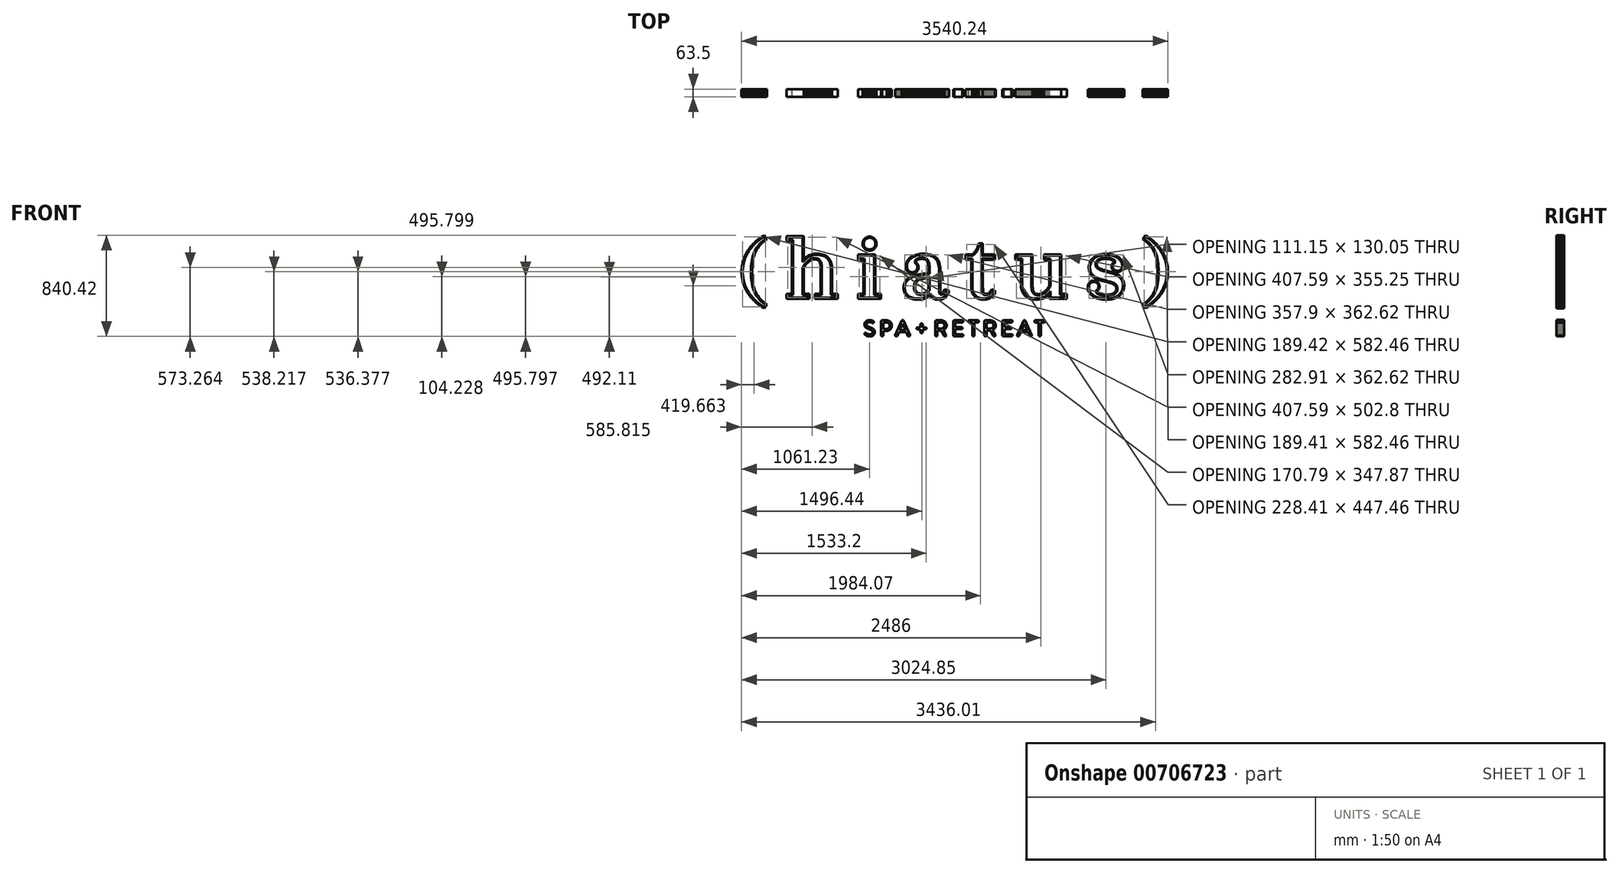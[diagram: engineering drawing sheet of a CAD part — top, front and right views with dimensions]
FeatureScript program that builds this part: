
annotation { "Feature Type Name" : "Feature", "Feature Type Description" : "" }
export const myFeature = defineFeature(function(context is Context, id is Id, definition is map)
    precondition{}
    {
        {
            var Q0;
            Q0=qCreatedBy(makeId("Front.planeOp"),FACE);
            var sketch = newSketch(context, id + "F0", { "sketchPlane" : qUnion([Q0])});
            skLineSegment(sketch, "E0", {"start": v(-2285.99, 533.4) * mm, "end": v(2285.99, 533.4) * mm});
            skLineSegment(sketch, "E1", {"start": v(2285.99, 533.4) * mm, "end": v(2285.99, -533.4) * mm});
            skLineSegment(sketch, "E2", {"start": v(2285.99, -533.4) * mm, "end": v(-2285.99, -533.4) * mm});
            skLineSegment(sketch, "E3", {"start": v(-2285.99, -533.4) * mm, "end": v(-2285.99, 533.4) * mm});
            skLineSegment(sketch, "E4", {"start": v(-1654.97, -36.78) * mm, "end": v(-1656.5, -33) * mm});
            skLineSegment(sketch, "E5", {"start": v(-1656.5, -33) * mm, "end": v(-1660.62, -21.42) * mm});
            skLineSegment(sketch, "E6", {"start": v(-1660.62, -21.42) * mm, "end": v(-1665.46, -5.14) * mm});
            skLineSegment(sketch, "E7", {"start": v(-1665.46, -5.14) * mm, "end": v(-1669.53, 12.14) * mm});
            skLineSegment(sketch, "E8", {"start": v(-1669.53, 12.14) * mm, "end": v(-1672.82, 30.5) * mm});
            skLineSegment(sketch, "E9", {"start": v(-1672.82, 30.5) * mm, "end": v(-1675.37, 50.01) * mm});
            skLineSegment(sketch, "E10", {"start": v(-1675.37, 50.01) * mm, "end": v(-1677.16, 70.78) * mm});
            skLineSegment(sketch, "E11", {"start": v(-1677.16, 70.78) * mm, "end": v(-1678.24, 92.88) * mm});
            skLineSegment(sketch, "E12", {"start": v(-1678.24, 92.88) * mm, "end": v(-1678.59, 110.52) * mm});
            skLineSegment(sketch, "E13", {"start": v(-1678.59, 110.52) * mm, "end": v(-1678.59, 116.4) * mm});
            skLineSegment(sketch, "E14", {"start": v(-1678.59, 116.4) * mm, "end": v(-1678.59, 122.28) * mm});
            skLineSegment(sketch, "E15", {"start": v(-1678.59, 122.28) * mm, "end": v(-1678.24, 139.92) * mm});
            skLineSegment(sketch, "E16", {"start": v(-1678.24, 139.92) * mm, "end": v(-1677.16, 162.02) * mm});
            skLineSegment(sketch, "E17", {"start": v(-1677.16, 162.02) * mm, "end": v(-1675.37, 182.79) * mm});
            skLineSegment(sketch, "E18", {"start": v(-1675.37, 182.79) * mm, "end": v(-1672.82, 202.3) * mm});
            skLineSegment(sketch, "E19", {"start": v(-1672.82, 202.3) * mm, "end": v(-1669.53, 220.66) * mm});
            skLineSegment(sketch, "E20", {"start": v(-1669.53, 220.66) * mm, "end": v(-1665.46, 237.93) * mm});
            skLineSegment(sketch, "E21", {"start": v(-1665.46, 237.93) * mm, "end": v(-1660.62, 254.21) * mm});
            skLineSegment(sketch, "E22", {"start": v(-1660.62, 254.21) * mm, "end": v(-1656.5, 265.78) * mm});
            skLineSegment(sketch, "E23", {"start": v(-1656.5, 265.78) * mm, "end": v(-1654.97, 269.58) * mm});
            skLineSegment(sketch, "E24", {"start": v(-1654.97, 269.58) * mm, "end": v(-1653.32, 273.65) * mm});
            skLineSegment(sketch, "E25", {"start": v(-1653.32, 273.65) * mm, "end": v(-1647.8, 285.64) * mm});
            skLineSegment(sketch, "E26", {"start": v(-1647.8, 285.64) * mm, "end": v(-1639.54, 300.96) * mm});
            skLineSegment(sketch, "E27", {"start": v(-1639.54, 300.96) * mm, "end": v(-1630.17, 315.59) * mm});
            skLineSegment(sketch, "E28", {"start": v(-1630.17, 315.59) * mm, "end": v(-1619.63, 329.58) * mm});
            skLineSegment(sketch, "E29", {"start": v(-1619.63, 329.58) * mm, "end": v(-1607.87, 343) * mm});
            skLineSegment(sketch, "E30", {"start": v(-1607.87, 343) * mm, "end": v(-1594.84, 355.9) * mm});
            skLineSegment(sketch, "E31", {"start": v(-1594.84, 355.9) * mm, "end": v(-1580.48, 368.36) * mm});
            skLineSegment(sketch, "E32", {"start": v(-1580.48, 368.36) * mm, "end": v(-1568.78, 377.52) * mm});
            skLineSegment(sketch, "E33", {"start": v(-1568.78, 377.52) * mm, "end": v(-1564.77, 380.43) * mm});
            skLineSegment(sketch, "E34", {"start": v(-1564.77, 380.43) * mm, "end": v(-1553.7, 388.45) * mm});
            skLineSegment(sketch, "E35", {"start": v(-1553.7, 388.45) * mm, "end": v(-1576.54, 420.44) * mm});
            skLineSegment(sketch, "E36", {"start": v(-1576.54, 420.44) * mm, "end": v(-1587.52, 413.6) * mm});
            skLineSegment(sketch, "E37", {"start": v(-1587.52, 413.6) * mm, "end": v(-1589.45, 412.39) * mm});
            skLineSegment(sketch, "E38", {"start": v(-1589.45, 412.39) * mm, "end": v(-1595.19, 408.71) * mm});
            skLineSegment(sketch, "E39", {"start": v(-1595.19, 408.71) * mm, "end": v(-1602.93, 403.58) * mm});
            skLineSegment(sketch, "E40", {"start": v(-1602.93, 403.58) * mm, "end": v(-1610.72, 398.2) * mm});
            skLineSegment(sketch, "E41", {"start": v(-1610.72, 398.2) * mm, "end": v(-1618.54, 392.55) * mm});
            skLineSegment(sketch, "E42", {"start": v(-1618.54, 392.55) * mm, "end": v(-1626.38, 386.65) * mm});
            skLineSegment(sketch, "E43", {"start": v(-1626.38, 386.65) * mm, "end": v(-1634.2, 380.48) * mm});
            skLineSegment(sketch, "E44", {"start": v(-1634.2, 380.48) * mm, "end": v(-1641.98, 374.05) * mm});
            skLineSegment(sketch, "E45", {"start": v(-1641.98, 374.05) * mm, "end": v(-1649.72, 367.35) * mm});
            skLineSegment(sketch, "E46", {"start": v(-1649.72, 367.35) * mm, "end": v(-1657.37, 360.37) * mm});
            skLineSegment(sketch, "E47", {"start": v(-1657.37, 360.37) * mm, "end": v(-1664.94, 353.12) * mm});
            skLineSegment(sketch, "E48", {"start": v(-1664.94, 353.12) * mm, "end": v(-1672.4, 345.59) * mm});
            skLineSegment(sketch, "E49", {"start": v(-1672.4, 345.59) * mm, "end": v(-1679.71, 337.76) * mm});
            skLineSegment(sketch, "E50", {"start": v(-1679.71, 337.76) * mm, "end": v(-1686.87, 329.66) * mm});
            skLineSegment(sketch, "E51", {"start": v(-1686.87, 329.66) * mm, "end": v(-1693.86, 321.26) * mm});
            skLineSegment(sketch, "E52", {"start": v(-1693.86, 321.26) * mm, "end": v(-1700.64, 312.57) * mm});
            skLineSegment(sketch, "E53", {"start": v(-1700.64, 312.57) * mm, "end": v(-1707.21, 303.58) * mm});
            skLineSegment(sketch, "E54", {"start": v(-1707.21, 303.58) * mm, "end": v(-1713.55, 294.29) * mm});
            skLineSegment(sketch, "E55", {"start": v(-1713.55, 294.29) * mm, "end": v(-1719.62, 284.7) * mm});
            skLineSegment(sketch, "E56", {"start": v(-1719.62, 284.7) * mm, "end": v(-1725.4, 274.8) * mm});
            skLineSegment(sketch, "E57", {"start": v(-1725.4, 274.8) * mm, "end": v(-1730.9, 264.57) * mm});
            skLineSegment(sketch, "E58", {"start": v(-1730.9, 264.57) * mm, "end": v(-1736.08, 254.04) * mm});
            skLineSegment(sketch, "E59", {"start": v(-1736.08, 254.04) * mm, "end": v(-1740.9, 243.2) * mm});
            skLineSegment(sketch, "E60", {"start": v(-1740.9, 243.2) * mm, "end": v(-1745.37, 232.02) * mm});
            skLineSegment(sketch, "E61", {"start": v(-1745.37, 232.02) * mm, "end": v(-1749.46, 220.52) * mm});
            skLineSegment(sketch, "E62", {"start": v(-1749.46, 220.52) * mm, "end": v(-1753.14, 208.7) * mm});
            skLineSegment(sketch, "E63", {"start": v(-1753.14, 208.7) * mm, "end": v(-1756.4, 196.54) * mm});
            skLineSegment(sketch, "E64", {"start": v(-1756.4, 196.54) * mm, "end": v(-1759.2, 184.04) * mm});
            skLineSegment(sketch, "E65", {"start": v(-1759.2, 184.04) * mm, "end": v(-1761.56, 171.2) * mm});
            skLineSegment(sketch, "E66", {"start": v(-1761.56, 171.2) * mm, "end": v(-1763.42, 158.03) * mm});
            skLineSegment(sketch, "E67", {"start": v(-1763.42, 158.03) * mm, "end": v(-1764.77, 144.5) * mm});
            skLineSegment(sketch, "E68", {"start": v(-1764.77, 144.5) * mm, "end": v(-1765.6, 130.63) * mm});
            skLineSegment(sketch, "E69", {"start": v(-1765.6, 130.63) * mm, "end": v(-1765.88, 119.96) * mm});
            skLineSegment(sketch, "E70", {"start": v(-1765.88, 119.96) * mm, "end": v(-1765.88, 116.4) * mm});
            skLineSegment(sketch, "E71", {"start": v(-1765.88, 116.4) * mm, "end": v(-1765.88, 112.84) * mm});
            skLineSegment(sketch, "E72", {"start": v(-1765.88, 112.84) * mm, "end": v(-1765.6, 102.17) * mm});
            skLineSegment(sketch, "E73", {"start": v(-1765.6, 102.17) * mm, "end": v(-1764.77, 88.3) * mm});
            skLineSegment(sketch, "E74", {"start": v(-1764.77, 88.3) * mm, "end": v(-1763.42, 74.77) * mm});
            skLineSegment(sketch, "E75", {"start": v(-1763.42, 74.77) * mm, "end": v(-1761.56, 61.6) * mm});
            skLineSegment(sketch, "E76", {"start": v(-1761.56, 61.6) * mm, "end": v(-1759.2, 48.76) * mm});
            skLineSegment(sketch, "E77", {"start": v(-1759.2, 48.76) * mm, "end": v(-1756.4, 36.26) * mm});
            skLineSegment(sketch, "E78", {"start": v(-1756.4, 36.26) * mm, "end": v(-1753.14, 24.1) * mm});
            skLineSegment(sketch, "E79", {"start": v(-1753.14, 24.1) * mm, "end": v(-1749.46, 12.27) * mm});
            skLineSegment(sketch, "E80", {"start": v(-1749.46, 12.27) * mm, "end": v(-1745.37, 0.78) * mm});
            skLineSegment(sketch, "E81", {"start": v(-1745.37, 0.78) * mm, "end": v(-1740.9, -10.4) * mm});
            skLineSegment(sketch, "E82", {"start": v(-1740.9, -10.4) * mm, "end": v(-1736.08, -21.25) * mm});
            skLineSegment(sketch, "E83", {"start": v(-1736.08, -21.25) * mm, "end": v(-1730.9, -31.78) * mm});
            skLineSegment(sketch, "E84", {"start": v(-1730.9, -31.78) * mm, "end": v(-1725.4, -42) * mm});
            skLineSegment(sketch, "E85", {"start": v(-1725.4, -42) * mm, "end": v(-1719.62, -51.9) * mm});
            skLineSegment(sketch, "E86", {"start": v(-1719.62, -51.9) * mm, "end": v(-1713.55, -61.5) * mm});
            skLineSegment(sketch, "E87", {"start": v(-1713.55, -61.5) * mm, "end": v(-1707.21, -70.79) * mm});
            skLineSegment(sketch, "E88", {"start": v(-1707.21, -70.79) * mm, "end": v(-1700.64, -79.78) * mm});
            skLineSegment(sketch, "E89", {"start": v(-1700.64, -79.78) * mm, "end": v(-1693.86, -88.47) * mm});
            skLineSegment(sketch, "E90", {"start": v(-1693.86, -88.47) * mm, "end": v(-1686.87, -96.87) * mm});
            skLineSegment(sketch, "E91", {"start": v(-1686.87, -96.87) * mm, "end": v(-1679.71, -104.97) * mm});
            skLineSegment(sketch, "E92", {"start": v(-1679.71, -104.97) * mm, "end": v(-1672.4, -112.8) * mm});
            skLineSegment(sketch, "E93", {"start": v(-1672.4, -112.8) * mm, "end": v(-1664.94, -120.32) * mm});
            skLineSegment(sketch, "E94", {"start": v(-1664.94, -120.32) * mm, "end": v(-1657.37, -127.58) * mm});
            skLineSegment(sketch, "E95", {"start": v(-1657.37, -127.58) * mm, "end": v(-1649.72, -134.56) * mm});
            skLineSegment(sketch, "E96", {"start": v(-1649.72, -134.56) * mm, "end": v(-1641.98, -141.26) * mm});
            skLineSegment(sketch, "E97", {"start": v(-1641.98, -141.26) * mm, "end": v(-1634.2, -147.7) * mm});
            skLineSegment(sketch, "E98", {"start": v(-1634.2, -147.7) * mm, "end": v(-1626.38, -153.86) * mm});
            skLineSegment(sketch, "E99", {"start": v(-1626.38, -153.86) * mm, "end": v(-1618.54, -159.76) * mm});
            skLineSegment(sketch, "E100", {"start": v(-1618.54, -159.76) * mm, "end": v(-1610.72, -165.4) * mm});
            skLineSegment(sketch, "E101", {"start": v(-1610.72, -165.4) * mm, "end": v(-1602.93, -170.79) * mm});
            skLineSegment(sketch, "E102", {"start": v(-1602.93, -170.79) * mm, "end": v(-1595.19, -175.92) * mm});
            skLineSegment(sketch, "E103", {"start": v(-1595.19, -175.92) * mm, "end": v(-1589.45, -179.6) * mm});
            skLineSegment(sketch, "E104", {"start": v(-1589.45, -179.6) * mm, "end": v(-1587.52, -180.8) * mm});
            skLineSegment(sketch, "E105", {"start": v(-1587.52, -180.8) * mm, "end": v(-1576.54, -187.65) * mm});
            skLineSegment(sketch, "E106", {"start": v(-1576.54, -187.65) * mm, "end": v(-1553.7, -155.66) * mm});
            skLineSegment(sketch, "E107", {"start": v(-1553.7, -155.66) * mm, "end": v(-1564.77, -147.64) * mm});
            skLineSegment(sketch, "E108", {"start": v(-1564.77, -147.64) * mm, "end": v(-1568.78, -144.73) * mm});
            skLineSegment(sketch, "E109", {"start": v(-1568.78, -144.73) * mm, "end": v(-1580.48, -135.57) * mm});
            skLineSegment(sketch, "E110", {"start": v(-1580.48, -135.57) * mm, "end": v(-1594.84, -123.11) * mm});
            skLineSegment(sketch, "E111", {"start": v(-1594.84, -123.11) * mm, "end": v(-1607.87, -110.2) * mm});
            skLineSegment(sketch, "E112", {"start": v(-1607.87, -110.2) * mm, "end": v(-1619.63, -96.78) * mm});
            skLineSegment(sketch, "E113", {"start": v(-1619.63, -96.78) * mm, "end": v(-1630.17, -82.8) * mm});
            skLineSegment(sketch, "E114", {"start": v(-1630.17, -82.8) * mm, "end": v(-1639.54, -68.17) * mm});
            skLineSegment(sketch, "E115", {"start": v(-1639.54, -68.17) * mm, "end": v(-1647.8, -52.86) * mm});
            skLineSegment(sketch, "E116", {"start": v(-1647.8, -52.86) * mm, "end": v(-1653.32, -40.86) * mm});
            skLineSegment(sketch, "E117", {"start": v(-1653.32, -40.86) * mm, "end": v(-1654.97, -36.78) * mm});
            skLineSegment(sketch, "E118", {"start": v(-1013.22, 127.47) * mm, "end": v(-1013.22, 131.72) * mm});
            skLineSegment(sketch, "E119", {"start": v(-1013.22, 131.72) * mm, "end": v(-1013.71, 144.47) * mm});
            skLineSegment(sketch, "E120", {"start": v(-1013.71, 144.47) * mm, "end": v(-1015.2, 160.34) * mm});
            skLineSegment(sketch, "E121", {"start": v(-1015.2, 160.34) * mm, "end": v(-1017.68, 175.1) * mm});
            skLineSegment(sketch, "E122", {"start": v(-1017.68, 175.1) * mm, "end": v(-1021.16, 188.72) * mm});
            skLineSegment(sketch, "E123", {"start": v(-1021.16, 188.72) * mm, "end": v(-1025.64, 201.25) * mm});
            skLineSegment(sketch, "E124", {"start": v(-1025.64, 201.25) * mm, "end": v(-1031.13, 212.66) * mm});
            skLineSegment(sketch, "E125", {"start": v(-1031.13, 212.66) * mm, "end": v(-1037.62, 222.97) * mm});
            skLineSegment(sketch, "E126", {"start": v(-1037.62, 222.97) * mm, "end": v(-1045.13, 232.18) * mm});
            skLineSegment(sketch, "E127", {"start": v(-1045.13, 232.18) * mm, "end": v(-1053.66, 240.29) * mm});
            skLineSegment(sketch, "E128", {"start": v(-1053.66, 240.29) * mm, "end": v(-1063.2, 247.3) * mm});
            skLineSegment(sketch, "E129", {"start": v(-1063.2, 247.3) * mm, "end": v(-1073.76, 253.24) * mm});
            skLineSegment(sketch, "E130", {"start": v(-1073.76, 253.24) * mm, "end": v(-1085.36, 258.07) * mm});
            skLineSegment(sketch, "E131", {"start": v(-1085.36, 258.07) * mm, "end": v(-1097.98, 261.83) * mm});
            skLineSegment(sketch, "E132", {"start": v(-1097.98, 261.83) * mm, "end": v(-1111.64, 264.5) * mm});
            skLineSegment(sketch, "E133", {"start": v(-1111.64, 264.5) * mm, "end": v(-1126.33, 266.12) * mm});
            skLineSegment(sketch, "E134", {"start": v(-1126.33, 266.12) * mm, "end": v(-1138.13, 266.65) * mm});
            skLineSegment(sketch, "E135", {"start": v(-1138.13, 266.65) * mm, "end": v(-1142.07, 266.65) * mm});
            skLineSegment(sketch, "E136", {"start": v(-1142.07, 266.65) * mm, "end": v(-1144.32, 266.65) * mm});
            skLineSegment(sketch, "E137", {"start": v(-1144.32, 266.65) * mm, "end": v(-1151.08, 266.4) * mm});
            skLineSegment(sketch, "E138", {"start": v(-1151.08, 266.4) * mm, "end": v(-1159.76, 265.7) * mm});
            skLineSegment(sketch, "E139", {"start": v(-1159.76, 265.7) * mm, "end": v(-1168.12, 264.55) * mm});
            skLineSegment(sketch, "E140", {"start": v(-1168.12, 264.55) * mm, "end": v(-1176.17, 262.98) * mm});
            skLineSegment(sketch, "E141", {"start": v(-1176.17, 262.98) * mm, "end": v(-1183.91, 261.02) * mm});
            skLineSegment(sketch, "E142", {"start": v(-1183.91, 261.02) * mm, "end": v(-1191.35, 258.7) * mm});
            skLineSegment(sketch, "E143", {"start": v(-1191.35, 258.7) * mm, "end": v(-1198.48, 256.03) * mm});
            skLineSegment(sketch, "E144", {"start": v(-1198.48, 256.03) * mm, "end": v(-1205.32, 253.05) * mm});
            skLineSegment(sketch, "E145", {"start": v(-1205.32, 253.05) * mm, "end": v(-1211.88, 249.77) * mm});
            skLineSegment(sketch, "E146", {"start": v(-1211.88, 249.77) * mm, "end": v(-1218.14, 246.22) * mm});
            skLineSegment(sketch, "E147", {"start": v(-1218.14, 246.22) * mm, "end": v(-1224.13, 242.44) * mm});
            skLineSegment(sketch, "E148", {"start": v(-1224.13, 242.44) * mm, "end": v(-1229.84, 238.43) * mm});
            skLineSegment(sketch, "E149", {"start": v(-1229.84, 238.43) * mm, "end": v(-1235.28, 234.24) * mm});
            skLineSegment(sketch, "E150", {"start": v(-1235.28, 234.24) * mm, "end": v(-1240.46, 229.87) * mm});
            skLineSegment(sketch, "E151", {"start": v(-1240.46, 229.87) * mm, "end": v(-1245.37, 225.37) * mm});
            skLineSegment(sketch, "E152", {"start": v(-1245.37, 225.37) * mm, "end": v(-1248.89, 221.93) * mm});
            skLineSegment(sketch, "E153", {"start": v(-1248.89, 221.93) * mm, "end": v(-1250.03, 220.75) * mm});
            skLineSegment(sketch, "E154", {"start": v(-1250.03, 220.75) * mm, "end": v(-1250.03, 414.2) * mm});
            skLineSegment(sketch, "E155", {"start": v(-1250.03, 414.2) * mm, "end": v(-1393.39, 414.2) * mm});
            skLineSegment(sketch, "E156", {"start": v(-1393.39, 414.2) * mm, "end": v(-1393.39, 371.91) * mm});
            skLineSegment(sketch, "E157", {"start": v(-1393.39, 371.91) * mm, "end": v(-1346.91, 371.91) * mm});
            skLineSegment(sketch, "E158", {"start": v(-1346.91, 371.91) * mm, "end": v(-1346.91, -65.34) * mm});
            skLineSegment(sketch, "E159", {"start": v(-1346.91, -65.34) * mm, "end": v(-1393.39, -65.34) * mm});
            skLineSegment(sketch, "E160", {"start": v(-1393.39, -65.34) * mm, "end": v(-1393.39, -107.64) * mm});
            skLineSegment(sketch, "E161", {"start": v(-1393.39, -107.64) * mm, "end": v(-1203.55, -107.64) * mm});
            skLineSegment(sketch, "E162", {"start": v(-1203.55, -107.64) * mm, "end": v(-1203.55, -65.34) * mm});
            skLineSegment(sketch, "E163", {"start": v(-1203.55, -65.34) * mm, "end": v(-1250.03, -65.34) * mm});
            skLineSegment(sketch, "E164", {"start": v(-1250.03, -65.34) * mm, "end": v(-1250.03, 149.07) * mm});
            skLineSegment(sketch, "E165", {"start": v(-1250.03, 149.07) * mm, "end": v(-1249.29, 150.43) * mm});
            skLineSegment(sketch, "E166", {"start": v(-1249.29, 150.43) * mm, "end": v(-1246.99, 154.45) * mm});
            skLineSegment(sketch, "E167", {"start": v(-1246.99, 154.45) * mm, "end": v(-1243.58, 160.1) * mm});
            skLineSegment(sketch, "E168", {"start": v(-1243.58, 160.1) * mm, "end": v(-1239.82, 165.93) * mm});
            skLineSegment(sketch, "E169", {"start": v(-1239.82, 165.93) * mm, "end": v(-1235.69, 171.87) * mm});
            skLineSegment(sketch, "E170", {"start": v(-1235.69, 171.87) * mm, "end": v(-1231.2, 177.83) * mm});
            skLineSegment(sketch, "E171", {"start": v(-1231.2, 177.83) * mm, "end": v(-1226.37, 183.7) * mm});
            skLineSegment(sketch, "E172", {"start": v(-1226.37, 183.7) * mm, "end": v(-1221.18, 189.44) * mm});
            skLineSegment(sketch, "E173", {"start": v(-1221.18, 189.44) * mm, "end": v(-1215.64, 194.93) * mm});
            skLineSegment(sketch, "E174", {"start": v(-1215.64, 194.93) * mm, "end": v(-1209.76, 200.09) * mm});
            skLineSegment(sketch, "E175", {"start": v(-1209.76, 200.09) * mm, "end": v(-1203.53, 204.84) * mm});
            skLineSegment(sketch, "E176", {"start": v(-1203.53, 204.84) * mm, "end": v(-1196.95, 209.1) * mm});
            skLineSegment(sketch, "E177", {"start": v(-1196.95, 209.1) * mm, "end": v(-1190.04, 212.77) * mm});
            skLineSegment(sketch, "E178", {"start": v(-1190.04, 212.77) * mm, "end": v(-1182.79, 215.77) * mm});
            skLineSegment(sketch, "E179", {"start": v(-1182.79, 215.77) * mm, "end": v(-1175.2, 218.02) * mm});
            skLineSegment(sketch, "E180", {"start": v(-1175.2, 218.02) * mm, "end": v(-1167.29, 219.44) * mm});
            skLineSegment(sketch, "E181", {"start": v(-1167.29, 219.44) * mm, "end": v(-1161.1, 219.93) * mm});
            skLineSegment(sketch, "E182", {"start": v(-1161.1, 219.93) * mm, "end": v(-1159.04, 219.93) * mm});
            skLineSegment(sketch, "E183", {"start": v(-1159.04, 219.93) * mm, "end": v(-1157.7, 219.93) * mm});
            skLineSegment(sketch, "E184", {"start": v(-1157.7, 219.93) * mm, "end": v(-1153.65, 219.78) * mm});
            skLineSegment(sketch, "E185", {"start": v(-1153.65, 219.78) * mm, "end": v(-1148.5, 219.31) * mm});
            skLineSegment(sketch, "E186", {"start": v(-1148.5, 219.31) * mm, "end": v(-1143.62, 218.47) * mm});
            skLineSegment(sketch, "E187", {"start": v(-1143.62, 218.47) * mm, "end": v(-1139, 217.2) * mm});
            skLineSegment(sketch, "E188", {"start": v(-1139, 217.2) * mm, "end": v(-1134.67, 215.47) * mm});
            skLineSegment(sketch, "E189", {"start": v(-1134.67, 215.47) * mm, "end": v(-1130.65, 213.21) * mm});
            skLineSegment(sketch, "E190", {"start": v(-1130.65, 213.21) * mm, "end": v(-1126.94, 210.38) * mm});
            skLineSegment(sketch, "E191", {"start": v(-1126.94, 210.38) * mm, "end": v(-1123.56, 206.93) * mm});
            skLineSegment(sketch, "E192", {"start": v(-1123.56, 206.93) * mm, "end": v(-1120.52, 202.81) * mm});
            skLineSegment(sketch, "E193", {"start": v(-1120.52, 202.81) * mm, "end": v(-1117.84, 197.98) * mm});
            skLineSegment(sketch, "E194", {"start": v(-1117.84, 197.98) * mm, "end": v(-1115.54, 192.37) * mm});
            skLineSegment(sketch, "E195", {"start": v(-1115.54, 192.37) * mm, "end": v(-1113.62, 185.94) * mm});
            skLineSegment(sketch, "E196", {"start": v(-1113.62, 185.94) * mm, "end": v(-1112.1, 178.65) * mm});
            skLineSegment(sketch, "E197", {"start": v(-1112.1, 178.65) * mm, "end": v(-1111, 170.44) * mm});
            skLineSegment(sketch, "E198", {"start": v(-1111, 170.44) * mm, "end": v(-1110.33, 161.26) * mm});
            skLineSegment(sketch, "E199", {"start": v(-1110.33, 161.26) * mm, "end": v(-1110.1, 153.62) * mm});
            skLineSegment(sketch, "E200", {"start": v(-1110.1, 153.62) * mm, "end": v(-1110.1, 151.07) * mm});
            skLineSegment(sketch, "E201", {"start": v(-1110.1, 151.07) * mm, "end": v(-1110.1, -65.34) * mm});
            skLineSegment(sketch, "E202", {"start": v(-1110.1, -65.34) * mm, "end": v(-1157.32, -65.34) * mm});
            skLineSegment(sketch, "E203", {"start": v(-1157.32, -65.34) * mm, "end": v(-1157.32, -107.64) * mm});
            skLineSegment(sketch, "E204", {"start": v(-1157.32, -107.64) * mm, "end": v(-966.75, -107.64) * mm});
            skLineSegment(sketch, "E205", {"start": v(-966.75, -107.64) * mm, "end": v(-966.75, -65.34) * mm});
            skLineSegment(sketch, "E206", {"start": v(-966.75, -65.34) * mm, "end": v(-1013.22, -65.34) * mm});
            skLineSegment(sketch, "E207", {"start": v(-1013.22, -65.34) * mm, "end": v(-1013.22, 127.47) * mm});
            skLineSegment(sketch, "E208", {"start": v(-656.21, 259.28) * mm, "end": v(-799.57, 259.28) * mm});
            skLineSegment(sketch, "E209", {"start": v(-799.57, 259.28) * mm, "end": v(-799.57, 216.98) * mm});
            skLineSegment(sketch, "E210", {"start": v(-799.57, 216.98) * mm, "end": v(-753.1, 216.98) * mm});
            skLineSegment(sketch, "E211", {"start": v(-753.1, 216.98) * mm, "end": v(-753.1, -65.34) * mm});
            skLineSegment(sketch, "E212", {"start": v(-753.1, -65.34) * mm, "end": v(-799.57, -65.34) * mm});
            skLineSegment(sketch, "E213", {"start": v(-799.57, -65.34) * mm, "end": v(-799.57, -107.64) * mm});
            skLineSegment(sketch, "E214", {"start": v(-799.57, -107.64) * mm, "end": v(-609.73, -107.64) * mm});
            skLineSegment(sketch, "E215", {"start": v(-609.73, -107.64) * mm, "end": v(-609.73, -65.34) * mm});
            skLineSegment(sketch, "E216", {"start": v(-609.73, -65.34) * mm, "end": v(-656.21, -65.34) * mm});
            skLineSegment(sketch, "E217", {"start": v(-656.21, -65.34) * mm, "end": v(-656.21, 259.28) * mm});
            skLineSegment(sketch, "E218", {"start": v(-702.44, 292.23) * mm, "end": v(-700.98, 292.23) * mm});
            skLineSegment(sketch, "E219", {"start": v(-700.98, 292.23) * mm, "end": v(-696.59, 292.53) * mm});
            skLineSegment(sketch, "E220", {"start": v(-696.59, 292.53) * mm, "end": v(-690.9, 293.41) * mm});
            skLineSegment(sketch, "E221", {"start": v(-690.9, 293.41) * mm, "end": v(-685.42, 294.85) * mm});
            skLineSegment(sketch, "E222", {"start": v(-685.42, 294.85) * mm, "end": v(-680.15, 296.8) * mm});
            skLineSegment(sketch, "E223", {"start": v(-680.15, 296.8) * mm, "end": v(-675.15, 299.25) * mm});
            skLineSegment(sketch, "E224", {"start": v(-675.15, 299.25) * mm, "end": v(-670.43, 302.16) * mm});
            skLineSegment(sketch, "E225", {"start": v(-670.43, 302.16) * mm, "end": v(-666.01, 305.5) * mm});
            skLineSegment(sketch, "E226", {"start": v(-666.01, 305.5) * mm, "end": v(-661.94, 309.25) * mm});
            skLineSegment(sketch, "E227", {"start": v(-661.94, 309.25) * mm, "end": v(-658.24, 313.37) * mm});
            skLineSegment(sketch, "E228", {"start": v(-658.24, 313.37) * mm, "end": v(-654.94, 317.84) * mm});
            skLineSegment(sketch, "E229", {"start": v(-654.94, 317.84) * mm, "end": v(-652.06, 322.63) * mm});
            skLineSegment(sketch, "E230", {"start": v(-652.06, 322.63) * mm, "end": v(-649.65, 327.7) * mm});
            skLineSegment(sketch, "E231", {"start": v(-649.65, 327.7) * mm, "end": v(-647.72, 333.03) * mm});
            skLineSegment(sketch, "E232", {"start": v(-647.72, 333.03) * mm, "end": v(-646.3, 338.58) * mm});
            skLineSegment(sketch, "E233", {"start": v(-646.3, 338.58) * mm, "end": v(-645.43, 344.34) * mm});
            skLineSegment(sketch, "E234", {"start": v(-645.43, 344.34) * mm, "end": v(-645.14, 348.79) * mm});
            skLineSegment(sketch, "E235", {"start": v(-645.14, 348.79) * mm, "end": v(-645.14, 350.27) * mm});
            skLineSegment(sketch, "E236", {"start": v(-645.14, 350.27) * mm, "end": v(-645.14, 351.8) * mm});
            skLineSegment(sketch, "E237", {"start": v(-645.14, 351.8) * mm, "end": v(-645.43, 356.36) * mm});
            skLineSegment(sketch, "E238", {"start": v(-645.43, 356.36) * mm, "end": v(-646.29, 362.25) * mm});
            skLineSegment(sketch, "E239", {"start": v(-646.29, 362.25) * mm, "end": v(-647.67, 367.93) * mm});
            skLineSegment(sketch, "E240", {"start": v(-647.67, 367.93) * mm, "end": v(-649.57, 373.35) * mm});
            skLineSegment(sketch, "E241", {"start": v(-649.57, 373.35) * mm, "end": v(-651.96, 378.5) * mm});
            skLineSegment(sketch, "E242", {"start": v(-651.96, 378.5) * mm, "end": v(-654.8, 383.35) * mm});
            skLineSegment(sketch, "E243", {"start": v(-654.8, 383.35) * mm, "end": v(-658.07, 387.86) * mm});
            skLineSegment(sketch, "E244", {"start": v(-658.07, 387.86) * mm, "end": v(-661.74, 392.01) * mm});
            skLineSegment(sketch, "E245", {"start": v(-661.74, 392.01) * mm, "end": v(-665.8, 395.78) * mm});
            skLineSegment(sketch, "E246", {"start": v(-665.8, 395.78) * mm, "end": v(-670.19, 399.14) * mm});
            skLineSegment(sketch, "E247", {"start": v(-670.19, 399.14) * mm, "end": v(-674.91, 402.05) * mm});
            skLineSegment(sketch, "E248", {"start": v(-674.91, 402.05) * mm, "end": v(-679.93, 404.5) * mm});
            skLineSegment(sketch, "E249", {"start": v(-679.93, 404.5) * mm, "end": v(-685.22, 406.45) * mm});
            skLineSegment(sketch, "E250", {"start": v(-685.22, 406.45) * mm, "end": v(-690.75, 407.87) * mm});
            skLineSegment(sketch, "E251", {"start": v(-690.75, 407.87) * mm, "end": v(-696.5, 408.75) * mm});
            skLineSegment(sketch, "E252", {"start": v(-696.5, 408.75) * mm, "end": v(-700.95, 409.04) * mm});
            skLineSegment(sketch, "E253", {"start": v(-700.95, 409.04) * mm, "end": v(-702.44, 409.04) * mm});
            skLineSegment(sketch, "E254", {"start": v(-702.44, 409.04) * mm, "end": v(-703.96, 409.04) * mm});
            skLineSegment(sketch, "E255", {"start": v(-703.96, 409.04) * mm, "end": v(-708.52, 408.74) * mm});
            skLineSegment(sketch, "E256", {"start": v(-708.52, 408.74) * mm, "end": v(-714.42, 407.85) * mm});
            skLineSegment(sketch, "E257", {"start": v(-714.42, 407.85) * mm, "end": v(-720.11, 406.4) * mm});
            skLineSegment(sketch, "E258", {"start": v(-720.11, 406.4) * mm, "end": v(-725.58, 404.42) * mm});
            skLineSegment(sketch, "E259", {"start": v(-725.58, 404.42) * mm, "end": v(-730.78, 401.94) * mm});
            skLineSegment(sketch, "E260", {"start": v(-730.78, 401.94) * mm, "end": v(-735.69, 399) * mm});
            skLineSegment(sketch, "E261", {"start": v(-735.69, 399) * mm, "end": v(-740.27, 395.6) * mm});
            skLineSegment(sketch, "E262", {"start": v(-740.27, 395.6) * mm, "end": v(-744.5, 391.81) * mm});
            skLineSegment(sketch, "E263", {"start": v(-744.5, 391.81) * mm, "end": v(-748.34, 387.63) * mm});
            skLineSegment(sketch, "E264", {"start": v(-748.34, 387.63) * mm, "end": v(-751.77, 383.1) * mm});
            skLineSegment(sketch, "E265", {"start": v(-751.77, 383.1) * mm, "end": v(-754.75, 378.26) * mm});
            skLineSegment(sketch, "E266", {"start": v(-754.75, 378.26) * mm, "end": v(-757.26, 373.12) * mm});
            skLineSegment(sketch, "E267", {"start": v(-757.26, 373.12) * mm, "end": v(-759.26, 367.73) * mm});
            skLineSegment(sketch, "E268", {"start": v(-759.26, 367.73) * mm, "end": v(-760.73, 362.1) * mm});
            skLineSegment(sketch, "E269", {"start": v(-760.73, 362.1) * mm, "end": v(-761.64, 356.27) * mm});
            skLineSegment(sketch, "E270", {"start": v(-761.64, 356.27) * mm, "end": v(-761.94, 351.76) * mm});
            skLineSegment(sketch, "E271", {"start": v(-761.94, 351.76) * mm, "end": v(-761.94, 350.27) * mm});
            skLineSegment(sketch, "E272", {"start": v(-761.94, 350.27) * mm, "end": v(-761.94, 348.79) * mm});
            skLineSegment(sketch, "E273", {"start": v(-761.94, 348.79) * mm, "end": v(-761.64, 344.34) * mm});
            skLineSegment(sketch, "E274", {"start": v(-761.64, 344.34) * mm, "end": v(-760.73, 338.58) * mm});
            skLineSegment(sketch, "E275", {"start": v(-760.73, 338.58) * mm, "end": v(-759.26, 333.03) * mm});
            skLineSegment(sketch, "E276", {"start": v(-759.26, 333.03) * mm, "end": v(-757.26, 327.7) * mm});
            skLineSegment(sketch, "E277", {"start": v(-757.26, 327.7) * mm, "end": v(-754.75, 322.63) * mm});
            skLineSegment(sketch, "E278", {"start": v(-754.75, 322.63) * mm, "end": v(-751.77, 317.84) * mm});
            skLineSegment(sketch, "E279", {"start": v(-751.77, 317.84) * mm, "end": v(-748.34, 313.37) * mm});
            skLineSegment(sketch, "E280", {"start": v(-748.34, 313.37) * mm, "end": v(-744.5, 309.25) * mm});
            skLineSegment(sketch, "E281", {"start": v(-744.5, 309.25) * mm, "end": v(-740.27, 305.5) * mm});
            skLineSegment(sketch, "E282", {"start": v(-740.27, 305.5) * mm, "end": v(-735.69, 302.16) * mm});
            skLineSegment(sketch, "E283", {"start": v(-735.69, 302.16) * mm, "end": v(-730.78, 299.25) * mm});
            skLineSegment(sketch, "E284", {"start": v(-730.78, 299.25) * mm, "end": v(-725.58, 296.8) * mm});
            skLineSegment(sketch, "E285", {"start": v(-725.58, 296.8) * mm, "end": v(-720.11, 294.85) * mm});
            skLineSegment(sketch, "E286", {"start": v(-720.11, 294.85) * mm, "end": v(-714.42, 293.41) * mm});
            skLineSegment(sketch, "E287", {"start": v(-714.42, 293.41) * mm, "end": v(-708.52, 292.53) * mm});
            skLineSegment(sketch, "E288", {"start": v(-708.52, 292.53) * mm, "end": v(-703.96, 292.23) * mm});
            skLineSegment(sketch, "E289", {"start": v(-703.96, 292.23) * mm, "end": v(-702.44, 292.23) * mm});
            skLineSegment(sketch, "E290", {"start": v(-213.86, -33.04) * mm, "end": v(-215.78, -35.4) * mm});
            skLineSegment(sketch, "E291", {"start": v(-215.78, -35.4) * mm, "end": v(-222.04, -42.06) * mm});
            skLineSegment(sketch, "E292", {"start": v(-222.04, -42.06) * mm, "end": v(-230.25, -49.3) * mm});
            skLineSegment(sketch, "E293", {"start": v(-230.25, -49.3) * mm, "end": v(-238.4, -54.94) * mm});
            skLineSegment(sketch, "E294", {"start": v(-238.4, -54.94) * mm, "end": v(-246.39, -59.16) * mm});
            skLineSegment(sketch, "E295", {"start": v(-246.39, -59.16) * mm, "end": v(-254.1, -62.13) * mm});
            skLineSegment(sketch, "E296", {"start": v(-254.1, -62.13) * mm, "end": v(-261.44, -64.04) * mm});
            skLineSegment(sketch, "E297", {"start": v(-261.44, -64.04) * mm, "end": v(-268.31, -65.05) * mm});
            skLineSegment(sketch, "E298", {"start": v(-268.31, -65.05) * mm, "end": v(-273.03, -65.34) * mm});
            skLineSegment(sketch, "E299", {"start": v(-273.03, -65.34) * mm, "end": v(-274.6, -65.34) * mm});
            skLineSegment(sketch, "E300", {"start": v(-274.6, -65.34) * mm, "end": v(-276.18, -65.34) * mm});
            skLineSegment(sketch, "E301", {"start": v(-276.18, -65.34) * mm, "end": v(-280.9, -65.15) * mm});
            skLineSegment(sketch, "E302", {"start": v(-280.9, -65.15) * mm, "end": v(-286.78, -64.54) * mm});
            skLineSegment(sketch, "E303", {"start": v(-286.78, -64.54) * mm, "end": v(-292.2, -63.54) * mm});
            skLineSegment(sketch, "E304", {"start": v(-292.2, -63.54) * mm, "end": v(-297.19, -62.11) * mm});
            skLineSegment(sketch, "E305", {"start": v(-297.19, -62.11) * mm, "end": v(-301.74, -60.26) * mm});
            skLineSegment(sketch, "E306", {"start": v(-301.74, -60.26) * mm, "end": v(-305.87, -58) * mm});
            skLineSegment(sketch, "E307", {"start": v(-305.87, -58) * mm, "end": v(-309.59, -55.3) * mm});
            skLineSegment(sketch, "E308", {"start": v(-309.59, -55.3) * mm, "end": v(-312.89, -52.14) * mm});
            skLineSegment(sketch, "E309", {"start": v(-312.89, -52.14) * mm, "end": v(-315.77, -48.56) * mm});
            skLineSegment(sketch, "E310", {"start": v(-315.77, -48.56) * mm, "end": v(-318.26, -44.52) * mm});
            skLineSegment(sketch, "E311", {"start": v(-318.26, -44.52) * mm, "end": v(-320.35, -40.02) * mm});
            skLineSegment(sketch, "E312", {"start": v(-320.35, -40.02) * mm, "end": v(-322.04, -35.07) * mm});
            skLineSegment(sketch, "E313", {"start": v(-322.04, -35.07) * mm, "end": v(-323.35, -29.65) * mm});
            skLineSegment(sketch, "E314", {"start": v(-323.35, -29.65) * mm, "end": v(-324.28, -23.75) * mm});
            skLineSegment(sketch, "E315", {"start": v(-324.28, -23.75) * mm, "end": v(-324.83, -17.37) * mm});
            skLineSegment(sketch, "E316", {"start": v(-324.83, -17.37) * mm, "end": v(-325.02, -12.22) * mm});
            skLineSegment(sketch, "E317", {"start": v(-325.02, -12.22) * mm, "end": v(-325.02, -10.5) * mm});
            skLineSegment(sketch, "E318", {"start": v(-325.02, -10.5) * mm, "end": v(-325.02, -8.47) * mm});
            skLineSegment(sketch, "E319", {"start": v(-325.02, -8.47) * mm, "end": v(-324.77, -2.36) * mm});
            skLineSegment(sketch, "E320", {"start": v(-324.77, -2.36) * mm, "end": v(-324, 5.19) * mm});
            skLineSegment(sketch, "E321", {"start": v(-324, 5.19) * mm, "end": v(-322.7, 12.18) * mm});
            skLineSegment(sketch, "E322", {"start": v(-322.7, 12.18) * mm, "end": v(-320.83, 18.63) * mm});
            skLineSegment(sketch, "E323", {"start": v(-320.83, 18.63) * mm, "end": v(-318.39, 24.55) * mm});
            skLineSegment(sketch, "E324", {"start": v(-318.39, 24.55) * mm, "end": v(-315.34, 29.96) * mm});
            skLineSegment(sketch, "E325", {"start": v(-315.34, 29.96) * mm, "end": v(-311.68, 34.9) * mm});
            skLineSegment(sketch, "E326", {"start": v(-311.68, 34.9) * mm, "end": v(-307.36, 39.37) * mm});
            skLineSegment(sketch, "E327", {"start": v(-307.36, 39.37) * mm, "end": v(-302.39, 43.39) * mm});
            skLineSegment(sketch, "E328", {"start": v(-302.39, 43.39) * mm, "end": v(-296.72, 46.98) * mm});
            skLineSegment(sketch, "E329", {"start": v(-296.72, 46.98) * mm, "end": v(-290.35, 50.17) * mm});
            skLineSegment(sketch, "E330", {"start": v(-290.35, 50.17) * mm, "end": v(-283.25, 52.97) * mm});
            skLineSegment(sketch, "E331", {"start": v(-283.25, 52.97) * mm, "end": v(-275.4, 55.4) * mm});
            skLineSegment(sketch, "E332", {"start": v(-275.4, 55.4) * mm, "end": v(-266.78, 57.48) * mm});
            skLineSegment(sketch, "E333", {"start": v(-266.78, 57.48) * mm, "end": v(-257.36, 59.23) * mm});
            skLineSegment(sketch, "E334", {"start": v(-257.36, 59.23) * mm, "end": v(-249.7, 60.36) * mm});
            skLineSegment(sketch, "E335", {"start": v(-249.7, 60.36) * mm, "end": v(-247.13, 60.68) * mm});
            skLineSegment(sketch, "E336", {"start": v(-247.13, 60.68) * mm, "end": v(-213.86, 64.7) * mm});
            skLineSegment(sketch, "E337", {"start": v(-213.86, 64.7) * mm, "end": v(-213.86, -33.04) * mm});
            skLineSegment(sketch, "E338", {"start": v(-86.3, -40.21) * mm, "end": v(-86.93, -42.13) * mm});
            skLineSegment(sketch, "E339", {"start": v(-86.93, -42.13) * mm, "end": v(-89.1, -47.77) * mm});
            skLineSegment(sketch, "E340", {"start": v(-89.1, -47.77) * mm, "end": v(-91.9, -53.46) * mm});
            skLineSegment(sketch, "E341", {"start": v(-91.9, -53.46) * mm, "end": v(-94.66, -57.53) * mm});
            skLineSegment(sketch, "E342", {"start": v(-94.66, -57.53) * mm, "end": v(-97.3, -60.26) * mm});
            skLineSegment(sketch, "E343", {"start": v(-97.3, -60.26) * mm, "end": v(-99.79, -61.92) * mm});
            skLineSegment(sketch, "E344", {"start": v(-99.79, -61.92) * mm, "end": v(-102.04, -62.77) * mm});
            skLineSegment(sketch, "E345", {"start": v(-102.04, -62.77) * mm, "end": v(-104.03, -63.08) * mm});
            skLineSegment(sketch, "E346", {"start": v(-104.03, -63.08) * mm, "end": v(-105.26, -63.13) * mm});
            skLineSegment(sketch, "E347", {"start": v(-105.26, -63.13) * mm, "end": v(-105.67, -63.13) * mm});
            skLineSegment(sketch, "E348", {"start": v(-105.67, -63.13) * mm, "end": v(-106.42, -63.13) * mm});
            skLineSegment(sketch, "E349", {"start": v(-106.42, -63.13) * mm, "end": v(-108.68, -62.84) * mm});
            skLineSegment(sketch, "E350", {"start": v(-108.68, -62.84) * mm, "end": v(-110.7, -62.07) * mm});
            skLineSegment(sketch, "E351", {"start": v(-110.7, -62.07) * mm, "end": v(-112.04, -60.92) * mm});
            skLineSegment(sketch, "E352", {"start": v(-112.04, -60.92) * mm, "end": v(-112.79, -59.9) * mm});
            skLineSegment(sketch, "E353", {"start": v(-112.79, -59.9) * mm, "end": v(-113, -59.53) * mm});
            skLineSegment(sketch, "E354", {"start": v(-113, -59.53) * mm, "end": v(-113.2, -59.21) * mm});
            skLineSegment(sketch, "E355", {"start": v(-113.2, -59.21) * mm, "end": v(-113.7, -58.22) * mm});
            skLineSegment(sketch, "E356", {"start": v(-113.7, -58.22) * mm, "end": v(-114.39, -56.54) * mm});
            skLineSegment(sketch, "E357", {"start": v(-114.39, -56.54) * mm, "end": v(-115.05, -54.45) * mm});
            skLineSegment(sketch, "E358", {"start": v(-115.05, -54.45) * mm, "end": v(-115.66, -51.9) * mm});
            skLineSegment(sketch, "E359", {"start": v(-115.66, -51.9) * mm, "end": v(-116.2, -48.87) * mm});
            skLineSegment(sketch, "E360", {"start": v(-116.2, -48.87) * mm, "end": v(-116.6, -45.29) * mm});
            skLineSegment(sketch, "E361", {"start": v(-116.6, -45.29) * mm, "end": v(-116.87, -41.11) * mm});
            skLineSegment(sketch, "E362", {"start": v(-116.87, -41.11) * mm, "end": v(-116.97, -37.52) * mm});
            skLineSegment(sketch, "E363", {"start": v(-116.97, -37.52) * mm, "end": v(-116.97, -36.32) * mm});
            skLineSegment(sketch, "E364", {"start": v(-116.97, -36.32) * mm, "end": v(-116.97, 131.89) * mm});
            skLineSegment(sketch, "E365", {"start": v(-116.97, 131.89) * mm, "end": v(-116.97, 136.19) * mm});
            skLineSegment(sketch, "E366", {"start": v(-116.97, 136.19) * mm, "end": v(-117.48, 149.08) * mm});
            skLineSegment(sketch, "E367", {"start": v(-117.48, 149.08) * mm, "end": v(-119.02, 164.91) * mm});
            skLineSegment(sketch, "E368", {"start": v(-119.02, 164.91) * mm, "end": v(-121.6, 179.42) * mm});
            skLineSegment(sketch, "E369", {"start": v(-121.6, 179.42) * mm, "end": v(-125.26, 192.67) * mm});
            skLineSegment(sketch, "E370", {"start": v(-125.26, 192.67) * mm, "end": v(-130, 204.71) * mm});
            skLineSegment(sketch, "E371", {"start": v(-130, 204.71) * mm, "end": v(-135.86, 215.61) * mm});
            skLineSegment(sketch, "E372", {"start": v(-135.86, 215.61) * mm, "end": v(-142.83, 225.42) * mm});
            skLineSegment(sketch, "E373", {"start": v(-142.83, 225.42) * mm, "end": v(-148.79, 232.12) * mm});
            skLineSegment(sketch, "E374", {"start": v(-148.79, 232.12) * mm, "end": v(-150.94, 234.18) * mm});
            skLineSegment(sketch, "E375", {"start": v(-150.94, 234.18) * mm, "end": v(-153.13, 236.26) * mm});
            skLineSegment(sketch, "E376", {"start": v(-153.13, 236.26) * mm, "end": v(-160.22, 241.94) * mm});
            skLineSegment(sketch, "E377", {"start": v(-160.22, 241.94) * mm, "end": v(-170.62, 248.6) * mm});
            skLineSegment(sketch, "E378", {"start": v(-170.62, 248.6) * mm, "end": v(-182.2, 254.19) * mm});
            skLineSegment(sketch, "E379", {"start": v(-182.2, 254.19) * mm, "end": v(-195, 258.72) * mm});
            skLineSegment(sketch, "E380", {"start": v(-195, 258.72) * mm, "end": v(-209.12, 262.22) * mm});
            skLineSegment(sketch, "E381", {"start": v(-209.12, 262.22) * mm, "end": v(-224.6, 264.7) * mm});
            skLineSegment(sketch, "E382", {"start": v(-224.6, 264.7) * mm, "end": v(-241.48, 266.16) * mm});
            skLineSegment(sketch, "E383", {"start": v(-241.48, 266.16) * mm, "end": v(-255.26, 266.65) * mm});
            skLineSegment(sketch, "E384", {"start": v(-255.26, 266.65) * mm, "end": v(-259.85, 266.65) * mm});
            skLineSegment(sketch, "E385", {"start": v(-259.85, 266.65) * mm, "end": v(-263.7, 266.65) * mm});
            skLineSegment(sketch, "E386", {"start": v(-263.7, 266.65) * mm, "end": v(-275.27, 266.17) * mm});
            skLineSegment(sketch, "E387", {"start": v(-275.27, 266.17) * mm, "end": v(-290.07, 264.72) * mm});
            skLineSegment(sketch, "E388", {"start": v(-290.07, 264.72) * mm, "end": v(-304.24, 262.34) * mm});
            skLineSegment(sketch, "E389", {"start": v(-304.24, 262.34) * mm, "end": v(-317.71, 259.02) * mm});
            skLineSegment(sketch, "E390", {"start": v(-317.71, 259.02) * mm, "end": v(-330.44, 254.78) * mm});
            skLineSegment(sketch, "E391", {"start": v(-330.44, 254.78) * mm, "end": v(-342.39, 249.64) * mm});
            skLineSegment(sketch, "E392", {"start": v(-342.39, 249.64) * mm, "end": v(-353.5, 243.6) * mm});
            skLineSegment(sketch, "E393", {"start": v(-353.5, 243.6) * mm, "end": v(-361.27, 238.54) * mm});
            skLineSegment(sketch, "E394", {"start": v(-361.27, 238.54) * mm, "end": v(-363.74, 236.7) * mm});
            skLineSegment(sketch, "E395", {"start": v(-363.74, 236.7) * mm, "end": v(-366.1, 234.92) * mm});
            skLineSegment(sketch, "E396", {"start": v(-366.1, 234.92) * mm, "end": v(-372.8, 229.13) * mm});
            skLineSegment(sketch, "E397", {"start": v(-372.8, 229.13) * mm, "end": v(-380.75, 220.93) * mm});
            skLineSegment(sketch, "E398", {"start": v(-380.75, 220.93) * mm, "end": v(-387.56, 212.14) * mm});
            skLineSegment(sketch, "E399", {"start": v(-387.56, 212.14) * mm, "end": v(-393.2, 202.83) * mm});
            skLineSegment(sketch, "E400", {"start": v(-393.2, 202.83) * mm, "end": v(-397.64, 193.03) * mm});
            skLineSegment(sketch, "E401", {"start": v(-397.64, 193.03) * mm, "end": v(-400.85, 182.83) * mm});
            skLineSegment(sketch, "E402", {"start": v(-400.85, 182.83) * mm, "end": v(-402.8, 172.26) * mm});
            skLineSegment(sketch, "E403", {"start": v(-402.8, 172.26) * mm, "end": v(-403.45, 164.11) * mm});
            skLineSegment(sketch, "E404", {"start": v(-403.45, 164.11) * mm, "end": v(-403.45, 161.4) * mm});
            skLineSegment(sketch, "E405", {"start": v(-403.45, 161.4) * mm, "end": v(-403.45, 159.87) * mm});
            skLineSegment(sketch, "E406", {"start": v(-403.45, 159.87) * mm, "end": v(-403.18, 155.3) * mm});
            skLineSegment(sketch, "E407", {"start": v(-403.18, 155.3) * mm, "end": v(-402.4, 149.4) * mm});
            skLineSegment(sketch, "E408", {"start": v(-402.4, 149.4) * mm, "end": v(-401.12, 143.76) * mm});
            skLineSegment(sketch, "E409", {"start": v(-401.12, 143.76) * mm, "end": v(-399.37, 138.37) * mm});
            skLineSegment(sketch, "E410", {"start": v(-399.37, 138.37) * mm, "end": v(-397.18, 133.28) * mm});
            skLineSegment(sketch, "E411", {"start": v(-397.18, 133.28) * mm, "end": v(-394.55, 128.5) * mm});
            skLineSegment(sketch, "E412", {"start": v(-394.55, 128.5) * mm, "end": v(-391.52, 124.05) * mm});
            skLineSegment(sketch, "E413", {"start": v(-391.52, 124.05) * mm, "end": v(-388.11, 119.97) * mm});
            skLineSegment(sketch, "E414", {"start": v(-388.11, 119.97) * mm, "end": v(-384.34, 116.28) * mm});
            skLineSegment(sketch, "E415", {"start": v(-384.34, 116.28) * mm, "end": v(-380.24, 113) * mm});
            skLineSegment(sketch, "E416", {"start": v(-380.24, 113) * mm, "end": v(-375.82, 110.16) * mm});
            skLineSegment(sketch, "E417", {"start": v(-375.82, 110.16) * mm, "end": v(-371.12, 107.78) * mm});
            skLineSegment(sketch, "E418", {"start": v(-371.12, 107.78) * mm, "end": v(-366.14, 105.89) * mm});
            skLineSegment(sketch, "E419", {"start": v(-366.14, 105.89) * mm, "end": v(-360.93, 104.5) * mm});
            skLineSegment(sketch, "E420", {"start": v(-360.93, 104.5) * mm, "end": v(-355.49, 103.65) * mm});
            skLineSegment(sketch, "E421", {"start": v(-355.49, 103.65) * mm, "end": v(-351.26, 103.36) * mm});
            skLineSegment(sketch, "E422", {"start": v(-351.26, 103.36) * mm, "end": v(-349.85, 103.36) * mm});
            skLineSegment(sketch, "E423", {"start": v(-349.85, 103.36) * mm, "end": v(-348.42, 103.36) * mm});
            skLineSegment(sketch, "E424", {"start": v(-348.42, 103.36) * mm, "end": v(-344.13, 103.61) * mm});
            skLineSegment(sketch, "E425", {"start": v(-344.13, 103.61) * mm, "end": v(-338.63, 104.35) * mm});
            skLineSegment(sketch, "E426", {"start": v(-338.63, 104.35) * mm, "end": v(-333.37, 105.56) * mm});
            skLineSegment(sketch, "E427", {"start": v(-333.37, 105.56) * mm, "end": v(-328.37, 107.2) * mm});
            skLineSegment(sketch, "E428", {"start": v(-328.37, 107.2) * mm, "end": v(-323.65, 109.29) * mm});
            skLineSegment(sketch, "E429", {"start": v(-323.65, 109.29) * mm, "end": v(-319.24, 111.78) * mm});
            skLineSegment(sketch, "E430", {"start": v(-319.24, 111.78) * mm, "end": v(-315.14, 114.65) * mm});
            skLineSegment(sketch, "E431", {"start": v(-315.14, 114.65) * mm, "end": v(-311.4, 117.9) * mm});
            skLineSegment(sketch, "E432", {"start": v(-311.4, 117.9) * mm, "end": v(-308, 121.5) * mm});
            skLineSegment(sketch, "E433", {"start": v(-308, 121.5) * mm, "end": v(-305.01, 125.41) * mm});
            skLineSegment(sketch, "E434", {"start": v(-305.01, 125.41) * mm, "end": v(-302.42, 129.64) * mm});
            skLineSegment(sketch, "E435", {"start": v(-302.42, 129.64) * mm, "end": v(-300.25, 134.17) * mm});
            skLineSegment(sketch, "E436", {"start": v(-300.25, 134.17) * mm, "end": v(-298.52, 138.96) * mm});
            skLineSegment(sketch, "E437", {"start": v(-298.52, 138.96) * mm, "end": v(-297.27, 144) * mm});
            skLineSegment(sketch, "E438", {"start": v(-297.27, 144) * mm, "end": v(-296.5, 149.27) * mm});
            skLineSegment(sketch, "E439", {"start": v(-296.5, 149.27) * mm, "end": v(-296.24, 153.39) * mm});
            skLineSegment(sketch, "E440", {"start": v(-296.24, 153.39) * mm, "end": v(-296.24, 154.76) * mm});
            skLineSegment(sketch, "E441", {"start": v(-296.24, 154.76) * mm, "end": v(-296.24, 156.06) * mm});
            skLineSegment(sketch, "E442", {"start": v(-296.24, 156.06) * mm, "end": v(-296.58, 159.95) * mm});
            skLineSegment(sketch, "E443", {"start": v(-296.58, 159.95) * mm, "end": v(-297.53, 164.71) * mm});
            skLineSegment(sketch, "E444", {"start": v(-297.53, 164.71) * mm, "end": v(-298.98, 169.08) * mm});
            skLineSegment(sketch, "E445", {"start": v(-298.98, 169.08) * mm, "end": v(-300.8, 173.08) * mm});
            skLineSegment(sketch, "E446", {"start": v(-300.8, 173.08) * mm, "end": v(-302.89, 176.73) * mm});
            skLineSegment(sketch, "E447", {"start": v(-302.89, 176.73) * mm, "end": v(-305.12, 180.06) * mm});
            skLineSegment(sketch, "E448", {"start": v(-305.12, 180.06) * mm, "end": v(-307.4, 183.1) * mm});
            skLineSegment(sketch, "E449", {"start": v(-307.4, 183.1) * mm, "end": v(-309.04, 185.17) * mm});
            skLineSegment(sketch, "E450", {"start": v(-309.04, 185.17) * mm, "end": v(-309.59, 185.86) * mm});
            skLineSegment(sketch, "E451", {"start": v(-309.59, 185.86) * mm, "end": v(-310.4, 186.87) * mm});
            skLineSegment(sketch, "E452", {"start": v(-310.4, 186.87) * mm, "end": v(-312.76, 189.93) * mm});
            skLineSegment(sketch, "E453", {"start": v(-312.76, 189.93) * mm, "end": v(-315.05, 193.36) * mm});
            skLineSegment(sketch, "E454", {"start": v(-315.05, 193.36) * mm, "end": v(-316.43, 196.52) * mm});
            skLineSegment(sketch, "E455", {"start": v(-316.43, 196.52) * mm, "end": v(-316.9, 198.96) * mm});
            skLineSegment(sketch, "E456", {"start": v(-316.9, 198.96) * mm, "end": v(-316.9, 199.77) * mm});
            skLineSegment(sketch, "E457", {"start": v(-316.9, 199.77) * mm, "end": v(-316.9, 200.43) * mm});
            skLineSegment(sketch, "E458", {"start": v(-316.9, 200.43) * mm, "end": v(-316.66, 202.43) * mm});
            skLineSegment(sketch, "E459", {"start": v(-316.66, 202.43) * mm, "end": v(-315.95, 204.98) * mm});
            skLineSegment(sketch, "E460", {"start": v(-315.95, 204.98) * mm, "end": v(-314.8, 207.42) * mm});
            skLineSegment(sketch, "E461", {"start": v(-314.8, 207.42) * mm, "end": v(-313.2, 209.72) * mm});
            skLineSegment(sketch, "E462", {"start": v(-313.2, 209.72) * mm, "end": v(-311.19, 211.88) * mm});
            skLineSegment(sketch, "E463", {"start": v(-311.19, 211.88) * mm, "end": v(-308.78, 213.91) * mm});
            skLineSegment(sketch, "E464", {"start": v(-308.78, 213.91) * mm, "end": v(-305.98, 215.78) * mm});
            skLineSegment(sketch, "E465", {"start": v(-305.98, 215.78) * mm, "end": v(-302.83, 217.5) * mm});
            skLineSegment(sketch, "E466", {"start": v(-302.83, 217.5) * mm, "end": v(-299.32, 219.03) * mm});
            skLineSegment(sketch, "E467", {"start": v(-299.32, 219.03) * mm, "end": v(-295.48, 220.4) * mm});
            skLineSegment(sketch, "E468", {"start": v(-295.48, 220.4) * mm, "end": v(-291.33, 221.57) * mm});
            skLineSegment(sketch, "E469", {"start": v(-291.33, 221.57) * mm, "end": v(-286.89, 222.55) * mm});
            skLineSegment(sketch, "E470", {"start": v(-286.89, 222.55) * mm, "end": v(-282.16, 223.33) * mm});
            skLineSegment(sketch, "E471", {"start": v(-282.16, 223.33) * mm, "end": v(-277.18, 223.9) * mm});
            skLineSegment(sketch, "E472", {"start": v(-277.18, 223.9) * mm, "end": v(-271.95, 224.24) * mm});
            skLineSegment(sketch, "E473", {"start": v(-271.95, 224.24) * mm, "end": v(-267.85, 224.36) * mm});
            skLineSegment(sketch, "E474", {"start": v(-267.85, 224.36) * mm, "end": v(-266.49, 224.36) * mm});
            skLineSegment(sketch, "E475", {"start": v(-266.49, 224.36) * mm, "end": v(-265.11, 224.36) * mm});
            skLineSegment(sketch, "E476", {"start": v(-265.11, 224.36) * mm, "end": v(-260.99, 224.27) * mm});
            skLineSegment(sketch, "E477", {"start": v(-260.99, 224.27) * mm, "end": v(-255.67, 223.92) * mm});
            skLineSegment(sketch, "E478", {"start": v(-255.67, 223.92) * mm, "end": v(-250.56, 223.23) * mm});
            skLineSegment(sketch, "E479", {"start": v(-250.56, 223.23) * mm, "end": v(-245.69, 222.1) * mm});
            skLineSegment(sketch, "E480", {"start": v(-245.69, 222.1) * mm, "end": v(-241.07, 220.4) * mm});
            skLineSegment(sketch, "E481", {"start": v(-241.07, 220.4) * mm, "end": v(-236.73, 218.06) * mm});
            skLineSegment(sketch, "E482", {"start": v(-236.73, 218.06) * mm, "end": v(-232.7, 214.97) * mm});
            skLineSegment(sketch, "E483", {"start": v(-232.7, 214.97) * mm, "end": v(-229, 211.04) * mm});
            skLineSegment(sketch, "E484", {"start": v(-229, 211.04) * mm, "end": v(-225.64, 206.15) * mm});
            skLineSegment(sketch, "E485", {"start": v(-225.64, 206.15) * mm, "end": v(-222.65, 200.22) * mm});
            skLineSegment(sketch, "E486", {"start": v(-222.65, 200.22) * mm, "end": v(-220.07, 193.14) * mm});
            skLineSegment(sketch, "E487", {"start": v(-220.07, 193.14) * mm, "end": v(-217.9, 184.82) * mm});
            skLineSegment(sketch, "E488", {"start": v(-217.9, 184.82) * mm, "end": v(-216.17, 175.14) * mm});
            skLineSegment(sketch, "E489", {"start": v(-216.17, 175.14) * mm, "end": v(-214.9, 164.03) * mm});
            skLineSegment(sketch, "E490", {"start": v(-214.9, 164.03) * mm, "end": v(-214.13, 151.36) * mm});
            skLineSegment(sketch, "E491", {"start": v(-214.13, 151.36) * mm, "end": v(-213.86, 140.64) * mm});
            skLineSegment(sketch, "E492", {"start": v(-213.86, 140.64) * mm, "end": v(-213.86, 137.06) * mm});
            skLineSegment(sketch, "E493", {"start": v(-213.86, 137.06) * mm, "end": v(-213.86, 107.2) * mm});
            skLineSegment(sketch, "E494", {"start": v(-213.86, 107.2) * mm, "end": v(-250.38, 102.78) * mm});
            skLineSegment(sketch, "E495", {"start": v(-250.38, 102.78) * mm, "end": v(-255.86, 102.14) * mm});
            skLineSegment(sketch, "E496", {"start": v(-255.86, 102.14) * mm, "end": v(-272.28, 99.88) * mm});
            skLineSegment(sketch, "E497", {"start": v(-272.28, 99.88) * mm, "end": v(-292.54, 96.49) * mm});
            skLineSegment(sketch, "E498", {"start": v(-292.54, 96.49) * mm, "end": v(-311.18, 92.56) * mm});
            skLineSegment(sketch, "E499", {"start": v(-311.18, 92.56) * mm, "end": v(-328.23, 88.08) * mm});
            skLineSegment(sketch, "E500", {"start": v(-328.23, 88.08) * mm, "end": v(-343.74, 83.03) * mm});
            skLineSegment(sketch, "E501", {"start": v(-343.74, 83.03) * mm, "end": v(-357.72, 77.38) * mm});
            skLineSegment(sketch, "E502", {"start": v(-357.72, 77.38) * mm, "end": v(-370.22, 71.1) * mm});
            skLineSegment(sketch, "E503", {"start": v(-370.22, 71.1) * mm, "end": v(-381.26, 64.18) * mm});
            skLineSegment(sketch, "E504", {"start": v(-381.26, 64.18) * mm, "end": v(-390.87, 56.6) * mm});
            skLineSegment(sketch, "E505", {"start": v(-390.87, 56.6) * mm, "end": v(-399.1, 48.32) * mm});
            skLineSegment(sketch, "E506", {"start": v(-399.1, 48.32) * mm, "end": v(-405.98, 39.32) * mm});
            skLineSegment(sketch, "E507", {"start": v(-405.98, 39.32) * mm, "end": v(-411.53, 29.6) * mm});
            skLineSegment(sketch, "E508", {"start": v(-411.53, 29.6) * mm, "end": v(-415.8, 19.11) * mm});
            skLineSegment(sketch, "E509", {"start": v(-415.8, 19.11) * mm, "end": v(-418.8, 7.84) * mm});
            skLineSegment(sketch, "E510", {"start": v(-418.8, 7.84) * mm, "end": v(-420.57, -4.23) * mm});
            skLineSegment(sketch, "E511", {"start": v(-420.57, -4.23) * mm, "end": v(-421.16, -13.91) * mm});
            skLineSegment(sketch, "E512", {"start": v(-421.16, -13.91) * mm, "end": v(-421.16, -17.14) * mm});
            skLineSegment(sketch, "E513", {"start": v(-421.16, -17.14) * mm, "end": v(-421.16, -19.94) * mm});
            skLineSegment(sketch, "E514", {"start": v(-421.16, -19.94) * mm, "end": v(-420.64, -28.34) * mm});
            skLineSegment(sketch, "E515", {"start": v(-420.64, -28.34) * mm, "end": v(-419.09, -38.94) * mm});
            skLineSegment(sketch, "E516", {"start": v(-419.09, -38.94) * mm, "end": v(-416.52, -48.93) * mm});
            skLineSegment(sketch, "E517", {"start": v(-416.52, -48.93) * mm, "end": v(-412.97, -58.3) * mm});
            skLineSegment(sketch, "E518", {"start": v(-412.97, -58.3) * mm, "end": v(-408.46, -67) * mm});
            skLineSegment(sketch, "E519", {"start": v(-408.46, -67) * mm, "end": v(-403, -75.04) * mm});
            skLineSegment(sketch, "E520", {"start": v(-403, -75.04) * mm, "end": v(-396.62, -82.4) * mm});
            skLineSegment(sketch, "E521", {"start": v(-396.62, -82.4) * mm, "end": v(-389.33, -89.06) * mm});
            skLineSegment(sketch, "E522", {"start": v(-389.33, -89.06) * mm, "end": v(-381.17, -95) * mm});
            skLineSegment(sketch, "E523", {"start": v(-381.17, -95) * mm, "end": v(-372.15, -100.21) * mm});
            skLineSegment(sketch, "E524", {"start": v(-372.15, -100.21) * mm, "end": v(-362.29, -104.66) * mm});
            skLineSegment(sketch, "E525", {"start": v(-362.29, -104.66) * mm, "end": v(-351.61, -108.35) * mm});
            skLineSegment(sketch, "E526", {"start": v(-351.61, -108.35) * mm, "end": v(-340.14, -111.24) * mm});
            skLineSegment(sketch, "E527", {"start": v(-340.14, -111.24) * mm, "end": v(-327.9, -113.33) * mm});
            skLineSegment(sketch, "E528", {"start": v(-327.9, -113.33) * mm, "end": v(-314.9, -114.6) * mm});
            skLineSegment(sketch, "E529", {"start": v(-314.9, -114.6) * mm, "end": v(-304.6, -115.02) * mm});
            skLineSegment(sketch, "E530", {"start": v(-304.6, -115.02) * mm, "end": v(-301.16, -115.02) * mm});
            skLineSegment(sketch, "E531", {"start": v(-301.16, -115.02) * mm, "end": v(-297.67, -115.02) * mm});
            skLineSegment(sketch, "E532", {"start": v(-297.67, -115.02) * mm, "end": v(-287.21, -114.45) * mm});
            skLineSegment(sketch, "E533", {"start": v(-287.21, -114.45) * mm, "end": v(-273.72, -112.78) * mm});
            skLineSegment(sketch, "E534", {"start": v(-273.72, -112.78) * mm, "end": v(-260.68, -109.98) * mm});
            skLineSegment(sketch, "E535", {"start": v(-260.68, -109.98) * mm, "end": v(-248.12, -106.06) * mm});
            skLineSegment(sketch, "E536", {"start": v(-248.12, -106.06) * mm, "end": v(-236.02, -101.04) * mm});
            skLineSegment(sketch, "E537", {"start": v(-236.02, -101.04) * mm, "end": v(-224.4, -94.91) * mm});
            skLineSegment(sketch, "E538", {"start": v(-224.4, -94.91) * mm, "end": v(-213.28, -87.68) * mm});
            skLineSegment(sketch, "E539", {"start": v(-213.28, -87.68) * mm, "end": v(-205.2, -81.54) * mm});
            skLineSegment(sketch, "E540", {"start": v(-205.2, -81.54) * mm, "end": v(-202.65, -79.35) * mm});
            skLineSegment(sketch, "E541", {"start": v(-202.65, -79.35) * mm, "end": v(-201.92, -80.67) * mm});
            skLineSegment(sketch, "E542", {"start": v(-201.92, -80.67) * mm, "end": v(-199.51, -84.51) * mm});
            skLineSegment(sketch, "E543", {"start": v(-199.51, -84.51) * mm, "end": v(-196.07, -89.18) * mm});
            skLineSegment(sketch, "E544", {"start": v(-196.07, -89.18) * mm, "end": v(-192.33, -93.38) * mm});
            skLineSegment(sketch, "E545", {"start": v(-192.33, -93.38) * mm, "end": v(-188.35, -97.12) * mm});
            skLineSegment(sketch, "E546", {"start": v(-188.35, -97.12) * mm, "end": v(-184.14, -100.43) * mm});
            skLineSegment(sketch, "E547", {"start": v(-184.14, -100.43) * mm, "end": v(-179.74, -103.34) * mm});
            skLineSegment(sketch, "E548", {"start": v(-179.74, -103.34) * mm, "end": v(-175.17, -105.86) * mm});
            skLineSegment(sketch, "E549", {"start": v(-175.17, -105.86) * mm, "end": v(-170.47, -108.02) * mm});
            skLineSegment(sketch, "E550", {"start": v(-170.47, -108.02) * mm, "end": v(-165.66, -109.85) * mm});
            skLineSegment(sketch, "E551", {"start": v(-165.66, -109.85) * mm, "end": v(-160.78, -111.35) * mm});
            skLineSegment(sketch, "E552", {"start": v(-160.78, -111.35) * mm, "end": v(-155.84, -112.57) * mm});
            skLineSegment(sketch, "E553", {"start": v(-155.84, -112.57) * mm, "end": v(-150.9, -113.5) * mm});
            skLineSegment(sketch, "E554", {"start": v(-150.9, -113.5) * mm, "end": v(-145.95, -114.2) * mm});
            skLineSegment(sketch, "E555", {"start": v(-145.95, -114.2) * mm, "end": v(-141.05, -114.67) * mm});
            skLineSegment(sketch, "E556", {"start": v(-141.05, -114.67) * mm, "end": v(-136.21, -114.93) * mm});
            skLineSegment(sketch, "E557", {"start": v(-136.21, -114.93) * mm, "end": v(-132.66, -115.02) * mm});
            skLineSegment(sketch, "E558", {"start": v(-132.66, -115.02) * mm, "end": v(-131.48, -115.02) * mm});
            skLineSegment(sketch, "E559", {"start": v(-131.48, -115.02) * mm, "end": v(-130.17, -115.02) * mm});
            skLineSegment(sketch, "E560", {"start": v(-130.17, -115.02) * mm, "end": v(-126.23, -114.93) * mm});
            skLineSegment(sketch, "E561", {"start": v(-126.23, -114.93) * mm, "end": v(-120.76, -114.63) * mm});
            skLineSegment(sketch, "E562", {"start": v(-120.76, -114.63) * mm, "end": v(-115.12, -114.06) * mm});
            skLineSegment(sketch, "E563", {"start": v(-115.12, -114.06) * mm, "end": v(-109.35, -113.16) * mm});
            skLineSegment(sketch, "E564", {"start": v(-109.35, -113.16) * mm, "end": v(-103.49, -111.85) * mm});
            skLineSegment(sketch, "E565", {"start": v(-103.49, -111.85) * mm, "end": v(-97.59, -110.08) * mm});
            skLineSegment(sketch, "E566", {"start": v(-97.59, -110.08) * mm, "end": v(-91.7, -107.8) * mm});
            skLineSegment(sketch, "E567", {"start": v(-91.7, -107.8) * mm, "end": v(-85.85, -104.92) * mm});
            skLineSegment(sketch, "E568", {"start": v(-85.85, -104.92) * mm, "end": v(-80.1, -101.4) * mm});
            skLineSegment(sketch, "E569", {"start": v(-80.1, -101.4) * mm, "end": v(-74.48, -97.17) * mm});
            skLineSegment(sketch, "E570", {"start": v(-74.48, -97.17) * mm, "end": v(-69.05, -92.17) * mm});
            skLineSegment(sketch, "E571", {"start": v(-69.05, -92.17) * mm, "end": v(-63.85, -86.33) * mm});
            skLineSegment(sketch, "E572", {"start": v(-63.85, -86.33) * mm, "end": v(-58.91, -79.6) * mm});
            skLineSegment(sketch, "E573", {"start": v(-58.91, -79.6) * mm, "end": v(-54.3, -71.92) * mm});
            skLineSegment(sketch, "E574", {"start": v(-54.3, -71.92) * mm, "end": v(-50.04, -63.2) * mm});
            skLineSegment(sketch, "E575", {"start": v(-50.04, -63.2) * mm, "end": v(-47.06, -55.9) * mm});
            skLineSegment(sketch, "E576", {"start": v(-47.06, -55.9) * mm, "end": v(-46.2, -53.42) * mm});
            skLineSegment(sketch, "E577", {"start": v(-46.2, -53.42) * mm, "end": v(-41.49, -40) * mm});
            skLineSegment(sketch, "E578", {"start": v(-41.49, -40) * mm, "end": v(-82.1, -27.2) * mm});
            skLineSegment(sketch, "E579", {"start": v(-82.1, -27.2) * mm, "end": v(-86.3, -40.21) * mm});
            skLineSegment(sketch, "E580", {"start": v(303.11, -40.09) * mm, "end": v(301.87, -42.07) * mm});
            skLineSegment(sketch, "E581", {"start": v(301.87, -42.07) * mm, "end": v(297.88, -47.83) * mm});
            skLineSegment(sketch, "E582", {"start": v(297.88, -47.83) * mm, "end": v(292.83, -54.03) * mm});
            skLineSegment(sketch, "E583", {"start": v(292.83, -54.03) * mm, "end": v(287.9, -58.83) * mm});
            skLineSegment(sketch, "E584", {"start": v(287.9, -58.83) * mm, "end": v(283.05, -62.4) * mm});
            skLineSegment(sketch, "E585", {"start": v(283.05, -62.4) * mm, "end": v(278.22, -64.9) * mm});
            skLineSegment(sketch, "E586", {"start": v(278.22, -64.9) * mm, "end": v(273.32, -66.48) * mm});
            skLineSegment(sketch, "E587", {"start": v(273.32, -66.48) * mm, "end": v(268.32, -67.31) * mm});
            skLineSegment(sketch, "E588", {"start": v(268.32, -67.31) * mm, "end": v(264.43, -67.56) * mm});
            skLineSegment(sketch, "E589", {"start": v(264.43, -67.56) * mm, "end": v(263.13, -67.56) * mm});
            skLineSegment(sketch, "E590", {"start": v(263.13, -67.56) * mm, "end": v(262.47, -67.56) * mm});
            skLineSegment(sketch, "E591", {"start": v(262.47, -67.56) * mm, "end": v(260.5, -67.5) * mm});
            skLineSegment(sketch, "E592", {"start": v(260.5, -67.5) * mm, "end": v(257.93, -67.3) * mm});
            skLineSegment(sketch, "E593", {"start": v(257.93, -67.3) * mm, "end": v(255.46, -66.88) * mm});
            skLineSegment(sketch, "E594", {"start": v(255.46, -66.88) * mm, "end": v(253.13, -66.19) * mm});
            skLineSegment(sketch, "E595", {"start": v(253.13, -66.19) * mm, "end": v(250.92, -65.17) * mm});
            skLineSegment(sketch, "E596", {"start": v(250.92, -65.17) * mm, "end": v(248.83, -63.76) * mm});
            skLineSegment(sketch, "E597", {"start": v(248.83, -63.76) * mm, "end": v(246.88, -61.9) * mm});
            skLineSegment(sketch, "E598", {"start": v(246.88, -61.9) * mm, "end": v(245.1, -59.52) * mm});
            skLineSegment(sketch, "E599", {"start": v(245.1, -59.52) * mm, "end": v(243.47, -56.58) * mm});
            skLineSegment(sketch, "E600", {"start": v(243.47, -56.58) * mm, "end": v(242.05, -53) * mm});
            skLineSegment(sketch, "E601", {"start": v(242.05, -53) * mm, "end": v(240.8, -48.73) * mm});
            skLineSegment(sketch, "E602", {"start": v(240.8, -48.73) * mm, "end": v(239.74, -43.72) * mm});
            skLineSegment(sketch, "E603", {"start": v(239.74, -43.72) * mm, "end": v(238.93, -37.89) * mm});
            skLineSegment(sketch, "E604", {"start": v(238.93, -37.89) * mm, "end": v(238.32, -31.19) * mm});
            skLineSegment(sketch, "E605", {"start": v(238.32, -31.19) * mm, "end": v(237.94, -23.55) * mm});
            skLineSegment(sketch, "E606", {"start": v(237.94, -23.55) * mm, "end": v(237.8, -17.08) * mm});
            skLineSegment(sketch, "E607", {"start": v(237.8, -17.08) * mm, "end": v(237.8, -14.93) * mm});
            skLineSegment(sketch, "E608", {"start": v(237.8, -14.93) * mm, "end": v(237.8, 216.98) * mm});
            skLineSegment(sketch, "E609", {"start": v(237.8, 216.98) * mm, "end": v(337.4, 216.98) * mm});
            skLineSegment(sketch, "E610", {"start": v(337.4, 216.98) * mm, "end": v(337.4, 259.28) * mm});
            skLineSegment(sketch, "E611", {"start": v(337.4, 259.28) * mm, "end": v(237.8, 259.28) * mm});
            skLineSegment(sketch, "E612", {"start": v(237.8, 259.28) * mm, "end": v(237.8, 351.5) * mm});
            skLineSegment(sketch, "E613", {"start": v(237.8, 351.5) * mm, "end": v(201.55, 351.5) * mm});
            skLineSegment(sketch, "E614", {"start": v(201.55, 351.5) * mm, "end": v(198.9, 341.12) * mm});
            skLineSegment(sketch, "E615", {"start": v(198.9, 341.12) * mm, "end": v(198.1, 338) * mm});
            skLineSegment(sketch, "E616", {"start": v(198.1, 338) * mm, "end": v(195.28, 328.72) * mm});
            skLineSegment(sketch, "E617", {"start": v(195.28, 328.72) * mm, "end": v(190.87, 316.82) * mm});
            skLineSegment(sketch, "E618", {"start": v(190.87, 316.82) * mm, "end": v(185.71, 305.5) * mm});
            skLineSegment(sketch, "E619", {"start": v(185.71, 305.5) * mm, "end": v(179.84, 294.79) * mm});
            skLineSegment(sketch, "E620", {"start": v(179.84, 294.79) * mm, "end": v(173.28, 284.75) * mm});
            skLineSegment(sketch, "E621", {"start": v(173.28, 284.75) * mm, "end": v(166.07, 275.46) * mm});
            skLineSegment(sketch, "E622", {"start": v(166.07, 275.46) * mm, "end": v(158.26, 266.95) * mm});
            skLineSegment(sketch, "E623", {"start": v(158.26, 266.95) * mm, "end": v(152.04, 261.1) * mm});
            skLineSegment(sketch, "E624", {"start": v(152.04, 261.1) * mm, "end": v(149.86, 259.28) * mm});
            skLineSegment(sketch, "E625", {"start": v(149.86, 259.28) * mm, "end": v(94.46, 259.28) * mm});
            skLineSegment(sketch, "E626", {"start": v(94.46, 259.28) * mm, "end": v(94.46, 216.98) * mm});
            skLineSegment(sketch, "E627", {"start": v(94.46, 216.98) * mm, "end": v(140.93, 216.98) * mm});
            skLineSegment(sketch, "E628", {"start": v(140.93, 216.98) * mm, "end": v(140.93, -5.34) * mm});
            skLineSegment(sketch, "E629", {"start": v(140.93, -5.34) * mm, "end": v(140.93, -8.6) * mm});
            skLineSegment(sketch, "E630", {"start": v(140.93, -8.6) * mm, "end": v(141.36, -18.4) * mm});
            skLineSegment(sketch, "E631", {"start": v(141.36, -18.4) * mm, "end": v(142.65, -30.65) * mm});
            skLineSegment(sketch, "E632", {"start": v(142.65, -30.65) * mm, "end": v(144.8, -42.1) * mm});
            skLineSegment(sketch, "E633", {"start": v(144.8, -42.1) * mm, "end": v(147.79, -52.75) * mm});
            skLineSegment(sketch, "E634", {"start": v(147.79, -52.75) * mm, "end": v(151.62, -62.57) * mm});
            skLineSegment(sketch, "E635", {"start": v(151.62, -62.57) * mm, "end": v(156.29, -71.57) * mm});
            skLineSegment(sketch, "E636", {"start": v(156.29, -71.57) * mm, "end": v(161.79, -79.75) * mm});
            skLineSegment(sketch, "E637", {"start": v(161.79, -79.75) * mm, "end": v(168.1, -87.09) * mm});
            skLineSegment(sketch, "E638", {"start": v(168.1, -87.09) * mm, "end": v(175.25, -93.58) * mm});
            skLineSegment(sketch, "E639", {"start": v(175.25, -93.58) * mm, "end": v(183.2, -99.23) * mm});
            skLineSegment(sketch, "E640", {"start": v(183.2, -99.23) * mm, "end": v(191.96, -104.03) * mm});
            skLineSegment(sketch, "E641", {"start": v(191.96, -104.03) * mm, "end": v(201.52, -107.97) * mm});
            skLineSegment(sketch, "E642", {"start": v(201.52, -107.97) * mm, "end": v(211.88, -111.04) * mm});
            skLineSegment(sketch, "E643", {"start": v(211.88, -111.04) * mm, "end": v(223.03, -113.25) * mm});
            skLineSegment(sketch, "E644", {"start": v(223.03, -113.25) * mm, "end": v(234.94, -114.57) * mm});
            skLineSegment(sketch, "E645", {"start": v(234.94, -114.57) * mm, "end": v(244.46, -115.02) * mm});
            skLineSegment(sketch, "E646", {"start": v(244.46, -115.02) * mm, "end": v(247.66, -115.02) * mm});
            skLineSegment(sketch, "E647", {"start": v(247.66, -115.02) * mm, "end": v(251.22, -115.02) * mm});
            skLineSegment(sketch, "E648", {"start": v(251.22, -115.02) * mm, "end": v(261.89, -114.14) * mm});
            skLineSegment(sketch, "E649", {"start": v(261.89, -114.14) * mm, "end": v(275.4, -111.54) * mm});
            skLineSegment(sketch, "E650", {"start": v(275.4, -111.54) * mm, "end": v(288.1, -107.23) * mm});
            skLineSegment(sketch, "E651", {"start": v(288.1, -107.23) * mm, "end": v(300.01, -101.24) * mm});
            skLineSegment(sketch, "E652", {"start": v(300.01, -101.24) * mm, "end": v(311.01, -93.6) * mm});
            skLineSegment(sketch, "E653", {"start": v(311.01, -93.6) * mm, "end": v(321.15, -84.3) * mm});
            skLineSegment(sketch, "E654", {"start": v(321.15, -84.3) * mm, "end": v(330.32, -73.41) * mm});
            skLineSegment(sketch, "E655", {"start": v(330.32, -73.41) * mm, "end": v(336.64, -64.15) * mm});
            skLineSegment(sketch, "E656", {"start": v(336.64, -64.15) * mm, "end": v(338.5, -60.93) * mm});
            skLineSegment(sketch, "E657", {"start": v(338.5, -60.93) * mm, "end": v(345.48, -48.88) * mm});
            skLineSegment(sketch, "E658", {"start": v(345.48, -48.88) * mm, "end": v(310.1, -28.93) * mm});
            skLineSegment(sketch, "E659", {"start": v(310.1, -28.93) * mm, "end": v(303.11, -40.09) * mm});
            skLineSegment(sketch, "E660", {"start": v(886.96, 259.28) * mm, "end": v(742.86, 259.28) * mm});
            skLineSegment(sketch, "E661", {"start": v(742.86, 259.28) * mm, "end": v(742.86, 216.98) * mm});
            skLineSegment(sketch, "E662", {"start": v(742.86, 216.98) * mm, "end": v(790.08, 216.98) * mm});
            skLineSegment(sketch, "E663", {"start": v(790.08, 216.98) * mm, "end": v(790.08, 2.57) * mm});
            skLineSegment(sketch, "E664", {"start": v(790.08, 2.57) * mm, "end": v(788.94, 0.46) * mm});
            skLineSegment(sketch, "E665", {"start": v(788.94, 0.46) * mm, "end": v(785.3, -5.77) * mm});
            skLineSegment(sketch, "E666", {"start": v(785.3, -5.77) * mm, "end": v(780.35, -13.6) * mm});
            skLineSegment(sketch, "E667", {"start": v(780.35, -13.6) * mm, "end": v(775.25, -20.95) * mm});
            skLineSegment(sketch, "E668", {"start": v(775.25, -20.95) * mm, "end": v(770, -27.8) * mm});
            skLineSegment(sketch, "E669", {"start": v(770, -27.8) * mm, "end": v(764.6, -34.13) * mm});
            skLineSegment(sketch, "E670", {"start": v(764.6, -34.13) * mm, "end": v(759.07, -39.95) * mm});
            skLineSegment(sketch, "E671", {"start": v(759.07, -39.95) * mm, "end": v(753.43, -45.24) * mm});
            skLineSegment(sketch, "E672", {"start": v(753.43, -45.24) * mm, "end": v(747.66, -50) * mm});
            skLineSegment(sketch, "E673", {"start": v(747.66, -50) * mm, "end": v(741.77, -54.24) * mm});
            skLineSegment(sketch, "E674", {"start": v(741.77, -54.24) * mm, "end": v(735.8, -57.93) * mm});
            skLineSegment(sketch, "E675", {"start": v(735.8, -57.93) * mm, "end": v(729.76, -61.07) * mm});
            skLineSegment(sketch, "E676", {"start": v(729.76, -61.07) * mm, "end": v(723.61, -63.65) * mm});
            skLineSegment(sketch, "E677", {"start": v(723.61, -63.65) * mm, "end": v(717.39, -65.67) * mm});
            skLineSegment(sketch, "E678", {"start": v(717.39, -65.67) * mm, "end": v(711.09, -67.12) * mm});
            skLineSegment(sketch, "E679", {"start": v(711.09, -67.12) * mm, "end": v(704.76, -68) * mm});
            skLineSegment(sketch, "E680", {"start": v(704.76, -68) * mm, "end": v(699.96, -68.29) * mm});
            skLineSegment(sketch, "E681", {"start": v(699.96, -68.29) * mm, "end": v(698.36, -68.29) * mm});
            skLineSegment(sketch, "E682", {"start": v(698.36, -68.29) * mm, "end": v(697.04, -68.29) * mm});
            skLineSegment(sketch, "E683", {"start": v(697.04, -68.29) * mm, "end": v(693.05, -68.14) * mm});
            skLineSegment(sketch, "E684", {"start": v(693.05, -68.14) * mm, "end": v(687.97, -67.67) * mm});
            skLineSegment(sketch, "E685", {"start": v(687.97, -67.67) * mm, "end": v(683.17, -66.83) * mm});
            skLineSegment(sketch, "E686", {"start": v(683.17, -66.83) * mm, "end": v(678.63, -65.56) * mm});
            skLineSegment(sketch, "E687", {"start": v(678.63, -65.56) * mm, "end": v(674.36, -63.83) * mm});
            skLineSegment(sketch, "E688", {"start": v(674.36, -63.83) * mm, "end": v(670.4, -61.57) * mm});
            skLineSegment(sketch, "E689", {"start": v(670.4, -61.57) * mm, "end": v(666.74, -58.74) * mm});
            skLineSegment(sketch, "E690", {"start": v(666.74, -58.74) * mm, "end": v(663.41, -55.3) * mm});
            skLineSegment(sketch, "E691", {"start": v(663.41, -55.3) * mm, "end": v(660.41, -51.17) * mm});
            skLineSegment(sketch, "E692", {"start": v(660.41, -51.17) * mm, "end": v(657.77, -46.33) * mm});
            skLineSegment(sketch, "E693", {"start": v(657.77, -46.33) * mm, "end": v(655.51, -40.72) * mm});
            skLineSegment(sketch, "E694", {"start": v(655.51, -40.72) * mm, "end": v(653.6, -34.3) * mm});
            skLineSegment(sketch, "E695", {"start": v(653.6, -34.3) * mm, "end": v(652.13, -27) * mm});
            skLineSegment(sketch, "E696", {"start": v(652.13, -27) * mm, "end": v(651.04, -18.8) * mm});
            skLineSegment(sketch, "E697", {"start": v(651.04, -18.8) * mm, "end": v(650.38, -9.62) * mm});
            skLineSegment(sketch, "E698", {"start": v(650.38, -9.62) * mm, "end": v(650.15, -1.98) * mm});
            skLineSegment(sketch, "E699", {"start": v(650.15, -1.98) * mm, "end": v(650.15, 0.57) * mm});
            skLineSegment(sketch, "E700", {"start": v(650.15, 0.57) * mm, "end": v(650.15, 259.28) * mm});
            skLineSegment(sketch, "E701", {"start": v(650.15, 259.28) * mm, "end": v(506.8, 259.28) * mm});
            skLineSegment(sketch, "E702", {"start": v(506.8, 259.28) * mm, "end": v(506.8, 216.98) * mm});
            skLineSegment(sketch, "E703", {"start": v(506.8, 216.98) * mm, "end": v(553.28, 216.98) * mm});
            skLineSegment(sketch, "E704", {"start": v(553.28, 216.98) * mm, "end": v(553.28, 24.18) * mm});
            skLineSegment(sketch, "E705", {"start": v(553.28, 24.18) * mm, "end": v(553.28, 19.93) * mm});
            skLineSegment(sketch, "E706", {"start": v(553.28, 19.93) * mm, "end": v(553.76, 7.18) * mm});
            skLineSegment(sketch, "E707", {"start": v(553.76, 7.18) * mm, "end": v(555.26, -8.7) * mm});
            skLineSegment(sketch, "E708", {"start": v(555.26, -8.7) * mm, "end": v(557.72, -23.45) * mm});
            skLineSegment(sketch, "E709", {"start": v(557.72, -23.45) * mm, "end": v(561.2, -37.09) * mm});
            skLineSegment(sketch, "E710", {"start": v(561.2, -37.09) * mm, "end": v(565.7, -49.61) * mm});
            skLineSegment(sketch, "E711", {"start": v(565.7, -49.61) * mm, "end": v(571.18, -61.03) * mm});
            skLineSegment(sketch, "E712", {"start": v(571.18, -61.03) * mm, "end": v(577.69, -71.34) * mm});
            skLineSegment(sketch, "E713", {"start": v(577.69, -71.34) * mm, "end": v(585.18, -80.54) * mm});
            skLineSegment(sketch, "E714", {"start": v(585.18, -80.54) * mm, "end": v(593.71, -88.66) * mm});
            skLineSegment(sketch, "E715", {"start": v(593.71, -88.66) * mm, "end": v(603.26, -95.67) * mm});
            skLineSegment(sketch, "E716", {"start": v(603.26, -95.67) * mm, "end": v(613.83, -101.6) * mm});
            skLineSegment(sketch, "E717", {"start": v(613.83, -101.6) * mm, "end": v(625.41, -106.44) * mm});
            skLineSegment(sketch, "E718", {"start": v(625.41, -106.44) * mm, "end": v(638.04, -110.2) * mm});
            skLineSegment(sketch, "E719", {"start": v(638.04, -110.2) * mm, "end": v(651.7, -112.88) * mm});
            skLineSegment(sketch, "E720", {"start": v(651.7, -112.88) * mm, "end": v(666.4, -114.48) * mm});
            skLineSegment(sketch, "E721", {"start": v(666.4, -114.48) * mm, "end": v(678.2, -115.02) * mm});
            skLineSegment(sketch, "E722", {"start": v(678.2, -115.02) * mm, "end": v(682.13, -115.02) * mm});
            skLineSegment(sketch, "E723", {"start": v(682.13, -115.02) * mm, "end": v(686.02, -115.02) * mm});
            skLineSegment(sketch, "E724", {"start": v(686.02, -115.02) * mm, "end": v(697.65, -114.3) * mm});
            skLineSegment(sketch, "E725", {"start": v(697.65, -114.3) * mm, "end": v(712.61, -112.12) * mm});
            skLineSegment(sketch, "E726", {"start": v(712.61, -112.12) * mm, "end": v(727.01, -108.5) * mm});
            skLineSegment(sketch, "E727", {"start": v(727.01, -108.5) * mm, "end": v(740.8, -103.43) * mm});
            skLineSegment(sketch, "E728", {"start": v(740.8, -103.43) * mm, "end": v(754.01, -96.93) * mm});
            skLineSegment(sketch, "E729", {"start": v(754.01, -96.93) * mm, "end": v(766.64, -88.99) * mm});
            skLineSegment(sketch, "E730", {"start": v(766.64, -88.99) * mm, "end": v(778.68, -79.62) * mm});
            skLineSegment(sketch, "E731", {"start": v(778.68, -79.62) * mm, "end": v(787.36, -71.65) * mm});
            skLineSegment(sketch, "E732", {"start": v(787.36, -71.65) * mm, "end": v(790.08, -68.83) * mm});
            skLineSegment(sketch, "E733", {"start": v(790.08, -68.83) * mm, "end": v(790.08, -107.64) * mm});
            skLineSegment(sketch, "E734", {"start": v(790.08, -107.64) * mm, "end": v(933.44, -107.64) * mm});
            skLineSegment(sketch, "E735", {"start": v(933.44, -107.64) * mm, "end": v(933.44, -65.34) * mm});
            skLineSegment(sketch, "E736", {"start": v(933.44, -65.34) * mm, "end": v(886.96, -65.34) * mm});
            skLineSegment(sketch, "E737", {"start": v(886.96, -65.34) * mm, "end": v(886.96, 259.28) * mm});
            skLineSegment(sketch, "E738", {"start": v(1269.71, 124.07) * mm, "end": v(1267.25, 124.7) * mm});
            skLineSegment(sketch, "E739", {"start": v(1267.25, 124.7) * mm, "end": v(1259.88, 126.62) * mm});
            skLineSegment(sketch, "E740", {"start": v(1259.88, 126.62) * mm, "end": v(1250.48, 129.1) * mm});
            skLineSegment(sketch, "E741", {"start": v(1250.48, 129.1) * mm, "end": v(1241.67, 131.57) * mm});
            skLineSegment(sketch, "E742", {"start": v(1241.67, 131.57) * mm, "end": v(1233.36, 134.06) * mm});
            skLineSegment(sketch, "E743", {"start": v(1233.36, 134.06) * mm, "end": v(1225.64, 136.6) * mm});
            skLineSegment(sketch, "E744", {"start": v(1225.64, 136.6) * mm, "end": v(1218.48, 139.2) * mm});
            skLineSegment(sketch, "E745", {"start": v(1218.48, 139.2) * mm, "end": v(1211.95, 141.94) * mm});
            skLineSegment(sketch, "E746", {"start": v(1211.95, 141.94) * mm, "end": v(1206, 144.83) * mm});
            skLineSegment(sketch, "E747", {"start": v(1206, 144.83) * mm, "end": v(1200.7, 147.9) * mm});
            skLineSegment(sketch, "E748", {"start": v(1200.7, 147.9) * mm, "end": v(1196.05, 151.2) * mm});
            skLineSegment(sketch, "E749", {"start": v(1196.05, 151.2) * mm, "end": v(1192.06, 154.77) * mm});
            skLineSegment(sketch, "E750", {"start": v(1192.06, 154.77) * mm, "end": v(1188.76, 158.61) * mm});
            skLineSegment(sketch, "E751", {"start": v(1188.76, 158.61) * mm, "end": v(1186.14, 162.79) * mm});
            skLineSegment(sketch, "E752", {"start": v(1186.14, 162.79) * mm, "end": v(1184.26, 167.33) * mm});
            skLineSegment(sketch, "E753", {"start": v(1184.26, 167.33) * mm, "end": v(1183.12, 172.26) * mm});
            skLineSegment(sketch, "E754", {"start": v(1183.12, 172.26) * mm, "end": v(1182.74, 176.28) * mm});
            skLineSegment(sketch, "E755", {"start": v(1182.74, 176.28) * mm, "end": v(1182.74, 177.63) * mm});
            skLineSegment(sketch, "E756", {"start": v(1182.74, 177.63) * mm, "end": v(1182.74, 178.84) * mm});
            skLineSegment(sketch, "E757", {"start": v(1182.74, 178.84) * mm, "end": v(1183, 182.47) * mm});
            skLineSegment(sketch, "E758", {"start": v(1183, 182.47) * mm, "end": v(1183.76, 187.09) * mm});
            skLineSegment(sketch, "E759", {"start": v(1183.76, 187.09) * mm, "end": v(1185, 191.46) * mm});
            skLineSegment(sketch, "E760", {"start": v(1185, 191.46) * mm, "end": v(1186.75, 195.59) * mm});
            skLineSegment(sketch, "E761", {"start": v(1186.75, 195.59) * mm, "end": v(1189.01, 199.47) * mm});
            skLineSegment(sketch, "E762", {"start": v(1189.01, 199.47) * mm, "end": v(1191.76, 203.1) * mm});
            skLineSegment(sketch, "E763", {"start": v(1191.76, 203.1) * mm, "end": v(1194.98, 206.48) * mm});
            skLineSegment(sketch, "E764", {"start": v(1194.98, 206.48) * mm, "end": v(1197.75, 208.87) * mm});
            skLineSegment(sketch, "E765", {"start": v(1197.75, 208.87) * mm, "end": v(1198.74, 209.6) * mm});
            skLineSegment(sketch, "E766", {"start": v(1198.74, 209.6) * mm, "end": v(1199.96, 210.52) * mm});
            skLineSegment(sketch, "E767", {"start": v(1199.96, 210.52) * mm, "end": v(1203.87, 213) * mm});
            skLineSegment(sketch, "E768", {"start": v(1203.87, 213) * mm, "end": v(1209.66, 215.98) * mm});
            skLineSegment(sketch, "E769", {"start": v(1209.66, 215.98) * mm, "end": v(1216.12, 218.51) * mm});
            skLineSegment(sketch, "E770", {"start": v(1216.12, 218.51) * mm, "end": v(1223.15, 220.6) * mm});
            skLineSegment(sketch, "E771", {"start": v(1223.15, 220.6) * mm, "end": v(1230.72, 222.23) * mm});
            skLineSegment(sketch, "E772", {"start": v(1230.72, 222.23) * mm, "end": v(1238.87, 223.41) * mm});
            skLineSegment(sketch, "E773", {"start": v(1238.87, 223.41) * mm, "end": v(1247.59, 224.12) * mm});
            skLineSegment(sketch, "E774", {"start": v(1247.59, 224.12) * mm, "end": v(1254.47, 224.36) * mm});
            skLineSegment(sketch, "E775", {"start": v(1254.47, 224.36) * mm, "end": v(1256.76, 224.36) * mm});
            skLineSegment(sketch, "E776", {"start": v(1256.76, 224.36) * mm, "end": v(1258.84, 224.36) * mm});
            skLineSegment(sketch, "E777", {"start": v(1258.84, 224.36) * mm, "end": v(1265.06, 224.16) * mm});
            skLineSegment(sketch, "E778", {"start": v(1265.06, 224.16) * mm, "end": v(1272.86, 223.58) * mm});
            skLineSegment(sketch, "E779", {"start": v(1272.86, 223.58) * mm, "end": v(1280.15, 222.68) * mm});
            skLineSegment(sketch, "E780", {"start": v(1280.15, 222.68) * mm, "end": v(1286.88, 221.5) * mm});
            skLineSegment(sketch, "E781", {"start": v(1286.88, 221.5) * mm, "end": v(1293.13, 220.06) * mm});
            skLineSegment(sketch, "E782", {"start": v(1293.13, 220.06) * mm, "end": v(1298.84, 218.44) * mm});
            skLineSegment(sketch, "E783", {"start": v(1298.84, 218.44) * mm, "end": v(1304.08, 216.66) * mm});
            skLineSegment(sketch, "E784", {"start": v(1304.08, 216.66) * mm, "end": v(1308.72, 214.79) * mm});
            skLineSegment(sketch, "E785", {"start": v(1308.72, 214.79) * mm, "end": v(1312.86, 212.84) * mm});
            skLineSegment(sketch, "E786", {"start": v(1312.86, 212.84) * mm, "end": v(1316.5, 210.88) * mm});
            skLineSegment(sketch, "E787", {"start": v(1316.5, 210.88) * mm, "end": v(1319.6, 208.95) * mm});
            skLineSegment(sketch, "E788", {"start": v(1319.6, 208.95) * mm, "end": v(1322.14, 207.09) * mm});
            skLineSegment(sketch, "E789", {"start": v(1322.14, 207.09) * mm, "end": v(1324.2, 205.34) * mm});
            skLineSegment(sketch, "E790", {"start": v(1324.2, 205.34) * mm, "end": v(1325.7, 203.76) * mm});
            skLineSegment(sketch, "E791", {"start": v(1325.7, 203.76) * mm, "end": v(1326.66, 202.38) * mm});
            skLineSegment(sketch, "E792", {"start": v(1326.66, 202.38) * mm, "end": v(1327.04, 201.54) * mm});
            skLineSegment(sketch, "E793", {"start": v(1327.04, 201.54) * mm, "end": v(1327.11, 201.25) * mm});
            skLineSegment(sketch, "E794", {"start": v(1327.11, 201.25) * mm, "end": v(1327.11, 200.94) * mm});
            skLineSegment(sketch, "E795", {"start": v(1327.11, 200.94) * mm, "end": v(1326.86, 200.03) * mm});
            skLineSegment(sketch, "E796", {"start": v(1326.86, 200.03) * mm, "end": v(1325.97, 198.64) * mm});
            skLineSegment(sketch, "E797", {"start": v(1325.97, 198.64) * mm, "end": v(1324.22, 196.74) * mm});
            skLineSegment(sketch, "E798", {"start": v(1324.22, 196.74) * mm, "end": v(1322.03, 194.68) * mm});
            skLineSegment(sketch, "E799", {"start": v(1322.03, 194.68) * mm, "end": v(1321.25, 194.01) * mm});
            skLineSegment(sketch, "E800", {"start": v(1321.25, 194.01) * mm, "end": v(1320.61, 193.43) * mm});
            skLineSegment(sketch, "E801", {"start": v(1320.61, 193.43) * mm, "end": v(1318.7, 191.68) * mm});
            skLineSegment(sketch, "E802", {"start": v(1318.7, 191.68) * mm, "end": v(1315.96, 189) * mm});
            skLineSegment(sketch, "E803", {"start": v(1315.96, 189) * mm, "end": v(1313.25, 185.95) * mm});
            skLineSegment(sketch, "E804", {"start": v(1313.25, 185.95) * mm, "end": v(1310.68, 182.45) * mm});
            skLineSegment(sketch, "E805", {"start": v(1310.68, 182.45) * mm, "end": v(1308.42, 178.44) * mm});
            skLineSegment(sketch, "E806", {"start": v(1308.42, 178.44) * mm, "end": v(1306.57, 173.88) * mm});
            skLineSegment(sketch, "E807", {"start": v(1306.57, 173.88) * mm, "end": v(1305.37, 168.71) * mm});
            skLineSegment(sketch, "E808", {"start": v(1305.37, 168.71) * mm, "end": v(1304.97, 164.34) * mm});
            skLineSegment(sketch, "E809", {"start": v(1304.97, 164.34) * mm, "end": v(1304.97, 162.88) * mm});
            skLineSegment(sketch, "E810", {"start": v(1304.97, 162.88) * mm, "end": v(1304.97, 161.58) * mm});
            skLineSegment(sketch, "E811", {"start": v(1304.97, 161.58) * mm, "end": v(1305.2, 157.7) * mm});
            skLineSegment(sketch, "E812", {"start": v(1305.2, 157.7) * mm, "end": v(1305.9, 152.76) * mm});
            skLineSegment(sketch, "E813", {"start": v(1305.9, 152.76) * mm, "end": v(1307.02, 148.04) * mm});
            skLineSegment(sketch, "E814", {"start": v(1307.02, 148.04) * mm, "end": v(1308.62, 143.57) * mm});
            skLineSegment(sketch, "E815", {"start": v(1308.62, 143.57) * mm, "end": v(1310.6, 139.37) * mm});
            skLineSegment(sketch, "E816", {"start": v(1310.6, 139.37) * mm, "end": v(1313, 135.44) * mm});
            skLineSegment(sketch, "E817", {"start": v(1313, 135.44) * mm, "end": v(1315.79, 131.8) * mm});
            skLineSegment(sketch, "E818", {"start": v(1315.79, 131.8) * mm, "end": v(1318.88, 128.5) * mm});
            skLineSegment(sketch, "E819", {"start": v(1318.88, 128.5) * mm, "end": v(1322.39, 125.5) * mm});
            skLineSegment(sketch, "E820", {"start": v(1322.39, 125.5) * mm, "end": v(1326.15, 122.86) * mm});
            skLineSegment(sketch, "E821", {"start": v(1326.15, 122.86) * mm, "end": v(1330.29, 120.58) * mm});
            skLineSegment(sketch, "E822", {"start": v(1330.29, 120.58) * mm, "end": v(1334.66, 118.68) * mm});
            skLineSegment(sketch, "E823", {"start": v(1334.66, 118.68) * mm, "end": v(1339.36, 117.17) * mm});
            skLineSegment(sketch, "E824", {"start": v(1339.36, 117.17) * mm, "end": v(1344.28, 116.07) * mm});
            skLineSegment(sketch, "E825", {"start": v(1344.28, 116.07) * mm, "end": v(1349.47, 115.4) * mm});
            skLineSegment(sketch, "E826", {"start": v(1349.47, 115.4) * mm, "end": v(1353.53, 115.17) * mm});
            skLineSegment(sketch, "E827", {"start": v(1353.53, 115.17) * mm, "end": v(1354.88, 115.17) * mm});
            skLineSegment(sketch, "E828", {"start": v(1354.88, 115.17) * mm, "end": v(1356.22, 115.17) * mm});
            skLineSegment(sketch, "E829", {"start": v(1356.22, 115.17) * mm, "end": v(1360.26, 115.42) * mm});
            skLineSegment(sketch, "E830", {"start": v(1360.26, 115.42) * mm, "end": v(1365.42, 116.16) * mm});
            skLineSegment(sketch, "E831", {"start": v(1365.42, 116.16) * mm, "end": v(1370.3, 117.36) * mm});
            skLineSegment(sketch, "E832", {"start": v(1370.3, 117.36) * mm, "end": v(1374.87, 119.02) * mm});
            skLineSegment(sketch, "E833", {"start": v(1374.87, 119.02) * mm, "end": v(1379.13, 121.13) * mm});
            skLineSegment(sketch, "E834", {"start": v(1379.13, 121.13) * mm, "end": v(1383.12, 123.66) * mm});
            skLineSegment(sketch, "E835", {"start": v(1383.12, 123.66) * mm, "end": v(1386.8, 126.61) * mm});
            skLineSegment(sketch, "E836", {"start": v(1386.8, 126.61) * mm, "end": v(1390.16, 129.96) * mm});
            skLineSegment(sketch, "E837", {"start": v(1390.16, 129.96) * mm, "end": v(1393.1, 133.7) * mm});
            skLineSegment(sketch, "E838", {"start": v(1393.1, 133.7) * mm, "end": v(1395.77, 137.81) * mm});
            skLineSegment(sketch, "E839", {"start": v(1395.77, 137.81) * mm, "end": v(1398, 142.28) * mm});
            skLineSegment(sketch, "E840", {"start": v(1398, 142.28) * mm, "end": v(1399.89, 147.1) * mm});
            skLineSegment(sketch, "E841", {"start": v(1399.89, 147.1) * mm, "end": v(1401.36, 152.24) * mm});
            skLineSegment(sketch, "E842", {"start": v(1401.36, 152.24) * mm, "end": v(1402.45, 157.7) * mm});
            skLineSegment(sketch, "E843", {"start": v(1402.45, 157.7) * mm, "end": v(1403.09, 163.46) * mm});
            skLineSegment(sketch, "E844", {"start": v(1403.09, 163.46) * mm, "end": v(1403.31, 168) * mm});
            skLineSegment(sketch, "E845", {"start": v(1403.31, 168) * mm, "end": v(1403.31, 169.51) * mm});
            skLineSegment(sketch, "E846", {"start": v(1403.31, 169.51) * mm, "end": v(1403.31, 172.18) * mm});
            skLineSegment(sketch, "E847", {"start": v(1403.31, 172.18) * mm, "end": v(1402.58, 180.17) * mm});
            skLineSegment(sketch, "E848", {"start": v(1402.58, 180.17) * mm, "end": v(1400.4, 190.47) * mm});
            skLineSegment(sketch, "E849", {"start": v(1400.4, 190.47) * mm, "end": v(1396.74, 200.36) * mm});
            skLineSegment(sketch, "E850", {"start": v(1396.74, 200.36) * mm, "end": v(1391.7, 209.79) * mm});
            skLineSegment(sketch, "E851", {"start": v(1391.7, 209.79) * mm, "end": v(1385.36, 218.7) * mm});
            skLineSegment(sketch, "E852", {"start": v(1385.36, 218.7) * mm, "end": v(1377.63, 227.03) * mm});
            skLineSegment(sketch, "E853", {"start": v(1377.63, 227.03) * mm, "end": v(1368.64, 234.73) * mm});
            skLineSegment(sketch, "E854", {"start": v(1368.64, 234.73) * mm, "end": v(1361, 240.13) * mm});
            skLineSegment(sketch, "E855", {"start": v(1361, 240.13) * mm, "end": v(1358.36, 241.75) * mm});
            skLineSegment(sketch, "E856", {"start": v(1358.36, 241.75) * mm, "end": v(1355.9, 243.28) * mm});
            skLineSegment(sketch, "E857", {"start": v(1355.9, 243.28) * mm, "end": v(1348.1, 247.43) * mm});
            skLineSegment(sketch, "E858", {"start": v(1348.1, 247.43) * mm, "end": v(1337.02, 252.42) * mm});
            skLineSegment(sketch, "E859", {"start": v(1337.02, 252.42) * mm, "end": v(1325.16, 256.69) * mm});
            skLineSegment(sketch, "E860", {"start": v(1325.16, 256.69) * mm, "end": v(1312.69, 260.22) * mm});
            skLineSegment(sketch, "E861", {"start": v(1312.69, 260.22) * mm, "end": v(1299.56, 263) * mm});
            skLineSegment(sketch, "E862", {"start": v(1299.56, 263) * mm, "end": v(1285.97, 265.02) * mm});
            skLineSegment(sketch, "E863", {"start": v(1285.97, 265.02) * mm, "end": v(1271.9, 266.24) * mm});
            skLineSegment(sketch, "E864", {"start": v(1271.9, 266.24) * mm, "end": v(1261.1, 266.65) * mm});
            skLineSegment(sketch, "E865", {"start": v(1261.1, 266.65) * mm, "end": v(1257.52, 266.65) * mm});
            skLineSegment(sketch, "E866", {"start": v(1257.52, 266.65) * mm, "end": v(1253.1, 266.65) * mm});
            skLineSegment(sketch, "E867", {"start": v(1253.1, 266.65) * mm, "end": v(1239.9, 265.98) * mm});
            skLineSegment(sketch, "E868", {"start": v(1239.9, 265.98) * mm, "end": v(1223.56, 264.03) * mm});
            skLineSegment(sketch, "E869", {"start": v(1223.56, 264.03) * mm, "end": v(1208.45, 260.88) * mm});
            skLineSegment(sketch, "E870", {"start": v(1208.45, 260.88) * mm, "end": v(1194.53, 256.62) * mm});
            skLineSegment(sketch, "E871", {"start": v(1194.53, 256.62) * mm, "end": v(1181.8, 251.33) * mm});
            skLineSegment(sketch, "E872", {"start": v(1181.8, 251.33) * mm, "end": v(1170.3, 245.11) * mm});
            skLineSegment(sketch, "E873", {"start": v(1170.3, 245.11) * mm, "end": v(1159.93, 238.04) * mm});
            skLineSegment(sketch, "E874", {"start": v(1159.93, 238.04) * mm, "end": v(1150.74, 230.2) * mm});
            skLineSegment(sketch, "E875", {"start": v(1150.74, 230.2) * mm, "end": v(1142.66, 221.69) * mm});
            skLineSegment(sketch, "E876", {"start": v(1142.66, 221.69) * mm, "end": v(1135.73, 212.58) * mm});
            skLineSegment(sketch, "E877", {"start": v(1135.73, 212.58) * mm, "end": v(1129.88, 202.97) * mm});
            skLineSegment(sketch, "E878", {"start": v(1129.88, 202.97) * mm, "end": v(1125.16, 192.93) * mm});
            skLineSegment(sketch, "E879", {"start": v(1125.16, 192.93) * mm, "end": v(1121.48, 182.57) * mm});
            skLineSegment(sketch, "E880", {"start": v(1121.48, 182.57) * mm, "end": v(1118.88, 171.96) * mm});
            skLineSegment(sketch, "E881", {"start": v(1118.88, 171.96) * mm, "end": v(1117.34, 161.18) * mm});
            skLineSegment(sketch, "E882", {"start": v(1117.34, 161.18) * mm, "end": v(1116.83, 153.05) * mm});
            skLineSegment(sketch, "E883", {"start": v(1116.83, 153.05) * mm, "end": v(1116.83, 150.33) * mm});
            skLineSegment(sketch, "E884", {"start": v(1116.83, 150.33) * mm, "end": v(1116.83, 148.45) * mm});
            skLineSegment(sketch, "E885", {"start": v(1116.83, 148.45) * mm, "end": v(1117.06, 142.8) * mm});
            skLineSegment(sketch, "E886", {"start": v(1117.06, 142.8) * mm, "end": v(1117.7, 135.65) * mm});
            skLineSegment(sketch, "E887", {"start": v(1117.7, 135.65) * mm, "end": v(1118.76, 128.83) * mm});
            skLineSegment(sketch, "E888", {"start": v(1118.76, 128.83) * mm, "end": v(1120.23, 122.36) * mm});
            skLineSegment(sketch, "E889", {"start": v(1120.23, 122.36) * mm, "end": v(1122.06, 116.22) * mm});
            skLineSegment(sketch, "E890", {"start": v(1122.06, 116.22) * mm, "end": v(1124.27, 110.4) * mm});
            skLineSegment(sketch, "E891", {"start": v(1124.27, 110.4) * mm, "end": v(1126.8, 104.9) * mm});
            skLineSegment(sketch, "E892", {"start": v(1126.8, 104.9) * mm, "end": v(1129.7, 99.68) * mm});
            skLineSegment(sketch, "E893", {"start": v(1129.7, 99.68) * mm, "end": v(1132.88, 94.74) * mm});
            skLineSegment(sketch, "E894", {"start": v(1132.88, 94.74) * mm, "end": v(1136.36, 90.09) * mm});
            skLineSegment(sketch, "E895", {"start": v(1136.36, 90.09) * mm, "end": v(1140.14, 85.7) * mm});
            skLineSegment(sketch, "E896", {"start": v(1140.14, 85.7) * mm, "end": v(1144.16, 81.55) * mm});
            skLineSegment(sketch, "E897", {"start": v(1144.16, 81.55) * mm, "end": v(1148.45, 77.66) * mm});
            skLineSegment(sketch, "E898", {"start": v(1148.45, 77.66) * mm, "end": v(1152.95, 74) * mm});
            skLineSegment(sketch, "E899", {"start": v(1152.95, 74) * mm, "end": v(1157.67, 70.54) * mm});
            skLineSegment(sketch, "E900", {"start": v(1157.67, 70.54) * mm, "end": v(1162.57, 67.3) * mm});
            skLineSegment(sketch, "E901", {"start": v(1162.57, 67.3) * mm, "end": v(1167.68, 64.26) * mm});
            skLineSegment(sketch, "E902", {"start": v(1167.68, 64.26) * mm, "end": v(1172.94, 61.4) * mm});
            skLineSegment(sketch, "E903", {"start": v(1172.94, 61.4) * mm, "end": v(1178.32, 58.73) * mm});
            skLineSegment(sketch, "E904", {"start": v(1178.32, 58.73) * mm, "end": v(1183.86, 56.22) * mm});
            skLineSegment(sketch, "E905", {"start": v(1183.86, 56.22) * mm, "end": v(1189.5, 53.85) * mm});
            skLineSegment(sketch, "E906", {"start": v(1189.5, 53.85) * mm, "end": v(1195.24, 51.63) * mm});
            skLineSegment(sketch, "E907", {"start": v(1195.24, 51.63) * mm, "end": v(1201.05, 49.55) * mm});
            skLineSegment(sketch, "E908", {"start": v(1201.05, 49.55) * mm, "end": v(1206.95, 47.58) * mm});
            skLineSegment(sketch, "E909", {"start": v(1206.95, 47.58) * mm, "end": v(1212.9, 45.72) * mm});
            skLineSegment(sketch, "E910", {"start": v(1212.9, 45.72) * mm, "end": v(1218.8, 43.96) * mm});
            skLineSegment(sketch, "E911", {"start": v(1218.8, 43.96) * mm, "end": v(1224.8, 42.3) * mm});
            skLineSegment(sketch, "E912", {"start": v(1224.8, 42.3) * mm, "end": v(1230.77, 40.7) * mm});
            skLineSegment(sketch, "E913", {"start": v(1230.77, 40.7) * mm, "end": v(1236.7, 39.16) * mm});
            skLineSegment(sketch, "E914", {"start": v(1236.7, 39.16) * mm, "end": v(1242.58, 37.69) * mm});
            skLineSegment(sketch, "E915", {"start": v(1242.58, 37.69) * mm, "end": v(1248.45, 36.26) * mm});
            skLineSegment(sketch, "E916", {"start": v(1248.45, 36.26) * mm, "end": v(1252.77, 35.2) * mm});
            skLineSegment(sketch, "E917", {"start": v(1252.77, 35.2) * mm, "end": v(1254.22, 34.85) * mm});
            skLineSegment(sketch, "E918", {"start": v(1254.22, 34.85) * mm, "end": v(1256.8, 34.23) * mm});
            skLineSegment(sketch, "E919", {"start": v(1256.8, 34.23) * mm, "end": v(1264.5, 32.35) * mm});
            skLineSegment(sketch, "E920", {"start": v(1264.5, 32.35) * mm, "end": v(1274.23, 29.88) * mm});
            skLineSegment(sketch, "E921", {"start": v(1274.23, 29.88) * mm, "end": v(1283.43, 27.42) * mm});
            skLineSegment(sketch, "E922", {"start": v(1283.43, 27.42) * mm, "end": v(1292.09, 24.93) * mm});
            skLineSegment(sketch, "E923", {"start": v(1292.09, 24.93) * mm, "end": v(1300.11, 22.37) * mm});
            skLineSegment(sketch, "E924", {"start": v(1300.11, 22.37) * mm, "end": v(1307.56, 19.7) * mm});
            skLineSegment(sketch, "E925", {"start": v(1307.56, 19.7) * mm, "end": v(1314.36, 16.88) * mm});
            skLineSegment(sketch, "E926", {"start": v(1314.36, 16.88) * mm, "end": v(1320.54, 13.87) * mm});
            skLineSegment(sketch, "E927", {"start": v(1320.54, 13.87) * mm, "end": v(1326.07, 10.64) * mm});
            skLineSegment(sketch, "E928", {"start": v(1326.07, 10.64) * mm, "end": v(1330.95, 7.14) * mm});
            skLineSegment(sketch, "E929", {"start": v(1330.95, 7.14) * mm, "end": v(1335.09, 3.34) * mm});
            skLineSegment(sketch, "E930", {"start": v(1335.09, 3.34) * mm, "end": v(1338.54, -0.8) * mm});
            skLineSegment(sketch, "E931", {"start": v(1338.54, -0.8) * mm, "end": v(1341.26, -5.32) * mm});
            skLineSegment(sketch, "E932", {"start": v(1341.26, -5.32) * mm, "end": v(1343.2, -10.27) * mm});
            skLineSegment(sketch, "E933", {"start": v(1343.2, -10.27) * mm, "end": v(1344.39, -15.67) * mm});
            skLineSegment(sketch, "E934", {"start": v(1344.39, -15.67) * mm, "end": v(1344.8, -20.1) * mm});
            skLineSegment(sketch, "E935", {"start": v(1344.8, -20.1) * mm, "end": v(1344.8, -21.56) * mm});
            skLineSegment(sketch, "E936", {"start": v(1344.8, -21.56) * mm, "end": v(1344.8, -23.18) * mm});
            skLineSegment(sketch, "E937", {"start": v(1344.8, -23.18) * mm, "end": v(1344.46, -28.04) * mm});
            skLineSegment(sketch, "E938", {"start": v(1344.46, -28.04) * mm, "end": v(1343.47, -34.02) * mm});
            skLineSegment(sketch, "E939", {"start": v(1343.47, -34.02) * mm, "end": v(1341.85, -39.5) * mm});
            skLineSegment(sketch, "E940", {"start": v(1341.85, -39.5) * mm, "end": v(1339.53, -44.52) * mm});
            skLineSegment(sketch, "E941", {"start": v(1339.53, -44.52) * mm, "end": v(1336.54, -49.1) * mm});
            skLineSegment(sketch, "E942", {"start": v(1336.54, -49.1) * mm, "end": v(1332.83, -53.24) * mm});
            skLineSegment(sketch, "E943", {"start": v(1332.83, -53.24) * mm, "end": v(1328.4, -57) * mm});
            skLineSegment(sketch, "E944", {"start": v(1328.4, -57) * mm, "end": v(1324.57, -59.6) * mm});
            skLineSegment(sketch, "E945", {"start": v(1324.57, -59.6) * mm, "end": v(1323.25, -60.37) * mm});
            skLineSegment(sketch, "E946", {"start": v(1323.25, -60.37) * mm, "end": v(1321.93, -61.15) * mm});
            skLineSegment(sketch, "E947", {"start": v(1321.93, -61.15) * mm, "end": v(1317.7, -63.22) * mm});
            skLineSegment(sketch, "E948", {"start": v(1317.7, -63.22) * mm, "end": v(1311.5, -65.7) * mm});
            skLineSegment(sketch, "E949", {"start": v(1311.5, -65.7) * mm, "end": v(1304.64, -67.83) * mm});
            skLineSegment(sketch, "E950", {"start": v(1304.64, -67.83) * mm, "end": v(1297.17, -69.57) * mm});
            skLineSegment(sketch, "E951", {"start": v(1297.17, -69.57) * mm, "end": v(1289.14, -70.94) * mm});
            skLineSegment(sketch, "E952", {"start": v(1289.14, -70.94) * mm, "end": v(1280.58, -71.92) * mm});
            skLineSegment(sketch, "E953", {"start": v(1280.58, -71.92) * mm, "end": v(1271.51, -72.52) * mm});
            skLineSegment(sketch, "E954", {"start": v(1271.51, -72.52) * mm, "end": v(1264.33, -72.72) * mm});
            skLineSegment(sketch, "E955", {"start": v(1264.33, -72.72) * mm, "end": v(1261.91, -72.72) * mm});
            skLineSegment(sketch, "E956", {"start": v(1261.91, -72.72) * mm, "end": v(1259.83, -72.72) * mm});
            skLineSegment(sketch, "E957", {"start": v(1259.83, -72.72) * mm, "end": v(1253.53, -72.55) * mm});
            skLineSegment(sketch, "E958", {"start": v(1253.53, -72.55) * mm, "end": v(1245.33, -72.06) * mm});
            skLineSegment(sketch, "E959", {"start": v(1245.33, -72.06) * mm, "end": v(1237.48, -71.26) * mm});
            skLineSegment(sketch, "E960", {"start": v(1237.48, -71.26) * mm, "end": v(1229.9, -70.16) * mm});
            skLineSegment(sketch, "E961", {"start": v(1229.9, -70.16) * mm, "end": v(1222.75, -68.75) * mm});
            skLineSegment(sketch, "E962", {"start": v(1222.75, -68.75) * mm, "end": v(1216.01, -67.05) * mm});
            skLineSegment(sketch, "E963", {"start": v(1216.01, -67.05) * mm, "end": v(1209.74, -65.07) * mm});
            skLineSegment(sketch, "E964", {"start": v(1209.74, -65.07) * mm, "end": v(1205.4, -63.42) * mm});
            skLineSegment(sketch, "E965", {"start": v(1205.4, -63.42) * mm, "end": v(1204, -62.8) * mm});
            skLineSegment(sketch, "E966", {"start": v(1204, -62.8) * mm, "end": v(1203, -62.37) * mm});
            skLineSegment(sketch, "E967", {"start": v(1203, -62.37) * mm, "end": v(1200.06, -60.94) * mm});
            skLineSegment(sketch, "E968", {"start": v(1200.06, -60.94) * mm, "end": v(1196.6, -59) * mm});
            skLineSegment(sketch, "E969", {"start": v(1196.6, -59) * mm, "end": v(1193.61, -56.98) * mm});
            skLineSegment(sketch, "E970", {"start": v(1193.61, -56.98) * mm, "end": v(1191.07, -54.92) * mm});
            skLineSegment(sketch, "E971", {"start": v(1191.07, -54.92) * mm, "end": v(1189.1, -52.83) * mm});
            skLineSegment(sketch, "E972", {"start": v(1189.1, -52.83) * mm, "end": v(1187.62, -50.74) * mm});
            skLineSegment(sketch, "E973", {"start": v(1187.62, -50.74) * mm, "end": v(1186.73, -48.67) * mm});
            skLineSegment(sketch, "E974", {"start": v(1186.73, -48.67) * mm, "end": v(1186.42, -47.15) * mm});
            skLineSegment(sketch, "E975", {"start": v(1186.42, -47.15) * mm, "end": v(1186.42, -46.65) * mm});
            skLineSegment(sketch, "E976", {"start": v(1186.42, -46.65) * mm, "end": v(1186.42, -46.14) * mm});
            skLineSegment(sketch, "E977", {"start": v(1186.42, -46.14) * mm, "end": v(1186.63, -44.62) * mm});
            skLineSegment(sketch, "E978", {"start": v(1186.63, -44.62) * mm, "end": v(1187.36, -42.87) * mm});
            skLineSegment(sketch, "E979", {"start": v(1187.36, -42.87) * mm, "end": v(1188.89, -40.88) * mm});
            skLineSegment(sketch, "E980", {"start": v(1188.89, -40.88) * mm, "end": v(1190.87, -38.82) * mm});
            skLineSegment(sketch, "E981", {"start": v(1190.87, -38.82) * mm, "end": v(1191.5, -38.15) * mm});
            skLineSegment(sketch, "E982", {"start": v(1191.5, -38.15) * mm, "end": v(1192.09, -37.56) * mm});
            skLineSegment(sketch, "E983", {"start": v(1192.09, -37.56) * mm, "end": v(1193.87, -35.75) * mm});
            skLineSegment(sketch, "E984", {"start": v(1193.87, -35.75) * mm, "end": v(1196.33, -33) * mm});
            skLineSegment(sketch, "E985", {"start": v(1196.33, -33) * mm, "end": v(1198.8, -29.8) * mm});
            skLineSegment(sketch, "E986", {"start": v(1198.8, -29.8) * mm, "end": v(1201.13, -26.1) * mm});
            skLineSegment(sketch, "E987", {"start": v(1201.13, -26.1) * mm, "end": v(1203.21, -21.8) * mm});
            skLineSegment(sketch, "E988", {"start": v(1203.21, -21.8) * mm, "end": v(1204.86, -16.83) * mm});
            skLineSegment(sketch, "E989", {"start": v(1204.86, -16.83) * mm, "end": v(1205.96, -11.12) * mm});
            skLineSegment(sketch, "E990", {"start": v(1205.96, -11.12) * mm, "end": v(1206.36, -6.23) * mm});
            skLineSegment(sketch, "E991", {"start": v(1206.36, -6.23) * mm, "end": v(1206.36, -4.6) * mm});
            skLineSegment(sketch, "E992", {"start": v(1206.36, -4.6) * mm, "end": v(1206.36, -3.32) * mm});
            skLineSegment(sketch, "E993", {"start": v(1206.36, -3.32) * mm, "end": v(1206.1, 0.5) * mm});
            skLineSegment(sketch, "E994", {"start": v(1206.1, 0.5) * mm, "end": v(1205.42, 5.36) * mm});
            skLineSegment(sketch, "E995", {"start": v(1205.42, 5.36) * mm, "end": v(1204.3, 10) * mm});
            skLineSegment(sketch, "E996", {"start": v(1204.3, 10) * mm, "end": v(1202.73, 14.41) * mm});
            skLineSegment(sketch, "E997", {"start": v(1202.73, 14.41) * mm, "end": v(1200.77, 18.55) * mm});
            skLineSegment(sketch, "E998", {"start": v(1200.77, 18.55) * mm, "end": v(1198.41, 22.42) * mm});
            skLineSegment(sketch, "E999", {"start": v(1198.41, 22.42) * mm, "end": v(1195.7, 26) * mm});
            skLineSegment(sketch, "E1000", {"start": v(1195.7, 26) * mm, "end": v(1192.62, 29.26) * mm});
            skLineSegment(sketch, "E1001", {"start": v(1192.62, 29.26) * mm, "end": v(1189.2, 32.2) * mm});
            skLineSegment(sketch, "E1002", {"start": v(1189.2, 32.2) * mm, "end": v(1185.46, 34.8) * mm});
            skLineSegment(sketch, "E1003", {"start": v(1185.46, 34.8) * mm, "end": v(1181.4, 37.05) * mm});
            skLineSegment(sketch, "E1004", {"start": v(1181.4, 37.05) * mm, "end": v(1177.08, 38.93) * mm});
            skLineSegment(sketch, "E1005", {"start": v(1177.08, 38.93) * mm, "end": v(1172.45, 40.41) * mm});
            skLineSegment(sketch, "E1006", {"start": v(1172.45, 40.41) * mm, "end": v(1167.6, 41.5) * mm});
            skLineSegment(sketch, "E1007", {"start": v(1167.6, 41.5) * mm, "end": v(1162.5, 42.15) * mm});
            skLineSegment(sketch, "E1008", {"start": v(1162.5, 42.15) * mm, "end": v(1158.48, 42.37) * mm});
            skLineSegment(sketch, "E1009", {"start": v(1158.48, 42.37) * mm, "end": v(1157.16, 42.37) * mm});
            skLineSegment(sketch, "E1010", {"start": v(1157.16, 42.37) * mm, "end": v(1155.77, 42.37) * mm});
            skLineSegment(sketch, "E1011", {"start": v(1155.77, 42.37) * mm, "end": v(1151.55, 42.13) * mm});
            skLineSegment(sketch, "E1012", {"start": v(1151.55, 42.13) * mm, "end": v(1146.22, 41.4) * mm});
            skLineSegment(sketch, "E1013", {"start": v(1146.22, 41.4) * mm, "end": v(1141.19, 40.19) * mm});
            skLineSegment(sketch, "E1014", {"start": v(1141.19, 40.19) * mm, "end": v(1136.49, 38.52) * mm});
            skLineSegment(sketch, "E1015", {"start": v(1136.49, 38.52) * mm, "end": v(1132.12, 36.39) * mm});
            skLineSegment(sketch, "E1016", {"start": v(1132.12, 36.39) * mm, "end": v(1128.08, 33.82) * mm});
            skLineSegment(sketch, "E1017", {"start": v(1128.08, 33.82) * mm, "end": v(1124.37, 30.8) * mm});
            skLineSegment(sketch, "E1018", {"start": v(1124.37, 30.8) * mm, "end": v(1121.02, 27.38) * mm});
            skLineSegment(sketch, "E1019", {"start": v(1121.02, 27.38) * mm, "end": v(1118.05, 23.53) * mm});
            skLineSegment(sketch, "E1020", {"start": v(1118.05, 23.53) * mm, "end": v(1115.43, 19.28) * mm});
            skLineSegment(sketch, "E1021", {"start": v(1115.43, 19.28) * mm, "end": v(1113.2, 14.63) * mm});
            skLineSegment(sketch, "E1022", {"start": v(1113.2, 14.63) * mm, "end": v(1111.34, 9.6) * mm});
            skLineSegment(sketch, "E1023", {"start": v(1111.34, 9.6) * mm, "end": v(1109.9, 4.19) * mm});
            skLineSegment(sketch, "E1024", {"start": v(1109.9, 4.19) * mm, "end": v(1108.85, -1.58) * mm});
            skLineSegment(sketch, "E1025", {"start": v(1108.85, -1.58) * mm, "end": v(1108.2, -7.71) * mm});
            skLineSegment(sketch, "E1026", {"start": v(1108.2, -7.71) * mm, "end": v(1107.99, -12.56) * mm});
            skLineSegment(sketch, "E1027", {"start": v(1107.99, -12.56) * mm, "end": v(1107.99, -14.19) * mm});
            skLineSegment(sketch, "E1028", {"start": v(1107.99, -14.19) * mm, "end": v(1107.99, -16.8) * mm});
            skLineSegment(sketch, "E1029", {"start": v(1107.99, -16.8) * mm, "end": v(1108.67, -24.64) * mm});
            skLineSegment(sketch, "E1030", {"start": v(1108.67, -24.64) * mm, "end": v(1110.7, -34.79) * mm});
            skLineSegment(sketch, "E1031", {"start": v(1110.7, -34.79) * mm, "end": v(1114.08, -44.58) * mm});
            skLineSegment(sketch, "E1032", {"start": v(1114.08, -44.58) * mm, "end": v(1118.73, -53.96) * mm});
            skLineSegment(sketch, "E1033", {"start": v(1118.73, -53.96) * mm, "end": v(1124.65, -62.88) * mm});
            skLineSegment(sketch, "E1034", {"start": v(1124.65, -62.88) * mm, "end": v(1131.79, -71.27) * mm});
            skLineSegment(sketch, "E1035", {"start": v(1131.79, -71.27) * mm, "end": v(1140.12, -79.08) * mm});
            skLineSegment(sketch, "E1036", {"start": v(1140.12, -79.08) * mm, "end": v(1147.16, -84.58) * mm});
            skLineSegment(sketch, "E1037", {"start": v(1147.16, -84.58) * mm, "end": v(1149.62, -86.26) * mm});
            skLineSegment(sketch, "E1038", {"start": v(1149.62, -86.26) * mm, "end": v(1152.24, -88.05) * mm});
            skLineSegment(sketch, "E1039", {"start": v(1152.24, -88.05) * mm, "end": v(1160.52, -92.9) * mm});
            skLineSegment(sketch, "E1040", {"start": v(1160.52, -92.9) * mm, "end": v(1172.43, -98.69) * mm});
            skLineSegment(sketch, "E1041", {"start": v(1172.43, -98.69) * mm, "end": v(1185.33, -103.62) * mm});
            skLineSegment(sketch, "E1042", {"start": v(1185.33, -103.62) * mm, "end": v(1199.15, -107.7) * mm});
            skLineSegment(sketch, "E1043", {"start": v(1199.15, -107.7) * mm, "end": v(1213.83, -110.88) * mm});
            skLineSegment(sketch, "E1044", {"start": v(1213.83, -110.88) * mm, "end": v(1229.35, -113.17) * mm});
            skLineSegment(sketch, "E1045", {"start": v(1229.35, -113.17) * mm, "end": v(1245.66, -114.55) * mm});
            skLineSegment(sketch, "E1046", {"start": v(1245.66, -114.55) * mm, "end": v(1258.38, -115.02) * mm});
            skLineSegment(sketch, "E1047", {"start": v(1258.38, -115.02) * mm, "end": v(1262.65, -115.02) * mm});
            skLineSegment(sketch, "E1048", {"start": v(1262.65, -115.02) * mm, "end": v(1266.81, -115.02) * mm});
            skLineSegment(sketch, "E1049", {"start": v(1266.81, -115.02) * mm, "end": v(1279.34, -114.48) * mm});
            skLineSegment(sketch, "E1050", {"start": v(1279.34, -114.48) * mm, "end": v(1295.21, -112.87) * mm});
            skLineSegment(sketch, "E1051", {"start": v(1295.21, -112.87) * mm, "end": v(1310.32, -110.21) * mm});
            skLineSegment(sketch, "E1052", {"start": v(1310.32, -110.21) * mm, "end": v(1324.52, -106.51) * mm});
            skLineSegment(sketch, "E1053", {"start": v(1324.52, -106.51) * mm, "end": v(1337.83, -101.8) * mm});
            skLineSegment(sketch, "E1054", {"start": v(1337.83, -101.8) * mm, "end": v(1350.18, -96.06) * mm});
            skLineSegment(sketch, "E1055", {"start": v(1350.18, -96.06) * mm, "end": v(1361.5, -89.33) * mm});
            skLineSegment(sketch, "E1056", {"start": v(1361.5, -89.33) * mm, "end": v(1369.3, -83.7) * mm});
            skLineSegment(sketch, "E1057", {"start": v(1369.3, -83.7) * mm, "end": v(1371.77, -81.63) * mm});
            skLineSegment(sketch, "E1058", {"start": v(1371.77, -81.63) * mm, "end": v(1374.05, -79.68) * mm});
            skLineSegment(sketch, "E1059", {"start": v(1374.05, -79.68) * mm, "end": v(1380.58, -73.36) * mm});
            skLineSegment(sketch, "E1060", {"start": v(1380.58, -73.36) * mm, "end": v(1388.28, -64.36) * mm});
            skLineSegment(sketch, "E1061", {"start": v(1388.28, -64.36) * mm, "end": v(1394.83, -54.68) * mm});
            skLineSegment(sketch, "E1062", {"start": v(1394.83, -54.68) * mm, "end": v(1400.24, -44.35) * mm});
            skLineSegment(sketch, "E1063", {"start": v(1400.24, -44.35) * mm, "end": v(1404.48, -33.4) * mm});
            skLineSegment(sketch, "E1064", {"start": v(1404.48, -33.4) * mm, "end": v(1407.5, -21.87) * mm});
            skLineSegment(sketch, "E1065", {"start": v(1407.5, -21.87) * mm, "end": v(1409.33, -9.8) * mm});
            skLineSegment(sketch, "E1066", {"start": v(1409.33, -9.8) * mm, "end": v(1409.94, -0.37) * mm});
            skLineSegment(sketch, "E1067", {"start": v(1409.94, -0.37) * mm, "end": v(1409.94, 2.77) * mm});
            skLineSegment(sketch, "E1068", {"start": v(1409.94, 2.77) * mm, "end": v(1409.94, 4.73) * mm});
            skLineSegment(sketch, "E1069", {"start": v(1409.94, 4.73) * mm, "end": v(1409.74, 10.6) * mm});
            skLineSegment(sketch, "E1070", {"start": v(1409.74, 10.6) * mm, "end": v(1409.05, 18.05) * mm});
            skLineSegment(sketch, "E1071", {"start": v(1409.05, 18.05) * mm, "end": v(1407.99, 25.14) * mm});
            skLineSegment(sketch, "E1072", {"start": v(1407.99, 25.14) * mm, "end": v(1406.49, 31.87) * mm});
            skLineSegment(sketch, "E1073", {"start": v(1406.49, 31.87) * mm, "end": v(1404.6, 38.27) * mm});
            skLineSegment(sketch, "E1074", {"start": v(1404.6, 38.27) * mm, "end": v(1402.35, 44.34) * mm});
            skLineSegment(sketch, "E1075", {"start": v(1402.35, 44.34) * mm, "end": v(1399.78, 50.1) * mm});
            skLineSegment(sketch, "E1076", {"start": v(1399.78, 50.1) * mm, "end": v(1396.81, 55.54) * mm});
            skLineSegment(sketch, "E1077", {"start": v(1396.81, 55.54) * mm, "end": v(1393.56, 60.7) * mm});
            skLineSegment(sketch, "E1078", {"start": v(1393.56, 60.7) * mm, "end": v(1390, 65.57) * mm});
            skLineSegment(sketch, "E1079", {"start": v(1390, 65.57) * mm, "end": v(1386.17, 70.17) * mm});
            skLineSegment(sketch, "E1080", {"start": v(1386.17, 70.17) * mm, "end": v(1382.08, 74.5) * mm});
            skLineSegment(sketch, "E1081", {"start": v(1382.08, 74.5) * mm, "end": v(1377.69, 78.6) * mm});
            skLineSegment(sketch, "E1082", {"start": v(1377.69, 78.6) * mm, "end": v(1373.11, 82.45) * mm});
            skLineSegment(sketch, "E1083", {"start": v(1373.11, 82.45) * mm, "end": v(1368.29, 86.08) * mm});
            skLineSegment(sketch, "E1084", {"start": v(1368.29, 86.08) * mm, "end": v(1363.26, 89.49) * mm});
            skLineSegment(sketch, "E1085", {"start": v(1363.26, 89.49) * mm, "end": v(1358.08, 92.7) * mm});
            skLineSegment(sketch, "E1086", {"start": v(1358.08, 92.7) * mm, "end": v(1352.72, 95.72) * mm});
            skLineSegment(sketch, "E1087", {"start": v(1352.72, 95.72) * mm, "end": v(1347.18, 98.55) * mm});
            skLineSegment(sketch, "E1088", {"start": v(1347.18, 98.55) * mm, "end": v(1341.54, 101.22) * mm});
            skLineSegment(sketch, "E1089", {"start": v(1341.54, 101.22) * mm, "end": v(1335.78, 103.72) * mm});
            skLineSegment(sketch, "E1090", {"start": v(1335.78, 103.72) * mm, "end": v(1329.93, 106.08) * mm});
            skLineSegment(sketch, "E1091", {"start": v(1329.93, 106.08) * mm, "end": v(1324.02, 108.3) * mm});
            skLineSegment(sketch, "E1092", {"start": v(1324.02, 108.3) * mm, "end": v(1318, 110.4) * mm});
            skLineSegment(sketch, "E1093", {"start": v(1318, 110.4) * mm, "end": v(1311.95, 112.4) * mm});
            skLineSegment(sketch, "E1094", {"start": v(1311.95, 112.4) * mm, "end": v(1305.88, 114.27) * mm});
            skLineSegment(sketch, "E1095", {"start": v(1305.88, 114.27) * mm, "end": v(1299.76, 116.07) * mm});
            skLineSegment(sketch, "E1096", {"start": v(1299.76, 116.07) * mm, "end": v(1293.69, 117.78) * mm});
            skLineSegment(sketch, "E1097", {"start": v(1293.69, 117.78) * mm, "end": v(1287.64, 119.43) * mm});
            skLineSegment(sketch, "E1098", {"start": v(1287.64, 119.43) * mm, "end": v(1281.6, 121.02) * mm});
            skLineSegment(sketch, "E1099", {"start": v(1281.6, 121.02) * mm, "end": v(1275.63, 122.56) * mm});
            skLineSegment(sketch, "E1100", {"start": v(1275.63, 122.56) * mm, "end": v(1271.18, 123.7) * mm});
            skLineSegment(sketch, "E1101", {"start": v(1271.18, 123.7) * mm, "end": v(1269.71, 124.07) * mm});
            skLineSegment(sketch, "E1102", {"start": v(1596, 413.6) * mm, "end": v(1585.03, 420.44) * mm});
            skLineSegment(sketch, "E1103", {"start": v(1585.03, 420.44) * mm, "end": v(1562.17, 388.45) * mm});
            skLineSegment(sketch, "E1104", {"start": v(1562.17, 388.45) * mm, "end": v(1573.24, 380.43) * mm});
            skLineSegment(sketch, "E1105", {"start": v(1573.24, 380.43) * mm, "end": v(1577.25, 377.52) * mm});
            skLineSegment(sketch, "E1106", {"start": v(1577.25, 377.52) * mm, "end": v(1588.96, 368.36) * mm});
            skLineSegment(sketch, "E1107", {"start": v(1588.96, 368.36) * mm, "end": v(1603.29, 355.9) * mm});
            skLineSegment(sketch, "E1108", {"start": v(1603.29, 355.9) * mm, "end": v(1616.34, 343) * mm});
            skLineSegment(sketch, "E1109", {"start": v(1616.34, 343) * mm, "end": v(1628.1, 329.58) * mm});
            skLineSegment(sketch, "E1110", {"start": v(1628.1, 329.58) * mm, "end": v(1638.65, 315.59) * mm});
            skLineSegment(sketch, "E1111", {"start": v(1638.65, 315.59) * mm, "end": v(1648.04, 300.96) * mm});
            skLineSegment(sketch, "E1112", {"start": v(1648.04, 300.96) * mm, "end": v(1656.27, 285.64) * mm});
            skLineSegment(sketch, "E1113", {"start": v(1656.27, 285.64) * mm, "end": v(1661.78, 273.65) * mm});
            skLineSegment(sketch, "E1114", {"start": v(1661.78, 273.65) * mm, "end": v(1663.44, 269.58) * mm});
            skLineSegment(sketch, "E1115", {"start": v(1663.44, 269.58) * mm, "end": v(1665.01, 265.78) * mm});
            skLineSegment(sketch, "E1116", {"start": v(1665.01, 265.78) * mm, "end": v(1669.1, 254.21) * mm});
            skLineSegment(sketch, "E1117", {"start": v(1669.1, 254.21) * mm, "end": v(1673.93, 237.93) * mm});
            skLineSegment(sketch, "E1118", {"start": v(1673.93, 237.93) * mm, "end": v(1678.02, 220.66) * mm});
            skLineSegment(sketch, "E1119", {"start": v(1678.02, 220.66) * mm, "end": v(1681.3, 202.3) * mm});
            skLineSegment(sketch, "E1120", {"start": v(1681.3, 202.3) * mm, "end": v(1683.83, 182.79) * mm});
            skLineSegment(sketch, "E1121", {"start": v(1683.83, 182.79) * mm, "end": v(1685.64, 162.02) * mm});
            skLineSegment(sketch, "E1122", {"start": v(1685.64, 162.02) * mm, "end": v(1686.73, 139.92) * mm});
            skLineSegment(sketch, "E1123", {"start": v(1686.73, 139.92) * mm, "end": v(1687.08, 122.28) * mm});
            skLineSegment(sketch, "E1124", {"start": v(1687.08, 122.28) * mm, "end": v(1687.08, 116.4) * mm});
            skLineSegment(sketch, "E1125", {"start": v(1687.08, 116.4) * mm, "end": v(1687.08, 110.52) * mm});
            skLineSegment(sketch, "E1126", {"start": v(1687.08, 110.52) * mm, "end": v(1686.73, 92.88) * mm});
            skLineSegment(sketch, "E1127", {"start": v(1686.73, 92.88) * mm, "end": v(1685.64, 70.78) * mm});
            skLineSegment(sketch, "E1128", {"start": v(1685.64, 70.78) * mm, "end": v(1683.83, 50.01) * mm});
            skLineSegment(sketch, "E1129", {"start": v(1683.83, 50.01) * mm, "end": v(1681.3, 30.5) * mm});
            skLineSegment(sketch, "E1130", {"start": v(1681.3, 30.5) * mm, "end": v(1678.02, 12.14) * mm});
            skLineSegment(sketch, "E1131", {"start": v(1678.02, 12.14) * mm, "end": v(1673.93, -5.14) * mm});
            skLineSegment(sketch, "E1132", {"start": v(1673.93, -5.14) * mm, "end": v(1669.1, -21.42) * mm});
            skLineSegment(sketch, "E1133", {"start": v(1669.1, -21.42) * mm, "end": v(1665.01, -33) * mm});
            skLineSegment(sketch, "E1134", {"start": v(1665.01, -33) * mm, "end": v(1663.44, -36.78) * mm});
            skLineSegment(sketch, "E1135", {"start": v(1663.44, -36.78) * mm, "end": v(1661.78, -40.86) * mm});
            skLineSegment(sketch, "E1136", {"start": v(1661.78, -40.86) * mm, "end": v(1656.27, -52.85) * mm});
            skLineSegment(sketch, "E1137", {"start": v(1656.27, -52.85) * mm, "end": v(1648.04, -68.17) * mm});
            skLineSegment(sketch, "E1138", {"start": v(1648.04, -68.17) * mm, "end": v(1638.65, -82.8) * mm});
            skLineSegment(sketch, "E1139", {"start": v(1638.65, -82.8) * mm, "end": v(1628.1, -96.78) * mm});
            skLineSegment(sketch, "E1140", {"start": v(1628.1, -96.78) * mm, "end": v(1616.34, -110.2) * mm});
            skLineSegment(sketch, "E1141", {"start": v(1616.34, -110.2) * mm, "end": v(1603.29, -123.11) * mm});
            skLineSegment(sketch, "E1142", {"start": v(1603.29, -123.11) * mm, "end": v(1588.96, -135.57) * mm});
            skLineSegment(sketch, "E1143", {"start": v(1588.96, -135.57) * mm, "end": v(1577.25, -144.73) * mm});
            skLineSegment(sketch, "E1144", {"start": v(1577.25, -144.73) * mm, "end": v(1573.24, -147.64) * mm});
            skLineSegment(sketch, "E1145", {"start": v(1573.24, -147.64) * mm, "end": v(1562.17, -155.66) * mm});
            skLineSegment(sketch, "E1146", {"start": v(1562.17, -155.66) * mm, "end": v(1585.03, -187.65) * mm});
            skLineSegment(sketch, "E1147", {"start": v(1585.03, -187.65) * mm, "end": v(1596, -180.8) * mm});
            skLineSegment(sketch, "E1148", {"start": v(1596, -180.8) * mm, "end": v(1597.93, -179.6) * mm});
            skLineSegment(sketch, "E1149", {"start": v(1597.93, -179.6) * mm, "end": v(1603.64, -175.92) * mm});
            skLineSegment(sketch, "E1150", {"start": v(1603.64, -175.92) * mm, "end": v(1611.42, -170.79) * mm});
            skLineSegment(sketch, "E1151", {"start": v(1611.42, -170.79) * mm, "end": v(1619.21, -165.4) * mm});
            skLineSegment(sketch, "E1152", {"start": v(1619.21, -165.4) * mm, "end": v(1627.01, -159.76) * mm});
            skLineSegment(sketch, "E1153", {"start": v(1627.01, -159.76) * mm, "end": v(1634.84, -153.86) * mm});
            skLineSegment(sketch, "E1154", {"start": v(1634.84, -153.86) * mm, "end": v(1642.66, -147.7) * mm});
            skLineSegment(sketch, "E1155", {"start": v(1642.66, -147.7) * mm, "end": v(1650.46, -141.26) * mm});
            skLineSegment(sketch, "E1156", {"start": v(1650.46, -141.26) * mm, "end": v(1658.2, -134.56) * mm});
            skLineSegment(sketch, "E1157", {"start": v(1658.2, -134.56) * mm, "end": v(1665.85, -127.58) * mm});
            skLineSegment(sketch, "E1158", {"start": v(1665.85, -127.58) * mm, "end": v(1673.44, -120.32) * mm});
            skLineSegment(sketch, "E1159", {"start": v(1673.44, -120.32) * mm, "end": v(1680.89, -112.8) * mm});
            skLineSegment(sketch, "E1160", {"start": v(1680.89, -112.8) * mm, "end": v(1688.18, -104.97) * mm});
            skLineSegment(sketch, "E1161", {"start": v(1688.18, -104.97) * mm, "end": v(1695.34, -96.87) * mm});
            skLineSegment(sketch, "E1162", {"start": v(1695.34, -96.87) * mm, "end": v(1702.32, -88.47) * mm});
            skLineSegment(sketch, "E1163", {"start": v(1702.32, -88.47) * mm, "end": v(1709.13, -79.78) * mm});
            skLineSegment(sketch, "E1164", {"start": v(1709.13, -79.78) * mm, "end": v(1715.68, -70.78) * mm});
            skLineSegment(sketch, "E1165", {"start": v(1715.68, -70.78) * mm, "end": v(1722, -61.5) * mm});
            skLineSegment(sketch, "E1166", {"start": v(1722, -61.5) * mm, "end": v(1728.1, -51.9) * mm});
            skLineSegment(sketch, "E1167", {"start": v(1728.1, -51.9) * mm, "end": v(1733.9, -42) * mm});
            skLineSegment(sketch, "E1168", {"start": v(1733.9, -42) * mm, "end": v(1739.36, -31.78) * mm});
            skLineSegment(sketch, "E1169", {"start": v(1739.36, -31.78) * mm, "end": v(1744.54, -21.25) * mm});
            skLineSegment(sketch, "E1170", {"start": v(1744.54, -21.25) * mm, "end": v(1749.39, -10.4) * mm});
            skLineSegment(sketch, "E1171", {"start": v(1749.39, -10.4) * mm, "end": v(1753.86, 0.78) * mm});
            skLineSegment(sketch, "E1172", {"start": v(1753.86, 0.78) * mm, "end": v(1757.92, 12.28) * mm});
            skLineSegment(sketch, "E1173", {"start": v(1757.92, 12.28) * mm, "end": v(1761.63, 24.1) * mm});
            skLineSegment(sketch, "E1174", {"start": v(1761.63, 24.1) * mm, "end": v(1764.88, 36.26) * mm});
            skLineSegment(sketch, "E1175", {"start": v(1764.88, 36.26) * mm, "end": v(1767.7, 48.76) * mm});
            skLineSegment(sketch, "E1176", {"start": v(1767.7, 48.76) * mm, "end": v(1770.01, 61.6) * mm});
            skLineSegment(sketch, "E1177", {"start": v(1770.01, 61.6) * mm, "end": v(1771.9, 74.77) * mm});
            skLineSegment(sketch, "E1178", {"start": v(1771.9, 74.77) * mm, "end": v(1773.27, 88.3) * mm});
            skLineSegment(sketch, "E1179", {"start": v(1773.27, 88.3) * mm, "end": v(1774.08, 102.17) * mm});
            skLineSegment(sketch, "E1180", {"start": v(1774.08, 102.17) * mm, "end": v(1774.36, 112.84) * mm});
            skLineSegment(sketch, "E1181", {"start": v(1774.36, 112.84) * mm, "end": v(1774.36, 116.4) * mm});
            skLineSegment(sketch, "E1182", {"start": v(1774.36, 116.4) * mm, "end": v(1774.36, 119.96) * mm});
            skLineSegment(sketch, "E1183", {"start": v(1774.36, 119.96) * mm, "end": v(1774.08, 130.63) * mm});
            skLineSegment(sketch, "E1184", {"start": v(1774.08, 130.63) * mm, "end": v(1773.27, 144.5) * mm});
            skLineSegment(sketch, "E1185", {"start": v(1773.27, 144.5) * mm, "end": v(1771.9, 158.03) * mm});
            skLineSegment(sketch, "E1186", {"start": v(1771.9, 158.03) * mm, "end": v(1770.01, 171.2) * mm});
            skLineSegment(sketch, "E1187", {"start": v(1770.01, 171.2) * mm, "end": v(1767.7, 184.04) * mm});
            skLineSegment(sketch, "E1188", {"start": v(1767.7, 184.04) * mm, "end": v(1764.88, 196.53) * mm});
            skLineSegment(sketch, "E1189", {"start": v(1764.88, 196.53) * mm, "end": v(1761.63, 208.7) * mm});
            skLineSegment(sketch, "E1190", {"start": v(1761.63, 208.7) * mm, "end": v(1757.92, 220.52) * mm});
            skLineSegment(sketch, "E1191", {"start": v(1757.92, 220.52) * mm, "end": v(1753.86, 232.02) * mm});
            skLineSegment(sketch, "E1192", {"start": v(1753.86, 232.02) * mm, "end": v(1749.39, 243.2) * mm});
            skLineSegment(sketch, "E1193", {"start": v(1749.39, 243.2) * mm, "end": v(1744.54, 254.04) * mm});
            skLineSegment(sketch, "E1194", {"start": v(1744.54, 254.04) * mm, "end": v(1739.36, 264.57) * mm});
            skLineSegment(sketch, "E1195", {"start": v(1739.36, 264.57) * mm, "end": v(1733.9, 274.79) * mm});
            skLineSegment(sketch, "E1196", {"start": v(1733.9, 274.79) * mm, "end": v(1728.1, 284.7) * mm});
            skLineSegment(sketch, "E1197", {"start": v(1728.1, 284.7) * mm, "end": v(1722, 294.29) * mm});
            skLineSegment(sketch, "E1198", {"start": v(1722, 294.29) * mm, "end": v(1715.68, 303.58) * mm});
            skLineSegment(sketch, "E1199", {"start": v(1715.68, 303.58) * mm, "end": v(1709.13, 312.57) * mm});
            skLineSegment(sketch, "E1200", {"start": v(1709.13, 312.57) * mm, "end": v(1702.32, 321.26) * mm});
            skLineSegment(sketch, "E1201", {"start": v(1702.32, 321.26) * mm, "end": v(1695.34, 329.66) * mm});
            skLineSegment(sketch, "E1202", {"start": v(1695.34, 329.66) * mm, "end": v(1688.18, 337.76) * mm});
            skLineSegment(sketch, "E1203", {"start": v(1688.18, 337.76) * mm, "end": v(1680.89, 345.58) * mm});
            skLineSegment(sketch, "E1204", {"start": v(1680.89, 345.58) * mm, "end": v(1673.44, 353.12) * mm});
            skLineSegment(sketch, "E1205", {"start": v(1673.44, 353.12) * mm, "end": v(1665.85, 360.37) * mm});
            skLineSegment(sketch, "E1206", {"start": v(1665.85, 360.37) * mm, "end": v(1658.2, 367.35) * mm});
            skLineSegment(sketch, "E1207", {"start": v(1658.2, 367.35) * mm, "end": v(1650.46, 374.05) * mm});
            skLineSegment(sketch, "E1208", {"start": v(1650.46, 374.05) * mm, "end": v(1642.66, 380.48) * mm});
            skLineSegment(sketch, "E1209", {"start": v(1642.66, 380.48) * mm, "end": v(1634.84, 386.65) * mm});
            skLineSegment(sketch, "E1210", {"start": v(1634.84, 386.65) * mm, "end": v(1627.01, 392.55) * mm});
            skLineSegment(sketch, "E1211", {"start": v(1627.01, 392.55) * mm, "end": v(1619.21, 398.2) * mm});
            skLineSegment(sketch, "E1212", {"start": v(1619.21, 398.2) * mm, "end": v(1611.42, 403.58) * mm});
            skLineSegment(sketch, "E1213", {"start": v(1611.42, 403.58) * mm, "end": v(1603.64, 408.71) * mm});
            skLineSegment(sketch, "E1214", {"start": v(1603.64, 408.71) * mm, "end": v(1597.93, 412.39) * mm});
            skLineSegment(sketch, "E1215", {"start": v(1597.93, 412.39) * mm, "end": v(1596, 413.6) * mm});
            skLineSegment(sketch, "E1216", {"start": v(-702.3, -342.73) * mm, "end": v(-703.97, -342.18) * mm});
            skLineSegment(sketch, "E1217", {"start": v(-703.97, -342.18) * mm, "end": v(-708.93, -340.38) * mm});
            skLineSegment(sketch, "E1218", {"start": v(-708.93, -340.38) * mm, "end": v(-714.46, -338) * mm});
            skLineSegment(sketch, "E1219", {"start": v(-714.46, -338) * mm, "end": v(-718.96, -335.54) * mm});
            skLineSegment(sketch, "E1220", {"start": v(-718.96, -335.54) * mm, "end": v(-722.5, -332.93) * mm});
            skLineSegment(sketch, "E1221", {"start": v(-722.5, -332.93) * mm, "end": v(-725.13, -330.11) * mm});
            skLineSegment(sketch, "E1222", {"start": v(-725.13, -330.11) * mm, "end": v(-726.93, -327.04) * mm});
            skLineSegment(sketch, "E1223", {"start": v(-726.93, -327.04) * mm, "end": v(-727.96, -323.65) * mm});
            skLineSegment(sketch, "E1224", {"start": v(-727.96, -323.65) * mm, "end": v(-728.3, -320.82) * mm});
            skLineSegment(sketch, "E1225", {"start": v(-728.3, -320.82) * mm, "end": v(-728.3, -319.88) * mm});
            skLineSegment(sketch, "E1226", {"start": v(-728.3, -319.88) * mm, "end": v(-728.3, -318.61) * mm});
            skLineSegment(sketch, "E1227", {"start": v(-728.3, -318.61) * mm, "end": v(-727.57, -314.8) * mm});
            skLineSegment(sketch, "E1228", {"start": v(-727.57, -314.8) * mm, "end": v(-725.6, -310.68) * mm});
            skLineSegment(sketch, "E1229", {"start": v(-725.6, -310.68) * mm, "end": v(-722.64, -307.42) * mm});
            skLineSegment(sketch, "E1230", {"start": v(-722.64, -307.42) * mm, "end": v(-719, -304.93) * mm});
            skLineSegment(sketch, "E1231", {"start": v(-719, -304.93) * mm, "end": v(-714.95, -303.14) * mm});
            skLineSegment(sketch, "E1232", {"start": v(-714.95, -303.14) * mm, "end": v(-710.78, -301.96) * mm});
            skLineSegment(sketch, "E1233", {"start": v(-710.78, -301.96) * mm, "end": v(-706.77, -301.31) * mm});
            skLineSegment(sketch, "E1234", {"start": v(-706.77, -301.31) * mm, "end": v(-704.1, -301.12) * mm});
            skLineSegment(sketch, "E1235", {"start": v(-704.1, -301.12) * mm, "end": v(-703.2, -301.12) * mm});
            skLineSegment(sketch, "E1236", {"start": v(-703.2, -301.12) * mm, "end": v(-702.13, -301.12) * mm});
            skLineSegment(sketch, "E1237", {"start": v(-702.13, -301.12) * mm, "end": v(-698.91, -301.4) * mm});
            skLineSegment(sketch, "E1238", {"start": v(-698.91, -301.4) * mm, "end": v(-694.82, -302.18) * mm});
            skLineSegment(sketch, "E1239", {"start": v(-694.82, -302.18) * mm, "end": v(-691.04, -303.28) * mm});
            skLineSegment(sketch, "E1240", {"start": v(-691.04, -303.28) * mm, "end": v(-687.64, -304.56) * mm});
            skLineSegment(sketch, "E1241", {"start": v(-687.64, -304.56) * mm, "end": v(-684.74, -305.89) * mm});
            skLineSegment(sketch, "E1242", {"start": v(-684.74, -305.89) * mm, "end": v(-682.43, -307.1) * mm});
            skLineSegment(sketch, "E1243", {"start": v(-682.43, -307.1) * mm, "end": v(-680.8, -308.05) * mm});
            skLineSegment(sketch, "E1244", {"start": v(-680.8, -308.05) * mm, "end": v(-680.16, -308.45) * mm});
            skLineSegment(sketch, "E1245", {"start": v(-680.16, -308.45) * mm, "end": v(-679.95, -308.59) * mm});
            skLineSegment(sketch, "E1246", {"start": v(-679.95, -308.59) * mm, "end": v(-679.76, -308.7) * mm});
            skLineSegment(sketch, "E1247", {"start": v(-679.76, -308.7) * mm, "end": v(-679.15, -309.08) * mm});
            skLineSegment(sketch, "E1248", {"start": v(-679.15, -309.08) * mm, "end": v(-677.06, -309.8) * mm});
            skLineSegment(sketch, "E1249", {"start": v(-677.06, -309.8) * mm, "end": v(-674.43, -309.8) * mm});
            skLineSegment(sketch, "E1250", {"start": v(-674.43, -309.8) * mm, "end": v(-671.99, -308.74) * mm});
            skLineSegment(sketch, "E1251", {"start": v(-671.99, -308.74) * mm, "end": v(-670.3, -307.25) * mm});
            skLineSegment(sketch, "E1252", {"start": v(-670.3, -307.25) * mm, "end": v(-669.85, -306.66) * mm});
            skLineSegment(sketch, "E1253", {"start": v(-669.85, -306.66) * mm, "end": v(-669.42, -305.95) * mm});
            skLineSegment(sketch, "E1254", {"start": v(-669.42, -305.95) * mm, "end": v(-669.36, -305.82) * mm});
            skLineSegment(sketch, "E1255", {"start": v(-669.36, -305.82) * mm, "end": v(-668.96, -305.13) * mm});
            skLineSegment(sketch, "E1256", {"start": v(-668.96, -305.13) * mm, "end": v(-668.53, -304.47) * mm});
            skLineSegment(sketch, "E1257", {"start": v(-668.53, -304.47) * mm, "end": v(-668.45, -304.36) * mm});
            skLineSegment(sketch, "E1258", {"start": v(-668.45, -304.36) * mm, "end": v(-668.26, -304.08) * mm});
            skLineSegment(sketch, "E1259", {"start": v(-668.26, -304.08) * mm, "end": v(-667.88, -303.49) * mm});
            skLineSegment(sketch, "E1260", {"start": v(-667.88, -303.49) * mm, "end": v(-667.16, -301.44) * mm});
            skLineSegment(sketch, "E1261", {"start": v(-667.16, -301.44) * mm, "end": v(-667.13, -298.79) * mm});
            skLineSegment(sketch, "E1262", {"start": v(-667.13, -298.79) * mm, "end": v(-668.15, -296.3) * mm});
            skLineSegment(sketch, "E1263", {"start": v(-668.15, -296.3) * mm, "end": v(-669.61, -294.6) * mm});
            skLineSegment(sketch, "E1264", {"start": v(-669.61, -294.6) * mm, "end": v(-670.2, -294.17) * mm});
            skLineSegment(sketch, "E1265", {"start": v(-670.2, -294.17) * mm, "end": v(-670.34, -294.07) * mm});
            skLineSegment(sketch, "E1266", {"start": v(-670.34, -294.07) * mm, "end": v(-671, -293.63) * mm});
            skLineSegment(sketch, "E1267", {"start": v(-671, -293.63) * mm, "end": v(-672.95, -292.47) * mm});
            skLineSegment(sketch, "E1268", {"start": v(-672.95, -292.47) * mm, "end": v(-675.93, -290.9) * mm});
            skLineSegment(sketch, "E1269", {"start": v(-675.93, -290.9) * mm, "end": v(-679.84, -289.13) * mm});
            skLineSegment(sketch, "E1270", {"start": v(-679.84, -289.13) * mm, "end": v(-684.6, -287.37) * mm});
            skLineSegment(sketch, "E1271", {"start": v(-684.6, -287.37) * mm, "end": v(-690.12, -285.86) * mm});
            skLineSegment(sketch, "E1272", {"start": v(-690.12, -285.86) * mm, "end": v(-696.3, -284.79) * mm});
            skLineSegment(sketch, "E1273", {"start": v(-696.3, -284.79) * mm, "end": v(-701.35, -284.39) * mm});
            skLineSegment(sketch, "E1274", {"start": v(-701.35, -284.39) * mm, "end": v(-703.03, -284.39) * mm});
            skLineSegment(sketch, "E1275", {"start": v(-703.03, -284.39) * mm, "end": v(-704.44, -284.39) * mm});
            skLineSegment(sketch, "E1276", {"start": v(-704.44, -284.39) * mm, "end": v(-708.65, -284.63) * mm});
            skLineSegment(sketch, "E1277", {"start": v(-708.65, -284.63) * mm, "end": v(-713.81, -285.33) * mm});
            skLineSegment(sketch, "E1278", {"start": v(-713.81, -285.33) * mm, "end": v(-718.54, -286.45) * mm});
            skLineSegment(sketch, "E1279", {"start": v(-718.54, -286.45) * mm, "end": v(-722.83, -287.94) * mm});
            skLineSegment(sketch, "E1280", {"start": v(-722.83, -287.94) * mm, "end": v(-726.71, -289.77) * mm});
            skLineSegment(sketch, "E1281", {"start": v(-726.71, -289.77) * mm, "end": v(-730.19, -291.89) * mm});
            skLineSegment(sketch, "E1282", {"start": v(-730.19, -291.89) * mm, "end": v(-733.28, -294.26) * mm});
            skLineSegment(sketch, "E1283", {"start": v(-733.28, -294.26) * mm, "end": v(-735.99, -296.84) * mm});
            skLineSegment(sketch, "E1284", {"start": v(-735.99, -296.84) * mm, "end": v(-738.33, -299.6) * mm});
            skLineSegment(sketch, "E1285", {"start": v(-738.33, -299.6) * mm, "end": v(-740.32, -302.47) * mm});
            skLineSegment(sketch, "E1286", {"start": v(-740.32, -302.47) * mm, "end": v(-741.96, -305.43) * mm});
            skLineSegment(sketch, "E1287", {"start": v(-741.96, -305.43) * mm, "end": v(-743.29, -308.43) * mm});
            skLineSegment(sketch, "E1288", {"start": v(-743.29, -308.43) * mm, "end": v(-744.3, -311.44) * mm});
            skLineSegment(sketch, "E1289", {"start": v(-744.3, -311.44) * mm, "end": v(-745, -314.4) * mm});
            skLineSegment(sketch, "E1290", {"start": v(-745, -314.4) * mm, "end": v(-745.4, -317.3) * mm});
            skLineSegment(sketch, "E1291", {"start": v(-745.4, -317.3) * mm, "end": v(-745.54, -319.36) * mm});
            skLineSegment(sketch, "E1292", {"start": v(-745.54, -319.36) * mm, "end": v(-745.54, -320.06) * mm});
            skLineSegment(sketch, "E1293", {"start": v(-745.54, -320.06) * mm, "end": v(-745.54, -321.13) * mm});
            skLineSegment(sketch, "E1294", {"start": v(-745.54, -321.13) * mm, "end": v(-745.34, -324.35) * mm});
            skLineSegment(sketch, "E1295", {"start": v(-745.34, -324.35) * mm, "end": v(-744.76, -328.3) * mm});
            skLineSegment(sketch, "E1296", {"start": v(-744.76, -328.3) * mm, "end": v(-743.8, -331.92) * mm});
            skLineSegment(sketch, "E1297", {"start": v(-743.8, -331.92) * mm, "end": v(-742.5, -335.24) * mm});
            skLineSegment(sketch, "E1298", {"start": v(-742.5, -335.24) * mm, "end": v(-740.9, -338.27) * mm});
            skLineSegment(sketch, "E1299", {"start": v(-740.9, -338.27) * mm, "end": v(-738.98, -341.04) * mm});
            skLineSegment(sketch, "E1300", {"start": v(-738.98, -341.04) * mm, "end": v(-736.8, -343.57) * mm});
            skLineSegment(sketch, "E1301", {"start": v(-736.8, -343.57) * mm, "end": v(-734.36, -345.88) * mm});
            skLineSegment(sketch, "E1302", {"start": v(-734.36, -345.88) * mm, "end": v(-731.7, -348) * mm});
            skLineSegment(sketch, "E1303", {"start": v(-731.7, -348) * mm, "end": v(-728.83, -349.93) * mm});
            skLineSegment(sketch, "E1304", {"start": v(-728.83, -349.93) * mm, "end": v(-725.77, -351.7) * mm});
            skLineSegment(sketch, "E1305", {"start": v(-725.77, -351.7) * mm, "end": v(-722.56, -353.35) * mm});
            skLineSegment(sketch, "E1306", {"start": v(-722.56, -353.35) * mm, "end": v(-719.2, -354.88) * mm});
            skLineSegment(sketch, "E1307", {"start": v(-719.2, -354.88) * mm, "end": v(-715.74, -356.31) * mm});
            skLineSegment(sketch, "E1308", {"start": v(-715.74, -356.31) * mm, "end": v(-712.17, -357.68) * mm});
            skLineSegment(sketch, "E1309", {"start": v(-712.17, -357.68) * mm, "end": v(-709.45, -358.67) * mm});
            skLineSegment(sketch, "E1310", {"start": v(-709.45, -358.67) * mm, "end": v(-708.54, -358.99) * mm});
            skLineSegment(sketch, "E1311", {"start": v(-708.54, -358.99) * mm, "end": v(-706.53, -359.67) * mm});
            skLineSegment(sketch, "E1312", {"start": v(-706.53, -359.67) * mm, "end": v(-700.57, -361.87) * mm});
            skLineSegment(sketch, "E1313", {"start": v(-700.57, -361.87) * mm, "end": v(-693.94, -364.7) * mm});
            skLineSegment(sketch, "E1314", {"start": v(-693.94, -364.7) * mm, "end": v(-688.58, -367.54) * mm});
            skLineSegment(sketch, "E1315", {"start": v(-688.58, -367.54) * mm, "end": v(-684.39, -370.47) * mm});
            skLineSegment(sketch, "E1316", {"start": v(-684.39, -370.47) * mm, "end": v(-681.28, -373.56) * mm});
            skLineSegment(sketch, "E1317", {"start": v(-681.28, -373.56) * mm, "end": v(-679.17, -376.87) * mm});
            skLineSegment(sketch, "E1318", {"start": v(-679.17, -376.87) * mm, "end": v(-677.97, -380.5) * mm});
            skLineSegment(sketch, "E1319", {"start": v(-677.97, -380.5) * mm, "end": v(-677.59, -383.5) * mm});
            skLineSegment(sketch, "E1320", {"start": v(-677.59, -383.5) * mm, "end": v(-677.59, -384.5) * mm});
            skLineSegment(sketch, "E1321", {"start": v(-677.59, -384.5) * mm, "end": v(-677.59, -385.43) * mm});
            skLineSegment(sketch, "E1322", {"start": v(-677.59, -385.43) * mm, "end": v(-678.1, -388.26) * mm});
            skLineSegment(sketch, "E1323", {"start": v(-678.1, -388.26) * mm, "end": v(-679.58, -391.78) * mm});
            skLineSegment(sketch, "E1324", {"start": v(-679.58, -391.78) * mm, "end": v(-681.91, -395) * mm});
            skLineSegment(sketch, "E1325", {"start": v(-681.91, -395) * mm, "end": v(-684.98, -397.81) * mm});
            skLineSegment(sketch, "E1326", {"start": v(-684.98, -397.81) * mm, "end": v(-688.69, -400.15) * mm});
            skLineSegment(sketch, "E1327", {"start": v(-688.69, -400.15) * mm, "end": v(-692.91, -401.91) * mm});
            skLineSegment(sketch, "E1328", {"start": v(-692.91, -401.91) * mm, "end": v(-697.56, -403.04) * mm});
            skLineSegment(sketch, "E1329", {"start": v(-697.56, -403.04) * mm, "end": v(-701.27, -403.43) * mm});
            skLineSegment(sketch, "E1330", {"start": v(-701.27, -403.43) * mm, "end": v(-702.5, -403.43) * mm});
            skLineSegment(sketch, "E1331", {"start": v(-702.5, -403.43) * mm, "end": v(-703.8, -403.43) * mm});
            skLineSegment(sketch, "E1332", {"start": v(-703.8, -403.43) * mm, "end": v(-707.67, -403.05) * mm});
            skLineSegment(sketch, "E1333", {"start": v(-707.67, -403.05) * mm, "end": v(-712.5, -402.03) * mm});
            skLineSegment(sketch, "E1334", {"start": v(-712.5, -402.03) * mm, "end": v(-716.95, -400.52) * mm});
            skLineSegment(sketch, "E1335", {"start": v(-716.95, -400.52) * mm, "end": v(-720.96, -398.68) * mm});
            skLineSegment(sketch, "E1336", {"start": v(-720.96, -398.68) * mm, "end": v(-724.5, -396.66) * mm});
            skLineSegment(sketch, "E1337", {"start": v(-724.5, -396.66) * mm, "end": v(-727.52, -394.63) * mm});
            skLineSegment(sketch, "E1338", {"start": v(-727.52, -394.63) * mm, "end": v(-729.98, -392.74) * mm});
            skLineSegment(sketch, "E1339", {"start": v(-729.98, -392.74) * mm, "end": v(-731.38, -391.57) * mm});
            skLineSegment(sketch, "E1340", {"start": v(-731.38, -391.57) * mm, "end": v(-731.83, -391.16) * mm});
            skLineSegment(sketch, "E1341", {"start": v(-731.83, -391.16) * mm, "end": v(-731.98, -391.03) * mm});
            skLineSegment(sketch, "E1342", {"start": v(-731.98, -391.03) * mm, "end": v(-732.44, -390.63) * mm});
            skLineSegment(sketch, "E1343", {"start": v(-732.44, -390.63) * mm, "end": v(-734.1, -389.72) * mm});
            skLineSegment(sketch, "E1344", {"start": v(-734.1, -389.72) * mm, "end": v(-736.67, -389.21) * mm});
            skLineSegment(sketch, "E1345", {"start": v(-736.67, -389.21) * mm, "end": v(-739.47, -389.91) * mm});
            skLineSegment(sketch, "E1346", {"start": v(-739.47, -389.91) * mm, "end": v(-741.71, -391.5) * mm});
            skLineSegment(sketch, "E1347", {"start": v(-741.71, -391.5) * mm, "end": v(-742.3, -392.18) * mm});
            skLineSegment(sketch, "E1348", {"start": v(-742.3, -392.18) * mm, "end": v(-744.14, -394.6) * mm});
            skLineSegment(sketch, "E1349", {"start": v(-744.14, -394.6) * mm, "end": v(-744.27, -394.78) * mm});
            skLineSegment(sketch, "E1350", {"start": v(-744.27, -394.78) * mm, "end": v(-744.62, -395.33) * mm});
            skLineSegment(sketch, "E1351", {"start": v(-744.62, -395.33) * mm, "end": v(-745.1, -396.27) * mm});
            skLineSegment(sketch, "E1352", {"start": v(-745.1, -396.27) * mm, "end": v(-745.51, -397.4) * mm});
            skLineSegment(sketch, "E1353", {"start": v(-745.51, -397.4) * mm, "end": v(-745.73, -398.65) * mm});
            skLineSegment(sketch, "E1354", {"start": v(-745.73, -398.65) * mm, "end": v(-745.68, -400.02) * mm});
            skLineSegment(sketch, "E1355", {"start": v(-745.68, -400.02) * mm, "end": v(-745.26, -401.46) * mm});
            skLineSegment(sketch, "E1356", {"start": v(-745.26, -401.46) * mm, "end": v(-744.38, -402.94) * mm});
            skLineSegment(sketch, "E1357", {"start": v(-744.38, -402.94) * mm, "end": v(-743.33, -404.1) * mm});
            skLineSegment(sketch, "E1358", {"start": v(-743.33, -404.1) * mm, "end": v(-742.94, -404.44) * mm});
            skLineSegment(sketch, "E1359", {"start": v(-742.94, -404.44) * mm, "end": v(-742.53, -404.82) * mm});
            skLineSegment(sketch, "E1360", {"start": v(-742.53, -404.82) * mm, "end": v(-741.25, -405.9) * mm});
            skLineSegment(sketch, "E1361", {"start": v(-741.25, -405.9) * mm, "end": v(-738.49, -408.03) * mm});
            skLineSegment(sketch, "E1362", {"start": v(-738.49, -408.03) * mm, "end": v(-734.7, -410.57) * mm});
            skLineSegment(sketch, "E1363", {"start": v(-734.7, -410.57) * mm, "end": v(-729.97, -413.25) * mm});
            skLineSegment(sketch, "E1364", {"start": v(-729.97, -413.25) * mm, "end": v(-724.34, -415.8) * mm});
            skLineSegment(sketch, "E1365", {"start": v(-724.34, -415.8) * mm, "end": v(-717.87, -417.94) * mm});
            skLineSegment(sketch, "E1366", {"start": v(-717.87, -417.94) * mm, "end": v(-710.63, -419.42) * mm});
            skLineSegment(sketch, "E1367", {"start": v(-710.63, -419.42) * mm, "end": v(-704.66, -419.98) * mm});
            skLineSegment(sketch, "E1368", {"start": v(-704.66, -419.98) * mm, "end": v(-702.68, -419.98) * mm});
            skLineSegment(sketch, "E1369", {"start": v(-702.68, -419.98) * mm, "end": v(-701.58, -419.98) * mm});
            skLineSegment(sketch, "E1370", {"start": v(-701.58, -419.98) * mm, "end": v(-698.3, -419.8) * mm});
            skLineSegment(sketch, "E1371", {"start": v(-698.3, -419.8) * mm, "end": v(-694.05, -419.25) * mm});
            skLineSegment(sketch, "E1372", {"start": v(-694.05, -419.25) * mm, "end": v(-689.94, -418.36) * mm});
            skLineSegment(sketch, "E1373", {"start": v(-689.94, -418.36) * mm, "end": v(-686, -417.16) * mm});
            skLineSegment(sketch, "E1374", {"start": v(-686, -417.16) * mm, "end": v(-682.26, -415.65) * mm});
            skLineSegment(sketch, "E1375", {"start": v(-682.26, -415.65) * mm, "end": v(-678.73, -413.85) * mm});
            skLineSegment(sketch, "E1376", {"start": v(-678.73, -413.85) * mm, "end": v(-675.43, -411.78) * mm});
            skLineSegment(sketch, "E1377", {"start": v(-675.43, -411.78) * mm, "end": v(-672.38, -409.47) * mm});
            skLineSegment(sketch, "E1378", {"start": v(-672.38, -409.47) * mm, "end": v(-669.61, -406.92) * mm});
            skLineSegment(sketch, "E1379", {"start": v(-669.61, -406.92) * mm, "end": v(-667.14, -404.16) * mm});
            skLineSegment(sketch, "E1380", {"start": v(-667.14, -404.16) * mm, "end": v(-665, -401.2) * mm});
            skLineSegment(sketch, "E1381", {"start": v(-665, -401.2) * mm, "end": v(-663.18, -398.07) * mm});
            skLineSegment(sketch, "E1382", {"start": v(-663.18, -398.07) * mm, "end": v(-661.74, -394.78) * mm});
            skLineSegment(sketch, "E1383", {"start": v(-661.74, -394.78) * mm, "end": v(-660.68, -391.35) * mm});
            skLineSegment(sketch, "E1384", {"start": v(-660.68, -391.35) * mm, "end": v(-660.03, -387.8) * mm});
            skLineSegment(sketch, "E1385", {"start": v(-660.03, -387.8) * mm, "end": v(-659.81, -385.05) * mm});
            skLineSegment(sketch, "E1386", {"start": v(-659.81, -385.05) * mm, "end": v(-659.81, -384.14) * mm});
            skLineSegment(sketch, "E1387", {"start": v(-659.81, -384.14) * mm, "end": v(-659.81, -383.02) * mm});
            skLineSegment(sketch, "E1388", {"start": v(-659.81, -383.02) * mm, "end": v(-660.04, -379.67) * mm});
            skLineSegment(sketch, "E1389", {"start": v(-660.04, -379.67) * mm, "end": v(-660.72, -375.56) * mm});
            skLineSegment(sketch, "E1390", {"start": v(-660.72, -375.56) * mm, "end": v(-661.81, -371.77) * mm});
            skLineSegment(sketch, "E1391", {"start": v(-661.81, -371.77) * mm, "end": v(-663.3, -368.3) * mm});
            skLineSegment(sketch, "E1392", {"start": v(-663.3, -368.3) * mm, "end": v(-665.15, -365.1) * mm});
            skLineSegment(sketch, "E1393", {"start": v(-665.15, -365.1) * mm, "end": v(-667.34, -362.17) * mm});
            skLineSegment(sketch, "E1394", {"start": v(-667.34, -362.17) * mm, "end": v(-669.85, -359.49) * mm});
            skLineSegment(sketch, "E1395", {"start": v(-669.85, -359.49) * mm, "end": v(-672.65, -357.02) * mm});
            skLineSegment(sketch, "E1396", {"start": v(-672.65, -357.02) * mm, "end": v(-675.7, -354.76) * mm});
            skLineSegment(sketch, "E1397", {"start": v(-675.7, -354.76) * mm, "end": v(-679, -352.68) * mm});
            skLineSegment(sketch, "E1398", {"start": v(-679, -352.68) * mm, "end": v(-682.51, -350.75) * mm});
            skLineSegment(sketch, "E1399", {"start": v(-682.51, -350.75) * mm, "end": v(-686.2, -348.96) * mm});
            skLineSegment(sketch, "E1400", {"start": v(-686.2, -348.96) * mm, "end": v(-690.05, -347.28) * mm});
            skLineSegment(sketch, "E1401", {"start": v(-690.05, -347.28) * mm, "end": v(-694.04, -345.7) * mm});
            skLineSegment(sketch, "E1402", {"start": v(-694.04, -345.7) * mm, "end": v(-698.13, -344.19) * mm});
            skLineSegment(sketch, "E1403", {"start": v(-698.13, -344.19) * mm, "end": v(-701.26, -343.09) * mm});
            skLineSegment(sketch, "E1404", {"start": v(-701.26, -343.09) * mm, "end": v(-702.3, -342.73) * mm});
            skLineSegment(sketch, "E1405", {"start": v(-589.71, -357.25) * mm, "end": v(-589.71, -303.58) * mm});
            skLineSegment(sketch, "E1406", {"start": v(-589.71, -303.58) * mm, "end": v(-563.05, -303.58) * mm});
            skLineSegment(sketch, "E1407", {"start": v(-563.05, -303.58) * mm, "end": v(-561.67, -303.58) * mm});
            skLineSegment(sketch, "E1408", {"start": v(-561.67, -303.58) * mm, "end": v(-557.54, -304.11) * mm});
            skLineSegment(sketch, "E1409", {"start": v(-557.54, -304.11) * mm, "end": v(-552.4, -305.65) * mm});
            skLineSegment(sketch, "E1410", {"start": v(-552.4, -305.65) * mm, "end": v(-547.76, -308.07) * mm});
            skLineSegment(sketch, "E1411", {"start": v(-547.76, -308.07) * mm, "end": v(-543.7, -311.29) * mm});
            skLineSegment(sketch, "E1412", {"start": v(-543.7, -311.29) * mm, "end": v(-540.36, -315.18) * mm});
            skLineSegment(sketch, "E1413", {"start": v(-540.36, -315.18) * mm, "end": v(-537.83, -319.65) * mm});
            skLineSegment(sketch, "E1414", {"start": v(-537.83, -319.65) * mm, "end": v(-536.24, -324.59) * mm});
            skLineSegment(sketch, "E1415", {"start": v(-536.24, -324.59) * mm, "end": v(-535.68, -328.56) * mm});
            skLineSegment(sketch, "E1416", {"start": v(-535.68, -328.56) * mm, "end": v(-535.68, -329.88) * mm});
            skLineSegment(sketch, "E1417", {"start": v(-535.68, -329.88) * mm, "end": v(-535.68, -331.26) * mm});
            skLineSegment(sketch, "E1418", {"start": v(-535.68, -331.26) * mm, "end": v(-536.23, -335.39) * mm});
            skLineSegment(sketch, "E1419", {"start": v(-536.23, -335.39) * mm, "end": v(-537.82, -340.52) * mm});
            skLineSegment(sketch, "E1420", {"start": v(-537.82, -340.52) * mm, "end": v(-540.33, -345.17) * mm});
            skLineSegment(sketch, "E1421", {"start": v(-540.33, -345.17) * mm, "end": v(-543.65, -349.22) * mm});
            skLineSegment(sketch, "E1422", {"start": v(-543.65, -349.22) * mm, "end": v(-547.68, -352.57) * mm});
            skLineSegment(sketch, "E1423", {"start": v(-547.68, -352.57) * mm, "end": v(-552.3, -355.1) * mm});
            skLineSegment(sketch, "E1424", {"start": v(-552.3, -355.1) * mm, "end": v(-557.4, -356.7) * mm});
            skLineSegment(sketch, "E1425", {"start": v(-557.4, -356.7) * mm, "end": v(-561.5, -357.25) * mm});
            skLineSegment(sketch, "E1426", {"start": v(-561.5, -357.25) * mm, "end": v(-562.87, -357.25) * mm});
            skLineSegment(sketch, "E1427", {"start": v(-562.87, -357.25) * mm, "end": v(-589.71, -357.25) * mm});
            skLineSegment(sketch, "E1428", {"start": v(-562.52, -286.15) * mm, "end": v(-600.27, -286.15) * mm});
            skLineSegment(sketch, "E1429", {"start": v(-600.27, -286.15) * mm, "end": v(-600.94, -286.15) * mm});
            skLineSegment(sketch, "E1430", {"start": v(-600.94, -286.15) * mm, "end": v(-602.95, -286.69) * mm});
            skLineSegment(sketch, "E1431", {"start": v(-602.95, -286.69) * mm, "end": v(-605.13, -288.16) * mm});
            skLineSegment(sketch, "E1432", {"start": v(-605.13, -288.16) * mm, "end": v(-606.6, -290.34) * mm});
            skLineSegment(sketch, "E1433", {"start": v(-606.6, -290.34) * mm, "end": v(-607.14, -292.34) * mm});
            skLineSegment(sketch, "E1434", {"start": v(-607.14, -292.34) * mm, "end": v(-607.14, -293.01) * mm});
            skLineSegment(sketch, "E1435", {"start": v(-607.14, -293.01) * mm, "end": v(-607.14, -411.36) * mm});
            skLineSegment(sketch, "E1436", {"start": v(-607.14, -411.36) * mm, "end": v(-607.14, -412.02) * mm});
            skLineSegment(sketch, "E1437", {"start": v(-607.14, -412.02) * mm, "end": v(-606.6, -414.03) * mm});
            skLineSegment(sketch, "E1438", {"start": v(-606.6, -414.03) * mm, "end": v(-605.13, -416.21) * mm});
            skLineSegment(sketch, "E1439", {"start": v(-605.13, -416.21) * mm, "end": v(-602.95, -417.69) * mm});
            skLineSegment(sketch, "E1440", {"start": v(-602.95, -417.69) * mm, "end": v(-600.94, -418.23) * mm});
            skLineSegment(sketch, "E1441", {"start": v(-600.94, -418.23) * mm, "end": v(-600.27, -418.23) * mm});
            skLineSegment(sketch, "E1442", {"start": v(-600.27, -418.23) * mm, "end": v(-597.11, -418.23) * mm});
            skLineSegment(sketch, "E1443", {"start": v(-597.11, -418.23) * mm, "end": v(-596.38, -418.23) * mm});
            skLineSegment(sketch, "E1444", {"start": v(-596.38, -418.23) * mm, "end": v(-594.2, -417.7) * mm});
            skLineSegment(sketch, "E1445", {"start": v(-594.2, -417.7) * mm, "end": v(-591.86, -416.24) * mm});
            skLineSegment(sketch, "E1446", {"start": v(-591.86, -416.24) * mm, "end": v(-590.28, -414.05) * mm});
            skLineSegment(sketch, "E1447", {"start": v(-590.28, -414.05) * mm, "end": v(-589.71, -412.03) * mm});
            skLineSegment(sketch, "E1448", {"start": v(-589.71, -412.03) * mm, "end": v(-589.71, -411.36) * mm});
            skLineSegment(sketch, "E1449", {"start": v(-589.71, -411.36) * mm, "end": v(-589.71, -374.5) * mm});
            skLineSegment(sketch, "E1450", {"start": v(-589.71, -374.5) * mm, "end": v(-562.34, -374.5) * mm});
            skLineSegment(sketch, "E1451", {"start": v(-562.34, -374.5) * mm, "end": v(-561.22, -374.5) * mm});
            skLineSegment(sketch, "E1452", {"start": v(-561.22, -374.5) * mm, "end": v(-557.84, -374.27) * mm});
            skLineSegment(sketch, "E1453", {"start": v(-557.84, -374.27) * mm, "end": v(-553.47, -373.6) * mm});
            skLineSegment(sketch, "E1454", {"start": v(-553.47, -373.6) * mm, "end": v(-549.25, -372.5) * mm});
            skLineSegment(sketch, "E1455", {"start": v(-549.25, -372.5) * mm, "end": v(-545.2, -371) * mm});
            skLineSegment(sketch, "E1456", {"start": v(-545.2, -371) * mm, "end": v(-541.35, -369.13) * mm});
            skLineSegment(sketch, "E1457", {"start": v(-541.35, -369.13) * mm, "end": v(-537.71, -366.9) * mm});
            skLineSegment(sketch, "E1458", {"start": v(-537.71, -366.9) * mm, "end": v(-534.31, -364.34) * mm});
            skLineSegment(sketch, "E1459", {"start": v(-534.31, -364.34) * mm, "end": v(-531.18, -361.47) * mm});
            skLineSegment(sketch, "E1460", {"start": v(-531.18, -361.47) * mm, "end": v(-528.33, -358.31) * mm});
            skLineSegment(sketch, "E1461", {"start": v(-528.33, -358.31) * mm, "end": v(-525.8, -354.89) * mm});
            skLineSegment(sketch, "E1462", {"start": v(-525.8, -354.89) * mm, "end": v(-523.58, -351.23) * mm});
            skLineSegment(sketch, "E1463", {"start": v(-523.58, -351.23) * mm, "end": v(-521.72, -347.34) * mm});
            skLineSegment(sketch, "E1464", {"start": v(-521.72, -347.34) * mm, "end": v(-520.24, -343.26) * mm});
            skLineSegment(sketch, "E1465", {"start": v(-520.24, -343.26) * mm, "end": v(-519.15, -339) * mm});
            skLineSegment(sketch, "E1466", {"start": v(-519.15, -339) * mm, "end": v(-518.48, -334.6) * mm});
            skLineSegment(sketch, "E1467", {"start": v(-518.48, -334.6) * mm, "end": v(-518.25, -331.2) * mm});
            skLineSegment(sketch, "E1468", {"start": v(-518.25, -331.2) * mm, "end": v(-518.25, -330.06) * mm});
            skLineSegment(sketch, "E1469", {"start": v(-518.25, -330.06) * mm, "end": v(-518.25, -328.94) * mm});
            skLineSegment(sketch, "E1470", {"start": v(-518.25, -328.94) * mm, "end": v(-518.48, -325.57) * mm});
            skLineSegment(sketch, "E1471", {"start": v(-518.48, -325.57) * mm, "end": v(-519.15, -321.22) * mm});
            skLineSegment(sketch, "E1472", {"start": v(-519.15, -321.22) * mm, "end": v(-520.24, -317.01) * mm});
            skLineSegment(sketch, "E1473", {"start": v(-520.24, -317.01) * mm, "end": v(-521.74, -312.98) * mm});
            skLineSegment(sketch, "E1474", {"start": v(-521.74, -312.98) * mm, "end": v(-523.6, -309.14) * mm});
            skLineSegment(sketch, "E1475", {"start": v(-523.6, -309.14) * mm, "end": v(-525.82, -305.52) * mm});
            skLineSegment(sketch, "E1476", {"start": v(-525.82, -305.52) * mm, "end": v(-528.37, -302.14) * mm});
            skLineSegment(sketch, "E1477", {"start": v(-528.37, -302.14) * mm, "end": v(-531.23, -299.02) * mm});
            skLineSegment(sketch, "E1478", {"start": v(-531.23, -299.02) * mm, "end": v(-534.38, -296.18) * mm});
            skLineSegment(sketch, "E1479", {"start": v(-534.38, -296.18) * mm, "end": v(-537.79, -293.65) * mm});
            skLineSegment(sketch, "E1480", {"start": v(-537.79, -293.65) * mm, "end": v(-541.43, -291.45) * mm});
            skLineSegment(sketch, "E1481", {"start": v(-541.43, -291.45) * mm, "end": v(-545.3, -289.6) * mm});
            skLineSegment(sketch, "E1482", {"start": v(-545.3, -289.6) * mm, "end": v(-549.37, -288.12) * mm});
            skLineSegment(sketch, "E1483", {"start": v(-549.37, -288.12) * mm, "end": v(-553.6, -287.04) * mm});
            skLineSegment(sketch, "E1484", {"start": v(-553.6, -287.04) * mm, "end": v(-558, -286.37) * mm});
            skLineSegment(sketch, "E1485", {"start": v(-558, -286.37) * mm, "end": v(-561.4, -286.15) * mm});
            skLineSegment(sketch, "E1486", {"start": v(-561.4, -286.15) * mm, "end": v(-562.52, -286.15) * mm});
            skLineSegment(sketch, "E1487", {"start": v(-452.61, -368.31) * mm, "end": v(-428.9, -313.4) * mm});
            skLineSegment(sketch, "E1488", {"start": v(-428.9, -313.4) * mm, "end": v(-405.6, -368.31) * mm});
            skLineSegment(sketch, "E1489", {"start": v(-405.6, -368.31) * mm, "end": v(-452.61, -368.31) * mm});
            skLineSegment(sketch, "E1490", {"start": v(-422.2, -287.48) * mm, "end": v(-422.3, -287.26) * mm});
            skLineSegment(sketch, "E1491", {"start": v(-422.3, -287.26) * mm, "end": v(-422.46, -286.95) * mm});
            skLineSegment(sketch, "E1492", {"start": v(-422.46, -286.95) * mm, "end": v(-423.05, -286.08) * mm});
            skLineSegment(sketch, "E1493", {"start": v(-423.05, -286.08) * mm, "end": v(-424.3, -284.86) * mm});
            skLineSegment(sketch, "E1494", {"start": v(-424.3, -284.86) * mm, "end": v(-426.14, -283.9) * mm});
            skLineSegment(sketch, "E1495", {"start": v(-426.14, -283.9) * mm, "end": v(-428.05, -283.5) * mm});
            skLineSegment(sketch, "E1496", {"start": v(-428.05, -283.5) * mm, "end": v(-428.68, -283.5) * mm});
            skLineSegment(sketch, "E1497", {"start": v(-428.68, -283.5) * mm, "end": v(-429.22, -283.5) * mm});
            skLineSegment(sketch, "E1498", {"start": v(-429.22, -283.5) * mm, "end": v(-429.69, -283.5) * mm});
            skLineSegment(sketch, "E1499", {"start": v(-429.69, -283.5) * mm, "end": v(-431.1, -283.77) * mm});
            skLineSegment(sketch, "E1500", {"start": v(-431.1, -283.77) * mm, "end": v(-432.85, -284.53) * mm});
            skLineSegment(sketch, "E1501", {"start": v(-432.85, -284.53) * mm, "end": v(-434.33, -285.7) * mm});
            skLineSegment(sketch, "E1502", {"start": v(-434.33, -285.7) * mm, "end": v(-435.2, -286.82) * mm});
            skLineSegment(sketch, "E1503", {"start": v(-435.2, -286.82) * mm, "end": v(-435.41, -287.23) * mm});
            skLineSegment(sketch, "E1504", {"start": v(-435.41, -287.23) * mm, "end": v(-489.6, -409.67) * mm});
            skLineSegment(sketch, "E1505", {"start": v(-489.6, -409.67) * mm, "end": v(-489.7, -409.92) * mm});
            skLineSegment(sketch, "E1506", {"start": v(-489.7, -409.92) * mm, "end": v(-489.87, -410.4) * mm});
            skLineSegment(sketch, "E1507", {"start": v(-489.87, -410.4) * mm, "end": v(-490.17, -411.92) * mm});
            skLineSegment(sketch, "E1508", {"start": v(-490.17, -411.92) * mm, "end": v(-490.1, -413.57) * mm});
            skLineSegment(sketch, "E1509", {"start": v(-490.1, -413.57) * mm, "end": v(-489.7, -414.86) * mm});
            skLineSegment(sketch, "E1510", {"start": v(-489.7, -414.86) * mm, "end": v(-489.34, -415.55) * mm});
            skLineSegment(sketch, "E1511", {"start": v(-489.34, -415.55) * mm, "end": v(-489.19, -415.76) * mm});
            skLineSegment(sketch, "E1512", {"start": v(-489.19, -415.76) * mm, "end": v(-489, -416.05) * mm});
            skLineSegment(sketch, "E1513", {"start": v(-489, -416.05) * mm, "end": v(-488.24, -416.8) * mm});
            skLineSegment(sketch, "E1514", {"start": v(-488.24, -416.8) * mm, "end": v(-487.07, -417.58) * mm});
            skLineSegment(sketch, "E1515", {"start": v(-487.07, -417.58) * mm, "end": v(-485.69, -418.06) * mm});
            skLineSegment(sketch, "E1516", {"start": v(-485.69, -418.06) * mm, "end": v(-484.55, -418.23) * mm});
            skLineSegment(sketch, "E1517", {"start": v(-484.55, -418.23) * mm, "end": v(-484.17, -418.23) * mm});
            skLineSegment(sketch, "E1518", {"start": v(-484.17, -418.23) * mm, "end": v(-479.26, -418.23) * mm});
            skLineSegment(sketch, "E1519", {"start": v(-479.26, -418.23) * mm, "end": v(-478.75, -418.23) * mm});
            skLineSegment(sketch, "E1520", {"start": v(-478.75, -418.23) * mm, "end": v(-477.25, -417.94) * mm});
            skLineSegment(sketch, "E1521", {"start": v(-477.25, -417.94) * mm, "end": v(-475.42, -417.1) * mm});
            skLineSegment(sketch, "E1522", {"start": v(-475.42, -417.1) * mm, "end": v(-473.86, -415.8) * mm});
            skLineSegment(sketch, "E1523", {"start": v(-473.86, -415.8) * mm, "end": v(-472.92, -414.56) * mm});
            skLineSegment(sketch, "E1524", {"start": v(-472.92, -414.56) * mm, "end": v(-472.69, -414.1) * mm});
            skLineSegment(sketch, "E1525", {"start": v(-472.69, -414.1) * mm, "end": v(-459.74, -384.34) * mm});
            skLineSegment(sketch, "E1526", {"start": v(-459.74, -384.34) * mm, "end": v(-398.67, -384.34) * mm});
            skLineSegment(sketch, "E1527", {"start": v(-398.67, -384.34) * mm, "end": v(-385.65, -413.9) * mm});
            skLineSegment(sketch, "E1528", {"start": v(-385.65, -413.9) * mm, "end": v(-385.56, -414.1) * mm});
            skLineSegment(sketch, "E1529", {"start": v(-385.56, -414.1) * mm, "end": v(-385.33, -414.56) * mm});
            skLineSegment(sketch, "E1530", {"start": v(-385.33, -414.56) * mm, "end": v(-384.39, -415.8) * mm});
            skLineSegment(sketch, "E1531", {"start": v(-384.39, -415.8) * mm, "end": v(-382.83, -417.1) * mm});
            skLineSegment(sketch, "E1532", {"start": v(-382.83, -417.1) * mm, "end": v(-381, -417.94) * mm});
            skLineSegment(sketch, "E1533", {"start": v(-381, -417.94) * mm, "end": v(-379.5, -418.23) * mm});
            skLineSegment(sketch, "E1534", {"start": v(-379.5, -418.23) * mm, "end": v(-379, -418.23) * mm});
            skLineSegment(sketch, "E1535", {"start": v(-379, -418.23) * mm, "end": v(-374.43, -418.23) * mm});
            skLineSegment(sketch, "E1536", {"start": v(-374.43, -418.23) * mm, "end": v(-373.94, -418.23) * mm});
            skLineSegment(sketch, "E1537", {"start": v(-373.94, -418.23) * mm, "end": v(-372.49, -418) * mm});
            skLineSegment(sketch, "E1538", {"start": v(-372.49, -418) * mm, "end": v(-371, -417.43) * mm});
            skLineSegment(sketch, "E1539", {"start": v(-371, -417.43) * mm, "end": v(-369.9, -416.64) * mm});
            skLineSegment(sketch, "E1540", {"start": v(-369.9, -416.64) * mm, "end": v(-369.3, -416.02) * mm});
            skLineSegment(sketch, "E1541", {"start": v(-369.3, -416.02) * mm, "end": v(-369.14, -415.8) * mm});
            skLineSegment(sketch, "E1542", {"start": v(-369.14, -415.8) * mm, "end": v(-368.98, -415.57) * mm});
            skLineSegment(sketch, "E1543", {"start": v(-368.98, -415.57) * mm, "end": v(-368.58, -414.82) * mm});
            skLineSegment(sketch, "E1544", {"start": v(-368.58, -414.82) * mm, "end": v(-368.18, -413.55) * mm});
            skLineSegment(sketch, "E1545", {"start": v(-368.18, -413.55) * mm, "end": v(-368.1, -411.98) * mm});
            skLineSegment(sketch, "E1546", {"start": v(-368.1, -411.98) * mm, "end": v(-368.33, -410.55) * mm});
            skLineSegment(sketch, "E1547", {"start": v(-368.33, -410.55) * mm, "end": v(-368.49, -410.1) * mm});
            skLineSegment(sketch, "E1548", {"start": v(-368.49, -410.1) * mm, "end": v(-422.2, -287.48) * mm});
            skLineSegment(sketch, "E1549", {"start": v(-237.95, -344.6) * mm, "end": v(-263.4, -344.6) * mm});
            skLineSegment(sketch, "E1550", {"start": v(-263.4, -344.6) * mm, "end": v(-263.4, -318.82) * mm});
            skLineSegment(sketch, "E1551", {"start": v(-263.4, -318.82) * mm, "end": v(-263.4, -318.17) * mm});
            skLineSegment(sketch, "E1552", {"start": v(-263.4, -318.17) * mm, "end": v(-263.93, -316.21) * mm});
            skLineSegment(sketch, "E1553", {"start": v(-263.93, -316.21) * mm, "end": v(-265.4, -314.09) * mm});
            skLineSegment(sketch, "E1554", {"start": v(-265.4, -314.09) * mm, "end": v(-267.6, -312.65) * mm});
            skLineSegment(sketch, "E1555", {"start": v(-267.6, -312.65) * mm, "end": v(-269.6, -312.12) * mm});
            skLineSegment(sketch, "E1556", {"start": v(-269.6, -312.12) * mm, "end": v(-270.27, -312.12) * mm});
            skLineSegment(sketch, "E1557", {"start": v(-270.27, -312.12) * mm, "end": v(-273.07, -312.12) * mm});
            skLineSegment(sketch, "E1558", {"start": v(-273.07, -312.12) * mm, "end": v(-273.74, -312.12) * mm});
            skLineSegment(sketch, "E1559", {"start": v(-273.74, -312.12) * mm, "end": v(-275.75, -312.65) * mm});
            skLineSegment(sketch, "E1560", {"start": v(-275.75, -312.65) * mm, "end": v(-277.93, -314.09) * mm});
            skLineSegment(sketch, "E1561", {"start": v(-277.93, -314.09) * mm, "end": v(-279.4, -316.21) * mm});
            skLineSegment(sketch, "E1562", {"start": v(-279.4, -316.21) * mm, "end": v(-279.94, -318.17) * mm});
            skLineSegment(sketch, "E1563", {"start": v(-279.94, -318.17) * mm, "end": v(-279.94, -318.82) * mm});
            skLineSegment(sketch, "E1564", {"start": v(-279.94, -318.82) * mm, "end": v(-279.94, -344.6) * mm});
            skLineSegment(sketch, "E1565", {"start": v(-279.94, -344.6) * mm, "end": v(-305.55, -344.6) * mm});
            skLineSegment(sketch, "E1566", {"start": v(-305.55, -344.6) * mm, "end": v(-306.22, -344.6) * mm});
            skLineSegment(sketch, "E1567", {"start": v(-306.22, -344.6) * mm, "end": v(-308.22, -345.15) * mm});
            skLineSegment(sketch, "E1568", {"start": v(-308.22, -345.15) * mm, "end": v(-310.41, -346.62) * mm});
            skLineSegment(sketch, "E1569", {"start": v(-310.41, -346.62) * mm, "end": v(-311.89, -348.8) * mm});
            skLineSegment(sketch, "E1570", {"start": v(-311.89, -348.8) * mm, "end": v(-312.43, -350.81) * mm});
            skLineSegment(sketch, "E1571", {"start": v(-312.43, -350.81) * mm, "end": v(-312.43, -351.48) * mm});
            skLineSegment(sketch, "E1572", {"start": v(-312.43, -351.48) * mm, "end": v(-312.43, -354.12) * mm});
            skLineSegment(sketch, "E1573", {"start": v(-312.43, -354.12) * mm, "end": v(-312.43, -354.78) * mm});
            skLineSegment(sketch, "E1574", {"start": v(-312.43, -354.78) * mm, "end": v(-311.89, -356.79) * mm});
            skLineSegment(sketch, "E1575", {"start": v(-311.89, -356.79) * mm, "end": v(-310.41, -358.97) * mm});
            skLineSegment(sketch, "E1576", {"start": v(-310.41, -358.97) * mm, "end": v(-308.22, -360.45) * mm});
            skLineSegment(sketch, "E1577", {"start": v(-308.22, -360.45) * mm, "end": v(-306.22, -360.99) * mm});
            skLineSegment(sketch, "E1578", {"start": v(-306.22, -360.99) * mm, "end": v(-305.55, -360.99) * mm});
            skLineSegment(sketch, "E1579", {"start": v(-305.55, -360.99) * mm, "end": v(-279.94, -360.99) * mm});
            skLineSegment(sketch, "E1580", {"start": v(-279.94, -360.99) * mm, "end": v(-279.94, -386.43) * mm});
            skLineSegment(sketch, "E1581", {"start": v(-279.94, -386.43) * mm, "end": v(-279.94, -387.1) * mm});
            skLineSegment(sketch, "E1582", {"start": v(-279.94, -387.1) * mm, "end": v(-279.4, -389.1) * mm});
            skLineSegment(sketch, "E1583", {"start": v(-279.4, -389.1) * mm, "end": v(-277.93, -391.28) * mm});
            skLineSegment(sketch, "E1584", {"start": v(-277.93, -391.28) * mm, "end": v(-275.75, -392.76) * mm});
            skLineSegment(sketch, "E1585", {"start": v(-275.75, -392.76) * mm, "end": v(-273.74, -393.3) * mm});
            skLineSegment(sketch, "E1586", {"start": v(-273.74, -393.3) * mm, "end": v(-273.07, -393.3) * mm});
            skLineSegment(sketch, "E1587", {"start": v(-273.07, -393.3) * mm, "end": v(-270.27, -393.3) * mm});
            skLineSegment(sketch, "E1588", {"start": v(-270.27, -393.3) * mm, "end": v(-269.6, -393.3) * mm});
            skLineSegment(sketch, "E1589", {"start": v(-269.6, -393.3) * mm, "end": v(-267.6, -392.76) * mm});
            skLineSegment(sketch, "E1590", {"start": v(-267.6, -392.76) * mm, "end": v(-265.4, -391.28) * mm});
            skLineSegment(sketch, "E1591", {"start": v(-265.4, -391.28) * mm, "end": v(-263.93, -389.1) * mm});
            skLineSegment(sketch, "E1592", {"start": v(-263.93, -389.1) * mm, "end": v(-263.4, -387.1) * mm});
            skLineSegment(sketch, "E1593", {"start": v(-263.4, -387.1) * mm, "end": v(-263.4, -386.43) * mm});
            skLineSegment(sketch, "E1594", {"start": v(-263.4, -386.43) * mm, "end": v(-263.4, -360.99) * mm});
            skLineSegment(sketch, "E1595", {"start": v(-263.4, -360.99) * mm, "end": v(-237.95, -360.99) * mm});
            skLineSegment(sketch, "E1596", {"start": v(-237.95, -360.99) * mm, "end": v(-237.28, -360.99) * mm});
            skLineSegment(sketch, "E1597", {"start": v(-237.28, -360.99) * mm, "end": v(-235.28, -360.45) * mm});
            skLineSegment(sketch, "E1598", {"start": v(-235.28, -360.45) * mm, "end": v(-233.1, -358.97) * mm});
            skLineSegment(sketch, "E1599", {"start": v(-233.1, -358.97) * mm, "end": v(-231.62, -356.79) * mm});
            skLineSegment(sketch, "E1600", {"start": v(-231.62, -356.79) * mm, "end": v(-231.08, -354.78) * mm});
            skLineSegment(sketch, "E1601", {"start": v(-231.08, -354.78) * mm, "end": v(-231.08, -354.12) * mm});
            skLineSegment(sketch, "E1602", {"start": v(-231.08, -354.12) * mm, "end": v(-231.08, -351.48) * mm});
            skLineSegment(sketch, "E1603", {"start": v(-231.08, -351.48) * mm, "end": v(-231.08, -350.81) * mm});
            skLineSegment(sketch, "E1604", {"start": v(-231.08, -350.81) * mm, "end": v(-231.62, -348.8) * mm});
            skLineSegment(sketch, "E1605", {"start": v(-231.62, -348.8) * mm, "end": v(-233.1, -346.62) * mm});
            skLineSegment(sketch, "E1606", {"start": v(-233.1, -346.62) * mm, "end": v(-235.28, -345.15) * mm});
            skLineSegment(sketch, "E1607", {"start": v(-235.28, -345.15) * mm, "end": v(-237.28, -344.6) * mm});
            skLineSegment(sketch, "E1608", {"start": v(-237.28, -344.6) * mm, "end": v(-237.95, -344.6) * mm});
            skLineSegment(sketch, "E1609", {"start": v(-140.1, -303.4) * mm, "end": v(-107.8, -303.4) * mm});
            skLineSegment(sketch, "E1610", {"start": v(-107.8, -303.4) * mm, "end": v(-106.47, -303.4) * mm});
            skLineSegment(sketch, "E1611", {"start": v(-106.47, -303.4) * mm, "end": v(-102.44, -303.9) * mm});
            skLineSegment(sketch, "E1612", {"start": v(-102.44, -303.9) * mm, "end": v(-97.44, -305.36) * mm});
            skLineSegment(sketch, "E1613", {"start": v(-97.44, -305.36) * mm, "end": v(-92.91, -307.66) * mm});
            skLineSegment(sketch, "E1614", {"start": v(-92.91, -307.66) * mm, "end": v(-88.96, -310.7) * mm});
            skLineSegment(sketch, "E1615", {"start": v(-88.96, -310.7) * mm, "end": v(-85.7, -314.39) * mm});
            skLineSegment(sketch, "E1616", {"start": v(-85.7, -314.39) * mm, "end": v(-83.24, -318.62) * mm});
            skLineSegment(sketch, "E1617", {"start": v(-83.24, -318.62) * mm, "end": v(-81.68, -323.3) * mm});
            skLineSegment(sketch, "E1618", {"start": v(-81.68, -323.3) * mm, "end": v(-81.14, -327.05) * mm});
            skLineSegment(sketch, "E1619", {"start": v(-81.14, -327.05) * mm, "end": v(-81.14, -328.3) * mm});
            skLineSegment(sketch, "E1620", {"start": v(-81.14, -328.3) * mm, "end": v(-81.14, -329.63) * mm});
            skLineSegment(sketch, "E1621", {"start": v(-81.14, -329.63) * mm, "end": v(-81.67, -333.6) * mm});
            skLineSegment(sketch, "E1622", {"start": v(-81.67, -333.6) * mm, "end": v(-83.2, -338.5) * mm});
            skLineSegment(sketch, "E1623", {"start": v(-83.2, -338.5) * mm, "end": v(-85.6, -342.92) * mm});
            skLineSegment(sketch, "E1624", {"start": v(-85.6, -342.92) * mm, "end": v(-88.82, -346.74) * mm});
            skLineSegment(sketch, "E1625", {"start": v(-88.82, -346.74) * mm, "end": v(-92.72, -349.89) * mm});
            skLineSegment(sketch, "E1626", {"start": v(-92.72, -349.89) * mm, "end": v(-97.22, -352.26) * mm});
            skLineSegment(sketch, "E1627", {"start": v(-97.22, -352.26) * mm, "end": v(-102.23, -353.75) * mm});
            skLineSegment(sketch, "E1628", {"start": v(-102.23, -353.75) * mm, "end": v(-106.28, -354.27) * mm});
            skLineSegment(sketch, "E1629", {"start": v(-106.28, -354.27) * mm, "end": v(-107.63, -354.27) * mm});
            skLineSegment(sketch, "E1630", {"start": v(-107.63, -354.27) * mm, "end": v(-140.1, -354.27) * mm});
            skLineSegment(sketch, "E1631", {"start": v(-140.1, -354.27) * mm, "end": v(-140.1, -303.4) * mm});
            skLineSegment(sketch, "E1632", {"start": v(-63.53, -328.3) * mm, "end": v(-63.53, -327.22) * mm});
            skLineSegment(sketch, "E1633", {"start": v(-63.53, -327.22) * mm, "end": v(-63.76, -323.94) * mm});
            skLineSegment(sketch, "E1634", {"start": v(-63.76, -323.94) * mm, "end": v(-64.4, -319.7) * mm});
            skLineSegment(sketch, "E1635", {"start": v(-64.4, -319.7) * mm, "end": v(-65.47, -315.64) * mm});
            skLineSegment(sketch, "E1636", {"start": v(-65.47, -315.64) * mm, "end": v(-66.92, -311.74) * mm});
            skLineSegment(sketch, "E1637", {"start": v(-66.92, -311.74) * mm, "end": v(-68.74, -308.05) * mm});
            skLineSegment(sketch, "E1638", {"start": v(-68.74, -308.05) * mm, "end": v(-70.9, -304.58) * mm});
            skLineSegment(sketch, "E1639", {"start": v(-70.9, -304.58) * mm, "end": v(-73.4, -301.34) * mm});
            skLineSegment(sketch, "E1640", {"start": v(-73.4, -301.34) * mm, "end": v(-76.2, -298.36) * mm});
            skLineSegment(sketch, "E1641", {"start": v(-76.2, -298.36) * mm, "end": v(-79.3, -295.66) * mm});
            skLineSegment(sketch, "E1642", {"start": v(-79.3, -295.66) * mm, "end": v(-82.66, -293.25) * mm});
            skLineSegment(sketch, "E1643", {"start": v(-82.66, -293.25) * mm, "end": v(-86.26, -291.16) * mm});
            skLineSegment(sketch, "E1644", {"start": v(-86.26, -291.16) * mm, "end": v(-90.1, -289.4) * mm});
            skLineSegment(sketch, "E1645", {"start": v(-90.1, -289.4) * mm, "end": v(-94.13, -288.01) * mm});
            skLineSegment(sketch, "E1646", {"start": v(-94.13, -288.01) * mm, "end": v(-98.36, -286.99) * mm});
            skLineSegment(sketch, "E1647", {"start": v(-98.36, -286.99) * mm, "end": v(-102.75, -286.36) * mm});
            skLineSegment(sketch, "E1648", {"start": v(-102.75, -286.36) * mm, "end": v(-106.15, -286.15) * mm});
            skLineSegment(sketch, "E1649", {"start": v(-106.15, -286.15) * mm, "end": v(-107.28, -286.15) * mm});
            skLineSegment(sketch, "E1650", {"start": v(-107.28, -286.15) * mm, "end": v(-150.83, -286.15) * mm});
            skLineSegment(sketch, "E1651", {"start": v(-150.83, -286.15) * mm, "end": v(-151.5, -286.15) * mm});
            skLineSegment(sketch, "E1652", {"start": v(-151.5, -286.15) * mm, "end": v(-153.53, -286.68) * mm});
            skLineSegment(sketch, "E1653", {"start": v(-153.53, -286.68) * mm, "end": v(-155.7, -288.13) * mm});
            skLineSegment(sketch, "E1654", {"start": v(-155.7, -288.13) * mm, "end": v(-157.17, -290.31) * mm});
            skLineSegment(sketch, "E1655", {"start": v(-157.17, -290.31) * mm, "end": v(-157.7, -292.34) * mm});
            skLineSegment(sketch, "E1656", {"start": v(-157.7, -292.34) * mm, "end": v(-157.7, -293.01) * mm});
            skLineSegment(sketch, "E1657", {"start": v(-157.7, -293.01) * mm, "end": v(-157.7, -411.36) * mm});
            skLineSegment(sketch, "E1658", {"start": v(-157.7, -411.36) * mm, "end": v(-157.7, -412.02) * mm});
            skLineSegment(sketch, "E1659", {"start": v(-157.7, -412.02) * mm, "end": v(-157.16, -414.03) * mm});
            skLineSegment(sketch, "E1660", {"start": v(-157.16, -414.03) * mm, "end": v(-155.68, -416.21) * mm});
            skLineSegment(sketch, "E1661", {"start": v(-155.68, -416.21) * mm, "end": v(-153.5, -417.69) * mm});
            skLineSegment(sketch, "E1662", {"start": v(-153.5, -417.69) * mm, "end": v(-151.5, -418.23) * mm});
            skLineSegment(sketch, "E1663", {"start": v(-151.5, -418.23) * mm, "end": v(-150.83, -418.23) * mm});
            skLineSegment(sketch, "E1664", {"start": v(-150.83, -418.23) * mm, "end": v(-147.67, -418.23) * mm});
            skLineSegment(sketch, "E1665", {"start": v(-147.67, -418.23) * mm, "end": v(-146.94, -418.23) * mm});
            skLineSegment(sketch, "E1666", {"start": v(-146.94, -418.23) * mm, "end": v(-144.76, -417.7) * mm});
            skLineSegment(sketch, "E1667", {"start": v(-144.76, -417.7) * mm, "end": v(-142.41, -416.24) * mm});
            skLineSegment(sketch, "E1668", {"start": v(-142.41, -416.24) * mm, "end": v(-140.84, -414.05) * mm});
            skLineSegment(sketch, "E1669", {"start": v(-140.84, -414.05) * mm, "end": v(-140.27, -412.03) * mm});
            skLineSegment(sketch, "E1670", {"start": v(-140.27, -412.03) * mm, "end": v(-140.27, -411.36) * mm});
            skLineSegment(sketch, "E1671", {"start": v(-140.27, -411.36) * mm, "end": v(-140.27, -370.82) * mm});
            skLineSegment(sketch, "E1672", {"start": v(-140.27, -370.82) * mm, "end": v(-112.55, -370.82) * mm});
            skLineSegment(sketch, "E1673", {"start": v(-112.55, -370.82) * mm, "end": v(-111.58, -370.82) * mm});
            skLineSegment(sketch, "E1674", {"start": v(-111.58, -370.82) * mm, "end": v(-109, -370.8) * mm});
            skLineSegment(sketch, "E1675", {"start": v(-109, -370.8) * mm, "end": v(-108.68, -370.79) * mm});
            skLineSegment(sketch, "E1676", {"start": v(-108.68, -370.79) * mm, "end": v(-84.65, -414.2) * mm});
            skLineSegment(sketch, "E1677", {"start": v(-84.65, -414.2) * mm, "end": v(-84.41, -414.66) * mm});
            skLineSegment(sketch, "E1678", {"start": v(-84.41, -414.66) * mm, "end": v(-83.47, -415.93) * mm});
            skLineSegment(sketch, "E1679", {"start": v(-83.47, -415.93) * mm, "end": v(-81.97, -417.19) * mm});
            skLineSegment(sketch, "E1680", {"start": v(-81.97, -417.19) * mm, "end": v(-80.18, -417.96) * mm});
            skLineSegment(sketch, "E1681", {"start": v(-80.18, -417.96) * mm, "end": v(-78.65, -418.23) * mm});
            skLineSegment(sketch, "E1682", {"start": v(-78.65, -418.23) * mm, "end": v(-78.14, -418.23) * mm});
            skLineSegment(sketch, "E1683", {"start": v(-78.14, -418.23) * mm, "end": v(-72.7, -418.23) * mm});
            skLineSegment(sketch, "E1684", {"start": v(-72.7, -418.23) * mm, "end": v(-72.27, -418.23) * mm});
            skLineSegment(sketch, "E1685", {"start": v(-72.27, -418.23) * mm, "end": v(-71, -418.01) * mm});
            skLineSegment(sketch, "E1686", {"start": v(-71, -418.01) * mm, "end": v(-69.47, -417.4) * mm});
            skLineSegment(sketch, "E1687", {"start": v(-69.47, -417.4) * mm, "end": v(-68.19, -416.42) * mm});
            skLineSegment(sketch, "E1688", {"start": v(-68.19, -416.42) * mm, "end": v(-67.4, -415.46) * mm});
            skLineSegment(sketch, "E1689", {"start": v(-67.4, -415.46) * mm, "end": v(-67.2, -415.1) * mm});
            skLineSegment(sketch, "E1690", {"start": v(-67.2, -415.1) * mm, "end": v(-66.91, -414.58) * mm});
            skLineSegment(sketch, "E1691", {"start": v(-66.91, -414.58) * mm, "end": v(-66.41, -411.68) * mm});
            skLineSegment(sketch, "E1692", {"start": v(-66.41, -411.68) * mm, "end": v(-67.17, -408.7) * mm});
            skLineSegment(sketch, "E1693", {"start": v(-67.17, -408.7) * mm, "end": v(-67.5, -408.15) * mm});
            skLineSegment(sketch, "E1694", {"start": v(-67.5, -408.15) * mm, "end": v(-90.4, -367.52) * mm});
            skLineSegment(sketch, "E1695", {"start": v(-90.4, -367.52) * mm, "end": v(-88.91, -366.9) * mm});
            skLineSegment(sketch, "E1696", {"start": v(-88.91, -366.9) * mm, "end": v(-84.58, -364.58) * mm});
            skLineSegment(sketch, "E1697", {"start": v(-84.58, -364.58) * mm, "end": v(-79.34, -360.94) * mm});
            skLineSegment(sketch, "E1698", {"start": v(-79.34, -360.94) * mm, "end": v(-74.75, -356.66) * mm});
            skLineSegment(sketch, "E1699", {"start": v(-74.75, -356.66) * mm, "end": v(-70.87, -351.82) * mm});
            skLineSegment(sketch, "E1700", {"start": v(-70.87, -351.82) * mm, "end": v(-67.74, -346.5) * mm});
            skLineSegment(sketch, "E1701", {"start": v(-67.74, -346.5) * mm, "end": v(-65.44, -340.75) * mm});
            skLineSegment(sketch, "E1702", {"start": v(-65.44, -340.75) * mm, "end": v(-64.02, -334.66) * mm});
            skLineSegment(sketch, "E1703", {"start": v(-64.02, -334.66) * mm, "end": v(-63.53, -329.9) * mm});
            skLineSegment(sketch, "E1704", {"start": v(-63.53, -329.9) * mm, "end": v(-63.53, -328.3) * mm});
            skLineSegment(sketch, "E1705", {"start": v(68.87, -286.15) * mm, "end": v(-1.53, -286.15) * mm});
            skLineSegment(sketch, "E1706", {"start": v(-1.53, -286.15) * mm, "end": v(-2.2, -286.15) * mm});
            skLineSegment(sketch, "E1707", {"start": v(-2.2, -286.15) * mm, "end": v(-4.2, -286.69) * mm});
            skLineSegment(sketch, "E1708", {"start": v(-4.2, -286.69) * mm, "end": v(-6.4, -288.16) * mm});
            skLineSegment(sketch, "E1709", {"start": v(-6.4, -288.16) * mm, "end": v(-7.87, -290.34) * mm});
            skLineSegment(sketch, "E1710", {"start": v(-7.87, -290.34) * mm, "end": v(-8.4, -292.34) * mm});
            skLineSegment(sketch, "E1711", {"start": v(-8.4, -292.34) * mm, "end": v(-8.4, -293.01) * mm});
            skLineSegment(sketch, "E1712", {"start": v(-8.4, -293.01) * mm, "end": v(-8.4, -411.36) * mm});
            skLineSegment(sketch, "E1713", {"start": v(-8.4, -411.36) * mm, "end": v(-8.4, -412.02) * mm});
            skLineSegment(sketch, "E1714", {"start": v(-8.4, -412.02) * mm, "end": v(-7.87, -414.03) * mm});
            skLineSegment(sketch, "E1715", {"start": v(-7.87, -414.03) * mm, "end": v(-6.4, -416.21) * mm});
            skLineSegment(sketch, "E1716", {"start": v(-6.4, -416.21) * mm, "end": v(-4.2, -417.69) * mm});
            skLineSegment(sketch, "E1717", {"start": v(-4.2, -417.69) * mm, "end": v(-2.2, -418.23) * mm});
            skLineSegment(sketch, "E1718", {"start": v(-2.2, -418.23) * mm, "end": v(-1.53, -418.23) * mm});
            skLineSegment(sketch, "E1719", {"start": v(-1.53, -418.23) * mm, "end": v(68.87, -418.23) * mm});
            skLineSegment(sketch, "E1720", {"start": v(68.87, -418.23) * mm, "end": v(69.54, -418.23) * mm});
            skLineSegment(sketch, "E1721", {"start": v(69.54, -418.23) * mm, "end": v(71.54, -417.69) * mm});
            skLineSegment(sketch, "E1722", {"start": v(71.54, -417.69) * mm, "end": v(73.73, -416.21) * mm});
            skLineSegment(sketch, "E1723", {"start": v(73.73, -416.21) * mm, "end": v(75.2, -414.03) * mm});
            skLineSegment(sketch, "E1724", {"start": v(75.2, -414.03) * mm, "end": v(75.75, -412.02) * mm});
            skLineSegment(sketch, "E1725", {"start": v(75.75, -412.02) * mm, "end": v(75.75, -411.36) * mm});
            skLineSegment(sketch, "E1726", {"start": v(75.75, -411.36) * mm, "end": v(75.75, -408.54) * mm});
            skLineSegment(sketch, "E1727", {"start": v(75.75, -408.54) * mm, "end": v(75.75, -407.87) * mm});
            skLineSegment(sketch, "E1728", {"start": v(75.75, -407.87) * mm, "end": v(75.2, -405.87) * mm});
            skLineSegment(sketch, "E1729", {"start": v(75.2, -405.87) * mm, "end": v(73.73, -403.69) * mm});
            skLineSegment(sketch, "E1730", {"start": v(73.73, -403.69) * mm, "end": v(71.54, -402.22) * mm});
            skLineSegment(sketch, "E1731", {"start": v(71.54, -402.22) * mm, "end": v(69.54, -401.68) * mm});
            skLineSegment(sketch, "E1732", {"start": v(69.54, -401.68) * mm, "end": v(68.87, -401.68) * mm});
            skLineSegment(sketch, "E1733", {"start": v(68.87, -401.68) * mm, "end": v(9.2, -401.68) * mm});
            skLineSegment(sketch, "E1734", {"start": v(9.2, -401.68) * mm, "end": v(9.2, -358.88) * mm});
            skLineSegment(sketch, "E1735", {"start": v(9.2, -358.88) * mm, "end": v(60.27, -358.88) * mm});
            skLineSegment(sketch, "E1736", {"start": v(60.27, -358.88) * mm, "end": v(60.94, -358.88) * mm});
            skLineSegment(sketch, "E1737", {"start": v(60.94, -358.88) * mm, "end": v(62.94, -358.34) * mm});
            skLineSegment(sketch, "E1738", {"start": v(62.94, -358.34) * mm, "end": v(65.13, -356.86) * mm});
            skLineSegment(sketch, "E1739", {"start": v(65.13, -356.86) * mm, "end": v(66.6, -354.68) * mm});
            skLineSegment(sketch, "E1740", {"start": v(66.6, -354.68) * mm, "end": v(67.14, -352.68) * mm});
            skLineSegment(sketch, "E1741", {"start": v(67.14, -352.68) * mm, "end": v(67.14, -352) * mm});
            skLineSegment(sketch, "E1742", {"start": v(67.14, -352) * mm, "end": v(67.14, -349.02) * mm});
            skLineSegment(sketch, "E1743", {"start": v(67.14, -349.02) * mm, "end": v(67.14, -348.35) * mm});
            skLineSegment(sketch, "E1744", {"start": v(67.14, -348.35) * mm, "end": v(66.6, -346.35) * mm});
            skLineSegment(sketch, "E1745", {"start": v(66.6, -346.35) * mm, "end": v(65.13, -344.17) * mm});
            skLineSegment(sketch, "E1746", {"start": v(65.13, -344.17) * mm, "end": v(62.94, -342.7) * mm});
            skLineSegment(sketch, "E1747", {"start": v(62.94, -342.7) * mm, "end": v(60.94, -342.15) * mm});
            skLineSegment(sketch, "E1748", {"start": v(60.94, -342.15) * mm, "end": v(60.27, -342.15) * mm});
            skLineSegment(sketch, "E1749", {"start": v(60.27, -342.15) * mm, "end": v(9.2, -342.15) * mm});
            skLineSegment(sketch, "E1750", {"start": v(9.2, -342.15) * mm, "end": v(9.2, -302.87) * mm});
            skLineSegment(sketch, "E1751", {"start": v(9.2, -302.87) * mm, "end": v(68.87, -302.87) * mm});
            skLineSegment(sketch, "E1752", {"start": v(68.87, -302.87) * mm, "end": v(69.54, -302.87) * mm});
            skLineSegment(sketch, "E1753", {"start": v(69.54, -302.87) * mm, "end": v(71.54, -302.33) * mm});
            skLineSegment(sketch, "E1754", {"start": v(71.54, -302.33) * mm, "end": v(73.73, -300.85) * mm});
            skLineSegment(sketch, "E1755", {"start": v(73.73, -300.85) * mm, "end": v(75.2, -298.67) * mm});
            skLineSegment(sketch, "E1756", {"start": v(75.2, -298.67) * mm, "end": v(75.75, -296.67) * mm});
            skLineSegment(sketch, "E1757", {"start": v(75.75, -296.67) * mm, "end": v(75.75, -296) * mm});
            skLineSegment(sketch, "E1758", {"start": v(75.75, -296) * mm, "end": v(75.75, -293.01) * mm});
            skLineSegment(sketch, "E1759", {"start": v(75.75, -293.01) * mm, "end": v(75.75, -292.34) * mm});
            skLineSegment(sketch, "E1760", {"start": v(75.75, -292.34) * mm, "end": v(75.2, -290.34) * mm});
            skLineSegment(sketch, "E1761", {"start": v(75.2, -290.34) * mm, "end": v(73.73, -288.16) * mm});
            skLineSegment(sketch, "E1762", {"start": v(73.73, -288.16) * mm, "end": v(71.54, -286.69) * mm});
            skLineSegment(sketch, "E1763", {"start": v(71.54, -286.69) * mm, "end": v(69.54, -286.15) * mm});
            skLineSegment(sketch, "E1764", {"start": v(69.54, -286.15) * mm, "end": v(68.87, -286.15) * mm});
            skLineSegment(sketch, "E1765", {"start": v(196.91, -286.15) * mm, "end": v(121.4, -286.15) * mm});
            skLineSegment(sketch, "E1766", {"start": v(121.4, -286.15) * mm, "end": v(120.74, -286.15) * mm});
            skLineSegment(sketch, "E1767", {"start": v(120.74, -286.15) * mm, "end": v(118.71, -286.68) * mm});
            skLineSegment(sketch, "E1768", {"start": v(118.71, -286.68) * mm, "end": v(116.53, -288.13) * mm});
            skLineSegment(sketch, "E1769", {"start": v(116.53, -288.13) * mm, "end": v(115.07, -290.31) * mm});
            skLineSegment(sketch, "E1770", {"start": v(115.07, -290.31) * mm, "end": v(114.54, -292.34) * mm});
            skLineSegment(sketch, "E1771", {"start": v(114.54, -292.34) * mm, "end": v(114.54, -293.01) * mm});
            skLineSegment(sketch, "E1772", {"start": v(114.54, -293.01) * mm, "end": v(114.54, -295.65) * mm});
            skLineSegment(sketch, "E1773", {"start": v(114.54, -295.65) * mm, "end": v(114.54, -296.46) * mm});
            skLineSegment(sketch, "E1774", {"start": v(114.54, -296.46) * mm, "end": v(115.13, -298.88) * mm});
            skLineSegment(sketch, "E1775", {"start": v(115.13, -298.88) * mm, "end": v(116.7, -301.13) * mm});
            skLineSegment(sketch, "E1776", {"start": v(116.7, -301.13) * mm, "end": v(118.9, -302.45) * mm});
            skLineSegment(sketch, "E1777", {"start": v(118.9, -302.45) * mm, "end": v(120.78, -302.87) * mm});
            skLineSegment(sketch, "E1778", {"start": v(120.78, -302.87) * mm, "end": v(121.4, -302.87) * mm});
            skLineSegment(sketch, "E1779", {"start": v(121.4, -302.87) * mm, "end": v(150.37, -302.87) * mm});
            skLineSegment(sketch, "E1780", {"start": v(150.37, -302.87) * mm, "end": v(150.37, -411.36) * mm});
            skLineSegment(sketch, "E1781", {"start": v(150.37, -411.36) * mm, "end": v(150.37, -412.02) * mm});
            skLineSegment(sketch, "E1782", {"start": v(150.37, -412.02) * mm, "end": v(150.9, -414.03) * mm});
            skLineSegment(sketch, "E1783", {"start": v(150.9, -414.03) * mm, "end": v(152.38, -416.21) * mm});
            skLineSegment(sketch, "E1784", {"start": v(152.38, -416.21) * mm, "end": v(154.56, -417.69) * mm});
            skLineSegment(sketch, "E1785", {"start": v(154.56, -417.69) * mm, "end": v(156.56, -418.23) * mm});
            skLineSegment(sketch, "E1786", {"start": v(156.56, -418.23) * mm, "end": v(157.23, -418.23) * mm});
            skLineSegment(sketch, "E1787", {"start": v(157.23, -418.23) * mm, "end": v(160.4, -418.23) * mm});
            skLineSegment(sketch, "E1788", {"start": v(160.4, -418.23) * mm, "end": v(161.12, -418.23) * mm});
            skLineSegment(sketch, "E1789", {"start": v(161.12, -418.23) * mm, "end": v(163.3, -417.7) * mm});
            skLineSegment(sketch, "E1790", {"start": v(163.3, -417.7) * mm, "end": v(165.65, -416.24) * mm});
            skLineSegment(sketch, "E1791", {"start": v(165.65, -416.24) * mm, "end": v(167.22, -414.05) * mm});
            skLineSegment(sketch, "E1792", {"start": v(167.22, -414.05) * mm, "end": v(167.8, -412.03) * mm});
            skLineSegment(sketch, "E1793", {"start": v(167.8, -412.03) * mm, "end": v(167.8, -411.36) * mm});
            skLineSegment(sketch, "E1794", {"start": v(167.8, -411.36) * mm, "end": v(167.8, -302.87) * mm});
            skLineSegment(sketch, "E1795", {"start": v(167.8, -302.87) * mm, "end": v(196.91, -302.87) * mm});
            skLineSegment(sketch, "E1796", {"start": v(196.91, -302.87) * mm, "end": v(197.59, -302.87) * mm});
            skLineSegment(sketch, "E1797", {"start": v(197.59, -302.87) * mm, "end": v(199.61, -302.34) * mm});
            skLineSegment(sketch, "E1798", {"start": v(199.61, -302.34) * mm, "end": v(201.8, -300.88) * mm});
            skLineSegment(sketch, "E1799", {"start": v(201.8, -300.88) * mm, "end": v(203.27, -298.7) * mm});
            skLineSegment(sketch, "E1800", {"start": v(203.27, -298.7) * mm, "end": v(203.8, -296.67) * mm});
            skLineSegment(sketch, "E1801", {"start": v(203.8, -296.67) * mm, "end": v(203.8, -296) * mm});
            skLineSegment(sketch, "E1802", {"start": v(203.8, -296) * mm, "end": v(203.8, -293.01) * mm});
            skLineSegment(sketch, "E1803", {"start": v(203.8, -293.01) * mm, "end": v(203.8, -292.34) * mm});
            skLineSegment(sketch, "E1804", {"start": v(203.8, -292.34) * mm, "end": v(203.27, -290.31) * mm});
            skLineSegment(sketch, "E1805", {"start": v(203.27, -290.31) * mm, "end": v(201.8, -288.13) * mm});
            skLineSegment(sketch, "E1806", {"start": v(201.8, -288.13) * mm, "end": v(199.61, -286.68) * mm});
            skLineSegment(sketch, "E1807", {"start": v(199.61, -286.68) * mm, "end": v(197.59, -286.15) * mm});
            skLineSegment(sketch, "E1808", {"start": v(197.59, -286.15) * mm, "end": v(196.91, -286.15) * mm});
            skLineSegment(sketch, "E1809", {"start": v(267.38, -303.4) * mm, "end": v(299.66, -303.4) * mm});
            skLineSegment(sketch, "E1810", {"start": v(299.66, -303.4) * mm, "end": v(301, -303.4) * mm});
            skLineSegment(sketch, "E1811", {"start": v(301, -303.4) * mm, "end": v(305.02, -303.9) * mm});
            skLineSegment(sketch, "E1812", {"start": v(305.02, -303.9) * mm, "end": v(310.02, -305.36) * mm});
            skLineSegment(sketch, "E1813", {"start": v(310.02, -305.36) * mm, "end": v(314.54, -307.66) * mm});
            skLineSegment(sketch, "E1814", {"start": v(314.54, -307.66) * mm, "end": v(318.5, -310.7) * mm});
            skLineSegment(sketch, "E1815", {"start": v(318.5, -310.7) * mm, "end": v(321.76, -314.39) * mm});
            skLineSegment(sketch, "E1816", {"start": v(321.76, -314.39) * mm, "end": v(324.22, -318.62) * mm});
            skLineSegment(sketch, "E1817", {"start": v(324.22, -318.62) * mm, "end": v(325.77, -323.3) * mm});
            skLineSegment(sketch, "E1818", {"start": v(325.77, -323.3) * mm, "end": v(326.33, -327.05) * mm});
            skLineSegment(sketch, "E1819", {"start": v(326.33, -327.05) * mm, "end": v(326.33, -328.3) * mm});
            skLineSegment(sketch, "E1820", {"start": v(326.33, -328.3) * mm, "end": v(326.33, -329.63) * mm});
            skLineSegment(sketch, "E1821", {"start": v(326.33, -329.63) * mm, "end": v(325.8, -333.6) * mm});
            skLineSegment(sketch, "E1822", {"start": v(325.8, -333.6) * mm, "end": v(324.27, -338.5) * mm});
            skLineSegment(sketch, "E1823", {"start": v(324.27, -338.5) * mm, "end": v(321.86, -342.92) * mm});
            skLineSegment(sketch, "E1824", {"start": v(321.86, -342.92) * mm, "end": v(318.66, -346.74) * mm});
            skLineSegment(sketch, "E1825", {"start": v(318.66, -346.74) * mm, "end": v(314.75, -349.89) * mm});
            skLineSegment(sketch, "E1826", {"start": v(314.75, -349.89) * mm, "end": v(310.25, -352.26) * mm});
            skLineSegment(sketch, "E1827", {"start": v(310.25, -352.26) * mm, "end": v(305.25, -353.75) * mm});
            skLineSegment(sketch, "E1828", {"start": v(305.25, -353.75) * mm, "end": v(301.18, -354.27) * mm});
            skLineSegment(sketch, "E1829", {"start": v(301.18, -354.27) * mm, "end": v(299.84, -354.27) * mm});
            skLineSegment(sketch, "E1830", {"start": v(299.84, -354.27) * mm, "end": v(267.38, -354.27) * mm});
            skLineSegment(sketch, "E1831", {"start": v(267.38, -354.27) * mm, "end": v(267.38, -303.4) * mm});
            skLineSegment(sketch, "E1832", {"start": v(343.93, -328.3) * mm, "end": v(343.93, -327.22) * mm});
            skLineSegment(sketch, "E1833", {"start": v(343.93, -327.22) * mm, "end": v(343.73, -323.94) * mm});
            skLineSegment(sketch, "E1834", {"start": v(343.73, -323.94) * mm, "end": v(343.07, -319.7) * mm});
            skLineSegment(sketch, "E1835", {"start": v(343.07, -319.7) * mm, "end": v(342, -315.64) * mm});
            skLineSegment(sketch, "E1836", {"start": v(342, -315.64) * mm, "end": v(340.55, -311.74) * mm});
            skLineSegment(sketch, "E1837", {"start": v(340.55, -311.74) * mm, "end": v(338.72, -308.05) * mm});
            skLineSegment(sketch, "E1838", {"start": v(338.72, -308.05) * mm, "end": v(336.56, -304.58) * mm});
            skLineSegment(sketch, "E1839", {"start": v(336.56, -304.58) * mm, "end": v(334.08, -301.34) * mm});
            skLineSegment(sketch, "E1840", {"start": v(334.08, -301.34) * mm, "end": v(331.26, -298.36) * mm});
            skLineSegment(sketch, "E1841", {"start": v(331.26, -298.36) * mm, "end": v(328.16, -295.66) * mm});
            skLineSegment(sketch, "E1842", {"start": v(328.16, -295.66) * mm, "end": v(324.8, -293.25) * mm});
            skLineSegment(sketch, "E1843", {"start": v(324.8, -293.25) * mm, "end": v(321.2, -291.16) * mm});
            skLineSegment(sketch, "E1844", {"start": v(321.2, -291.16) * mm, "end": v(317.36, -289.4) * mm});
            skLineSegment(sketch, "E1845", {"start": v(317.36, -289.4) * mm, "end": v(313.32, -288.01) * mm});
            skLineSegment(sketch, "E1846", {"start": v(313.32, -288.01) * mm, "end": v(309.1, -286.99) * mm});
            skLineSegment(sketch, "E1847", {"start": v(309.1, -286.99) * mm, "end": v(304.71, -286.36) * mm});
            skLineSegment(sketch, "E1848", {"start": v(304.71, -286.36) * mm, "end": v(301.3, -286.15) * mm});
            skLineSegment(sketch, "E1849", {"start": v(301.3, -286.15) * mm, "end": v(300.2, -286.15) * mm});
            skLineSegment(sketch, "E1850", {"start": v(300.2, -286.15) * mm, "end": v(256.63, -286.15) * mm});
            skLineSegment(sketch, "E1851", {"start": v(256.63, -286.15) * mm, "end": v(255.97, -286.15) * mm});
            skLineSegment(sketch, "E1852", {"start": v(255.97, -286.15) * mm, "end": v(253.94, -286.68) * mm});
            skLineSegment(sketch, "E1853", {"start": v(253.94, -286.68) * mm, "end": v(251.75, -288.13) * mm});
            skLineSegment(sketch, "E1854", {"start": v(251.75, -288.13) * mm, "end": v(250.3, -290.31) * mm});
            skLineSegment(sketch, "E1855", {"start": v(250.3, -290.31) * mm, "end": v(249.77, -292.34) * mm});
            skLineSegment(sketch, "E1856", {"start": v(249.77, -292.34) * mm, "end": v(249.77, -293.01) * mm});
            skLineSegment(sketch, "E1857", {"start": v(249.77, -293.01) * mm, "end": v(249.77, -411.36) * mm});
            skLineSegment(sketch, "E1858", {"start": v(249.77, -411.36) * mm, "end": v(249.77, -412.02) * mm});
            skLineSegment(sketch, "E1859", {"start": v(249.77, -412.02) * mm, "end": v(250.3, -414.03) * mm});
            skLineSegment(sketch, "E1860", {"start": v(250.3, -414.03) * mm, "end": v(251.78, -416.21) * mm});
            skLineSegment(sketch, "E1861", {"start": v(251.78, -416.21) * mm, "end": v(253.96, -417.69) * mm});
            skLineSegment(sketch, "E1862", {"start": v(253.96, -417.69) * mm, "end": v(255.97, -418.23) * mm});
            skLineSegment(sketch, "E1863", {"start": v(255.97, -418.23) * mm, "end": v(256.63, -418.23) * mm});
            skLineSegment(sketch, "E1864", {"start": v(256.63, -418.23) * mm, "end": v(259.8, -418.23) * mm});
            skLineSegment(sketch, "E1865", {"start": v(259.8, -418.23) * mm, "end": v(260.54, -418.23) * mm});
            skLineSegment(sketch, "E1866", {"start": v(260.54, -418.23) * mm, "end": v(262.7, -417.7) * mm});
            skLineSegment(sketch, "E1867", {"start": v(262.7, -417.7) * mm, "end": v(265.06, -416.24) * mm});
            skLineSegment(sketch, "E1868", {"start": v(265.06, -416.24) * mm, "end": v(266.64, -414.05) * mm});
            skLineSegment(sketch, "E1869", {"start": v(266.64, -414.05) * mm, "end": v(267.2, -412.03) * mm});
            skLineSegment(sketch, "E1870", {"start": v(267.2, -412.03) * mm, "end": v(267.2, -411.36) * mm});
            skLineSegment(sketch, "E1871", {"start": v(267.2, -411.36) * mm, "end": v(267.2, -370.82) * mm});
            skLineSegment(sketch, "E1872", {"start": v(267.2, -370.82) * mm, "end": v(294.9, -370.82) * mm});
            skLineSegment(sketch, "E1873", {"start": v(294.9, -370.82) * mm, "end": v(295.9, -370.82) * mm});
            skLineSegment(sketch, "E1874", {"start": v(295.9, -370.82) * mm, "end": v(298.46, -370.8) * mm});
            skLineSegment(sketch, "E1875", {"start": v(298.46, -370.8) * mm, "end": v(298.8, -370.79) * mm});
            skLineSegment(sketch, "E1876", {"start": v(298.8, -370.79) * mm, "end": v(322.82, -414.2) * mm});
            skLineSegment(sketch, "E1877", {"start": v(322.82, -414.2) * mm, "end": v(323.05, -414.66) * mm});
            skLineSegment(sketch, "E1878", {"start": v(323.05, -414.66) * mm, "end": v(324, -415.93) * mm});
            skLineSegment(sketch, "E1879", {"start": v(324, -415.93) * mm, "end": v(325.5, -417.19) * mm});
            skLineSegment(sketch, "E1880", {"start": v(325.5, -417.19) * mm, "end": v(327.3, -417.96) * mm});
            skLineSegment(sketch, "E1881", {"start": v(327.3, -417.96) * mm, "end": v(328.82, -418.23) * mm});
            skLineSegment(sketch, "E1882", {"start": v(328.82, -418.23) * mm, "end": v(329.33, -418.23) * mm});
            skLineSegment(sketch, "E1883", {"start": v(329.33, -418.23) * mm, "end": v(334.79, -418.23) * mm});
            skLineSegment(sketch, "E1884", {"start": v(334.79, -418.23) * mm, "end": v(335.2, -418.23) * mm});
            skLineSegment(sketch, "E1885", {"start": v(335.2, -418.23) * mm, "end": v(336.46, -418.01) * mm});
            skLineSegment(sketch, "E1886", {"start": v(336.46, -418.01) * mm, "end": v(337.99, -417.4) * mm});
            skLineSegment(sketch, "E1887", {"start": v(337.99, -417.4) * mm, "end": v(339.28, -416.41) * mm});
            skLineSegment(sketch, "E1888", {"start": v(339.28, -416.41) * mm, "end": v(340.07, -415.46) * mm});
            skLineSegment(sketch, "E1889", {"start": v(340.07, -415.46) * mm, "end": v(340.27, -415.1) * mm});
            skLineSegment(sketch, "E1890", {"start": v(340.27, -415.1) * mm, "end": v(340.55, -414.58) * mm});
            skLineSegment(sketch, "E1891", {"start": v(340.55, -414.58) * mm, "end": v(341.06, -411.68) * mm});
            skLineSegment(sketch, "E1892", {"start": v(341.06, -411.68) * mm, "end": v(340.3, -408.7) * mm});
            skLineSegment(sketch, "E1893", {"start": v(340.3, -408.7) * mm, "end": v(339.97, -408.15) * mm});
            skLineSegment(sketch, "E1894", {"start": v(339.97, -408.15) * mm, "end": v(317.06, -367.52) * mm});
            skLineSegment(sketch, "E1895", {"start": v(317.06, -367.52) * mm, "end": v(318.56, -366.9) * mm});
            skLineSegment(sketch, "E1896", {"start": v(318.56, -366.9) * mm, "end": v(322.9, -364.58) * mm});
            skLineSegment(sketch, "E1897", {"start": v(322.9, -364.58) * mm, "end": v(328.13, -360.94) * mm});
            skLineSegment(sketch, "E1898", {"start": v(328.13, -360.94) * mm, "end": v(332.73, -356.66) * mm});
            skLineSegment(sketch, "E1899", {"start": v(332.73, -356.66) * mm, "end": v(336.62, -351.82) * mm});
            skLineSegment(sketch, "E1900", {"start": v(336.62, -351.82) * mm, "end": v(339.71, -346.5) * mm});
            skLineSegment(sketch, "E1901", {"start": v(339.71, -346.5) * mm, "end": v(342.03, -340.75) * mm});
            skLineSegment(sketch, "E1902", {"start": v(342.03, -340.75) * mm, "end": v(343.45, -334.66) * mm});
            skLineSegment(sketch, "E1903", {"start": v(343.45, -334.66) * mm, "end": v(343.93, -329.9) * mm});
            skLineSegment(sketch, "E1904", {"start": v(343.93, -329.9) * mm, "end": v(343.93, -328.3) * mm});
            skLineSegment(sketch, "E1905", {"start": v(476.34, -286.15) * mm, "end": v(405.93, -286.15) * mm});
            skLineSegment(sketch, "E1906", {"start": v(405.93, -286.15) * mm, "end": v(405.27, -286.15) * mm});
            skLineSegment(sketch, "E1907", {"start": v(405.27, -286.15) * mm, "end": v(403.27, -286.69) * mm});
            skLineSegment(sketch, "E1908", {"start": v(403.27, -286.69) * mm, "end": v(401.08, -288.16) * mm});
            skLineSegment(sketch, "E1909", {"start": v(401.08, -288.16) * mm, "end": v(399.6, -290.34) * mm});
            skLineSegment(sketch, "E1910", {"start": v(399.6, -290.34) * mm, "end": v(399.07, -292.34) * mm});
            skLineSegment(sketch, "E1911", {"start": v(399.07, -292.34) * mm, "end": v(399.07, -293.01) * mm});
            skLineSegment(sketch, "E1912", {"start": v(399.07, -293.01) * mm, "end": v(399.07, -411.36) * mm});
            skLineSegment(sketch, "E1913", {"start": v(399.07, -411.36) * mm, "end": v(399.07, -412.02) * mm});
            skLineSegment(sketch, "E1914", {"start": v(399.07, -412.02) * mm, "end": v(399.6, -414.03) * mm});
            skLineSegment(sketch, "E1915", {"start": v(399.6, -414.03) * mm, "end": v(401.08, -416.21) * mm});
            skLineSegment(sketch, "E1916", {"start": v(401.08, -416.21) * mm, "end": v(403.27, -417.69) * mm});
            skLineSegment(sketch, "E1917", {"start": v(403.27, -417.69) * mm, "end": v(405.27, -418.23) * mm});
            skLineSegment(sketch, "E1918", {"start": v(405.27, -418.23) * mm, "end": v(405.93, -418.23) * mm});
            skLineSegment(sketch, "E1919", {"start": v(405.93, -418.23) * mm, "end": v(476.34, -418.23) * mm});
            skLineSegment(sketch, "E1920", {"start": v(476.34, -418.23) * mm, "end": v(477, -418.23) * mm});
            skLineSegment(sketch, "E1921", {"start": v(477, -418.23) * mm, "end": v(479, -417.69) * mm});
            skLineSegment(sketch, "E1922", {"start": v(479, -417.69) * mm, "end": v(481.2, -416.21) * mm});
            skLineSegment(sketch, "E1923", {"start": v(481.2, -416.21) * mm, "end": v(482.67, -414.03) * mm});
            skLineSegment(sketch, "E1924", {"start": v(482.67, -414.03) * mm, "end": v(483.22, -412.02) * mm});
            skLineSegment(sketch, "E1925", {"start": v(483.22, -412.02) * mm, "end": v(483.22, -411.36) * mm});
            skLineSegment(sketch, "E1926", {"start": v(483.22, -411.36) * mm, "end": v(483.22, -408.54) * mm});
            skLineSegment(sketch, "E1927", {"start": v(483.22, -408.54) * mm, "end": v(483.22, -407.87) * mm});
            skLineSegment(sketch, "E1928", {"start": v(483.22, -407.87) * mm, "end": v(482.67, -405.87) * mm});
            skLineSegment(sketch, "E1929", {"start": v(482.67, -405.87) * mm, "end": v(481.2, -403.69) * mm});
            skLineSegment(sketch, "E1930", {"start": v(481.2, -403.69) * mm, "end": v(479, -402.22) * mm});
            skLineSegment(sketch, "E1931", {"start": v(479, -402.22) * mm, "end": v(477, -401.68) * mm});
            skLineSegment(sketch, "E1932", {"start": v(477, -401.68) * mm, "end": v(476.34, -401.68) * mm});
            skLineSegment(sketch, "E1933", {"start": v(476.34, -401.68) * mm, "end": v(416.68, -401.68) * mm});
            skLineSegment(sketch, "E1934", {"start": v(416.68, -401.68) * mm, "end": v(416.68, -358.88) * mm});
            skLineSegment(sketch, "E1935", {"start": v(416.68, -358.88) * mm, "end": v(467.73, -358.88) * mm});
            skLineSegment(sketch, "E1936", {"start": v(467.73, -358.88) * mm, "end": v(468.42, -358.88) * mm});
            skLineSegment(sketch, "E1937", {"start": v(468.42, -358.88) * mm, "end": v(470.42, -358.34) * mm});
            skLineSegment(sketch, "E1938", {"start": v(470.42, -358.34) * mm, "end": v(472.6, -356.86) * mm});
            skLineSegment(sketch, "E1939", {"start": v(472.6, -356.86) * mm, "end": v(474.08, -354.68) * mm});
            skLineSegment(sketch, "E1940", {"start": v(474.08, -354.68) * mm, "end": v(474.61, -352.68) * mm});
            skLineSegment(sketch, "E1941", {"start": v(474.61, -352.68) * mm, "end": v(474.61, -352) * mm});
            skLineSegment(sketch, "E1942", {"start": v(474.61, -352) * mm, "end": v(474.61, -349.02) * mm});
            skLineSegment(sketch, "E1943", {"start": v(474.61, -349.02) * mm, "end": v(474.61, -348.35) * mm});
            skLineSegment(sketch, "E1944", {"start": v(474.61, -348.35) * mm, "end": v(474.08, -346.35) * mm});
            skLineSegment(sketch, "E1945", {"start": v(474.08, -346.35) * mm, "end": v(472.6, -344.17) * mm});
            skLineSegment(sketch, "E1946", {"start": v(472.6, -344.17) * mm, "end": v(470.42, -342.7) * mm});
            skLineSegment(sketch, "E1947", {"start": v(470.42, -342.7) * mm, "end": v(468.42, -342.15) * mm});
            skLineSegment(sketch, "E1948", {"start": v(468.42, -342.15) * mm, "end": v(467.73, -342.15) * mm});
            skLineSegment(sketch, "E1949", {"start": v(467.73, -342.15) * mm, "end": v(416.68, -342.15) * mm});
            skLineSegment(sketch, "E1950", {"start": v(416.68, -342.15) * mm, "end": v(416.68, -302.87) * mm});
            skLineSegment(sketch, "E1951", {"start": v(416.68, -302.87) * mm, "end": v(476.34, -302.87) * mm});
            skLineSegment(sketch, "E1952", {"start": v(476.34, -302.87) * mm, "end": v(477, -302.87) * mm});
            skLineSegment(sketch, "E1953", {"start": v(477, -302.87) * mm, "end": v(479, -302.33) * mm});
            skLineSegment(sketch, "E1954", {"start": v(479, -302.33) * mm, "end": v(481.2, -300.85) * mm});
            skLineSegment(sketch, "E1955", {"start": v(481.2, -300.85) * mm, "end": v(482.67, -298.67) * mm});
            skLineSegment(sketch, "E1956", {"start": v(482.67, -298.67) * mm, "end": v(483.22, -296.67) * mm});
            skLineSegment(sketch, "E1957", {"start": v(483.22, -296.67) * mm, "end": v(483.22, -296) * mm});
            skLineSegment(sketch, "E1958", {"start": v(483.22, -296) * mm, "end": v(483.22, -293.01) * mm});
            skLineSegment(sketch, "E1959", {"start": v(483.22, -293.01) * mm, "end": v(483.22, -292.34) * mm});
            skLineSegment(sketch, "E1960", {"start": v(483.22, -292.34) * mm, "end": v(482.67, -290.34) * mm});
            skLineSegment(sketch, "E1961", {"start": v(482.67, -290.34) * mm, "end": v(481.2, -288.16) * mm});
            skLineSegment(sketch, "E1962", {"start": v(481.2, -288.16) * mm, "end": v(479, -286.69) * mm});
            skLineSegment(sketch, "E1963", {"start": v(479, -286.69) * mm, "end": v(477, -286.15) * mm});
            skLineSegment(sketch, "E1964", {"start": v(477, -286.15) * mm, "end": v(476.34, -286.15) * mm});
            skLineSegment(sketch, "E1965", {"start": v(559.04, -368.31) * mm, "end": v(582.74, -313.4) * mm});
            skLineSegment(sketch, "E1966", {"start": v(582.74, -313.4) * mm, "end": v(606.06, -368.31) * mm});
            skLineSegment(sketch, "E1967", {"start": v(606.06, -368.31) * mm, "end": v(559.04, -368.31) * mm});
            skLineSegment(sketch, "E1968", {"start": v(589.45, -287.48) * mm, "end": v(589.35, -287.26) * mm});
            skLineSegment(sketch, "E1969", {"start": v(589.35, -287.26) * mm, "end": v(589.2, -286.95) * mm});
            skLineSegment(sketch, "E1970", {"start": v(589.2, -286.95) * mm, "end": v(588.6, -286.08) * mm});
            skLineSegment(sketch, "E1971", {"start": v(588.6, -286.08) * mm, "end": v(587.36, -284.86) * mm});
            skLineSegment(sketch, "E1972", {"start": v(587.36, -284.86) * mm, "end": v(585.51, -283.9) * mm});
            skLineSegment(sketch, "E1973", {"start": v(585.51, -283.9) * mm, "end": v(583.6, -283.5) * mm});
            skLineSegment(sketch, "E1974", {"start": v(583.6, -283.5) * mm, "end": v(582.97, -283.5) * mm});
            skLineSegment(sketch, "E1975", {"start": v(582.97, -283.5) * mm, "end": v(582.44, -283.5) * mm});
            skLineSegment(sketch, "E1976", {"start": v(582.44, -283.5) * mm, "end": v(581.95, -283.5) * mm});
            skLineSegment(sketch, "E1977", {"start": v(581.95, -283.5) * mm, "end": v(580.53, -283.78) * mm});
            skLineSegment(sketch, "E1978", {"start": v(580.53, -283.78) * mm, "end": v(578.78, -284.55) * mm});
            skLineSegment(sketch, "E1979", {"start": v(578.78, -284.55) * mm, "end": v(577.3, -285.74) * mm});
            skLineSegment(sketch, "E1980", {"start": v(577.3, -285.74) * mm, "end": v(576.42, -286.87) * mm});
            skLineSegment(sketch, "E1981", {"start": v(576.42, -286.87) * mm, "end": v(576.21, -287.29) * mm});
            skLineSegment(sketch, "E1982", {"start": v(576.21, -287.29) * mm, "end": v(522.06, -409.67) * mm});
            skLineSegment(sketch, "E1983", {"start": v(522.06, -409.67) * mm, "end": v(521.96, -409.9) * mm});
            skLineSegment(sketch, "E1984", {"start": v(521.96, -409.9) * mm, "end": v(521.78, -410.38) * mm});
            skLineSegment(sketch, "E1985", {"start": v(521.78, -410.38) * mm, "end": v(521.48, -411.9) * mm});
            skLineSegment(sketch, "E1986", {"start": v(521.48, -411.9) * mm, "end": v(521.55, -413.56) * mm});
            skLineSegment(sketch, "E1987", {"start": v(521.55, -413.56) * mm, "end": v(521.93, -414.85) * mm});
            skLineSegment(sketch, "E1988", {"start": v(521.93, -414.85) * mm, "end": v(522.32, -415.54) * mm});
            skLineSegment(sketch, "E1989", {"start": v(522.32, -415.54) * mm, "end": v(522.44, -415.75) * mm});
            skLineSegment(sketch, "E1990", {"start": v(522.44, -415.75) * mm, "end": v(522.65, -416.04) * mm});
            skLineSegment(sketch, "E1991", {"start": v(522.65, -416.04) * mm, "end": v(523.4, -416.8) * mm});
            skLineSegment(sketch, "E1992", {"start": v(523.4, -416.8) * mm, "end": v(524.58, -417.58) * mm});
            skLineSegment(sketch, "E1993", {"start": v(524.58, -417.58) * mm, "end": v(525.95, -418.06) * mm});
            skLineSegment(sketch, "E1994", {"start": v(525.95, -418.06) * mm, "end": v(527.1, -418.23) * mm});
            skLineSegment(sketch, "E1995", {"start": v(527.1, -418.23) * mm, "end": v(527.47, -418.23) * mm});
            skLineSegment(sketch, "E1996", {"start": v(527.47, -418.23) * mm, "end": v(532.4, -418.23) * mm});
            skLineSegment(sketch, "E1997", {"start": v(532.4, -418.23) * mm, "end": v(532.9, -418.23) * mm});
            skLineSegment(sketch, "E1998", {"start": v(532.9, -418.23) * mm, "end": v(534.4, -417.93) * mm});
            skLineSegment(sketch, "E1999", {"start": v(534.4, -417.93) * mm, "end": v(536.26, -417.1) * mm});
            skLineSegment(sketch, "E2000", {"start": v(536.26, -417.1) * mm, "end": v(537.8, -415.79) * mm});
            skLineSegment(sketch, "E2001", {"start": v(537.8, -415.79) * mm, "end": v(538.75, -414.54) * mm});
            skLineSegment(sketch, "E2002", {"start": v(538.75, -414.54) * mm, "end": v(538.98, -414.08) * mm});
            skLineSegment(sketch, "E2003", {"start": v(538.98, -414.08) * mm, "end": v(551.9, -384.34) * mm});
            skLineSegment(sketch, "E2004", {"start": v(551.9, -384.34) * mm, "end": v(612.97, -384.34) * mm});
            skLineSegment(sketch, "E2005", {"start": v(612.97, -384.34) * mm, "end": v(626, -413.9) * mm});
            skLineSegment(sketch, "E2006", {"start": v(626, -413.9) * mm, "end": v(626.1, -414.11) * mm});
            skLineSegment(sketch, "E2007", {"start": v(626.1, -414.11) * mm, "end": v(626.33, -414.57) * mm});
            skLineSegment(sketch, "E2008", {"start": v(626.33, -414.57) * mm, "end": v(627.27, -415.8) * mm});
            skLineSegment(sketch, "E2009", {"start": v(627.27, -415.8) * mm, "end": v(628.82, -417.1) * mm});
            skLineSegment(sketch, "E2010", {"start": v(628.82, -417.1) * mm, "end": v(630.65, -417.94) * mm});
            skLineSegment(sketch, "E2011", {"start": v(630.65, -417.94) * mm, "end": v(632.14, -418.23) * mm});
            skLineSegment(sketch, "E2012", {"start": v(632.14, -418.23) * mm, "end": v(632.65, -418.23) * mm});
            skLineSegment(sketch, "E2013", {"start": v(632.65, -418.23) * mm, "end": v(637.22, -418.23) * mm});
            skLineSegment(sketch, "E2014", {"start": v(637.22, -418.23) * mm, "end": v(637.7, -418.23) * mm});
            skLineSegment(sketch, "E2015", {"start": v(637.7, -418.23) * mm, "end": v(639.18, -418) * mm});
            skLineSegment(sketch, "E2016", {"start": v(639.18, -418) * mm, "end": v(640.68, -417.42) * mm});
            skLineSegment(sketch, "E2017", {"start": v(640.68, -417.42) * mm, "end": v(641.77, -416.63) * mm});
            skLineSegment(sketch, "E2018", {"start": v(641.77, -416.63) * mm, "end": v(642.36, -416) * mm});
            skLineSegment(sketch, "E2019", {"start": v(642.36, -416) * mm, "end": v(642.53, -415.77) * mm});
            skLineSegment(sketch, "E2020", {"start": v(642.53, -415.77) * mm, "end": v(642.69, -415.54) * mm});
            skLineSegment(sketch, "E2021", {"start": v(642.69, -415.54) * mm, "end": v(643.1, -414.8) * mm});
            skLineSegment(sketch, "E2022", {"start": v(643.1, -414.8) * mm, "end": v(643.47, -413.52) * mm});
            skLineSegment(sketch, "E2023", {"start": v(643.47, -413.52) * mm, "end": v(643.55, -411.93) * mm});
            skLineSegment(sketch, "E2024", {"start": v(643.55, -411.93) * mm, "end": v(643.3, -410.5) * mm});
            skLineSegment(sketch, "E2025", {"start": v(643.3, -410.5) * mm, "end": v(643.14, -410.05) * mm});
            skLineSegment(sketch, "E2026", {"start": v(643.14, -410.05) * mm, "end": v(589.45, -287.48) * mm});
            skLineSegment(sketch, "E2027", {"start": v(747.36, -286.15) * mm, "end": v(671.84, -286.15) * mm});
            skLineSegment(sketch, "E2028", {"start": v(671.84, -286.15) * mm, "end": v(671.18, -286.15) * mm});
            skLineSegment(sketch, "E2029", {"start": v(671.18, -286.15) * mm, "end": v(669.15, -286.68) * mm});
            skLineSegment(sketch, "E2030", {"start": v(669.15, -286.68) * mm, "end": v(666.97, -288.13) * mm});
            skLineSegment(sketch, "E2031", {"start": v(666.97, -288.13) * mm, "end": v(665.52, -290.31) * mm});
            skLineSegment(sketch, "E2032", {"start": v(665.52, -290.31) * mm, "end": v(664.99, -292.34) * mm});
            skLineSegment(sketch, "E2033", {"start": v(664.99, -292.34) * mm, "end": v(664.99, -293.01) * mm});
            skLineSegment(sketch, "E2034", {"start": v(664.99, -293.01) * mm, "end": v(664.99, -295.65) * mm});
            skLineSegment(sketch, "E2035", {"start": v(664.99, -295.65) * mm, "end": v(664.99, -296.46) * mm});
            skLineSegment(sketch, "E2036", {"start": v(664.99, -296.46) * mm, "end": v(665.57, -298.88) * mm});
            skLineSegment(sketch, "E2037", {"start": v(665.57, -298.88) * mm, "end": v(667.12, -301.13) * mm});
            skLineSegment(sketch, "E2038", {"start": v(667.12, -301.13) * mm, "end": v(669.33, -302.45) * mm});
            skLineSegment(sketch, "E2039", {"start": v(669.33, -302.45) * mm, "end": v(671.2, -302.87) * mm});
            skLineSegment(sketch, "E2040", {"start": v(671.2, -302.87) * mm, "end": v(671.84, -302.87) * mm});
            skLineSegment(sketch, "E2041", {"start": v(671.84, -302.87) * mm, "end": v(700.8, -302.87) * mm});
            skLineSegment(sketch, "E2042", {"start": v(700.8, -302.87) * mm, "end": v(700.8, -411.36) * mm});
            skLineSegment(sketch, "E2043", {"start": v(700.8, -411.36) * mm, "end": v(700.8, -412.02) * mm});
            skLineSegment(sketch, "E2044", {"start": v(700.8, -412.02) * mm, "end": v(701.33, -414.03) * mm});
            skLineSegment(sketch, "E2045", {"start": v(701.33, -414.03) * mm, "end": v(702.8, -416.21) * mm});
            skLineSegment(sketch, "E2046", {"start": v(702.8, -416.21) * mm, "end": v(705, -417.69) * mm});
            skLineSegment(sketch, "E2047", {"start": v(705, -417.69) * mm, "end": v(707, -418.23) * mm});
            skLineSegment(sketch, "E2048", {"start": v(707, -418.23) * mm, "end": v(707.66, -418.23) * mm});
            skLineSegment(sketch, "E2049", {"start": v(707.66, -418.23) * mm, "end": v(710.83, -418.23) * mm});
            skLineSegment(sketch, "E2050", {"start": v(710.83, -418.23) * mm, "end": v(711.55, -418.23) * mm});
            skLineSegment(sketch, "E2051", {"start": v(711.55, -418.23) * mm, "end": v(713.73, -417.7) * mm});
            skLineSegment(sketch, "E2052", {"start": v(713.73, -417.7) * mm, "end": v(716.1, -416.24) * mm});
            skLineSegment(sketch, "E2053", {"start": v(716.1, -416.24) * mm, "end": v(717.67, -414.05) * mm});
            skLineSegment(sketch, "E2054", {"start": v(717.67, -414.05) * mm, "end": v(718.23, -412.03) * mm});
            skLineSegment(sketch, "E2055", {"start": v(718.23, -412.03) * mm, "end": v(718.23, -411.36) * mm});
            skLineSegment(sketch, "E2056", {"start": v(718.23, -411.36) * mm, "end": v(718.23, -302.87) * mm});
            skLineSegment(sketch, "E2057", {"start": v(718.23, -302.87) * mm, "end": v(747.36, -302.87) * mm});
            skLineSegment(sketch, "E2058", {"start": v(747.36, -302.87) * mm, "end": v(748.02, -302.87) * mm});
            skLineSegment(sketch, "E2059", {"start": v(748.02, -302.87) * mm, "end": v(750.05, -302.34) * mm});
            skLineSegment(sketch, "E2060", {"start": v(750.05, -302.34) * mm, "end": v(752.24, -300.88) * mm});
            skLineSegment(sketch, "E2061", {"start": v(752.24, -300.88) * mm, "end": v(753.68, -298.7) * mm});
            skLineSegment(sketch, "E2062", {"start": v(753.68, -298.7) * mm, "end": v(754.22, -296.67) * mm});
            skLineSegment(sketch, "E2063", {"start": v(754.22, -296.67) * mm, "end": v(754.22, -296) * mm});
            skLineSegment(sketch, "E2064", {"start": v(754.22, -296) * mm, "end": v(754.22, -293.01) * mm});
            skLineSegment(sketch, "E2065", {"start": v(754.22, -293.01) * mm, "end": v(754.22, -292.34) * mm});
            skLineSegment(sketch, "E2066", {"start": v(754.22, -292.34) * mm, "end": v(753.68, -290.31) * mm});
            skLineSegment(sketch, "E2067", {"start": v(753.68, -290.31) * mm, "end": v(752.24, -288.13) * mm});
            skLineSegment(sketch, "E2068", {"start": v(752.24, -288.13) * mm, "end": v(750.05, -286.68) * mm});
            skLineSegment(sketch, "E2069", {"start": v(750.05, -286.68) * mm, "end": v(748.02, -286.15) * mm});
            skLineSegment(sketch, "E2070", {"start": v(748.02, -286.15) * mm, "end": v(747.36, -286.15) * mm});
            skLineSegment(sketch, "E2071", {"start": v(-1582.48, -172.72) * mm, "end": v(-1587, -169.9) * mm});
            skLineSegment(sketch, "E2072", {"start": v(-1587, -169.9) * mm, "end": v(-1600.31, -161.05) * mm});
            skLineSegment(sketch, "E2073", {"start": v(-1600.31, -161.05) * mm, "end": v(-1617.26, -148.85) * mm});
            skLineSegment(sketch, "E2074", {"start": v(-1617.26, -148.85) * mm, "end": v(-1633.3, -136.14) * mm});
            skLineSegment(sketch, "E2075", {"start": v(-1633.3, -136.14) * mm, "end": v(-1648.41, -122.93) * mm});
            skLineSegment(sketch, "E2076", {"start": v(-1648.41, -122.93) * mm, "end": v(-1662.6, -109.23) * mm});
            skLineSegment(sketch, "E2077", {"start": v(-1662.6, -109.23) * mm, "end": v(-1675.84, -95.04) * mm});
            skLineSegment(sketch, "E2078", {"start": v(-1675.84, -95.04) * mm, "end": v(-1688.12, -80.4) * mm});
            skLineSegment(sketch, "E2079", {"start": v(-1688.12, -80.4) * mm, "end": v(-1696.71, -69.15) * mm});
            skLineSegment(sketch, "E2080", {"start": v(-1696.71, -69.15) * mm, "end": v(-1699.43, -65.3) * mm});
            skLineSegment(sketch, "E2081", {"start": v(-1699.43, -65.3) * mm, "end": v(-1702.94, -60.32) * mm});
            skLineSegment(sketch, "E2082", {"start": v(-1702.94, -60.32) * mm, "end": v(-1712.72, -44.88) * mm});
            skLineSegment(sketch, "E2083", {"start": v(-1712.72, -44.88) * mm, "end": v(-1724.26, -23.77) * mm});
            skLineSegment(sketch, "E2084", {"start": v(-1724.26, -23.77) * mm, "end": v(-1734.05, -1.98) * mm});
            skLineSegment(sketch, "E2085", {"start": v(-1734.05, -1.98) * mm, "end": v(-1742.06, 20.47) * mm});
            skLineSegment(sketch, "E2086", {"start": v(-1742.06, 20.47) * mm, "end": v(-1748.3, 43.54) * mm});
            skLineSegment(sketch, "E2087", {"start": v(-1748.3, 43.54) * mm, "end": v(-1752.78, 67.24) * mm});
            skLineSegment(sketch, "E2088", {"start": v(-1752.78, 67.24) * mm, "end": v(-1755.46, 91.53) * mm});
            skLineSegment(sketch, "E2089", {"start": v(-1755.46, 91.53) * mm, "end": v(-1756.36, 110.18) * mm});
            skLineSegment(sketch, "E2090", {"start": v(-1756.36, 110.18) * mm, "end": v(-1756.36, 116.4) * mm});
            skLineSegment(sketch, "E2091", {"start": v(-1756.36, 116.4) * mm, "end": v(-1756.36, 122.62) * mm});
            skLineSegment(sketch, "E2092", {"start": v(-1756.36, 122.62) * mm, "end": v(-1755.46, 141.27) * mm});
            skLineSegment(sketch, "E2093", {"start": v(-1755.46, 141.27) * mm, "end": v(-1752.78, 165.56) * mm});
            skLineSegment(sketch, "E2094", {"start": v(-1752.78, 165.56) * mm, "end": v(-1748.3, 189.26) * mm});
            skLineSegment(sketch, "E2095", {"start": v(-1748.3, 189.26) * mm, "end": v(-1742.06, 212.33) * mm});
            skLineSegment(sketch, "E2096", {"start": v(-1742.06, 212.33) * mm, "end": v(-1734.05, 234.78) * mm});
            skLineSegment(sketch, "E2097", {"start": v(-1734.05, 234.78) * mm, "end": v(-1724.26, 256.56) * mm});
            skLineSegment(sketch, "E2098", {"start": v(-1724.26, 256.56) * mm, "end": v(-1712.72, 277.67) * mm});
            skLineSegment(sketch, "E2099", {"start": v(-1712.72, 277.67) * mm, "end": v(-1702.94, 293.12) * mm});
            skLineSegment(sketch, "E2100", {"start": v(-1702.94, 293.12) * mm, "end": v(-1699.43, 298.09) * mm});
            skLineSegment(sketch, "E2101", {"start": v(-1699.43, 298.09) * mm, "end": v(-1696.71, 301.94) * mm});
            skLineSegment(sketch, "E2102", {"start": v(-1696.71, 301.94) * mm, "end": v(-1688.12, 313.18) * mm});
            skLineSegment(sketch, "E2103", {"start": v(-1688.12, 313.18) * mm, "end": v(-1675.84, 327.84) * mm});
            skLineSegment(sketch, "E2104", {"start": v(-1675.84, 327.84) * mm, "end": v(-1662.6, 342.01) * mm});
            skLineSegment(sketch, "E2105", {"start": v(-1662.6, 342.01) * mm, "end": v(-1648.41, 355.72) * mm});
            skLineSegment(sketch, "E2106", {"start": v(-1648.41, 355.72) * mm, "end": v(-1633.3, 368.93) * mm});
            skLineSegment(sketch, "E2107", {"start": v(-1633.3, 368.93) * mm, "end": v(-1617.26, 381.64) * mm});
            skLineSegment(sketch, "E2108", {"start": v(-1617.26, 381.64) * mm, "end": v(-1600.31, 393.84) * mm});
            skLineSegment(sketch, "E2109", {"start": v(-1600.31, 393.84) * mm, "end": v(-1587, 402.7) * mm});
            skLineSegment(sketch, "E2110", {"start": v(-1587, 402.7) * mm, "end": v(-1582.48, 405.51) * mm});
            skLineSegment(sketch, "E2111", {"start": v(-1582.48, 405.51) * mm, "end": v(-1579.1, 407.62) * mm});
            skLineSegment(sketch, "E2112", {"start": v(-1579.1, 407.62) * mm, "end": v(-1566.94, 390.61) * mm});
            skLineSegment(sketch, "E2113", {"start": v(-1566.94, 390.61) * mm, "end": v(-1570.36, 388.14) * mm});
            skLineSegment(sketch, "E2114", {"start": v(-1570.36, 388.14) * mm, "end": v(-1574.5, 385.14) * mm});
            skLineSegment(sketch, "E2115", {"start": v(-1574.5, 385.14) * mm, "end": v(-1586.62, 375.65) * mm});
            skLineSegment(sketch, "E2116", {"start": v(-1586.62, 375.65) * mm, "end": v(-1601.47, 362.75) * mm});
            skLineSegment(sketch, "E2117", {"start": v(-1601.47, 362.75) * mm, "end": v(-1614.96, 349.37) * mm});
            skLineSegment(sketch, "E2118", {"start": v(-1614.96, 349.37) * mm, "end": v(-1627.14, 335.46) * mm});
            skLineSegment(sketch, "E2119", {"start": v(-1627.14, 335.46) * mm, "end": v(-1638.06, 320.94) * mm});
            skLineSegment(sketch, "E2120", {"start": v(-1638.06, 320.94) * mm, "end": v(-1647.78, 305.76) * mm});
            skLineSegment(sketch, "E2121", {"start": v(-1647.78, 305.76) * mm, "end": v(-1656.35, 289.85) * mm});
            skLineSegment(sketch, "E2122", {"start": v(-1656.35, 289.85) * mm, "end": v(-1662.1, 277.39) * mm});
            skLineSegment(sketch, "E2123", {"start": v(-1662.1, 277.39) * mm, "end": v(-1663.8, 273.14) * mm});
            skLineSegment(sketch, "E2124", {"start": v(-1663.8, 273.14) * mm, "end": v(-1665.38, 269.25) * mm});
            skLineSegment(sketch, "E2125", {"start": v(-1665.38, 269.25) * mm, "end": v(-1669.61, 257.35) * mm});
            skLineSegment(sketch, "E2126", {"start": v(-1669.61, 257.35) * mm, "end": v(-1674.6, 240.63) * mm});
            skLineSegment(sketch, "E2127", {"start": v(-1674.6, 240.63) * mm, "end": v(-1678.78, 222.92) * mm});
            skLineSegment(sketch, "E2128", {"start": v(-1678.78, 222.92) * mm, "end": v(-1682.18, 204.12) * mm});
            skLineSegment(sketch, "E2129", {"start": v(-1682.18, 204.12) * mm, "end": v(-1684.8, 184.16) * mm});
            skLineSegment(sketch, "E2130", {"start": v(-1684.8, 184.16) * mm, "end": v(-1686.65, 162.94) * mm});
            skLineSegment(sketch, "E2131", {"start": v(-1686.65, 162.94) * mm, "end": v(-1687.75, 140.38) * mm});
            skLineSegment(sketch, "E2132", {"start": v(-1687.75, 140.38) * mm, "end": v(-1688.11, 122.4) * mm});
            skLineSegment(sketch, "E2133", {"start": v(-1688.11, 122.4) * mm, "end": v(-1688.11, 116.4) * mm});
            skLineSegment(sketch, "E2134", {"start": v(-1688.11, 116.4) * mm, "end": v(-1688.11, 110.4) * mm});
            skLineSegment(sketch, "E2135", {"start": v(-1688.11, 110.4) * mm, "end": v(-1687.75, 92.41) * mm});
            skLineSegment(sketch, "E2136", {"start": v(-1687.75, 92.41) * mm, "end": v(-1686.65, 69.85) * mm});
            skLineSegment(sketch, "E2137", {"start": v(-1686.65, 69.85) * mm, "end": v(-1684.8, 48.63) * mm});
            skLineSegment(sketch, "E2138", {"start": v(-1684.8, 48.63) * mm, "end": v(-1682.18, 28.67) * mm});
            skLineSegment(sketch, "E2139", {"start": v(-1682.18, 28.67) * mm, "end": v(-1678.78, 9.88) * mm});
            skLineSegment(sketch, "E2140", {"start": v(-1678.78, 9.88) * mm, "end": v(-1674.6, -7.84) * mm});
            skLineSegment(sketch, "E2141", {"start": v(-1674.6, -7.84) * mm, "end": v(-1669.61, -24.55) * mm});
            skLineSegment(sketch, "E2142", {"start": v(-1669.61, -24.55) * mm, "end": v(-1665.38, -36.46) * mm});
            skLineSegment(sketch, "E2143", {"start": v(-1665.38, -36.46) * mm, "end": v(-1663.8, -40.35) * mm});
            skLineSegment(sketch, "E2144", {"start": v(-1663.8, -40.35) * mm, "end": v(-1662.1, -44.6) * mm});
            skLineSegment(sketch, "E2145", {"start": v(-1662.1, -44.6) * mm, "end": v(-1656.35, -57.06) * mm});
            skLineSegment(sketch, "E2146", {"start": v(-1656.35, -57.06) * mm, "end": v(-1647.78, -72.96) * mm});
            skLineSegment(sketch, "E2147", {"start": v(-1647.78, -72.96) * mm, "end": v(-1638.06, -88.15) * mm});
            skLineSegment(sketch, "E2148", {"start": v(-1638.06, -88.15) * mm, "end": v(-1627.14, -102.66) * mm});
            skLineSegment(sketch, "E2149", {"start": v(-1627.14, -102.66) * mm, "end": v(-1614.96, -116.58) * mm});
            skLineSegment(sketch, "E2150", {"start": v(-1614.96, -116.58) * mm, "end": v(-1601.47, -129.96) * mm});
            skLineSegment(sketch, "E2151", {"start": v(-1601.47, -129.96) * mm, "end": v(-1586.62, -142.86) * mm});
            skLineSegment(sketch, "E2152", {"start": v(-1586.62, -142.86) * mm, "end": v(-1574.5, -152.34) * mm});
            skLineSegment(sketch, "E2153", {"start": v(-1574.5, -152.34) * mm, "end": v(-1570.36, -155.35) * mm});
            skLineSegment(sketch, "E2154", {"start": v(-1570.36, -155.35) * mm, "end": v(-1566.94, -157.82) * mm});
            skLineSegment(sketch, "E2155", {"start": v(-1566.94, -157.82) * mm, "end": v(-1579.1, -174.83) * mm});
            skLineSegment(sketch, "E2156", {"start": v(-1579.1, -174.83) * mm, "end": v(-1582.48, -172.72) * mm});
            skLineSegment(sketch, "E2157", {"start": v(-1147.8, -98.11) * mm, "end": v(-1147.8, -74.87) * mm});
            skLineSegment(sketch, "E2158", {"start": v(-1147.8, -74.87) * mm, "end": v(-1100.58, -74.87) * mm});
            skLineSegment(sketch, "E2159", {"start": v(-1100.58, -74.87) * mm, "end": v(-1100.58, 151.07) * mm});
            skLineSegment(sketch, "E2160", {"start": v(-1100.58, 151.07) * mm, "end": v(-1100.58, 153.74) * mm});
            skLineSegment(sketch, "E2161", {"start": v(-1100.58, 153.74) * mm, "end": v(-1100.81, 161.75) * mm});
            skLineSegment(sketch, "E2162", {"start": v(-1100.81, 161.75) * mm, "end": v(-1101.53, 171.52) * mm});
            skLineSegment(sketch, "E2163", {"start": v(-1101.53, 171.52) * mm, "end": v(-1102.72, 180.43) * mm});
            skLineSegment(sketch, "E2164", {"start": v(-1102.72, 180.43) * mm, "end": v(-1104.42, 188.5) * mm});
            skLineSegment(sketch, "E2165", {"start": v(-1104.42, 188.5) * mm, "end": v(-1106.6, 195.76) * mm});
            skLineSegment(sketch, "E2166", {"start": v(-1106.6, 195.76) * mm, "end": v(-1109.32, 202.27) * mm});
            skLineSegment(sketch, "E2167", {"start": v(-1109.32, 202.27) * mm, "end": v(-1112.54, 208.03) * mm});
            skLineSegment(sketch, "E2168", {"start": v(-1112.54, 208.03) * mm, "end": v(-1115.28, 211.9) * mm});
            skLineSegment(sketch, "E2169", {"start": v(-1115.28, 211.9) * mm, "end": v(-1116.3, 213.1) * mm});
            skLineSegment(sketch, "E2170", {"start": v(-1116.3, 213.1) * mm, "end": v(-1117.42, 214.42) * mm});
            skLineSegment(sketch, "E2171", {"start": v(-1117.42, 214.42) * mm, "end": v(-1121.2, 218.01) * mm});
            skLineSegment(sketch, "E2172", {"start": v(-1121.2, 218.01) * mm, "end": v(-1126.5, 221.84) * mm});
            skLineSegment(sketch, "E2173", {"start": v(-1126.5, 221.84) * mm, "end": v(-1132.04, 224.72) * mm});
            skLineSegment(sketch, "E2174", {"start": v(-1132.04, 224.72) * mm, "end": v(-1137.7, 226.78) * mm});
            skLineSegment(sketch, "E2175", {"start": v(-1137.7, 226.78) * mm, "end": v(-1143.36, 228.15) * mm});
            skLineSegment(sketch, "E2176", {"start": v(-1143.36, 228.15) * mm, "end": v(-1148.9, 228.96) * mm});
            skLineSegment(sketch, "E2177", {"start": v(-1148.9, 228.96) * mm, "end": v(-1154.16, 229.35) * mm});
            skLineSegment(sketch, "E2178", {"start": v(-1154.16, 229.35) * mm, "end": v(-1157.82, 229.45) * mm});
            skLineSegment(sketch, "E2179", {"start": v(-1157.82, 229.45) * mm, "end": v(-1159.04, 229.45) * mm});
            skLineSegment(sketch, "E2180", {"start": v(-1159.04, 229.45) * mm, "end": v(-1161.12, 229.45) * mm});
            skLineSegment(sketch, "E2181", {"start": v(-1161.12, 229.45) * mm, "end": v(-1167.35, 229.02) * mm});
            skLineSegment(sketch, "E2182", {"start": v(-1167.35, 229.02) * mm, "end": v(-1175.56, 227.72) * mm});
            skLineSegment(sketch, "E2183", {"start": v(-1175.56, 227.72) * mm, "end": v(-1183.65, 225.55) * mm});
            skLineSegment(sketch, "E2184", {"start": v(-1183.65, 225.55) * mm, "end": v(-1191.62, 222.53) * mm});
            skLineSegment(sketch, "E2185", {"start": v(-1191.62, 222.53) * mm, "end": v(-1199.45, 218.65) * mm});
            skLineSegment(sketch, "E2186", {"start": v(-1199.45, 218.65) * mm, "end": v(-1207.16, 213.91) * mm});
            skLineSegment(sketch, "E2187", {"start": v(-1207.16, 213.91) * mm, "end": v(-1214.72, 208.32) * mm});
            skLineSegment(sketch, "E2188", {"start": v(-1214.72, 208.32) * mm, "end": v(-1220.35, 203.56) * mm});
            skLineSegment(sketch, "E2189", {"start": v(-1220.35, 203.56) * mm, "end": v(-1222.14, 201.88) * mm});
            skLineSegment(sketch, "E2190", {"start": v(-1222.14, 201.88) * mm, "end": v(-1223.07, 201.02) * mm});
            skLineSegment(sketch, "E2191", {"start": v(-1223.07, 201.02) * mm, "end": v(-1225.78, 198.35) * mm});
            skLineSegment(sketch, "E2192", {"start": v(-1225.78, 198.35) * mm, "end": v(-1229.79, 194.16) * mm});
            skLineSegment(sketch, "E2193", {"start": v(-1229.79, 194.16) * mm, "end": v(-1234.1, 189.29) * mm});
            skLineSegment(sketch, "E2194", {"start": v(-1234.1, 189.29) * mm, "end": v(-1238.68, 183.7) * mm});
            skLineSegment(sketch, "E2195", {"start": v(-1238.68, 183.7) * mm, "end": v(-1243.46, 177.36) * mm});
            skLineSegment(sketch, "E2196", {"start": v(-1243.46, 177.36) * mm, "end": v(-1248.37, 170.26) * mm});
            skLineSegment(sketch, "E2197", {"start": v(-1248.37, 170.26) * mm, "end": v(-1253.36, 162.37) * mm});
            skLineSegment(sketch, "E2198", {"start": v(-1253.36, 162.37) * mm, "end": v(-1257.17, 155.86) * mm});
            skLineSegment(sketch, "E2199", {"start": v(-1257.17, 155.86) * mm, "end": v(-1258.38, 153.66) * mm});
            skLineSegment(sketch, "E2200", {"start": v(-1258.38, 153.66) * mm, "end": v(-1259.56, 151.51) * mm});
            skLineSegment(sketch, "E2201", {"start": v(-1259.56, 151.51) * mm, "end": v(-1259.56, -74.87) * mm});
            skLineSegment(sketch, "E2202", {"start": v(-1259.56, -74.87) * mm, "end": v(-1213.07, -74.87) * mm});
            skLineSegment(sketch, "E2203", {"start": v(-1213.07, -74.87) * mm, "end": v(-1213.07, -98.11) * mm});
            skLineSegment(sketch, "E2204", {"start": v(-1213.07, -98.11) * mm, "end": v(-1383.86, -98.11) * mm});
            skLineSegment(sketch, "E2205", {"start": v(-1383.86, -98.11) * mm, "end": v(-1383.86, -74.87) * mm});
            skLineSegment(sketch, "E2206", {"start": v(-1383.86, -74.87) * mm, "end": v(-1337.39, -74.87) * mm});
            skLineSegment(sketch, "E2207", {"start": v(-1337.39, -74.87) * mm, "end": v(-1337.39, 381.44) * mm});
            skLineSegment(sketch, "E2208", {"start": v(-1337.39, 381.44) * mm, "end": v(-1383.86, 381.44) * mm});
            skLineSegment(sketch, "E2209", {"start": v(-1383.86, 381.44) * mm, "end": v(-1383.86, 404.68) * mm});
            skLineSegment(sketch, "E2210", {"start": v(-1383.86, 404.68) * mm, "end": v(-1259.56, 404.68) * mm});
            skLineSegment(sketch, "E2211", {"start": v(-1259.56, 404.68) * mm, "end": v(-1259.56, 197.25) * mm});
            skLineSegment(sketch, "E2212", {"start": v(-1259.56, 197.25) * mm, "end": v(-1243.2, 214.11) * mm});
            skLineSegment(sketch, "E2213", {"start": v(-1243.2, 214.11) * mm, "end": v(-1240.65, 216.74) * mm});
            skLineSegment(sketch, "E2214", {"start": v(-1240.65, 216.74) * mm, "end": v(-1232.52, 224.16) * mm});
            skLineSegment(sketch, "E2215", {"start": v(-1232.52, 224.16) * mm, "end": v(-1221.26, 232.88) * mm});
            skLineSegment(sketch, "E2216", {"start": v(-1221.26, 232.88) * mm, "end": v(-1209.42, 240.27) * mm});
            skLineSegment(sketch, "E2217", {"start": v(-1209.42, 240.27) * mm, "end": v(-1197.03, 246.32) * mm});
            skLineSegment(sketch, "E2218", {"start": v(-1197.03, 246.32) * mm, "end": v(-1184.09, 251.04) * mm});
            skLineSegment(sketch, "E2219", {"start": v(-1184.09, 251.04) * mm, "end": v(-1170.6, 254.42) * mm});
            skLineSegment(sketch, "E2220", {"start": v(-1170.6, 254.42) * mm, "end": v(-1156.6, 256.45) * mm});
            skLineSegment(sketch, "E2221", {"start": v(-1156.6, 256.45) * mm, "end": v(-1145.7, 257.13) * mm});
            skLineSegment(sketch, "E2222", {"start": v(-1145.7, 257.13) * mm, "end": v(-1142.07, 257.13) * mm});
            skLineSegment(sketch, "E2223", {"start": v(-1142.07, 257.13) * mm, "end": v(-1138.34, 257.13) * mm});
            skLineSegment(sketch, "E2224", {"start": v(-1138.34, 257.13) * mm, "end": v(-1127.16, 256.62) * mm});
            skLineSegment(sketch, "E2225", {"start": v(-1127.16, 256.62) * mm, "end": v(-1113.24, 255.1) * mm});
            skLineSegment(sketch, "E2226", {"start": v(-1113.24, 255.1) * mm, "end": v(-1100.36, 252.6) * mm});
            skLineSegment(sketch, "E2227", {"start": v(-1100.36, 252.6) * mm, "end": v(-1091.44, 250.13) * mm});
            skLineSegment(sketch, "E2228", {"start": v(-1091.44, 250.13) * mm, "end": v(-1088.55, 249.1) * mm});
            skLineSegment(sketch, "E2229", {"start": v(-1088.55, 249.1) * mm, "end": v(-1085.87, 248.15) * mm});
            skLineSegment(sketch, "E2230", {"start": v(-1085.87, 248.15) * mm, "end": v(-1078.04, 244.7) * mm});
            skLineSegment(sketch, "E2231", {"start": v(-1078.04, 244.7) * mm, "end": v(-1068.45, 239.33) * mm});
            skLineSegment(sketch, "E2232", {"start": v(-1068.45, 239.33) * mm, "end": v(-1059.8, 233) * mm});
            skLineSegment(sketch, "E2233", {"start": v(-1059.8, 233) * mm, "end": v(-1053.91, 227.65) * mm});
            skLineSegment(sketch, "E2234", {"start": v(-1053.91, 227.65) * mm, "end": v(-1052.12, 225.7) * mm});
            skLineSegment(sketch, "E2235", {"start": v(-1052.12, 225.7) * mm, "end": v(-1050.3, 223.74) * mm});
            skLineSegment(sketch, "E2236", {"start": v(-1050.3, 223.74) * mm, "end": v(-1045.32, 217.35) * mm});
            skLineSegment(sketch, "E2237", {"start": v(-1045.32, 217.35) * mm, "end": v(-1039.4, 207.91) * mm});
            skLineSegment(sketch, "E2238", {"start": v(-1039.4, 207.91) * mm, "end": v(-1034.38, 197.44) * mm});
            skLineSegment(sketch, "E2239", {"start": v(-1034.38, 197.44) * mm, "end": v(-1031.16, 188.87) * mm});
            skLineSegment(sketch, "E2240", {"start": v(-1031.16, 188.87) * mm, "end": v(-1030.27, 185.95) * mm});
            skLineSegment(sketch, "E2241", {"start": v(-1030.27, 185.95) * mm, "end": v(-1029.3, 182.77) * mm});
            skLineSegment(sketch, "E2242", {"start": v(-1029.3, 182.77) * mm, "end": v(-1026.99, 173.04) * mm});
            skLineSegment(sketch, "E2243", {"start": v(-1026.99, 173.04) * mm, "end": v(-1024.64, 158.95) * mm});
            skLineSegment(sketch, "E2244", {"start": v(-1024.64, 158.95) * mm, "end": v(-1023.22, 143.74) * mm});
            skLineSegment(sketch, "E2245", {"start": v(-1023.22, 143.74) * mm, "end": v(-1022.74, 131.54) * mm});
            skLineSegment(sketch, "E2246", {"start": v(-1022.74, 131.54) * mm, "end": v(-1022.74, 127.47) * mm});
            skLineSegment(sketch, "E2247", {"start": v(-1022.74, 127.47) * mm, "end": v(-1022.74, -74.87) * mm});
            skLineSegment(sketch, "E2248", {"start": v(-1022.74, -74.87) * mm, "end": v(-976.27, -74.87) * mm});
            skLineSegment(sketch, "E2249", {"start": v(-976.27, -74.87) * mm, "end": v(-976.27, -98.11) * mm});
            skLineSegment(sketch, "E2250", {"start": v(-976.27, -98.11) * mm, "end": v(-1147.8, -98.11) * mm});
            skLineSegment(sketch, "E2251", {"start": v(-790.04, -98.11) * mm, "end": v(-790.04, -74.87) * mm});
            skLineSegment(sketch, "E2252", {"start": v(-790.04, -74.87) * mm, "end": v(-743.57, -74.87) * mm});
            skLineSegment(sketch, "E2253", {"start": v(-743.57, -74.87) * mm, "end": v(-743.57, 226.5) * mm});
            skLineSegment(sketch, "E2254", {"start": v(-743.57, 226.5) * mm, "end": v(-790.04, 226.5) * mm});
            skLineSegment(sketch, "E2255", {"start": v(-790.04, 226.5) * mm, "end": v(-790.04, 249.75) * mm});
            skLineSegment(sketch, "E2256", {"start": v(-790.04, 249.75) * mm, "end": v(-665.74, 249.75) * mm});
            skLineSegment(sketch, "E2257", {"start": v(-665.74, 249.75) * mm, "end": v(-665.74, -74.87) * mm});
            skLineSegment(sketch, "E2258", {"start": v(-665.74, -74.87) * mm, "end": v(-619.25, -74.87) * mm});
            skLineSegment(sketch, "E2259", {"start": v(-619.25, -74.87) * mm, "end": v(-619.25, -98.11) * mm});
            skLineSegment(sketch, "E2260", {"start": v(-619.25, -98.11) * mm, "end": v(-790.04, -98.11) * mm});
            skLineSegment(sketch, "E2261", {"start": v(-702.44, 301.75) * mm, "end": v(-703.71, 301.75) * mm});
            skLineSegment(sketch, "E2262", {"start": v(-703.71, 301.75) * mm, "end": v(-707.54, 302) * mm});
            skLineSegment(sketch, "E2263", {"start": v(-707.54, 302) * mm, "end": v(-712.5, 302.74) * mm});
            skLineSegment(sketch, "E2264", {"start": v(-712.5, 302.74) * mm, "end": v(-717.28, 303.94) * mm});
            skLineSegment(sketch, "E2265", {"start": v(-717.28, 303.94) * mm, "end": v(-721.87, 305.58) * mm});
            skLineSegment(sketch, "E2266", {"start": v(-721.87, 305.58) * mm, "end": v(-726.24, 307.62) * mm});
            skLineSegment(sketch, "E2267", {"start": v(-726.24, 307.62) * mm, "end": v(-730.36, 310.05) * mm});
            skLineSegment(sketch, "E2268", {"start": v(-730.36, 310.05) * mm, "end": v(-734.21, 312.85) * mm});
            skLineSegment(sketch, "E2269", {"start": v(-734.21, 312.85) * mm, "end": v(-737.76, 315.98) * mm});
            skLineSegment(sketch, "E2270", {"start": v(-737.76, 315.98) * mm, "end": v(-741, 319.43) * mm});
            skLineSegment(sketch, "E2271", {"start": v(-741, 319.43) * mm, "end": v(-743.87, 323.16) * mm});
            skLineSegment(sketch, "E2272", {"start": v(-743.87, 323.16) * mm, "end": v(-746.38, 327.16) * mm});
            skLineSegment(sketch, "E2273", {"start": v(-746.38, 327.16) * mm, "end": v(-748.49, 331.4) * mm});
            skLineSegment(sketch, "E2274", {"start": v(-748.49, 331.4) * mm, "end": v(-750.17, 335.86) * mm});
            skLineSegment(sketch, "E2275", {"start": v(-750.17, 335.86) * mm, "end": v(-751.4, 340.5) * mm});
            skLineSegment(sketch, "E2276", {"start": v(-751.4, 340.5) * mm, "end": v(-752.16, 345.31) * mm});
            skLineSegment(sketch, "E2277", {"start": v(-752.16, 345.31) * mm, "end": v(-752.42, 349.03) * mm});
            skLineSegment(sketch, "E2278", {"start": v(-752.42, 349.03) * mm, "end": v(-752.42, 350.27) * mm});
            skLineSegment(sketch, "E2279", {"start": v(-752.42, 350.27) * mm, "end": v(-752.42, 351.53) * mm});
            skLineSegment(sketch, "E2280", {"start": v(-752.42, 351.53) * mm, "end": v(-752.16, 355.3) * mm});
            skLineSegment(sketch, "E2281", {"start": v(-752.16, 355.3) * mm, "end": v(-751.4, 360.18) * mm});
            skLineSegment(sketch, "E2282", {"start": v(-751.4, 360.18) * mm, "end": v(-750.17, 364.9) * mm});
            skLineSegment(sketch, "E2283", {"start": v(-750.17, 364.9) * mm, "end": v(-748.49, 369.42) * mm});
            skLineSegment(sketch, "E2284", {"start": v(-748.49, 369.42) * mm, "end": v(-746.38, 373.73) * mm});
            skLineSegment(sketch, "E2285", {"start": v(-746.38, 373.73) * mm, "end": v(-743.87, 377.79) * mm});
            skLineSegment(sketch, "E2286", {"start": v(-743.87, 377.79) * mm, "end": v(-741, 381.58) * mm});
            skLineSegment(sketch, "E2287", {"start": v(-741, 381.58) * mm, "end": v(-737.76, 385.08) * mm});
            skLineSegment(sketch, "E2288", {"start": v(-737.76, 385.08) * mm, "end": v(-734.21, 388.26) * mm});
            skLineSegment(sketch, "E2289", {"start": v(-734.21, 388.26) * mm, "end": v(-730.36, 391.1) * mm});
            skLineSegment(sketch, "E2290", {"start": v(-730.36, 391.1) * mm, "end": v(-726.24, 393.57) * mm});
            skLineSegment(sketch, "E2291", {"start": v(-726.24, 393.57) * mm, "end": v(-721.87, 395.64) * mm});
            skLineSegment(sketch, "E2292", {"start": v(-721.87, 395.64) * mm, "end": v(-717.28, 397.3) * mm});
            skLineSegment(sketch, "E2293", {"start": v(-717.28, 397.3) * mm, "end": v(-712.5, 398.52) * mm});
            skLineSegment(sketch, "E2294", {"start": v(-712.5, 398.52) * mm, "end": v(-707.54, 399.26) * mm});
            skLineSegment(sketch, "E2295", {"start": v(-707.54, 399.26) * mm, "end": v(-703.71, 399.52) * mm});
            skLineSegment(sketch, "E2296", {"start": v(-703.71, 399.52) * mm, "end": v(-702.44, 399.52) * mm});
            skLineSegment(sketch, "E2297", {"start": v(-702.44, 399.52) * mm, "end": v(-701.24, 399.52) * mm});
            skLineSegment(sketch, "E2298", {"start": v(-701.24, 399.52) * mm, "end": v(-697.63, 399.29) * mm});
            skLineSegment(sketch, "E2299", {"start": v(-697.63, 399.29) * mm, "end": v(-692.93, 398.59) * mm});
            skLineSegment(sketch, "E2300", {"start": v(-692.93, 398.59) * mm, "end": v(-688.37, 397.45) * mm});
            skLineSegment(sketch, "E2301", {"start": v(-688.37, 397.45) * mm, "end": v(-683.98, 395.87) * mm});
            skLineSegment(sketch, "E2302", {"start": v(-683.98, 395.87) * mm, "end": v(-679.77, 393.86) * mm});
            skLineSegment(sketch, "E2303", {"start": v(-679.77, 393.86) * mm, "end": v(-675.79, 391.43) * mm});
            skLineSegment(sketch, "E2304", {"start": v(-675.79, 391.43) * mm, "end": v(-672.04, 388.6) * mm});
            skLineSegment(sketch, "E2305", {"start": v(-672.04, 388.6) * mm, "end": v(-669.39, 386.22) * mm});
            skLineSegment(sketch, "E2306", {"start": v(-669.39, 386.22) * mm, "end": v(-668.56, 385.37) * mm});
            skLineSegment(sketch, "E2307", {"start": v(-668.56, 385.37) * mm, "end": v(-667.72, 384.51) * mm});
            skLineSegment(sketch, "E2308", {"start": v(-667.72, 384.51) * mm, "end": v(-665.4, 381.77) * mm});
            skLineSegment(sketch, "E2309", {"start": v(-665.4, 381.77) * mm, "end": v(-662.6, 377.9) * mm});
            skLineSegment(sketch, "E2310", {"start": v(-662.6, 377.9) * mm, "end": v(-660.23, 373.76) * mm});
            skLineSegment(sketch, "E2311", {"start": v(-660.23, 373.76) * mm, "end": v(-658.25, 369.41) * mm});
            skLineSegment(sketch, "E2312", {"start": v(-658.25, 369.41) * mm, "end": v(-656.7, 364.86) * mm});
            skLineSegment(sketch, "E2313", {"start": v(-656.7, 364.86) * mm, "end": v(-655.58, 360.13) * mm});
            skLineSegment(sketch, "E2314", {"start": v(-655.58, 360.13) * mm, "end": v(-654.9, 355.26) * mm});
            skLineSegment(sketch, "E2315", {"start": v(-654.9, 355.26) * mm, "end": v(-654.66, 351.52) * mm});
            skLineSegment(sketch, "E2316", {"start": v(-654.66, 351.52) * mm, "end": v(-654.66, 350.27) * mm});
            skLineSegment(sketch, "E2317", {"start": v(-654.66, 350.27) * mm, "end": v(-654.66, 349.03) * mm});
            skLineSegment(sketch, "E2318", {"start": v(-654.66, 349.03) * mm, "end": v(-654.9, 345.31) * mm});
            skLineSegment(sketch, "E2319", {"start": v(-654.9, 345.31) * mm, "end": v(-655.64, 340.5) * mm});
            skLineSegment(sketch, "E2320", {"start": v(-655.64, 340.5) * mm, "end": v(-656.81, 335.86) * mm});
            skLineSegment(sketch, "E2321", {"start": v(-656.81, 335.86) * mm, "end": v(-658.42, 331.4) * mm});
            skLineSegment(sketch, "E2322", {"start": v(-658.42, 331.4) * mm, "end": v(-660.44, 327.16) * mm});
            skLineSegment(sketch, "E2323", {"start": v(-660.44, 327.16) * mm, "end": v(-662.83, 323.16) * mm});
            skLineSegment(sketch, "E2324", {"start": v(-662.83, 323.16) * mm, "end": v(-665.59, 319.43) * mm});
            skLineSegment(sketch, "E2325", {"start": v(-665.59, 319.43) * mm, "end": v(-668.67, 315.98) * mm});
            skLineSegment(sketch, "E2326", {"start": v(-668.67, 315.98) * mm, "end": v(-672.07, 312.85) * mm});
            skLineSegment(sketch, "E2327", {"start": v(-672.07, 312.85) * mm, "end": v(-675.74, 310.05) * mm});
            skLineSegment(sketch, "E2328", {"start": v(-675.74, 310.05) * mm, "end": v(-679.69, 307.62) * mm});
            skLineSegment(sketch, "E2329", {"start": v(-679.69, 307.62) * mm, "end": v(-683.86, 305.58) * mm});
            skLineSegment(sketch, "E2330", {"start": v(-683.86, 305.58) * mm, "end": v(-688.25, 303.94) * mm});
            skLineSegment(sketch, "E2331", {"start": v(-688.25, 303.94) * mm, "end": v(-692.82, 302.74) * mm});
            skLineSegment(sketch, "E2332", {"start": v(-692.82, 302.74) * mm, "end": v(-697.56, 302) * mm});
            skLineSegment(sketch, "E2333", {"start": v(-697.56, 302) * mm, "end": v(-701.22, 301.75) * mm});
            skLineSegment(sketch, "E2334", {"start": v(-701.22, 301.75) * mm, "end": v(-702.44, 301.75) * mm});
            skLineSegment(sketch, "E2335", {"start": v(-248.27, 70.13) * mm, "end": v(-251.08, 69.79) * mm});
            skLineSegment(sketch, "E2336", {"start": v(-251.08, 69.79) * mm, "end": v(-259.47, 68.53) * mm});
            skLineSegment(sketch, "E2337", {"start": v(-259.47, 68.53) * mm, "end": v(-269.73, 66.57) * mm});
            skLineSegment(sketch, "E2338", {"start": v(-269.73, 66.57) * mm, "end": v(-279.1, 64.23) * mm});
            skLineSegment(sketch, "E2339", {"start": v(-279.1, 64.23) * mm, "end": v(-287.6, 61.5) * mm});
            skLineSegment(sketch, "E2340", {"start": v(-287.6, 61.5) * mm, "end": v(-295.3, 58.36) * mm});
            skLineSegment(sketch, "E2341", {"start": v(-295.3, 58.36) * mm, "end": v(-302.2, 54.8) * mm});
            skLineSegment(sketch, "E2342", {"start": v(-302.2, 54.8) * mm, "end": v(-308.35, 50.83) * mm});
            skLineSegment(sketch, "E2343", {"start": v(-308.35, 50.83) * mm, "end": v(-312.5, 47.58) * mm});
            skLineSegment(sketch, "E2344", {"start": v(-312.5, 47.58) * mm, "end": v(-313.79, 46.4) * mm});
            skLineSegment(sketch, "E2345", {"start": v(-313.79, 46.4) * mm, "end": v(-315.1, 45.2) * mm});
            skLineSegment(sketch, "E2346", {"start": v(-315.1, 45.2) * mm, "end": v(-318.74, 41.3) * mm});
            skLineSegment(sketch, "E2347", {"start": v(-318.74, 41.3) * mm, "end": v(-323, 35.69) * mm});
            skLineSegment(sketch, "E2348", {"start": v(-323, 35.69) * mm, "end": v(-326.58, 29.54) * mm});
            skLineSegment(sketch, "E2349", {"start": v(-326.58, 29.54) * mm, "end": v(-329.48, 22.8) * mm});
            skLineSegment(sketch, "E2350", {"start": v(-329.48, 22.8) * mm, "end": v(-331.7, 15.47) * mm});
            skLineSegment(sketch, "E2351", {"start": v(-331.7, 15.47) * mm, "end": v(-333.29, 7.5) * mm});
            skLineSegment(sketch, "E2352", {"start": v(-333.29, 7.5) * mm, "end": v(-334.23, -1.16) * mm});
            skLineSegment(sketch, "E2353", {"start": v(-334.23, -1.16) * mm, "end": v(-334.54, -8.16) * mm});
            skLineSegment(sketch, "E2354", {"start": v(-334.54, -8.16) * mm, "end": v(-334.54, -10.5) * mm});
            skLineSegment(sketch, "E2355", {"start": v(-334.54, -10.5) * mm, "end": v(-334.54, -12.46) * mm});
            skLineSegment(sketch, "E2356", {"start": v(-334.54, -12.46) * mm, "end": v(-334.32, -18.34) * mm});
            skLineSegment(sketch, "E2357", {"start": v(-334.32, -18.34) * mm, "end": v(-333.64, -25.64) * mm});
            skLineSegment(sketch, "E2358", {"start": v(-333.64, -25.64) * mm, "end": v(-332.5, -32.4) * mm});
            skLineSegment(sketch, "E2359", {"start": v(-332.5, -32.4) * mm, "end": v(-330.92, -38.64) * mm});
            skLineSegment(sketch, "E2360", {"start": v(-330.92, -38.64) * mm, "end": v(-328.86, -44.37) * mm});
            skLineSegment(sketch, "E2361", {"start": v(-328.86, -44.37) * mm, "end": v(-326.34, -49.6) * mm});
            skLineSegment(sketch, "E2362", {"start": v(-326.34, -49.6) * mm, "end": v(-323.36, -54.34) * mm});
            skLineSegment(sketch, "E2363", {"start": v(-323.36, -54.34) * mm, "end": v(-320.82, -57.58) * mm});
            skLineSegment(sketch, "E2364", {"start": v(-320.82, -57.58) * mm, "end": v(-319.9, -58.6) * mm});
            skLineSegment(sketch, "E2365", {"start": v(-319.9, -58.6) * mm, "end": v(-318.96, -59.61) * mm});
            skLineSegment(sketch, "E2366", {"start": v(-318.96, -59.61) * mm, "end": v(-315.9, -62.44) * mm});
            skLineSegment(sketch, "E2367", {"start": v(-315.9, -62.44) * mm, "end": v(-311.44, -65.76) * mm});
            skLineSegment(sketch, "E2368", {"start": v(-311.44, -65.76) * mm, "end": v(-306.52, -68.55) * mm});
            skLineSegment(sketch, "E2369", {"start": v(-306.52, -68.55) * mm, "end": v(-301.12, -70.84) * mm});
            skLineSegment(sketch, "E2370", {"start": v(-301.12, -70.84) * mm, "end": v(-295.24, -72.6) * mm});
            skLineSegment(sketch, "E2371", {"start": v(-295.24, -72.6) * mm, "end": v(-288.87, -73.87) * mm});
            skLineSegment(sketch, "E2372", {"start": v(-288.87, -73.87) * mm, "end": v(-282, -74.62) * mm});
            skLineSegment(sketch, "E2373", {"start": v(-282, -74.62) * mm, "end": v(-276.45, -74.87) * mm});
            skLineSegment(sketch, "E2374", {"start": v(-276.45, -74.87) * mm, "end": v(-274.6, -74.87) * mm});
            skLineSegment(sketch, "E2375", {"start": v(-274.6, -74.87) * mm, "end": v(-273.74, -74.87) * mm});
            skLineSegment(sketch, "E2376", {"start": v(-273.74, -74.87) * mm, "end": v(-271.17, -74.8) * mm});
            skLineSegment(sketch, "E2377", {"start": v(-271.17, -74.8) * mm, "end": v(-267.56, -74.55) * mm});
            skLineSegment(sketch, "E2378", {"start": v(-267.56, -74.55) * mm, "end": v(-263.78, -74.1) * mm});
            skLineSegment(sketch, "E2379", {"start": v(-263.78, -74.1) * mm, "end": v(-259.85, -73.44) * mm});
            skLineSegment(sketch, "E2380", {"start": v(-259.85, -73.44) * mm, "end": v(-255.78, -72.52) * mm});
            skLineSegment(sketch, "E2381", {"start": v(-255.78, -72.52) * mm, "end": v(-251.6, -71.34) * mm});
            skLineSegment(sketch, "E2382", {"start": v(-251.6, -71.34) * mm, "end": v(-247.3, -69.86) * mm});
            skLineSegment(sketch, "E2383", {"start": v(-247.3, -69.86) * mm, "end": v(-242.92, -68.06) * mm});
            skLineSegment(sketch, "E2384", {"start": v(-242.92, -68.06) * mm, "end": v(-238.46, -65.92) * mm});
            skLineSegment(sketch, "E2385", {"start": v(-238.46, -65.92) * mm, "end": v(-233.95, -63.4) * mm});
            skLineSegment(sketch, "E2386", {"start": v(-233.95, -63.4) * mm, "end": v(-229.39, -60.48) * mm});
            skLineSegment(sketch, "E2387", {"start": v(-229.39, -60.48) * mm, "end": v(-224.8, -57.14) * mm});
            skLineSegment(sketch, "E2388", {"start": v(-224.8, -57.14) * mm, "end": v(-220.2, -53.35) * mm});
            skLineSegment(sketch, "E2389", {"start": v(-220.2, -53.35) * mm, "end": v(-215.6, -49.1) * mm});
            skLineSegment(sketch, "E2390", {"start": v(-215.6, -49.1) * mm, "end": v(-211.02, -44.33) * mm});
            skLineSegment(sketch, "E2391", {"start": v(-211.02, -44.33) * mm, "end": v(-207.58, -40.4) * mm});
            skLineSegment(sketch, "E2392", {"start": v(-207.58, -40.4) * mm, "end": v(-206.48, -39.05) * mm});
            skLineSegment(sketch, "E2393", {"start": v(-206.48, -39.05) * mm, "end": v(-204.34, -36.43) * mm});
            skLineSegment(sketch, "E2394", {"start": v(-204.34, -36.43) * mm, "end": v(-204.34, 75.46) * mm});
            skLineSegment(sketch, "E2395", {"start": v(-204.34, 75.46) * mm, "end": v(-248.27, 70.13) * mm});
            skLineSegment(sketch, "E2396", {"start": v(-131.48, -105.5) * mm, "end": v(-133.93, -105.5) * mm});
            skLineSegment(sketch, "E2397", {"start": v(-133.93, -105.5) * mm, "end": v(-141.3, -105.1) * mm});
            skLineSegment(sketch, "E2398", {"start": v(-141.3, -105.1) * mm, "end": v(-150.48, -103.92) * mm});
            skLineSegment(sketch, "E2399", {"start": v(-150.48, -103.92) * mm, "end": v(-158.99, -101.97) * mm});
            skLineSegment(sketch, "E2400", {"start": v(-158.99, -101.97) * mm, "end": v(-164.9, -100.03) * mm});
            skLineSegment(sketch, "E2401", {"start": v(-164.9, -100.03) * mm, "end": v(-166.8, -99.23) * mm});
            skLineSegment(sketch, "E2402", {"start": v(-166.8, -99.23) * mm, "end": v(-169.01, -98.32) * mm});
            skLineSegment(sketch, "E2403", {"start": v(-169.01, -98.32) * mm, "end": v(-175.35, -94.85) * mm});
            skLineSegment(sketch, "E2404", {"start": v(-175.35, -94.85) * mm, "end": v(-182.8, -89.3) * mm});
            skLineSegment(sketch, "E2405", {"start": v(-182.8, -89.3) * mm, "end": v(-189.12, -82.6) * mm});
            skLineSegment(sketch, "E2406", {"start": v(-189.12, -82.6) * mm, "end": v(-193.17, -76.82) * mm});
            skLineSegment(sketch, "E2407", {"start": v(-193.17, -76.82) * mm, "end": v(-194.3, -74.77) * mm});
            skLineSegment(sketch, "E2408", {"start": v(-194.3, -74.77) * mm, "end": v(-199.93, -64.49) * mm});
            skLineSegment(sketch, "E2409", {"start": v(-199.93, -64.49) * mm, "end": v(-208.84, -72.11) * mm});
            skLineSegment(sketch, "E2410", {"start": v(-208.84, -72.11) * mm, "end": v(-211.24, -74.17) * mm});
            skLineSegment(sketch, "E2411", {"start": v(-211.24, -74.17) * mm, "end": v(-218.79, -79.9) * mm});
            skLineSegment(sketch, "E2412", {"start": v(-218.79, -79.9) * mm, "end": v(-229.2, -86.67) * mm});
            skLineSegment(sketch, "E2413", {"start": v(-229.2, -86.67) * mm, "end": v(-240.1, -92.4) * mm});
            skLineSegment(sketch, "E2414", {"start": v(-240.1, -92.4) * mm, "end": v(-251.44, -97.1) * mm});
            skLineSegment(sketch, "E2415", {"start": v(-251.44, -97.1) * mm, "end": v(-263.23, -100.77) * mm});
            skLineSegment(sketch, "E2416", {"start": v(-263.23, -100.77) * mm, "end": v(-275.45, -103.4) * mm});
            skLineSegment(sketch, "E2417", {"start": v(-275.45, -103.4) * mm, "end": v(-288.1, -104.97) * mm});
            skLineSegment(sketch, "E2418", {"start": v(-288.1, -104.97) * mm, "end": v(-297.9, -105.5) * mm});
            skLineSegment(sketch, "E2419", {"start": v(-297.9, -105.5) * mm, "end": v(-301.16, -105.5) * mm});
            skLineSegment(sketch, "E2420", {"start": v(-301.16, -105.5) * mm, "end": v(-304.33, -105.5) * mm});
            skLineSegment(sketch, "E2421", {"start": v(-304.33, -105.5) * mm, "end": v(-313.86, -105.1) * mm});
            skLineSegment(sketch, "E2422", {"start": v(-313.86, -105.1) * mm, "end": v(-325.93, -103.96) * mm});
            skLineSegment(sketch, "E2423", {"start": v(-325.93, -103.96) * mm, "end": v(-337.35, -102.06) * mm});
            skLineSegment(sketch, "E2424", {"start": v(-337.35, -102.06) * mm, "end": v(-348.07, -99.43) * mm});
            skLineSegment(sketch, "E2425", {"start": v(-348.07, -99.43) * mm, "end": v(-358.06, -96.06) * mm});
            skLineSegment(sketch, "E2426", {"start": v(-358.06, -96.06) * mm, "end": v(-367.3, -91.97) * mm});
            skLineSegment(sketch, "E2427", {"start": v(-367.3, -91.97) * mm, "end": v(-375.72, -87.18) * mm});
            skLineSegment(sketch, "E2428", {"start": v(-375.72, -87.18) * mm, "end": v(-381.5, -83.16) * mm});
            skLineSegment(sketch, "E2429", {"start": v(-381.5, -83.16) * mm, "end": v(-383.32, -81.68) * mm});
            skLineSegment(sketch, "E2430", {"start": v(-383.32, -81.68) * mm, "end": v(-385.01, -80.3) * mm});
            skLineSegment(sketch, "E2431", {"start": v(-385.01, -80.3) * mm, "end": v(-389.8, -75.76) * mm});
            skLineSegment(sketch, "E2432", {"start": v(-389.8, -75.76) * mm, "end": v(-395.46, -69.22) * mm});
            skLineSegment(sketch, "E2433", {"start": v(-395.46, -69.22) * mm, "end": v(-400.29, -62.1) * mm});
            skLineSegment(sketch, "E2434", {"start": v(-400.29, -62.1) * mm, "end": v(-403.4, -56.38) * mm});
            skLineSegment(sketch, "E2435", {"start": v(-403.4, -56.38) * mm, "end": v(-404.27, -54.4) * mm});
            skLineSegment(sketch, "E2436", {"start": v(-404.27, -54.4) * mm, "end": v(-405.2, -52.33) * mm});
            skLineSegment(sketch, "E2437", {"start": v(-405.2, -52.33) * mm, "end": v(-407.48, -45.91) * mm});
            skLineSegment(sketch, "E2438", {"start": v(-407.48, -45.91) * mm, "end": v(-409.79, -36.84) * mm});
            skLineSegment(sketch, "E2439", {"start": v(-409.79, -36.84) * mm, "end": v(-411.17, -27.24) * mm});
            skLineSegment(sketch, "E2440", {"start": v(-411.17, -27.24) * mm, "end": v(-411.63, -19.66) * mm});
            skLineSegment(sketch, "E2441", {"start": v(-411.63, -19.66) * mm, "end": v(-411.63, -17.14) * mm});
            skLineSegment(sketch, "E2442", {"start": v(-411.63, -17.14) * mm, "end": v(-411.63, -14.16) * mm});
            skLineSegment(sketch, "E2443", {"start": v(-411.63, -14.16) * mm, "end": v(-411.1, -5.21) * mm});
            skLineSegment(sketch, "E2444", {"start": v(-411.1, -5.21) * mm, "end": v(-409.47, 5.85) * mm});
            skLineSegment(sketch, "E2445", {"start": v(-409.47, 5.85) * mm, "end": v(-406.74, 16.1) * mm});
            skLineSegment(sketch, "E2446", {"start": v(-406.74, 16.1) * mm, "end": v(-402.88, 25.56) * mm});
            skLineSegment(sketch, "E2447", {"start": v(-402.88, 25.56) * mm, "end": v(-397.87, 34.27) * mm});
            skLineSegment(sketch, "E2448", {"start": v(-397.87, 34.27) * mm, "end": v(-391.7, 42.3) * mm});
            skLineSegment(sketch, "E2449", {"start": v(-391.7, 42.3) * mm, "end": v(-384.34, 49.65) * mm});
            skLineSegment(sketch, "E2450", {"start": v(-384.34, 49.65) * mm, "end": v(-378, 54.82) * mm});
            skLineSegment(sketch, "E2451", {"start": v(-378, 54.82) * mm, "end": v(-375.78, 56.39) * mm});
            skLineSegment(sketch, "E2452", {"start": v(-375.78, 56.39) * mm, "end": v(-373.28, 58.14) * mm});
            skLineSegment(sketch, "E2453", {"start": v(-373.28, 58.14) * mm, "end": v(-365.43, 62.87) * mm});
            skLineSegment(sketch, "E2454", {"start": v(-365.43, 62.87) * mm, "end": v(-353.66, 68.77) * mm});
            skLineSegment(sketch, "E2455", {"start": v(-353.66, 68.77) * mm, "end": v(-340.4, 74.11) * mm});
            skLineSegment(sketch, "E2456", {"start": v(-340.4, 74.11) * mm, "end": v(-329.3, 77.84) * mm});
            skLineSegment(sketch, "E2457", {"start": v(-329.3, 77.84) * mm, "end": v(-325.56, 78.94) * mm});
            skLineSegment(sketch, "E2458", {"start": v(-325.56, 78.94) * mm, "end": v(-321.47, 80.14) * mm});
            skLineSegment(sketch, "E2459", {"start": v(-321.47, 80.14) * mm, "end": v(-309.05, 83.28) * mm});
            skLineSegment(sketch, "E2460", {"start": v(-309.05, 83.28) * mm, "end": v(-290.92, 87.1) * mm});
            skLineSegment(sketch, "E2461", {"start": v(-290.92, 87.1) * mm, "end": v(-271.05, 90.44) * mm});
            skLineSegment(sketch, "E2462", {"start": v(-271.05, 90.44) * mm, "end": v(-254.73, 92.68) * mm});
            skLineSegment(sketch, "E2463", {"start": v(-254.73, 92.68) * mm, "end": v(-249.27, 93.31) * mm});
            skLineSegment(sketch, "E2464", {"start": v(-249.27, 93.31) * mm, "end": v(-204.34, 98.76) * mm});
            skLineSegment(sketch, "E2465", {"start": v(-204.34, 98.76) * mm, "end": v(-204.34, 137.06) * mm});
            skLineSegment(sketch, "E2466", {"start": v(-204.34, 137.06) * mm, "end": v(-204.34, 140.67) * mm});
            skLineSegment(sketch, "E2467", {"start": v(-204.34, 140.67) * mm, "end": v(-204.6, 151.5) * mm});
            skLineSegment(sketch, "E2468", {"start": v(-204.6, 151.5) * mm, "end": v(-205.4, 164.47) * mm});
            skLineSegment(sketch, "E2469", {"start": v(-205.4, 164.47) * mm, "end": v(-206.7, 176.07) * mm});
            skLineSegment(sketch, "E2470", {"start": v(-206.7, 176.07) * mm, "end": v(-208.52, 186.35) * mm});
            skLineSegment(sketch, "E2471", {"start": v(-208.52, 186.35) * mm, "end": v(-210.83, 195.4) * mm});
            skLineSegment(sketch, "E2472", {"start": v(-210.83, 195.4) * mm, "end": v(-213.62, 203.28) * mm});
            skLineSegment(sketch, "E2473", {"start": v(-213.62, 203.28) * mm, "end": v(-216.9, 210.07) * mm});
            skLineSegment(sketch, "E2474", {"start": v(-216.9, 210.07) * mm, "end": v(-220.66, 215.84) * mm});
            skLineSegment(sketch, "E2475", {"start": v(-220.66, 215.84) * mm, "end": v(-224.86, 220.66) * mm});
            skLineSegment(sketch, "E2476", {"start": v(-224.86, 220.66) * mm, "end": v(-229.53, 224.6) * mm});
            skLineSegment(sketch, "E2477", {"start": v(-229.53, 224.6) * mm, "end": v(-234.63, 227.74) * mm});
            skLineSegment(sketch, "E2478", {"start": v(-234.63, 227.74) * mm, "end": v(-240.17, 230.14) * mm});
            skLineSegment(sketch, "E2479", {"start": v(-240.17, 230.14) * mm, "end": v(-246.14, 231.89) * mm});
            skLineSegment(sketch, "E2480", {"start": v(-246.14, 231.89) * mm, "end": v(-252.52, 233.05) * mm});
            skLineSegment(sketch, "E2481", {"start": v(-252.52, 233.05) * mm, "end": v(-259.3, 233.69) * mm});
            skLineSegment(sketch, "E2482", {"start": v(-259.3, 233.69) * mm, "end": v(-264.7, 233.89) * mm});
            skLineSegment(sketch, "E2483", {"start": v(-264.7, 233.89) * mm, "end": v(-266.49, 233.89) * mm});
            skLineSegment(sketch, "E2484", {"start": v(-266.49, 233.89) * mm, "end": v(-269.4, 233.89) * mm});
            skLineSegment(sketch, "E2485", {"start": v(-269.4, 233.89) * mm, "end": v(-278.1, 233.38) * mm});
            skLineSegment(sketch, "E2486", {"start": v(-278.1, 233.38) * mm, "end": v(-288.8, 231.9) * mm});
            skLineSegment(sketch, "E2487", {"start": v(-288.8, 231.9) * mm, "end": v(-298.5, 229.44) * mm});
            skLineSegment(sketch, "E2488", {"start": v(-298.5, 229.44) * mm, "end": v(-304.95, 227.06) * mm});
            skLineSegment(sketch, "E2489", {"start": v(-304.95, 227.06) * mm, "end": v(-307, 226.05) * mm});
            skLineSegment(sketch, "E2490", {"start": v(-307, 226.05) * mm, "end": v(-308.47, 225.34) * mm});
            skLineSegment(sketch, "E2491", {"start": v(-308.47, 225.34) * mm, "end": v(-312.69, 222.81) * mm});
            skLineSegment(sketch, "E2492", {"start": v(-312.69, 222.81) * mm, "end": v(-317.17, 219.35) * mm});
            skLineSegment(sketch, "E2493", {"start": v(-317.17, 219.35) * mm, "end": v(-320.58, 215.77) * mm});
            skLineSegment(sketch, "E2494", {"start": v(-320.58, 215.77) * mm, "end": v(-323.05, 212.17) * mm});
            skLineSegment(sketch, "E2495", {"start": v(-323.05, 212.17) * mm, "end": v(-324.74, 208.67) * mm});
            skLineSegment(sketch, "E2496", {"start": v(-324.74, 208.67) * mm, "end": v(-325.77, 205.37) * mm});
            skLineSegment(sketch, "E2497", {"start": v(-325.77, 205.37) * mm, "end": v(-326.29, 202.36) * mm});
            skLineSegment(sketch, "E2498", {"start": v(-326.29, 202.36) * mm, "end": v(-326.43, 200.42) * mm});
            skLineSegment(sketch, "E2499", {"start": v(-326.43, 200.42) * mm, "end": v(-326.43, 199.77) * mm});
            skLineSegment(sketch, "E2500", {"start": v(-326.43, 199.77) * mm, "end": v(-326.43, 198.36) * mm});
            skLineSegment(sketch, "E2501", {"start": v(-326.43, 198.36) * mm, "end": v(-325.67, 194.13) * mm});
            skLineSegment(sketch, "E2502", {"start": v(-325.67, 194.13) * mm, "end": v(-323.62, 189.16) * mm});
            skLineSegment(sketch, "E2503", {"start": v(-323.62, 189.16) * mm, "end": v(-320.62, 184.53) * mm});
            skLineSegment(sketch, "E2504", {"start": v(-320.62, 184.53) * mm, "end": v(-317.94, 181.05) * mm});
            skLineSegment(sketch, "E2505", {"start": v(-317.94, 181.05) * mm, "end": v(-317.02, 179.91) * mm});
            skLineSegment(sketch, "E2506", {"start": v(-317.02, 179.91) * mm, "end": v(-316.52, 179.28) * mm});
            skLineSegment(sketch, "E2507", {"start": v(-316.52, 179.28) * mm, "end": v(-315.02, 177.4) * mm});
            skLineSegment(sketch, "E2508", {"start": v(-315.02, 177.4) * mm, "end": v(-313.04, 174.75) * mm});
            skLineSegment(sketch, "E2509", {"start": v(-313.04, 174.75) * mm, "end": v(-311.14, 171.98) * mm});
            skLineSegment(sketch, "E2510", {"start": v(-311.14, 171.98) * mm, "end": v(-309.41, 169.02) * mm});
            skLineSegment(sketch, "E2511", {"start": v(-309.41, 169.02) * mm, "end": v(-307.93, 165.85) * mm});
            skLineSegment(sketch, "E2512", {"start": v(-307.93, 165.85) * mm, "end": v(-306.78, 162.44) * mm});
            skLineSegment(sketch, "E2513", {"start": v(-306.78, 162.44) * mm, "end": v(-306.03, 158.75) * mm});
            skLineSegment(sketch, "E2514", {"start": v(-306.03, 158.75) * mm, "end": v(-305.76, 155.76) * mm});
            skLineSegment(sketch, "E2515", {"start": v(-305.76, 155.76) * mm, "end": v(-305.76, 154.76) * mm});
            skLineSegment(sketch, "E2516", {"start": v(-305.76, 154.76) * mm, "end": v(-305.76, 152.61) * mm});
            skLineSegment(sketch, "E2517", {"start": v(-305.76, 152.61) * mm, "end": v(-306.56, 146.17) * mm});
            skLineSegment(sketch, "E2518", {"start": v(-306.56, 146.17) * mm, "end": v(-308.92, 138.18) * mm});
            skLineSegment(sketch, "E2519", {"start": v(-308.92, 138.18) * mm, "end": v(-312.75, 130.99) * mm});
            skLineSegment(sketch, "E2520", {"start": v(-312.75, 130.99) * mm, "end": v(-316.53, 126.17) * mm});
            skLineSegment(sketch, "E2521", {"start": v(-316.53, 126.17) * mm, "end": v(-317.99, 124.77) * mm});
            skLineSegment(sketch, "E2522", {"start": v(-317.99, 124.77) * mm, "end": v(-318.73, 124.05) * mm});
            skLineSegment(sketch, "E2523", {"start": v(-318.73, 124.05) * mm, "end": v(-321.13, 122.06) * mm});
            skLineSegment(sketch, "E2524", {"start": v(-321.13, 122.06) * mm, "end": v(-324.57, 119.68) * mm});
            skLineSegment(sketch, "E2525", {"start": v(-324.57, 119.68) * mm, "end": v(-328.27, 117.65) * mm});
            skLineSegment(sketch, "E2526", {"start": v(-328.27, 117.65) * mm, "end": v(-332.2, 115.95) * mm});
            skLineSegment(sketch, "E2527", {"start": v(-332.2, 115.95) * mm, "end": v(-336.36, 114.63) * mm});
            skLineSegment(sketch, "E2528", {"start": v(-336.36, 114.63) * mm, "end": v(-340.7, 113.67) * mm});
            skLineSegment(sketch, "E2529", {"start": v(-340.7, 113.67) * mm, "end": v(-345.2, 113.09) * mm});
            skLineSegment(sketch, "E2530", {"start": v(-345.2, 113.09) * mm, "end": v(-348.69, 112.89) * mm});
            skLineSegment(sketch, "E2531", {"start": v(-348.69, 112.89) * mm, "end": v(-349.85, 112.89) * mm});
            skLineSegment(sketch, "E2532", {"start": v(-349.85, 112.89) * mm, "end": v(-350.97, 112.89) * mm});
            skLineSegment(sketch, "E2533", {"start": v(-350.97, 112.89) * mm, "end": v(-354.33, 113.11) * mm});
            skLineSegment(sketch, "E2534", {"start": v(-354.33, 113.11) * mm, "end": v(-358.7, 113.78) * mm});
            skLineSegment(sketch, "E2535", {"start": v(-358.7, 113.78) * mm, "end": v(-362.93, 114.87) * mm});
            skLineSegment(sketch, "E2536", {"start": v(-362.93, 114.87) * mm, "end": v(-366.99, 116.39) * mm});
            skLineSegment(sketch, "E2537", {"start": v(-366.99, 116.39) * mm, "end": v(-370.86, 118.31) * mm});
            skLineSegment(sketch, "E2538", {"start": v(-370.86, 118.31) * mm, "end": v(-374.53, 120.63) * mm});
            skLineSegment(sketch, "E2539", {"start": v(-374.53, 120.63) * mm, "end": v(-377.95, 123.35) * mm});
            skLineSegment(sketch, "E2540", {"start": v(-377.95, 123.35) * mm, "end": v(-380.37, 125.62) * mm});
            skLineSegment(sketch, "E2541", {"start": v(-380.37, 125.62) * mm, "end": v(-381.11, 126.44) * mm});
            skLineSegment(sketch, "E2542", {"start": v(-381.11, 126.44) * mm, "end": v(-381.89, 127.27) * mm});
            skLineSegment(sketch, "E2543", {"start": v(-381.89, 127.27) * mm, "end": v(-384.04, 129.95) * mm});
            skLineSegment(sketch, "E2544", {"start": v(-384.04, 129.95) * mm, "end": v(-386.6, 133.76) * mm});
            skLineSegment(sketch, "E2545", {"start": v(-386.6, 133.76) * mm, "end": v(-388.8, 137.84) * mm});
            skLineSegment(sketch, "E2546", {"start": v(-388.8, 137.84) * mm, "end": v(-390.62, 142.17) * mm});
            skLineSegment(sketch, "E2547", {"start": v(-390.62, 142.17) * mm, "end": v(-392.05, 146.72) * mm});
            skLineSegment(sketch, "E2548", {"start": v(-392.05, 146.72) * mm, "end": v(-393.09, 151.46) * mm});
            skLineSegment(sketch, "E2549", {"start": v(-393.09, 151.46) * mm, "end": v(-393.72, 156.36) * mm});
            skLineSegment(sketch, "E2550", {"start": v(-393.72, 156.36) * mm, "end": v(-393.92, 160.14) * mm});
            skLineSegment(sketch, "E2551", {"start": v(-393.92, 160.14) * mm, "end": v(-393.92, 161.4) * mm});
            skLineSegment(sketch, "E2552", {"start": v(-393.92, 161.4) * mm, "end": v(-393.92, 163.83) * mm});
            skLineSegment(sketch, "E2553", {"start": v(-393.92, 163.83) * mm, "end": v(-393.33, 171.13) * mm});
            skLineSegment(sketch, "E2554", {"start": v(-393.33, 171.13) * mm, "end": v(-391.57, 180.6) * mm});
            skLineSegment(sketch, "E2555", {"start": v(-391.57, 180.6) * mm, "end": v(-388.67, 189.76) * mm});
            skLineSegment(sketch, "E2556", {"start": v(-388.67, 189.76) * mm, "end": v(-384.66, 198.56) * mm});
            skLineSegment(sketch, "E2557", {"start": v(-384.66, 198.56) * mm, "end": v(-379.56, 206.94) * mm});
            skLineSegment(sketch, "E2558", {"start": v(-379.56, 206.94) * mm, "end": v(-373.4, 214.85) * mm});
            skLineSegment(sketch, "E2559", {"start": v(-373.4, 214.85) * mm, "end": v(-366.2, 222.25) * mm});
            skLineSegment(sketch, "E2560", {"start": v(-366.2, 222.25) * mm, "end": v(-360.15, 227.48) * mm});
            skLineSegment(sketch, "E2561", {"start": v(-360.15, 227.48) * mm, "end": v(-358.02, 229.07) * mm});
            skLineSegment(sketch, "E2562", {"start": v(-358.02, 229.07) * mm, "end": v(-355.71, 230.8) * mm});
            skLineSegment(sketch, "E2563", {"start": v(-355.71, 230.8) * mm, "end": v(-348.42, 235.55) * mm});
            skLineSegment(sketch, "E2564", {"start": v(-348.42, 235.55) * mm, "end": v(-337.97, 241.2) * mm});
            skLineSegment(sketch, "E2565", {"start": v(-337.97, 241.2) * mm, "end": v(-326.71, 246.01) * mm});
            skLineSegment(sketch, "E2566", {"start": v(-326.71, 246.01) * mm, "end": v(-314.7, 249.98) * mm});
            skLineSegment(sketch, "E2567", {"start": v(-314.7, 249.98) * mm, "end": v(-301.96, 253.1) * mm});
            skLineSegment(sketch, "E2568", {"start": v(-301.96, 253.1) * mm, "end": v(-288.54, 255.32) * mm});
            skLineSegment(sketch, "E2569", {"start": v(-288.54, 255.32) * mm, "end": v(-274.49, 256.68) * mm});
            skLineSegment(sketch, "E2570", {"start": v(-274.49, 256.68) * mm, "end": v(-263.51, 257.13) * mm});
            skLineSegment(sketch, "E2571", {"start": v(-263.51, 257.13) * mm, "end": v(-259.85, 257.13) * mm});
            skLineSegment(sketch, "E2572", {"start": v(-259.85, 257.13) * mm, "end": v(-255.5, 257.13) * mm});
            skLineSegment(sketch, "E2573", {"start": v(-255.5, 257.13) * mm, "end": v(-242.43, 256.68) * mm});
            skLineSegment(sketch, "E2574", {"start": v(-242.43, 256.68) * mm, "end": v(-226.45, 255.33) * mm});
            skLineSegment(sketch, "E2575", {"start": v(-226.45, 255.33) * mm, "end": v(-211.84, 253.05) * mm});
            skLineSegment(sketch, "E2576", {"start": v(-211.84, 253.05) * mm, "end": v(-198.56, 249.84) * mm});
            skLineSegment(sketch, "E2577", {"start": v(-198.56, 249.84) * mm, "end": v(-186.54, 245.67) * mm});
            skLineSegment(sketch, "E2578", {"start": v(-186.54, 245.67) * mm, "end": v(-175.73, 240.53) * mm});
            skLineSegment(sketch, "E2579", {"start": v(-175.73, 240.53) * mm, "end": v(-166.07, 234.4) * mm});
            skLineSegment(sketch, "E2580", {"start": v(-166.07, 234.4) * mm, "end": v(-159.52, 229.19) * mm});
            skLineSegment(sketch, "E2581", {"start": v(-159.52, 229.19) * mm, "end": v(-157.5, 227.27) * mm});
            skLineSegment(sketch, "E2582", {"start": v(-157.5, 227.27) * mm, "end": v(-155.53, 225.4) * mm});
            skLineSegment(sketch, "E2583", {"start": v(-155.53, 225.4) * mm, "end": v(-150.1, 219.25) * mm});
            skLineSegment(sketch, "E2584", {"start": v(-150.1, 219.25) * mm, "end": v(-143.73, 210.2) * mm});
            skLineSegment(sketch, "E2585", {"start": v(-143.73, 210.2) * mm, "end": v(-138.4, 200.1) * mm});
            skLineSegment(sketch, "E2586", {"start": v(-138.4, 200.1) * mm, "end": v(-134.07, 188.9) * mm});
            skLineSegment(sketch, "E2587", {"start": v(-134.07, 188.9) * mm, "end": v(-130.73, 176.52) * mm});
            skLineSegment(sketch, "E2588", {"start": v(-130.73, 176.52) * mm, "end": v(-128.36, 162.93) * mm});
            skLineSegment(sketch, "E2589", {"start": v(-128.36, 162.93) * mm, "end": v(-126.96, 148.07) * mm});
            skLineSegment(sketch, "E2590", {"start": v(-126.96, 148.07) * mm, "end": v(-126.5, 135.93) * mm});
            skLineSegment(sketch, "E2591", {"start": v(-126.5, 135.93) * mm, "end": v(-126.5, 131.89) * mm});
            skLineSegment(sketch, "E2592", {"start": v(-126.5, 131.89) * mm, "end": v(-126.5, -36.32) * mm});
            skLineSegment(sketch, "E2593", {"start": v(-126.5, -36.32) * mm, "end": v(-126.5, -38.56) * mm});
            skLineSegment(sketch, "E2594", {"start": v(-126.5, -38.56) * mm, "end": v(-126.17, -45.3) * mm});
            skLineSegment(sketch, "E2595", {"start": v(-126.17, -45.3) * mm, "end": v(-125.18, -52.94) * mm});
            skLineSegment(sketch, "E2596", {"start": v(-125.18, -52.94) * mm, "end": v(-123.53, -59.3) * mm});
            skLineSegment(sketch, "E2597", {"start": v(-123.53, -59.3) * mm, "end": v(-121.9, -63.2) * mm});
            skLineSegment(sketch, "E2598", {"start": v(-121.9, -63.2) * mm, "end": v(-121.2, -64.4) * mm});
            skLineSegment(sketch, "E2599", {"start": v(-121.2, -64.4) * mm, "end": v(-120.99, -64.75) * mm});
            skLineSegment(sketch, "E2600", {"start": v(-120.99, -64.75) * mm, "end": v(-120.31, -65.77) * mm});
            skLineSegment(sketch, "E2601", {"start": v(-120.31, -65.77) * mm, "end": v(-119.22, -67.18) * mm});
            skLineSegment(sketch, "E2602", {"start": v(-119.22, -67.18) * mm, "end": v(-117.87, -68.56) * mm});
            skLineSegment(sketch, "E2603", {"start": v(-117.87, -68.56) * mm, "end": v(-116.21, -69.85) * mm});
            skLineSegment(sketch, "E2604", {"start": v(-116.21, -69.85) * mm, "end": v(-114.2, -70.97) * mm});
            skLineSegment(sketch, "E2605", {"start": v(-114.2, -70.97) * mm, "end": v(-111.82, -71.86) * mm});
            skLineSegment(sketch, "E2606", {"start": v(-111.82, -71.86) * mm, "end": v(-108.98, -72.44) * mm});
            skLineSegment(sketch, "E2607", {"start": v(-108.98, -72.44) * mm, "end": v(-106.5, -72.65) * mm});
            skLineSegment(sketch, "E2608", {"start": v(-106.5, -72.65) * mm, "end": v(-105.67, -72.65) * mm});
            skLineSegment(sketch, "E2609", {"start": v(-105.67, -72.65) * mm, "end": v(-104.5, -72.65) * mm});
            skLineSegment(sketch, "E2610", {"start": v(-104.5, -72.65) * mm, "end": v(-100.97, -72.22) * mm});
            skLineSegment(sketch, "E2611", {"start": v(-100.97, -72.22) * mm, "end": v(-96.64, -70.91) * mm});
            skLineSegment(sketch, "E2612", {"start": v(-96.64, -70.91) * mm, "end": v(-92.67, -68.7) * mm});
            skLineSegment(sketch, "E2613", {"start": v(-92.67, -68.7) * mm, "end": v(-89.03, -65.55) * mm});
            skLineSegment(sketch, "E2614", {"start": v(-89.03, -65.55) * mm, "end": v(-85.69, -61.44) * mm});
            skLineSegment(sketch, "E2615", {"start": v(-85.69, -61.44) * mm, "end": v(-82.63, -56.36) * mm});
            skLineSegment(sketch, "E2616", {"start": v(-82.63, -56.36) * mm, "end": v(-79.82, -50.26) * mm});
            skLineSegment(sketch, "E2617", {"start": v(-79.82, -50.26) * mm, "end": v(-77.83, -44.94) * mm});
            skLineSegment(sketch, "E2618", {"start": v(-77.83, -44.94) * mm, "end": v(-77.24, -43.14) * mm});
            skLineSegment(sketch, "E2619", {"start": v(-77.24, -43.14) * mm, "end": v(-75.95, -39.13) * mm});
            skLineSegment(sketch, "E2620", {"start": v(-75.95, -39.13) * mm, "end": v(-53.73, -46.13) * mm});
            skLineSegment(sketch, "E2621", {"start": v(-53.73, -46.13) * mm, "end": v(-55.18, -50.26) * mm});
            skLineSegment(sketch, "E2622", {"start": v(-55.18, -50.26) * mm, "end": v(-55.95, -52.46) * mm});
            skLineSegment(sketch, "E2623", {"start": v(-55.95, -52.46) * mm, "end": v(-58.58, -58.95) * mm});
            skLineSegment(sketch, "E2624", {"start": v(-58.58, -58.95) * mm, "end": v(-62.3, -66.7) * mm});
            skLineSegment(sketch, "E2625", {"start": v(-62.3, -66.7) * mm, "end": v(-66.32, -73.54) * mm});
            skLineSegment(sketch, "E2626", {"start": v(-66.32, -73.54) * mm, "end": v(-70.62, -79.54) * mm});
            skLineSegment(sketch, "E2627", {"start": v(-70.62, -79.54) * mm, "end": v(-75.14, -84.76) * mm});
            skLineSegment(sketch, "E2628", {"start": v(-75.14, -84.76) * mm, "end": v(-79.88, -89.25) * mm});
            skLineSegment(sketch, "E2629", {"start": v(-79.88, -89.25) * mm, "end": v(-84.78, -93.06) * mm});
            skLineSegment(sketch, "E2630", {"start": v(-84.78, -93.06) * mm, "end": v(-89.83, -96.24) * mm});
            skLineSegment(sketch, "E2631", {"start": v(-89.83, -96.24) * mm, "end": v(-94.98, -98.84) * mm});
            skLineSegment(sketch, "E2632", {"start": v(-94.98, -98.84) * mm, "end": v(-100.22, -100.93) * mm});
            skLineSegment(sketch, "E2633", {"start": v(-100.22, -100.93) * mm, "end": v(-105.5, -102.54) * mm});
            skLineSegment(sketch, "E2634", {"start": v(-105.5, -102.54) * mm, "end": v(-110.8, -103.75) * mm});
            skLineSegment(sketch, "E2635", {"start": v(-110.8, -103.75) * mm, "end": v(-116.07, -104.6) * mm});
            skLineSegment(sketch, "E2636", {"start": v(-116.07, -104.6) * mm, "end": v(-121.3, -105.13) * mm});
            skLineSegment(sketch, "E2637", {"start": v(-121.3, -105.13) * mm, "end": v(-126.45, -105.4) * mm});
            skLineSegment(sketch, "E2638", {"start": v(-126.45, -105.4) * mm, "end": v(-130.22, -105.5) * mm});
            skLineSegment(sketch, "E2639", {"start": v(-130.22, -105.5) * mm, "end": v(-131.48, -105.5) * mm});
            skLineSegment(sketch, "E2640", {"start": v(247.66, -105.5) * mm, "end": v(244.72, -105.5) * mm});
            skLineSegment(sketch, "E2641", {"start": v(244.72, -105.5) * mm, "end": v(235.93, -105.1) * mm});
            skLineSegment(sketch, "E2642", {"start": v(235.93, -105.1) * mm, "end": v(224.96, -103.91) * mm});
            skLineSegment(sketch, "E2643", {"start": v(224.96, -103.91) * mm, "end": v(214.72, -101.95) * mm});
            skLineSegment(sketch, "E2644", {"start": v(214.72, -101.95) * mm, "end": v(205.25, -99.19) * mm});
            skLineSegment(sketch, "E2645", {"start": v(205.25, -99.19) * mm, "end": v(196.53, -95.65) * mm});
            skLineSegment(sketch, "E2646", {"start": v(196.53, -95.65) * mm, "end": v(188.56, -91.33) * mm});
            skLineSegment(sketch, "E2647", {"start": v(188.56, -91.33) * mm, "end": v(181.34, -86.22) * mm});
            skLineSegment(sketch, "E2648", {"start": v(181.34, -86.22) * mm, "end": v(174.87, -80.34) * mm});
            skLineSegment(sketch, "E2649", {"start": v(174.87, -80.34) * mm, "end": v(169.16, -73.67) * mm});
            skLineSegment(sketch, "E2650", {"start": v(169.16, -73.67) * mm, "end": v(164.2, -66.23) * mm});
            skLineSegment(sketch, "E2651", {"start": v(164.2, -66.23) * mm, "end": v(160, -58.02) * mm});
            skLineSegment(sketch, "E2652", {"start": v(160, -58.02) * mm, "end": v(156.58, -49.02) * mm});
            skLineSegment(sketch, "E2653", {"start": v(156.58, -49.02) * mm, "end": v(153.9, -39.26) * mm});
            skLineSegment(sketch, "E2654", {"start": v(153.9, -39.26) * mm, "end": v(151.99, -28.72) * mm});
            skLineSegment(sketch, "E2655", {"start": v(151.99, -28.72) * mm, "end": v(150.84, -17.42) * mm});
            skLineSegment(sketch, "E2656", {"start": v(150.84, -17.42) * mm, "end": v(150.46, -8.36) * mm});
            skLineSegment(sketch, "E2657", {"start": v(150.46, -8.36) * mm, "end": v(150.46, -5.34) * mm});
            skLineSegment(sketch, "E2658", {"start": v(150.46, -5.34) * mm, "end": v(150.46, 226.5) * mm});
            skLineSegment(sketch, "E2659", {"start": v(150.46, 226.5) * mm, "end": v(103.98, 226.5) * mm});
            skLineSegment(sketch, "E2660", {"start": v(103.98, 226.5) * mm, "end": v(103.98, 249.75) * mm});
            skLineSegment(sketch, "E2661", {"start": v(103.98, 249.75) * mm, "end": v(153.31, 249.75) * mm});
            skLineSegment(sketch, "E2662", {"start": v(153.31, 249.75) * mm, "end": v(155.96, 251.96) * mm});
            skLineSegment(sketch, "E2663", {"start": v(155.96, 251.96) * mm, "end": v(158.28, 253.9) * mm});
            skLineSegment(sketch, "E2664", {"start": v(158.28, 253.9) * mm, "end": v(164.9, 260.12) * mm});
            skLineSegment(sketch, "E2665", {"start": v(164.9, 260.12) * mm, "end": v(173.23, 269.19) * mm});
            skLineSegment(sketch, "E2666", {"start": v(173.23, 269.19) * mm, "end": v(180.9, 279.09) * mm});
            skLineSegment(sketch, "E2667", {"start": v(180.9, 279.09) * mm, "end": v(187.9, 289.75) * mm});
            skLineSegment(sketch, "E2668", {"start": v(187.9, 289.75) * mm, "end": v(194.14, 301.13) * mm});
            skLineSegment(sketch, "E2669", {"start": v(194.14, 301.13) * mm, "end": v(199.63, 313.13) * mm});
            skLineSegment(sketch, "E2670", {"start": v(199.63, 313.13) * mm, "end": v(204.3, 325.7) * mm});
            skLineSegment(sketch, "E2671", {"start": v(204.3, 325.7) * mm, "end": v(207.3, 335.47) * mm});
            skLineSegment(sketch, "E2672", {"start": v(207.3, 335.47) * mm, "end": v(208.14, 338.77) * mm});
            skLineSegment(sketch, "E2673", {"start": v(208.14, 338.77) * mm, "end": v(208.96, 341.97) * mm});
            skLineSegment(sketch, "E2674", {"start": v(208.96, 341.97) * mm, "end": v(228.28, 341.97) * mm});
            skLineSegment(sketch, "E2675", {"start": v(228.28, 341.97) * mm, "end": v(228.28, 249.75) * mm});
            skLineSegment(sketch, "E2676", {"start": v(228.28, 249.75) * mm, "end": v(327.88, 249.75) * mm});
            skLineSegment(sketch, "E2677", {"start": v(327.88, 249.75) * mm, "end": v(327.88, 226.5) * mm});
            skLineSegment(sketch, "E2678", {"start": v(327.88, 226.5) * mm, "end": v(228.28, 226.5) * mm});
            skLineSegment(sketch, "E2679", {"start": v(228.28, 226.5) * mm, "end": v(228.28, -14.93) * mm});
            skLineSegment(sketch, "E2680", {"start": v(228.28, -14.93) * mm, "end": v(228.28, -17.15) * mm});
            skLineSegment(sketch, "E2681", {"start": v(228.28, -17.15) * mm, "end": v(228.41, -23.84) * mm});
            skLineSegment(sketch, "E2682", {"start": v(228.41, -23.84) * mm, "end": v(228.82, -31.9) * mm});
            skLineSegment(sketch, "E2683", {"start": v(228.82, -31.9) * mm, "end": v(229.45, -39.13) * mm});
            skLineSegment(sketch, "E2684", {"start": v(229.45, -39.13) * mm, "end": v(230.4, -45.6) * mm});
            skLineSegment(sketch, "E2685", {"start": v(230.4, -45.6) * mm, "end": v(231.64, -51.35) * mm});
            skLineSegment(sketch, "E2686", {"start": v(231.64, -51.35) * mm, "end": v(233.14, -56.41) * mm});
            skLineSegment(sketch, "E2687", {"start": v(233.14, -56.41) * mm, "end": v(234.96, -60.84) * mm});
            skLineSegment(sketch, "E2688", {"start": v(234.96, -60.84) * mm, "end": v(236.49, -63.75) * mm});
            skLineSegment(sketch, "E2689", {"start": v(236.49, -63.75) * mm, "end": v(237.07, -64.68) * mm});
            skLineSegment(sketch, "E2690", {"start": v(237.07, -64.68) * mm, "end": v(237.7, -65.64) * mm});
            skLineSegment(sketch, "E2691", {"start": v(237.7, -65.64) * mm, "end": v(239.87, -68.34) * mm});
            skLineSegment(sketch, "E2692", {"start": v(239.87, -68.34) * mm, "end": v(242.86, -71.23) * mm});
            skLineSegment(sketch, "E2693", {"start": v(242.86, -71.23) * mm, "end": v(246.06, -73.4) * mm});
            skLineSegment(sketch, "E2694", {"start": v(246.06, -73.4) * mm, "end": v(249.4, -74.98) * mm});
            skLineSegment(sketch, "E2695", {"start": v(249.4, -74.98) * mm, "end": v(252.82, -76.04) * mm});
            skLineSegment(sketch, "E2696", {"start": v(252.82, -76.04) * mm, "end": v(256.28, -76.68) * mm});
            skLineSegment(sketch, "E2697", {"start": v(256.28, -76.68) * mm, "end": v(259.76, -77) * mm});
            skLineSegment(sketch, "E2698", {"start": v(259.76, -77) * mm, "end": v(262.3, -77.08) * mm});
            skLineSegment(sketch, "E2699", {"start": v(262.3, -77.08) * mm, "end": v(263.13, -77.08) * mm});
            skLineSegment(sketch, "E2700", {"start": v(263.13, -77.08) * mm, "end": v(264.28, -77.08) * mm});
            skLineSegment(sketch, "E2701", {"start": v(264.28, -77.08) * mm, "end": v(267.7, -76.91) * mm});
            skLineSegment(sketch, "E2702", {"start": v(267.7, -76.91) * mm, "end": v(271.82, -76.45) * mm});
            skLineSegment(sketch, "E2703", {"start": v(271.82, -76.45) * mm, "end": v(275.48, -75.74) * mm});
            skLineSegment(sketch, "E2704", {"start": v(275.48, -75.74) * mm, "end": v(278.73, -74.85) * mm});
            skLineSegment(sketch, "E2705", {"start": v(278.73, -74.85) * mm, "end": v(281.57, -73.81) * mm});
            skLineSegment(sketch, "E2706", {"start": v(281.57, -73.81) * mm, "end": v(284.06, -72.7) * mm});
            skLineSegment(sketch, "E2707", {"start": v(284.06, -72.7) * mm, "end": v(286.22, -71.58) * mm});
            skLineSegment(sketch, "E2708", {"start": v(286.22, -71.58) * mm, "end": v(287.62, -70.77) * mm});
            skLineSegment(sketch, "E2709", {"start": v(287.62, -70.77) * mm, "end": v(288.08, -70.49) * mm});
            skLineSegment(sketch, "E2710", {"start": v(288.08, -70.49) * mm, "end": v(289.65, -69.51) * mm});
            skLineSegment(sketch, "E2711", {"start": v(289.65, -69.51) * mm, "end": v(294.05, -66.12) * mm});
            skLineSegment(sketch, "E2712", {"start": v(294.05, -66.12) * mm, "end": v(299.81, -60.52) * mm});
            skLineSegment(sketch, "E2713", {"start": v(299.81, -60.52) * mm, "end": v(305.5, -53.56) * mm});
            skLineSegment(sketch, "E2714", {"start": v(305.5, -53.56) * mm, "end": v(309.84, -47.29) * mm});
            skLineSegment(sketch, "E2715", {"start": v(309.84, -47.29) * mm, "end": v(311.2, -45.13) * mm});
            skLineSegment(sketch, "E2716", {"start": v(311.2, -45.13) * mm, "end": v(313.35, -41.7) * mm});
            skLineSegment(sketch, "E2717", {"start": v(313.35, -41.7) * mm, "end": v(332.4, -52.44) * mm});
            skLineSegment(sketch, "E2718", {"start": v(332.4, -52.44) * mm, "end": v(330.27, -56.16) * mm});
            skLineSegment(sketch, "E2719", {"start": v(330.27, -56.16) * mm, "end": v(328.54, -59.1) * mm});
            skLineSegment(sketch, "E2720", {"start": v(328.54, -59.1) * mm, "end": v(322.77, -67.58) * mm});
            skLineSegment(sketch, "E2721", {"start": v(322.77, -67.58) * mm, "end": v(314.42, -77.57) * mm});
            skLineSegment(sketch, "E2722", {"start": v(314.42, -77.57) * mm, "end": v(305.17, -86.07) * mm});
            skLineSegment(sketch, "E2723", {"start": v(305.17, -86.07) * mm, "end": v(297.75, -91.5) * mm});
            skLineSegment(sketch, "E2724", {"start": v(297.75, -91.5) * mm, "end": v(295.14, -93.06) * mm});
            skLineSegment(sketch, "E2725", {"start": v(295.14, -93.06) * mm, "end": v(292.55, -94.6) * mm});
            skLineSegment(sketch, "E2726", {"start": v(292.55, -94.6) * mm, "end": v(284.34, -98.48) * mm});
            skLineSegment(sketch, "E2727", {"start": v(284.34, -98.48) * mm, "end": v(272.81, -102.37) * mm});
            skLineSegment(sketch, "E2728", {"start": v(272.81, -102.37) * mm, "end": v(260.57, -104.71) * mm});
            skLineSegment(sketch, "E2729", {"start": v(260.57, -104.71) * mm, "end": v(250.9, -105.5) * mm});
            skLineSegment(sketch, "E2730", {"start": v(250.9, -105.5) * mm, "end": v(247.66, -105.5) * mm});
            skLineSegment(sketch, "E2731", {"start": v(682.13, -105.5) * mm, "end": v(678.4, -105.5) * mm});
            skLineSegment(sketch, "E2732", {"start": v(678.4, -105.5) * mm, "end": v(667.22, -104.99) * mm});
            skLineSegment(sketch, "E2733", {"start": v(667.22, -104.99) * mm, "end": v(653.3, -103.48) * mm});
            skLineSegment(sketch, "E2734", {"start": v(653.3, -103.48) * mm, "end": v(640.43, -100.97) * mm});
            skLineSegment(sketch, "E2735", {"start": v(640.43, -100.97) * mm, "end": v(631.5, -98.5) * mm});
            skLineSegment(sketch, "E2736", {"start": v(631.5, -98.5) * mm, "end": v(628.61, -97.46) * mm});
            skLineSegment(sketch, "E2737", {"start": v(628.61, -97.46) * mm, "end": v(625.92, -96.51) * mm});
            skLineSegment(sketch, "E2738", {"start": v(625.92, -96.51) * mm, "end": v(618.1, -93.08) * mm});
            skLineSegment(sketch, "E2739", {"start": v(618.1, -93.08) * mm, "end": v(608.5, -87.7) * mm});
            skLineSegment(sketch, "E2740", {"start": v(608.5, -87.7) * mm, "end": v(599.86, -81.36) * mm});
            skLineSegment(sketch, "E2741", {"start": v(599.86, -81.36) * mm, "end": v(593.97, -76) * mm});
            skLineSegment(sketch, "E2742", {"start": v(593.97, -76) * mm, "end": v(592.17, -74.08) * mm});
            skLineSegment(sketch, "E2743", {"start": v(592.17, -74.08) * mm, "end": v(590.36, -72.1) * mm});
            skLineSegment(sketch, "E2744", {"start": v(590.36, -72.1) * mm, "end": v(585.38, -65.71) * mm});
            skLineSegment(sketch, "E2745", {"start": v(585.38, -65.71) * mm, "end": v(579.47, -56.28) * mm});
            skLineSegment(sketch, "E2746", {"start": v(579.47, -56.28) * mm, "end": v(574.44, -45.8) * mm});
            skLineSegment(sketch, "E2747", {"start": v(574.44, -45.8) * mm, "end": v(571.21, -37.23) * mm});
            skLineSegment(sketch, "E2748", {"start": v(571.21, -37.23) * mm, "end": v(570.32, -34.32) * mm});
            skLineSegment(sketch, "E2749", {"start": v(570.32, -34.32) * mm, "end": v(569.36, -31.13) * mm});
            skLineSegment(sketch, "E2750", {"start": v(569.36, -31.13) * mm, "end": v(567.04, -21.4) * mm});
            skLineSegment(sketch, "E2751", {"start": v(567.04, -21.4) * mm, "end": v(564.68, -7.3) * mm});
            skLineSegment(sketch, "E2752", {"start": v(564.68, -7.3) * mm, "end": v(563.26, 7.9) * mm});
            skLineSegment(sketch, "E2753", {"start": v(563.26, 7.9) * mm, "end": v(562.8, 20.1) * mm});
            skLineSegment(sketch, "E2754", {"start": v(562.8, 20.1) * mm, "end": v(562.8, 24.18) * mm});
            skLineSegment(sketch, "E2755", {"start": v(562.8, 24.18) * mm, "end": v(562.8, 226.5) * mm});
            skLineSegment(sketch, "E2756", {"start": v(562.8, 226.5) * mm, "end": v(516.32, 226.5) * mm});
            skLineSegment(sketch, "E2757", {"start": v(516.32, 226.5) * mm, "end": v(516.32, 249.75) * mm});
            skLineSegment(sketch, "E2758", {"start": v(516.32, 249.75) * mm, "end": v(640.63, 249.75) * mm});
            skLineSegment(sketch, "E2759", {"start": v(640.63, 249.75) * mm, "end": v(640.63, 0.57) * mm});
            skLineSegment(sketch, "E2760", {"start": v(640.63, 0.57) * mm, "end": v(640.63, -2.1) * mm});
            skLineSegment(sketch, "E2761", {"start": v(640.63, -2.1) * mm, "end": v(640.86, -10.1) * mm});
            skLineSegment(sketch, "E2762", {"start": v(640.86, -10.1) * mm, "end": v(641.57, -19.86) * mm});
            skLineSegment(sketch, "E2763", {"start": v(641.57, -19.86) * mm, "end": v(642.74, -28.76) * mm});
            skLineSegment(sketch, "E2764", {"start": v(642.74, -28.76) * mm, "end": v(644.41, -36.82) * mm});
            skLineSegment(sketch, "E2765", {"start": v(644.41, -36.82) * mm, "end": v(646.57, -44.08) * mm});
            skLineSegment(sketch, "E2766", {"start": v(646.57, -44.08) * mm, "end": v(649.24, -50.58) * mm});
            skLineSegment(sketch, "E2767", {"start": v(649.24, -50.58) * mm, "end": v(652.41, -56.34) * mm});
            skLineSegment(sketch, "E2768", {"start": v(652.41, -56.34) * mm, "end": v(655.1, -60.2) * mm});
            skLineSegment(sketch, "E2769", {"start": v(655.1, -60.2) * mm, "end": v(656.1, -61.4) * mm});
            skLineSegment(sketch, "E2770", {"start": v(656.1, -61.4) * mm, "end": v(657.21, -62.73) * mm});
            skLineSegment(sketch, "E2771", {"start": v(657.21, -62.73) * mm, "end": v(660.95, -66.33) * mm});
            skLineSegment(sketch, "E2772", {"start": v(660.95, -66.33) * mm, "end": v(666.18, -70.17) * mm});
            skLineSegment(sketch, "E2773", {"start": v(666.18, -70.17) * mm, "end": v(671.67, -73.06) * mm});
            skLineSegment(sketch, "E2774", {"start": v(671.67, -73.06) * mm, "end": v(677.26, -75.12) * mm});
            skLineSegment(sketch, "E2775", {"start": v(677.26, -75.12) * mm, "end": v(682.87, -76.5) * mm});
            skLineSegment(sketch, "E2776", {"start": v(682.87, -76.5) * mm, "end": v(688.33, -77.32) * mm});
            skLineSegment(sketch, "E2777", {"start": v(688.33, -77.32) * mm, "end": v(693.54, -77.7) * mm});
            skLineSegment(sketch, "E2778", {"start": v(693.54, -77.7) * mm, "end": v(697.14, -77.81) * mm});
            skLineSegment(sketch, "E2779", {"start": v(697.14, -77.81) * mm, "end": v(698.36, -77.81) * mm});
            skLineSegment(sketch, "E2780", {"start": v(698.36, -77.81) * mm, "end": v(700.12, -77.81) * mm});
            skLineSegment(sketch, "E2781", {"start": v(700.12, -77.81) * mm, "end": v(705.42, -77.5) * mm});
            skLineSegment(sketch, "E2782", {"start": v(705.42, -77.5) * mm, "end": v(712.4, -76.56) * mm});
            skLineSegment(sketch, "E2783", {"start": v(712.4, -76.56) * mm, "end": v(719.32, -75) * mm});
            skLineSegment(sketch, "E2784", {"start": v(719.32, -75) * mm, "end": v(726.18, -72.84) * mm});
            skLineSegment(sketch, "E2785", {"start": v(726.18, -72.84) * mm, "end": v(732.9, -70.08) * mm});
            skLineSegment(sketch, "E2786", {"start": v(732.9, -70.08) * mm, "end": v(739.56, -66.72) * mm});
            skLineSegment(sketch, "E2787", {"start": v(739.56, -66.72) * mm, "end": v(746.11, -62.77) * mm});
            skLineSegment(sketch, "E2788", {"start": v(746.11, -62.77) * mm, "end": v(752.52, -58.24) * mm});
            skLineSegment(sketch, "E2789", {"start": v(752.52, -58.24) * mm, "end": v(758.81, -53.14) * mm});
            skLineSegment(sketch, "E2790", {"start": v(758.81, -53.14) * mm, "end": v(764.96, -47.48) * mm});
            skLineSegment(sketch, "E2791", {"start": v(764.96, -47.48) * mm, "end": v(770.98, -41.25) * mm});
            skLineSegment(sketch, "E2792", {"start": v(770.98, -41.25) * mm, "end": v(776.82, -34.48) * mm});
            skLineSegment(sketch, "E2793", {"start": v(776.82, -34.48) * mm, "end": v(782.51, -27.16) * mm});
            skLineSegment(sketch, "E2794", {"start": v(782.51, -27.16) * mm, "end": v(788, -19.3) * mm});
            skLineSegment(sketch, "E2795", {"start": v(788, -19.3) * mm, "end": v(793.33, -10.92) * mm});
            skLineSegment(sketch, "E2796", {"start": v(793.33, -10.92) * mm, "end": v(797.22, -4.26) * mm});
            skLineSegment(sketch, "E2797", {"start": v(797.22, -4.26) * mm, "end": v(798.44, -2.01) * mm});
            skLineSegment(sketch, "E2798", {"start": v(798.44, -2.01) * mm, "end": v(799.6, 0.13) * mm});
            skLineSegment(sketch, "E2799", {"start": v(799.6, 0.13) * mm, "end": v(799.6, 226.5) * mm});
            skLineSegment(sketch, "E2800", {"start": v(799.6, 226.5) * mm, "end": v(752.39, 226.5) * mm});
            skLineSegment(sketch, "E2801", {"start": v(752.39, 226.5) * mm, "end": v(752.39, 249.75) * mm});
            skLineSegment(sketch, "E2802", {"start": v(752.39, 249.75) * mm, "end": v(877.43, 249.75) * mm});
            skLineSegment(sketch, "E2803", {"start": v(877.43, 249.75) * mm, "end": v(877.43, -74.87) * mm});
            skLineSegment(sketch, "E2804", {"start": v(877.43, -74.87) * mm, "end": v(923.91, -74.87) * mm});
            skLineSegment(sketch, "E2805", {"start": v(923.91, -74.87) * mm, "end": v(923.91, -98.11) * mm});
            skLineSegment(sketch, "E2806", {"start": v(923.91, -98.11) * mm, "end": v(799.6, -98.11) * mm});
            skLineSegment(sketch, "E2807", {"start": v(799.6, -98.11) * mm, "end": v(799.6, -45.25) * mm});
            skLineSegment(sketch, "E2808", {"start": v(799.6, -45.25) * mm, "end": v(783.22, -62.2) * mm});
            skLineSegment(sketch, "E2809", {"start": v(783.22, -62.2) * mm, "end": v(780.68, -64.85) * mm});
            skLineSegment(sketch, "E2810", {"start": v(780.68, -64.85) * mm, "end": v(772.53, -72.33) * mm});
            skLineSegment(sketch, "E2811", {"start": v(772.53, -72.33) * mm, "end": v(761.23, -81.13) * mm});
            skLineSegment(sketch, "E2812", {"start": v(761.23, -81.13) * mm, "end": v(749.4, -88.59) * mm});
            skLineSegment(sketch, "E2813", {"start": v(749.4, -88.59) * mm, "end": v(740.22, -93.32) * mm});
            skLineSegment(sketch, "E2814", {"start": v(740.22, -93.32) * mm, "end": v(737.05, -94.68) * mm});
            skLineSegment(sketch, "E2815", {"start": v(737.05, -94.68) * mm, "end": v(733.9, -96.02) * mm});
            skLineSegment(sketch, "E2816", {"start": v(733.9, -96.02) * mm, "end": v(724.17, -99.4) * mm});
            skLineSegment(sketch, "E2817", {"start": v(724.17, -99.4) * mm, "end": v(710.68, -102.78) * mm});
            skLineSegment(sketch, "E2818", {"start": v(710.68, -102.78) * mm, "end": v(696.66, -104.81) * mm});
            skLineSegment(sketch, "E2819", {"start": v(696.66, -104.81) * mm, "end": v(685.76, -105.5) * mm});
            skLineSegment(sketch, "E2820", {"start": v(685.76, -105.5) * mm, "end": v(682.13, -105.5) * mm});
            skLineSegment(sketch, "E2821", {"start": v(1262.65, -105.5) * mm, "end": v(1258.61, -105.5) * mm});
            skLineSegment(sketch, "E2822", {"start": v(1258.61, -105.5) * mm, "end": v(1246.37, -105.06) * mm});
            skLineSegment(sketch, "E2823", {"start": v(1246.37, -105.06) * mm, "end": v(1230.77, -103.75) * mm});
            skLineSegment(sketch, "E2824", {"start": v(1230.77, -103.75) * mm, "end": v(1215.94, -101.6) * mm});
            skLineSegment(sketch, "E2825", {"start": v(1215.94, -101.6) * mm, "end": v(1201.94, -98.59) * mm});
            skLineSegment(sketch, "E2826", {"start": v(1201.94, -98.59) * mm, "end": v(1188.81, -94.75) * mm});
            skLineSegment(sketch, "E2827", {"start": v(1188.81, -94.75) * mm, "end": v(1176.57, -90.1) * mm});
            skLineSegment(sketch, "E2828", {"start": v(1176.57, -90.1) * mm, "end": v(1165.27, -84.64) * mm});
            skLineSegment(sketch, "E2829", {"start": v(1165.27, -84.64) * mm, "end": v(1157.44, -80.07) * mm});
            skLineSegment(sketch, "E2830", {"start": v(1157.44, -80.07) * mm, "end": v(1154.98, -78.38) * mm});
            skLineSegment(sketch, "E2831", {"start": v(1154.98, -78.38) * mm, "end": v(1152.74, -76.88) * mm});
            skLineSegment(sketch, "E2832", {"start": v(1152.74, -76.88) * mm, "end": v(1146.42, -71.93) * mm});
            skLineSegment(sketch, "E2833", {"start": v(1146.42, -71.93) * mm, "end": v(1138.93, -64.93) * mm});
            skLineSegment(sketch, "E2834", {"start": v(1138.93, -64.93) * mm, "end": v(1132.5, -57.44) * mm});
            skLineSegment(sketch, "E2835", {"start": v(1132.5, -57.44) * mm, "end": v(1127.2, -49.5) * mm});
            skLineSegment(sketch, "E2836", {"start": v(1127.2, -49.5) * mm, "end": v(1123, -41.15) * mm});
            skLineSegment(sketch, "E2837", {"start": v(1123, -41.15) * mm, "end": v(1119.98, -32.45) * mm});
            skLineSegment(sketch, "E2838", {"start": v(1119.98, -32.45) * mm, "end": v(1118.12, -23.44) * mm});
            skLineSegment(sketch, "E2839", {"start": v(1118.12, -23.44) * mm, "end": v(1117.51, -16.5) * mm});
            skLineSegment(sketch, "E2840", {"start": v(1117.51, -16.5) * mm, "end": v(1117.51, -14.19) * mm});
            skLineSegment(sketch, "E2841", {"start": v(1117.51, -14.19) * mm, "end": v(1117.51, -12.8) * mm});
            skLineSegment(sketch, "E2842", {"start": v(1117.51, -12.8) * mm, "end": v(1117.7, -8.68) * mm});
            skLineSegment(sketch, "E2843", {"start": v(1117.7, -8.68) * mm, "end": v(1118.2, -3.45) * mm});
            skLineSegment(sketch, "E2844", {"start": v(1118.2, -3.45) * mm, "end": v(1119.06, 1.48) * mm});
            skLineSegment(sketch, "E2845", {"start": v(1119.06, 1.48) * mm, "end": v(1120.23, 6.1) * mm});
            skLineSegment(sketch, "E2846", {"start": v(1120.23, 6.1) * mm, "end": v(1121.76, 10.38) * mm});
            skLineSegment(sketch, "E2847", {"start": v(1121.76, 10.38) * mm, "end": v(1123.58, 14.33) * mm});
            skLineSegment(sketch, "E2848", {"start": v(1123.58, 14.33) * mm, "end": v(1125.74, 17.92) * mm});
            skLineSegment(sketch, "E2849", {"start": v(1125.74, 17.92) * mm, "end": v(1127.55, 20.36) * mm});
            skLineSegment(sketch, "E2850", {"start": v(1127.55, 20.36) * mm, "end": v(1128.2, 21.13) * mm});
            skLineSegment(sketch, "E2851", {"start": v(1128.2, 21.13) * mm, "end": v(1129.45, 22.55) * mm});
            skLineSegment(sketch, "E2852", {"start": v(1129.45, 22.55) * mm, "end": v(1133.85, 26.24) * mm});
            skLineSegment(sketch, "E2853", {"start": v(1133.85, 26.24) * mm, "end": v(1140.55, 29.9) * mm});
            skLineSegment(sketch, "E2854", {"start": v(1140.55, 29.9) * mm, "end": v(1148.35, 32.11) * mm});
            skLineSegment(sketch, "E2855", {"start": v(1148.35, 32.11) * mm, "end": v(1154.95, 32.85) * mm});
            skLineSegment(sketch, "E2856", {"start": v(1154.95, 32.85) * mm, "end": v(1157.16, 32.85) * mm});
            skLineSegment(sketch, "E2857", {"start": v(1157.16, 32.85) * mm, "end": v(1158.25, 32.85) * mm});
            skLineSegment(sketch, "E2858", {"start": v(1158.25, 32.85) * mm, "end": v(1161.53, 32.67) * mm});
            skLineSegment(sketch, "E2859", {"start": v(1161.53, 32.67) * mm, "end": v(1165.67, 32.16) * mm});
            skLineSegment(sketch, "E2860", {"start": v(1165.67, 32.16) * mm, "end": v(1169.63, 31.31) * mm});
            skLineSegment(sketch, "E2861", {"start": v(1169.63, 31.31) * mm, "end": v(1173.37, 30.15) * mm});
            skLineSegment(sketch, "E2862", {"start": v(1173.37, 30.15) * mm, "end": v(1176.87, 28.68) * mm});
            skLineSegment(sketch, "E2863", {"start": v(1176.87, 28.68) * mm, "end": v(1180.15, 26.9) * mm});
            skLineSegment(sketch, "E2864", {"start": v(1180.15, 26.9) * mm, "end": v(1183.15, 24.85) * mm});
            skLineSegment(sketch, "E2865", {"start": v(1183.15, 24.85) * mm, "end": v(1185.9, 22.53) * mm});
            skLineSegment(sketch, "E2866", {"start": v(1185.9, 22.53) * mm, "end": v(1188.35, 19.94) * mm});
            skLineSegment(sketch, "E2867", {"start": v(1188.35, 19.94) * mm, "end": v(1190.54, 17.1) * mm});
            skLineSegment(sketch, "E2868", {"start": v(1190.54, 17.1) * mm, "end": v(1192.42, 14.01) * mm});
            skLineSegment(sketch, "E2869", {"start": v(1192.42, 14.01) * mm, "end": v(1193.97, 10.7) * mm});
            skLineSegment(sketch, "E2870", {"start": v(1193.97, 10.7) * mm, "end": v(1195.21, 7.18) * mm});
            skLineSegment(sketch, "E2871", {"start": v(1195.21, 7.18) * mm, "end": v(1196.08, 3.44) * mm});
            skLineSegment(sketch, "E2872", {"start": v(1196.08, 3.44) * mm, "end": v(1196.66, -0.48) * mm});
            skLineSegment(sketch, "E2873", {"start": v(1196.66, -0.48) * mm, "end": v(1196.84, -3.57) * mm});
            skLineSegment(sketch, "E2874", {"start": v(1196.84, -3.57) * mm, "end": v(1196.84, -4.6) * mm});
            skLineSegment(sketch, "E2875", {"start": v(1196.84, -4.6) * mm, "end": v(1196.84, -5.88) * mm});
            skLineSegment(sketch, "E2876", {"start": v(1196.84, -5.88) * mm, "end": v(1196.5, -9.73) * mm});
            skLineSegment(sketch, "E2877", {"start": v(1196.5, -9.73) * mm, "end": v(1195.7, -14.2) * mm});
            skLineSegment(sketch, "E2878", {"start": v(1195.7, -14.2) * mm, "end": v(1194.42, -18.1) * mm});
            skLineSegment(sketch, "E2879", {"start": v(1194.42, -18.1) * mm, "end": v(1192.8, -21.47) * mm});
            skLineSegment(sketch, "E2880", {"start": v(1192.8, -21.47) * mm, "end": v(1190.94, -24.42) * mm});
            skLineSegment(sketch, "E2881", {"start": v(1190.94, -24.42) * mm, "end": v(1188.91, -27.02) * mm});
            skLineSegment(sketch, "E2882", {"start": v(1188.91, -27.02) * mm, "end": v(1186.8, -29.33) * mm});
            skLineSegment(sketch, "E2883", {"start": v(1186.8, -29.33) * mm, "end": v(1185.26, -30.92) * mm});
            skLineSegment(sketch, "E2884", {"start": v(1185.26, -30.92) * mm, "end": v(1184.75, -31.45) * mm});
            skLineSegment(sketch, "E2885", {"start": v(1184.75, -31.45) * mm, "end": v(1183.96, -32.24) * mm});
            skLineSegment(sketch, "E2886", {"start": v(1183.96, -32.24) * mm, "end": v(1181.67, -34.67) * mm});
            skLineSegment(sketch, "E2887", {"start": v(1181.67, -34.67) * mm, "end": v(1179.18, -37.98) * mm});
            skLineSegment(sketch, "E2888", {"start": v(1179.18, -37.98) * mm, "end": v(1177.5, -41.83) * mm});
            skLineSegment(sketch, "E2889", {"start": v(1177.5, -41.83) * mm, "end": v(1176.9, -45.45) * mm});
            skLineSegment(sketch, "E2890", {"start": v(1176.9, -45.45) * mm, "end": v(1176.9, -46.65) * mm});
            skLineSegment(sketch, "E2891", {"start": v(1176.9, -46.65) * mm, "end": v(1176.9, -47.53) * mm});
            skLineSegment(sketch, "E2892", {"start": v(1176.9, -47.53) * mm, "end": v(1177.28, -50.17) * mm});
            skLineSegment(sketch, "E2893", {"start": v(1177.28, -50.17) * mm, "end": v(1178.42, -53.62) * mm});
            skLineSegment(sketch, "E2894", {"start": v(1178.42, -53.62) * mm, "end": v(1180.3, -56.97) * mm});
            skLineSegment(sketch, "E2895", {"start": v(1180.3, -56.97) * mm, "end": v(1182.92, -60.19) * mm});
            skLineSegment(sketch, "E2896", {"start": v(1182.92, -60.19) * mm, "end": v(1186.22, -63.28) * mm});
            skLineSegment(sketch, "E2897", {"start": v(1186.22, -63.28) * mm, "end": v(1190.2, -66.21) * mm});
            skLineSegment(sketch, "E2898", {"start": v(1190.2, -66.21) * mm, "end": v(1194.86, -68.97) * mm});
            skLineSegment(sketch, "E2899", {"start": v(1194.86, -68.97) * mm, "end": v(1198.84, -70.94) * mm});
            skLineSegment(sketch, "E2900", {"start": v(1198.84, -70.94) * mm, "end": v(1200.2, -71.53) * mm});
            skLineSegment(sketch, "E2901", {"start": v(1200.2, -71.53) * mm, "end": v(1201.69, -72.2) * mm});
            skLineSegment(sketch, "E2902", {"start": v(1201.69, -72.2) * mm, "end": v(1206.39, -73.97) * mm});
            skLineSegment(sketch, "E2903", {"start": v(1206.39, -73.97) * mm, "end": v(1213.12, -76.12) * mm});
            skLineSegment(sketch, "E2904", {"start": v(1213.12, -76.12) * mm, "end": v(1220.33, -77.96) * mm});
            skLineSegment(sketch, "E2905", {"start": v(1220.33, -77.96) * mm, "end": v(1227.98, -79.48) * mm});
            skLineSegment(sketch, "E2906", {"start": v(1227.98, -79.48) * mm, "end": v(1236.03, -80.67) * mm});
            skLineSegment(sketch, "E2907", {"start": v(1236.03, -80.67) * mm, "end": v(1244.39, -81.54) * mm});
            skLineSegment(sketch, "E2908", {"start": v(1244.39, -81.54) * mm, "end": v(1253.02, -82.06) * mm});
            skLineSegment(sketch, "E2909", {"start": v(1253.02, -82.06) * mm, "end": v(1259.7, -82.24) * mm});
            skLineSegment(sketch, "E2910", {"start": v(1259.7, -82.24) * mm, "end": v(1261.91, -82.24) * mm});
            skLineSegment(sketch, "E2911", {"start": v(1261.91, -82.24) * mm, "end": v(1264.5, -82.24) * mm});
            skLineSegment(sketch, "E2912", {"start": v(1264.5, -82.24) * mm, "end": v(1272.1, -82.02) * mm});
            skLineSegment(sketch, "E2913", {"start": v(1272.1, -82.02) * mm, "end": v(1281.85, -81.36) * mm});
            skLineSegment(sketch, "E2914", {"start": v(1281.85, -81.36) * mm, "end": v(1291.02, -80.28) * mm});
            skLineSegment(sketch, "E2915", {"start": v(1291.02, -80.28) * mm, "end": v(1299.63, -78.77) * mm});
            skLineSegment(sketch, "E2916", {"start": v(1299.63, -78.77) * mm, "end": v(1307.68, -76.84) * mm});
            skLineSegment(sketch, "E2917", {"start": v(1307.68, -76.84) * mm, "end": v(1315.13, -74.5) * mm});
            skLineSegment(sketch, "E2918", {"start": v(1315.13, -74.5) * mm, "end": v(1321.93, -71.76) * mm});
            skLineSegment(sketch, "E2919", {"start": v(1321.93, -71.76) * mm, "end": v(1326.56, -69.47) * mm});
            skLineSegment(sketch, "E2920", {"start": v(1326.56, -69.47) * mm, "end": v(1328.03, -68.61) * mm});
            skLineSegment(sketch, "E2921", {"start": v(1328.03, -68.61) * mm, "end": v(1329.65, -67.68) * mm});
            skLineSegment(sketch, "E2922", {"start": v(1329.65, -67.68) * mm, "end": v(1334.23, -64.53) * mm});
            skLineSegment(sketch, "E2923", {"start": v(1334.23, -64.53) * mm, "end": v(1339.59, -59.95) * mm});
            skLineSegment(sketch, "E2924", {"start": v(1339.59, -59.95) * mm, "end": v(1344.1, -54.87) * mm});
            skLineSegment(sketch, "E2925", {"start": v(1344.1, -54.87) * mm, "end": v(1347.82, -49.28) * mm});
            skLineSegment(sketch, "E2926", {"start": v(1347.82, -49.28) * mm, "end": v(1350.69, -43.16) * mm});
            skLineSegment(sketch, "E2927", {"start": v(1350.69, -43.16) * mm, "end": v(1352.7, -36.51) * mm});
            skLineSegment(sketch, "E2928", {"start": v(1352.7, -36.51) * mm, "end": v(1353.91, -29.32) * mm});
            skLineSegment(sketch, "E2929", {"start": v(1353.91, -29.32) * mm, "end": v(1354.32, -23.5) * mm});
            skLineSegment(sketch, "E2930", {"start": v(1354.32, -23.5) * mm, "end": v(1354.32, -21.56) * mm});
            skLineSegment(sketch, "E2931", {"start": v(1354.32, -21.56) * mm, "end": v(1354.32, -19.68) * mm});
            skLineSegment(sketch, "E2932", {"start": v(1354.32, -19.68) * mm, "end": v(1353.78, -14.04) * mm});
            skLineSegment(sketch, "E2933", {"start": v(1353.78, -14.04) * mm, "end": v(1352.26, -7.2) * mm});
            skLineSegment(sketch, "E2934", {"start": v(1352.26, -7.2) * mm, "end": v(1349.8, -1) * mm});
            skLineSegment(sketch, "E2935", {"start": v(1349.8, -1) * mm, "end": v(1346.42, 4.64) * mm});
            skLineSegment(sketch, "E2936", {"start": v(1346.42, 4.64) * mm, "end": v(1342.2, 9.73) * mm});
            skLineSegment(sketch, "E2937", {"start": v(1342.2, 9.73) * mm, "end": v(1337.2, 14.33) * mm});
            skLineSegment(sketch, "E2938", {"start": v(1337.2, 14.33) * mm, "end": v(1331.48, 18.5) * mm});
            skLineSegment(sketch, "E2939", {"start": v(1331.48, 18.5) * mm, "end": v(1325.1, 22.27) * mm});
            skLineSegment(sketch, "E2940", {"start": v(1325.1, 22.27) * mm, "end": v(1318.07, 25.7) * mm});
            skLineSegment(sketch, "E2941", {"start": v(1318.07, 25.7) * mm, "end": v(1310.5, 28.83) * mm});
            skLineSegment(sketch, "E2942", {"start": v(1310.5, 28.83) * mm, "end": v(1302.43, 31.71) * mm});
            skLineSegment(sketch, "E2943", {"start": v(1302.43, 31.71) * mm, "end": v(1293.92, 34.4) * mm});
            skLineSegment(sketch, "E2944", {"start": v(1293.92, 34.4) * mm, "end": v(1284.98, 36.94) * mm});
            skLineSegment(sketch, "E2945", {"start": v(1284.98, 36.94) * mm, "end": v(1275.76, 39.37) * mm});
            skLineSegment(sketch, "E2946", {"start": v(1275.76, 39.37) * mm, "end": v(1266.23, 41.75) * mm});
            skLineSegment(sketch, "E2947", {"start": v(1266.23, 41.75) * mm, "end": v(1258.92, 43.53) * mm});
            skLineSegment(sketch, "E2948", {"start": v(1258.92, 43.53) * mm, "end": v(1256.48, 44.11) * mm});
            skLineSegment(sketch, "E2949", {"start": v(1256.48, 44.11) * mm, "end": v(1253.63, 44.8) * mm});
            skLineSegment(sketch, "E2950", {"start": v(1253.63, 44.8) * mm, "end": v(1245.15, 46.87) * mm});
            skLineSegment(sketch, "E2951", {"start": v(1245.15, 46.87) * mm, "end": v(1233.62, 49.8) * mm});
            skLineSegment(sketch, "E2952", {"start": v(1233.62, 49.8) * mm, "end": v(1221.98, 52.97) * mm});
            skLineSegment(sketch, "E2953", {"start": v(1221.98, 52.97) * mm, "end": v(1210.4, 56.47) * mm});
            skLineSegment(sketch, "E2954", {"start": v(1210.4, 56.47) * mm, "end": v(1199.05, 60.39) * mm});
            skLineSegment(sketch, "E2955", {"start": v(1199.05, 60.39) * mm, "end": v(1188.05, 64.79) * mm});
            skLineSegment(sketch, "E2956", {"start": v(1188.05, 64.79) * mm, "end": v(1177.5, 69.76) * mm});
            skLineSegment(sketch, "E2957", {"start": v(1177.5, 69.76) * mm, "end": v(1170.04, 73.87) * mm});
            skLineSegment(sketch, "E2958", {"start": v(1170.04, 73.87) * mm, "end": v(1167.63, 75.37) * mm});
            skLineSegment(sketch, "E2959", {"start": v(1167.63, 75.37) * mm, "end": v(1165.24, 76.87) * mm});
            skLineSegment(sketch, "E2960", {"start": v(1165.24, 76.87) * mm, "end": v(1158.36, 81.84) * mm});
            skLineSegment(sketch, "E2961", {"start": v(1158.36, 81.84) * mm, "end": v(1150.33, 88.83) * mm});
            skLineSegment(sketch, "E2962", {"start": v(1150.33, 88.83) * mm, "end": v(1143.52, 96.39) * mm});
            skLineSegment(sketch, "E2963", {"start": v(1143.52, 96.39) * mm, "end": v(1139.13, 102.44) * mm});
            skLineSegment(sketch, "E2964", {"start": v(1139.13, 102.44) * mm, "end": v(1137.86, 104.57) * mm});
            skLineSegment(sketch, "E2965", {"start": v(1137.86, 104.57) * mm, "end": v(1136.41, 106.98) * mm});
            skLineSegment(sketch, "E2966", {"start": v(1136.41, 106.98) * mm, "end": v(1132.8, 114.66) * mm});
            skLineSegment(sketch, "E2967", {"start": v(1132.8, 114.66) * mm, "end": v(1129.2, 125.6) * mm});
            skLineSegment(sketch, "E2968", {"start": v(1129.2, 125.6) * mm, "end": v(1127.06, 137.46) * mm});
            skLineSegment(sketch, "E2969", {"start": v(1127.06, 137.46) * mm, "end": v(1126.35, 147.11) * mm});
            skLineSegment(sketch, "E2970", {"start": v(1126.35, 147.11) * mm, "end": v(1126.35, 150.33) * mm});
            skLineSegment(sketch, "E2971", {"start": v(1126.35, 150.33) * mm, "end": v(1126.35, 152.94) * mm});
            skLineSegment(sketch, "E2972", {"start": v(1126.35, 152.94) * mm, "end": v(1126.86, 160.77) * mm});
            skLineSegment(sketch, "E2973", {"start": v(1126.86, 160.77) * mm, "end": v(1128.38, 170.94) * mm});
            skLineSegment(sketch, "E2974", {"start": v(1128.38, 170.94) * mm, "end": v(1130.87, 180.79) * mm});
            skLineSegment(sketch, "E2975", {"start": v(1130.87, 180.79) * mm, "end": v(1134.33, 190.26) * mm});
            skLineSegment(sketch, "E2976", {"start": v(1134.33, 190.26) * mm, "end": v(1138.75, 199.3) * mm});
            skLineSegment(sketch, "E2977", {"start": v(1138.75, 199.3) * mm, "end": v(1144.03, 207.86) * mm});
            skLineSegment(sketch, "E2978", {"start": v(1144.03, 207.86) * mm, "end": v(1150.23, 215.88) * mm});
            skLineSegment(sketch, "E2979", {"start": v(1150.23, 215.88) * mm, "end": v(1155.44, 221.53) * mm});
            skLineSegment(sketch, "E2980", {"start": v(1155.44, 221.53) * mm, "end": v(1157.29, 223.3) * mm});
            skLineSegment(sketch, "E2981", {"start": v(1157.29, 223.3) * mm, "end": v(1159.47, 225.38) * mm});
            skLineSegment(sketch, "E2982", {"start": v(1159.47, 225.38) * mm, "end": v(1166.56, 231.1) * mm});
            skLineSegment(sketch, "E2983", {"start": v(1166.56, 231.1) * mm, "end": v(1176.85, 237.92) * mm});
            skLineSegment(sketch, "E2984", {"start": v(1176.85, 237.92) * mm, "end": v(1188.1, 243.72) * mm});
            skLineSegment(sketch, "E2985", {"start": v(1188.1, 243.72) * mm, "end": v(1200.3, 248.51) * mm});
            skLineSegment(sketch, "E2986", {"start": v(1200.3, 248.51) * mm, "end": v(1213.37, 252.26) * mm});
            skLineSegment(sketch, "E2987", {"start": v(1213.37, 252.26) * mm, "end": v(1227.32, 254.95) * mm});
            skLineSegment(sketch, "E2988", {"start": v(1227.32, 254.95) * mm, "end": v(1242.02, 256.58) * mm});
            skLineSegment(sketch, "E2989", {"start": v(1242.02, 256.58) * mm, "end": v(1253.63, 257.13) * mm});
            skLineSegment(sketch, "E2990", {"start": v(1253.63, 257.13) * mm, "end": v(1257.52, 257.13) * mm});
            skLineSegment(sketch, "E2991", {"start": v(1257.52, 257.13) * mm, "end": v(1260.92, 257.13) * mm});
            skLineSegment(sketch, "E2992", {"start": v(1260.92, 257.13) * mm, "end": v(1271.26, 256.74) * mm});
            skLineSegment(sketch, "E2993", {"start": v(1271.26, 256.74) * mm, "end": v(1284.67, 255.59) * mm});
            skLineSegment(sketch, "E2994", {"start": v(1284.67, 255.59) * mm, "end": v(1297.62, 253.69) * mm});
            skLineSegment(sketch, "E2995", {"start": v(1297.62, 253.69) * mm, "end": v(1310.1, 251.06) * mm});
            skLineSegment(sketch, "E2996", {"start": v(1310.1, 251.06) * mm, "end": v(1321.96, 247.72) * mm});
            skLineSegment(sketch, "E2997", {"start": v(1321.96, 247.72) * mm, "end": v(1333.21, 243.7) * mm});
            skLineSegment(sketch, "E2998", {"start": v(1333.21, 243.7) * mm, "end": v(1343.7, 238.99) * mm});
            skLineSegment(sketch, "E2999", {"start": v(1343.7, 238.99) * mm, "end": v(1351.07, 235.07) * mm});
            skLineSegment(sketch, "E3000", {"start": v(1351.07, 235.07) * mm, "end": v(1353.4, 233.63) * mm});
            skLineSegment(sketch, "E3001", {"start": v(1353.4, 233.63) * mm, "end": v(1355.8, 232.17) * mm});
            skLineSegment(sketch, "E3002", {"start": v(1355.8, 232.17) * mm, "end": v(1362.62, 227.34) * mm});
            skLineSegment(sketch, "E3003", {"start": v(1362.62, 227.34) * mm, "end": v(1370.7, 220.45) * mm});
            skLineSegment(sketch, "E3004", {"start": v(1370.7, 220.45) * mm, "end": v(1377.63, 213.03) * mm});
            skLineSegment(sketch, "E3005", {"start": v(1377.63, 213.03) * mm, "end": v(1383.38, 205.11) * mm});
            skLineSegment(sketch, "E3006", {"start": v(1383.38, 205.11) * mm, "end": v(1387.9, 196.75) * mm});
            skLineSegment(sketch, "E3007", {"start": v(1387.9, 196.75) * mm, "end": v(1391.15, 188) * mm});
            skLineSegment(sketch, "E3008", {"start": v(1391.15, 188) * mm, "end": v(1393.1, 178.9) * mm});
            skLineSegment(sketch, "E3009", {"start": v(1393.1, 178.9) * mm, "end": v(1393.79, 171.86) * mm});
            skLineSegment(sketch, "E3010", {"start": v(1393.79, 171.86) * mm, "end": v(1393.79, 169.51) * mm});
            skLineSegment(sketch, "E3011", {"start": v(1393.79, 169.51) * mm, "end": v(1393.79, 167.04) * mm});
            skLineSegment(sketch, "E3012", {"start": v(1393.79, 167.04) * mm, "end": v(1393.1, 159.6) * mm});
            skLineSegment(sketch, "E3013", {"start": v(1393.1, 159.6) * mm, "end": v(1391.07, 150.69) * mm});
            skLineSegment(sketch, "E3014", {"start": v(1391.07, 150.69) * mm, "end": v(1387.7, 142.88) * mm});
            skLineSegment(sketch, "E3015", {"start": v(1387.7, 142.88) * mm, "end": v(1384.37, 137.8) * mm});
            skLineSegment(sketch, "E3016", {"start": v(1384.37, 137.8) * mm, "end": v(1383.02, 136.3) * mm});
            skLineSegment(sketch, "E3017", {"start": v(1383.02, 136.3) * mm, "end": v(1381.8, 134.9) * mm});
            skLineSegment(sketch, "E3018", {"start": v(1381.8, 134.9) * mm, "end": v(1377.4, 131.29) * mm});
            skLineSegment(sketch, "E3019", {"start": v(1377.4, 131.29) * mm, "end": v(1370.78, 127.65) * mm});
            skLineSegment(sketch, "E3020", {"start": v(1370.78, 127.65) * mm, "end": v(1363.23, 125.45) * mm});
            skLineSegment(sketch, "E3021", {"start": v(1363.23, 125.45) * mm, "end": v(1356.96, 124.7) * mm});
            skLineSegment(sketch, "E3022", {"start": v(1356.96, 124.7) * mm, "end": v(1354.88, 124.7) * mm});
            skLineSegment(sketch, "E3023", {"start": v(1354.88, 124.7) * mm, "end": v(1353.78, 124.7) * mm});
            skLineSegment(sketch, "E3024", {"start": v(1353.78, 124.7) * mm, "end": v(1350.43, 124.88) * mm});
            skLineSegment(sketch, "E3025", {"start": v(1350.43, 124.88) * mm, "end": v(1346.19, 125.4) * mm});
            skLineSegment(sketch, "E3026", {"start": v(1346.19, 125.4) * mm, "end": v(1342.18, 126.27) * mm});
            skLineSegment(sketch, "E3027", {"start": v(1342.18, 126.27) * mm, "end": v(1338.37, 127.45) * mm});
            skLineSegment(sketch, "E3028", {"start": v(1338.37, 127.45) * mm, "end": v(1334.81, 128.95) * mm});
            skLineSegment(sketch, "E3029", {"start": v(1334.81, 128.95) * mm, "end": v(1331.48, 130.76) * mm});
            skLineSegment(sketch, "E3030", {"start": v(1331.48, 130.76) * mm, "end": v(1328.4, 132.85) * mm});
            skLineSegment(sketch, "E3031", {"start": v(1328.4, 132.85) * mm, "end": v(1325.62, 135.22) * mm});
            skLineSegment(sketch, "E3032", {"start": v(1325.62, 135.22) * mm, "end": v(1323.13, 137.86) * mm});
            skLineSegment(sketch, "E3033", {"start": v(1323.13, 137.86) * mm, "end": v(1320.9, 140.76) * mm});
            skLineSegment(sketch, "E3034", {"start": v(1320.9, 140.76) * mm, "end": v(1318.99, 143.9) * mm});
            skLineSegment(sketch, "E3035", {"start": v(1318.99, 143.9) * mm, "end": v(1317.41, 147.27) * mm});
            skLineSegment(sketch, "E3036", {"start": v(1317.41, 147.27) * mm, "end": v(1316.14, 150.87) * mm});
            skLineSegment(sketch, "E3037", {"start": v(1316.14, 150.87) * mm, "end": v(1315.23, 154.68) * mm});
            skLineSegment(sketch, "E3038", {"start": v(1315.23, 154.68) * mm, "end": v(1314.67, 158.68) * mm});
            skLineSegment(sketch, "E3039", {"start": v(1314.67, 158.68) * mm, "end": v(1314.5, 161.83) * mm});
            skLineSegment(sketch, "E3040", {"start": v(1314.5, 161.83) * mm, "end": v(1314.5, 162.88) * mm});
            skLineSegment(sketch, "E3041", {"start": v(1314.5, 162.88) * mm, "end": v(1314.5, 163.96) * mm});
            skLineSegment(sketch, "E3042", {"start": v(1314.5, 163.96) * mm, "end": v(1314.8, 167.2) * mm});
            skLineSegment(sketch, "E3043", {"start": v(1314.8, 167.2) * mm, "end": v(1315.68, 171.02) * mm});
            skLineSegment(sketch, "E3044", {"start": v(1315.68, 171.02) * mm, "end": v(1317.03, 174.41) * mm});
            skLineSegment(sketch, "E3045", {"start": v(1317.03, 174.41) * mm, "end": v(1318.76, 177.42) * mm});
            skLineSegment(sketch, "E3046", {"start": v(1318.76, 177.42) * mm, "end": v(1320.76, 180.11) * mm});
            skLineSegment(sketch, "E3047", {"start": v(1320.76, 180.11) * mm, "end": v(1322.97, 182.56) * mm});
            skLineSegment(sketch, "E3048", {"start": v(1322.97, 182.56) * mm, "end": v(1325.29, 184.8) * mm});
            skLineSegment(sketch, "E3049", {"start": v(1325.29, 184.8) * mm, "end": v(1327.04, 186.4) * mm});
            skLineSegment(sketch, "E3050", {"start": v(1327.04, 186.4) * mm, "end": v(1327.65, 186.92) * mm});
            skLineSegment(sketch, "E3051", {"start": v(1327.65, 186.92) * mm, "end": v(1328.51, 187.72) * mm});
            skLineSegment(sketch, "E3052", {"start": v(1328.51, 187.72) * mm, "end": v(1331.18, 190.18) * mm});
            skLineSegment(sketch, "E3053", {"start": v(1331.18, 190.18) * mm, "end": v(1334, 193.43) * mm});
            skLineSegment(sketch, "E3054", {"start": v(1334, 193.43) * mm, "end": v(1335.93, 197) * mm});
            skLineSegment(sketch, "E3055", {"start": v(1335.93, 197) * mm, "end": v(1336.64, 200.18) * mm});
            skLineSegment(sketch, "E3056", {"start": v(1336.64, 200.18) * mm, "end": v(1336.64, 201.25) * mm});
            skLineSegment(sketch, "E3057", {"start": v(1336.64, 201.25) * mm, "end": v(1336.64, 202.05) * mm});
            skLineSegment(sketch, "E3058", {"start": v(1336.64, 202.05) * mm, "end": v(1336.49, 202.85) * mm});
            skLineSegment(sketch, "E3059", {"start": v(1336.49, 202.85) * mm, "end": v(1336.3, 203.79) * mm});
            skLineSegment(sketch, "E3060", {"start": v(1336.3, 203.79) * mm, "end": v(1335.22, 206.5) * mm});
            skLineSegment(sketch, "E3061", {"start": v(1335.22, 206.5) * mm, "end": v(1332.96, 209.89) * mm});
            skLineSegment(sketch, "E3062", {"start": v(1332.96, 209.89) * mm, "end": v(1329.9, 213.02) * mm});
            skLineSegment(sketch, "E3063", {"start": v(1329.9, 213.02) * mm, "end": v(1326.38, 215.85) * mm});
            skLineSegment(sketch, "E3064", {"start": v(1326.38, 215.85) * mm, "end": v(1322.57, 218.35) * mm});
            skLineSegment(sketch, "E3065", {"start": v(1322.57, 218.35) * mm, "end": v(1318.8, 220.47) * mm});
            skLineSegment(sketch, "E3066", {"start": v(1318.8, 220.47) * mm, "end": v(1315.4, 222.21) * mm});
            skLineSegment(sketch, "E3067", {"start": v(1315.4, 222.21) * mm, "end": v(1313.25, 223.2) * mm});
            skLineSegment(sketch, "E3068", {"start": v(1313.25, 223.2) * mm, "end": v(1312.53, 223.52) * mm});
            skLineSegment(sketch, "E3069", {"start": v(1312.53, 223.52) * mm, "end": v(1311.44, 224) * mm});
            skLineSegment(sketch, "E3070", {"start": v(1311.44, 224) * mm, "end": v(1308.09, 225.32) * mm});
            skLineSegment(sketch, "E3071", {"start": v(1308.09, 225.32) * mm, "end": v(1302.93, 227.13) * mm});
            skLineSegment(sketch, "E3072", {"start": v(1302.93, 227.13) * mm, "end": v(1297.1, 228.87) * mm});
            skLineSegment(sketch, "E3073", {"start": v(1297.1, 228.87) * mm, "end": v(1290.46, 230.47) * mm});
            skLineSegment(sketch, "E3074", {"start": v(1290.46, 230.47) * mm, "end": v(1283.15, 231.85) * mm});
            skLineSegment(sketch, "E3075", {"start": v(1283.15, 231.85) * mm, "end": v(1275.07, 232.93) * mm});
            skLineSegment(sketch, "E3076", {"start": v(1275.07, 232.93) * mm, "end": v(1266.28, 233.63) * mm});
            skLineSegment(sketch, "E3077", {"start": v(1266.28, 233.63) * mm, "end": v(1259.12, 233.88) * mm});
            skLineSegment(sketch, "E3078", {"start": v(1259.12, 233.88) * mm, "end": v(1256.76, 233.88) * mm});
            skLineSegment(sketch, "E3079", {"start": v(1256.76, 233.88) * mm, "end": v(1254.27, 233.88) * mm});
            skLineSegment(sketch, "E3080", {"start": v(1254.27, 233.88) * mm, "end": v(1246.82, 233.61) * mm});
            skLineSegment(sketch, "E3081", {"start": v(1246.82, 233.61) * mm, "end": v(1237.35, 232.81) * mm});
            skLineSegment(sketch, "E3082", {"start": v(1237.35, 232.81) * mm, "end": v(1228.46, 231.49) * mm});
            skLineSegment(sketch, "E3083", {"start": v(1228.46, 231.49) * mm, "end": v(1220.1, 229.64) * mm});
            skLineSegment(sketch, "E3084", {"start": v(1220.1, 229.64) * mm, "end": v(1212.38, 227.28) * mm});
            skLineSegment(sketch, "E3085", {"start": v(1212.38, 227.28) * mm, "end": v(1205.27, 224.42) * mm});
            skLineSegment(sketch, "E3086", {"start": v(1205.27, 224.42) * mm, "end": v(1198.8, 221.06) * mm});
            skLineSegment(sketch, "E3087", {"start": v(1198.8, 221.06) * mm, "end": v(1194.4, 218.26) * mm});
            skLineSegment(sketch, "E3088", {"start": v(1194.4, 218.26) * mm, "end": v(1193.03, 217.21) * mm});
            skLineSegment(sketch, "E3089", {"start": v(1193.03, 217.21) * mm, "end": v(1191.8, 216.32) * mm});
            skLineSegment(sketch, "E3090", {"start": v(1191.8, 216.32) * mm, "end": v(1188.43, 213.38) * mm});
            skLineSegment(sketch, "E3091", {"start": v(1188.43, 213.38) * mm, "end": v(1184.44, 209.2) * mm});
            skLineSegment(sketch, "E3092", {"start": v(1184.44, 209.2) * mm, "end": v(1181.06, 204.68) * mm});
            skLineSegment(sketch, "E3093", {"start": v(1181.06, 204.68) * mm, "end": v(1178.24, 199.83) * mm});
            skLineSegment(sketch, "E3094", {"start": v(1178.24, 199.83) * mm, "end": v(1176.06, 194.7) * mm});
            skLineSegment(sketch, "E3095", {"start": v(1176.06, 194.7) * mm, "end": v(1174.49, 189.26) * mm});
            skLineSegment(sketch, "E3096", {"start": v(1174.49, 189.26) * mm, "end": v(1173.55, 183.57) * mm});
            skLineSegment(sketch, "E3097", {"start": v(1173.55, 183.57) * mm, "end": v(1173.22, 179.11) * mm});
            skLineSegment(sketch, "E3098", {"start": v(1173.22, 179.11) * mm, "end": v(1173.22, 177.63) * mm});
            skLineSegment(sketch, "E3099", {"start": v(1173.22, 177.63) * mm, "end": v(1173.22, 176.02) * mm});
            skLineSegment(sketch, "E3100", {"start": v(1173.22, 176.02) * mm, "end": v(1173.65, 171.2) * mm});
            skLineSegment(sketch, "E3101", {"start": v(1173.65, 171.2) * mm, "end": v(1174.97, 165.16) * mm});
            skLineSegment(sketch, "E3102", {"start": v(1174.97, 165.16) * mm, "end": v(1177.15, 159.5) * mm});
            skLineSegment(sketch, "E3103", {"start": v(1177.15, 159.5) * mm, "end": v(1180.23, 154.19) * mm});
            skLineSegment(sketch, "E3104", {"start": v(1180.23, 154.19) * mm, "end": v(1184.21, 149.24) * mm});
            skLineSegment(sketch, "E3105", {"start": v(1184.21, 149.24) * mm, "end": v(1189.1, 144.63) * mm});
            skLineSegment(sketch, "E3106", {"start": v(1189.1, 144.63) * mm, "end": v(1194.86, 140.36) * mm});
            skLineSegment(sketch, "E3107", {"start": v(1194.86, 140.36) * mm, "end": v(1199.83, 137.32) * mm});
            skLineSegment(sketch, "E3108", {"start": v(1199.83, 137.32) * mm, "end": v(1201.56, 136.41) * mm});
            skLineSegment(sketch, "E3109", {"start": v(1201.56, 136.41) * mm, "end": v(1203.11, 135.6) * mm});
            skLineSegment(sketch, "E3110", {"start": v(1203.11, 135.6) * mm, "end": v(1207.86, 133.33) * mm});
            skLineSegment(sketch, "E3111", {"start": v(1207.86, 133.33) * mm, "end": v(1214.8, 130.43) * mm});
            skLineSegment(sketch, "E3112", {"start": v(1214.8, 130.43) * mm, "end": v(1222.24, 127.7) * mm});
            skLineSegment(sketch, "E3113", {"start": v(1222.24, 127.7) * mm, "end": v(1230.19, 125.06) * mm});
            skLineSegment(sketch, "E3114", {"start": v(1230.19, 125.06) * mm, "end": v(1238.75, 122.5) * mm});
            skLineSegment(sketch, "E3115", {"start": v(1238.75, 122.5) * mm, "end": v(1247.76, 119.97) * mm});
            skLineSegment(sketch, "E3116", {"start": v(1247.76, 119.97) * mm, "end": v(1257.34, 117.43) * mm});
            skLineSegment(sketch, "E3117", {"start": v(1257.34, 117.43) * mm, "end": v(1264.83, 115.49) * mm});
            skLineSegment(sketch, "E3118", {"start": v(1264.83, 115.49) * mm, "end": v(1267.37, 114.84) * mm});
            skLineSegment(sketch, "E3119", {"start": v(1267.37, 114.84) * mm, "end": v(1270.24, 114.1) * mm});
            skLineSegment(sketch, "E3120", {"start": v(1270.24, 114.1) * mm, "end": v(1278.93, 111.87) * mm});
            skLineSegment(sketch, "E3121", {"start": v(1278.93, 111.87) * mm, "end": v(1290.7, 108.72) * mm});
            skLineSegment(sketch, "E3122", {"start": v(1290.7, 108.72) * mm, "end": v(1302.6, 105.31) * mm});
            skLineSegment(sketch, "E3123", {"start": v(1302.6, 105.31) * mm, "end": v(1314.36, 101.56) * mm});
            skLineSegment(sketch, "E3124", {"start": v(1314.36, 101.56) * mm, "end": v(1325.97, 97.38) * mm});
            skLineSegment(sketch, "E3125", {"start": v(1325.97, 97.38) * mm, "end": v(1337.22, 92.7) * mm});
            skLineSegment(sketch, "E3126", {"start": v(1337.22, 92.7) * mm, "end": v(1348, 87.43) * mm});
            skLineSegment(sketch, "E3127", {"start": v(1348, 87.43) * mm, "end": v(1355.64, 83.09) * mm});
            skLineSegment(sketch, "E3128", {"start": v(1355.64, 83.09) * mm, "end": v(1358.08, 81.5) * mm});
            skLineSegment(sketch, "E3129", {"start": v(1358.08, 81.5) * mm, "end": v(1360.54, 79.9) * mm});
            skLineSegment(sketch, "E3130", {"start": v(1360.54, 79.9) * mm, "end": v(1367.6, 74.66) * mm});
            skLineSegment(sketch, "E3131", {"start": v(1367.6, 74.66) * mm, "end": v(1375.83, 67.3) * mm});
            skLineSegment(sketch, "E3132", {"start": v(1375.83, 67.3) * mm, "end": v(1382.82, 59.33) * mm});
            skLineSegment(sketch, "E3133", {"start": v(1382.82, 59.33) * mm, "end": v(1387.29, 52.97) * mm});
            skLineSegment(sketch, "E3134", {"start": v(1387.29, 52.97) * mm, "end": v(1388.6, 50.73) * mm});
            skLineSegment(sketch, "E3135", {"start": v(1388.6, 50.73) * mm, "end": v(1390.08, 48.2) * mm});
            skLineSegment(sketch, "E3136", {"start": v(1390.08, 48.2) * mm, "end": v(1393.81, 40.13) * mm});
            skLineSegment(sketch, "E3137", {"start": v(1393.81, 40.13) * mm, "end": v(1397.5, 28.66) * mm});
            skLineSegment(sketch, "E3138", {"start": v(1397.5, 28.66) * mm, "end": v(1399.7, 16.24) * mm});
            skLineSegment(sketch, "E3139", {"start": v(1399.7, 16.24) * mm, "end": v(1400.42, 6.14) * mm});
            skLineSegment(sketch, "E3140", {"start": v(1400.42, 6.14) * mm, "end": v(1400.42, 2.78) * mm});
            skLineSegment(sketch, "E3141", {"start": v(1400.42, 2.78) * mm, "end": v(1400.42, -0.1) * mm});
            skLineSegment(sketch, "E3142", {"start": v(1400.42, -0.1) * mm, "end": v(1399.89, -8.73) * mm});
            skLineSegment(sketch, "E3143", {"start": v(1399.89, -8.73) * mm, "end": v(1398.18, -19.77) * mm});
            skLineSegment(sketch, "E3144", {"start": v(1398.18, -19.77) * mm, "end": v(1395.41, -30.3) * mm});
            skLineSegment(sketch, "E3145", {"start": v(1395.41, -30.3) * mm, "end": v(1391.55, -40.32) * mm});
            skLineSegment(sketch, "E3146", {"start": v(1391.55, -40.32) * mm, "end": v(1386.65, -49.76) * mm});
            skLineSegment(sketch, "E3147", {"start": v(1386.65, -49.76) * mm, "end": v(1380.66, -58.6) * mm});
            skLineSegment(sketch, "E3148", {"start": v(1380.66, -58.6) * mm, "end": v(1373.67, -66.8) * mm});
            skLineSegment(sketch, "E3149", {"start": v(1373.67, -66.8) * mm, "end": v(1367.75, -72.56) * mm});
            skLineSegment(sketch, "E3150", {"start": v(1367.75, -72.56) * mm, "end": v(1365.62, -74.34) * mm});
            skLineSegment(sketch, "E3151", {"start": v(1365.62, -74.34) * mm, "end": v(1363.33, -76.27) * mm});
            skLineSegment(sketch, "E3152", {"start": v(1363.33, -76.27) * mm, "end": v(1356.04, -81.53) * mm});
            skLineSegment(sketch, "E3153", {"start": v(1356.04, -81.53) * mm, "end": v(1345.43, -87.8) * mm});
            skLineSegment(sketch, "E3154", {"start": v(1345.43, -87.8) * mm, "end": v(1333.82, -93.15) * mm});
            skLineSegment(sketch, "E3155", {"start": v(1333.82, -93.15) * mm, "end": v(1321.25, -97.56) * mm});
            skLineSegment(sketch, "E3156", {"start": v(1321.25, -97.56) * mm, "end": v(1307.84, -101.01) * mm});
            skLineSegment(sketch, "E3157", {"start": v(1307.84, -101.01) * mm, "end": v(1293.56, -103.49) * mm});
            skLineSegment(sketch, "E3158", {"start": v(1293.56, -103.49) * mm, "end": v(1278.5, -105) * mm});
            skLineSegment(sketch, "E3159", {"start": v(1278.5, -105) * mm, "end": v(1266.61, -105.5) * mm});
            skLineSegment(sketch, "E3160", {"start": v(1266.61, -105.5) * mm, "end": v(1262.65, -105.5) * mm});
            skLineSegment(sketch, "E3161", {"start": v(1575.42, -157.83) * mm, "end": v(1578.85, -155.35) * mm});
            skLineSegment(sketch, "E3162", {"start": v(1578.85, -155.35) * mm, "end": v(1582.97, -152.34) * mm});
            skLineSegment(sketch, "E3163", {"start": v(1582.97, -152.34) * mm, "end": v(1595.08, -142.86) * mm});
            skLineSegment(sketch, "E3164", {"start": v(1595.08, -142.86) * mm, "end": v(1609.94, -129.96) * mm});
            skLineSegment(sketch, "E3165", {"start": v(1609.94, -129.96) * mm, "end": v(1623.43, -116.58) * mm});
            skLineSegment(sketch, "E3166", {"start": v(1623.43, -116.58) * mm, "end": v(1635.62, -102.67) * mm});
            skLineSegment(sketch, "E3167", {"start": v(1635.62, -102.67) * mm, "end": v(1646.54, -88.15) * mm});
            skLineSegment(sketch, "E3168", {"start": v(1646.54, -88.15) * mm, "end": v(1656.25, -72.96) * mm});
            skLineSegment(sketch, "E3169", {"start": v(1656.25, -72.96) * mm, "end": v(1664.83, -57.06) * mm});
            skLineSegment(sketch, "E3170", {"start": v(1664.83, -57.06) * mm, "end": v(1670.57, -44.6) * mm});
            skLineSegment(sketch, "E3171", {"start": v(1670.57, -44.6) * mm, "end": v(1672.27, -40.35) * mm});
            skLineSegment(sketch, "E3172", {"start": v(1672.27, -40.35) * mm, "end": v(1673.85, -36.46) * mm});
            skLineSegment(sketch, "E3173", {"start": v(1673.85, -36.46) * mm, "end": v(1678.1, -24.55) * mm});
            skLineSegment(sketch, "E3174", {"start": v(1678.1, -24.55) * mm, "end": v(1683.07, -7.84) * mm});
            skLineSegment(sketch, "E3175", {"start": v(1683.07, -7.84) * mm, "end": v(1687.26, 9.88) * mm});
            skLineSegment(sketch, "E3176", {"start": v(1687.26, 9.88) * mm, "end": v(1690.64, 28.67) * mm});
            skLineSegment(sketch, "E3177", {"start": v(1690.64, 28.67) * mm, "end": v(1693.26, 48.64) * mm});
            skLineSegment(sketch, "E3178", {"start": v(1693.26, 48.64) * mm, "end": v(1695.13, 69.86) * mm});
            skLineSegment(sketch, "E3179", {"start": v(1695.13, 69.86) * mm, "end": v(1696.23, 92.42) * mm});
            skLineSegment(sketch, "E3180", {"start": v(1696.23, 92.42) * mm, "end": v(1696.6, 110.4) * mm});
            skLineSegment(sketch, "E3181", {"start": v(1696.6, 110.4) * mm, "end": v(1696.6, 116.4) * mm});
            skLineSegment(sketch, "E3182", {"start": v(1696.6, 116.4) * mm, "end": v(1696.6, 122.4) * mm});
            skLineSegment(sketch, "E3183", {"start": v(1696.6, 122.4) * mm, "end": v(1696.23, 140.38) * mm});
            skLineSegment(sketch, "E3184", {"start": v(1696.23, 140.38) * mm, "end": v(1695.13, 162.94) * mm});
            skLineSegment(sketch, "E3185", {"start": v(1695.13, 162.94) * mm, "end": v(1693.26, 184.16) * mm});
            skLineSegment(sketch, "E3186", {"start": v(1693.26, 184.16) * mm, "end": v(1690.64, 204.12) * mm});
            skLineSegment(sketch, "E3187", {"start": v(1690.64, 204.12) * mm, "end": v(1687.26, 222.92) * mm});
            skLineSegment(sketch, "E3188", {"start": v(1687.26, 222.92) * mm, "end": v(1683.07, 240.63) * mm});
            skLineSegment(sketch, "E3189", {"start": v(1683.07, 240.63) * mm, "end": v(1678.1, 257.34) * mm});
            skLineSegment(sketch, "E3190", {"start": v(1678.1, 257.34) * mm, "end": v(1673.85, 269.25) * mm});
            skLineSegment(sketch, "E3191", {"start": v(1673.85, 269.25) * mm, "end": v(1672.27, 273.14) * mm});
            skLineSegment(sketch, "E3192", {"start": v(1672.27, 273.14) * mm, "end": v(1670.57, 277.38) * mm});
            skLineSegment(sketch, "E3193", {"start": v(1670.57, 277.38) * mm, "end": v(1664.83, 289.85) * mm});
            skLineSegment(sketch, "E3194", {"start": v(1664.83, 289.85) * mm, "end": v(1656.25, 305.76) * mm});
            skLineSegment(sketch, "E3195", {"start": v(1656.25, 305.76) * mm, "end": v(1646.54, 320.94) * mm});
            skLineSegment(sketch, "E3196", {"start": v(1646.54, 320.94) * mm, "end": v(1635.62, 335.46) * mm});
            skLineSegment(sketch, "E3197", {"start": v(1635.62, 335.46) * mm, "end": v(1623.43, 349.37) * mm});
            skLineSegment(sketch, "E3198", {"start": v(1623.43, 349.37) * mm, "end": v(1609.94, 362.75) * mm});
            skLineSegment(sketch, "E3199", {"start": v(1609.94, 362.75) * mm, "end": v(1595.08, 375.65) * mm});
            skLineSegment(sketch, "E3200", {"start": v(1595.08, 375.65) * mm, "end": v(1582.97, 385.14) * mm});
            skLineSegment(sketch, "E3201", {"start": v(1582.97, 385.14) * mm, "end": v(1578.85, 388.14) * mm});
            skLineSegment(sketch, "E3202", {"start": v(1578.85, 388.14) * mm, "end": v(1575.42, 390.61) * mm});
            skLineSegment(sketch, "E3203", {"start": v(1575.42, 390.61) * mm, "end": v(1587.57, 407.62) * mm});
            skLineSegment(sketch, "E3204", {"start": v(1587.57, 407.62) * mm, "end": v(1590.94, 405.51) * mm});
            skLineSegment(sketch, "E3205", {"start": v(1590.94, 405.51) * mm, "end": v(1595.47, 402.7) * mm});
            skLineSegment(sketch, "E3206", {"start": v(1595.47, 402.7) * mm, "end": v(1608.8, 393.84) * mm});
            skLineSegment(sketch, "E3207", {"start": v(1608.8, 393.84) * mm, "end": v(1625.74, 381.64) * mm});
            skLineSegment(sketch, "E3208", {"start": v(1625.74, 381.64) * mm, "end": v(1641.8, 368.93) * mm});
            skLineSegment(sketch, "E3209", {"start": v(1641.8, 368.93) * mm, "end": v(1656.88, 355.72) * mm});
            skLineSegment(sketch, "E3210", {"start": v(1656.88, 355.72) * mm, "end": v(1671.06, 342.01) * mm});
            skLineSegment(sketch, "E3211", {"start": v(1671.06, 342.01) * mm, "end": v(1684.34, 327.83) * mm});
            skLineSegment(sketch, "E3212", {"start": v(1684.34, 327.83) * mm, "end": v(1696.6, 313.18) * mm});
            skLineSegment(sketch, "E3213", {"start": v(1696.6, 313.18) * mm, "end": v(1705.2, 301.94) * mm});
            skLineSegment(sketch, "E3214", {"start": v(1705.2, 301.94) * mm, "end": v(1707.89, 298.08) * mm});
            skLineSegment(sketch, "E3215", {"start": v(1707.89, 298.08) * mm, "end": v(1711.42, 293.11) * mm});
            skLineSegment(sketch, "E3216", {"start": v(1711.42, 293.11) * mm, "end": v(1721.2, 277.67) * mm});
            skLineSegment(sketch, "E3217", {"start": v(1721.2, 277.67) * mm, "end": v(1732.73, 256.56) * mm});
            skLineSegment(sketch, "E3218", {"start": v(1732.73, 256.56) * mm, "end": v(1742.53, 234.78) * mm});
            skLineSegment(sketch, "E3219", {"start": v(1742.53, 234.78) * mm, "end": v(1750.56, 212.33) * mm});
            skLineSegment(sketch, "E3220", {"start": v(1750.56, 212.33) * mm, "end": v(1756.78, 189.26) * mm});
            skLineSegment(sketch, "E3221", {"start": v(1756.78, 189.26) * mm, "end": v(1761.23, 165.56) * mm});
            skLineSegment(sketch, "E3222", {"start": v(1761.23, 165.56) * mm, "end": v(1763.94, 141.27) * mm});
            skLineSegment(sketch, "E3223", {"start": v(1763.94, 141.27) * mm, "end": v(1764.83, 122.62) * mm});
            skLineSegment(sketch, "E3224", {"start": v(1764.83, 122.62) * mm, "end": v(1764.83, 116.4) * mm});
            skLineSegment(sketch, "E3225", {"start": v(1764.83, 116.4) * mm, "end": v(1764.83, 110.18) * mm});
            skLineSegment(sketch, "E3226", {"start": v(1764.83, 110.18) * mm, "end": v(1763.94, 91.53) * mm});
            skLineSegment(sketch, "E3227", {"start": v(1763.94, 91.53) * mm, "end": v(1761.23, 67.24) * mm});
            skLineSegment(sketch, "E3228", {"start": v(1761.23, 67.24) * mm, "end": v(1756.78, 43.54) * mm});
            skLineSegment(sketch, "E3229", {"start": v(1756.78, 43.54) * mm, "end": v(1750.56, 20.47) * mm});
            skLineSegment(sketch, "E3230", {"start": v(1750.56, 20.47) * mm, "end": v(1742.53, -1.98) * mm});
            skLineSegment(sketch, "E3231", {"start": v(1742.53, -1.98) * mm, "end": v(1732.73, -23.77) * mm});
            skLineSegment(sketch, "E3232", {"start": v(1732.73, -23.77) * mm, "end": v(1721.2, -44.88) * mm});
            skLineSegment(sketch, "E3233", {"start": v(1721.2, -44.88) * mm, "end": v(1711.42, -60.32) * mm});
            skLineSegment(sketch, "E3234", {"start": v(1711.42, -60.32) * mm, "end": v(1707.89, -65.3) * mm});
            skLineSegment(sketch, "E3235", {"start": v(1707.89, -65.3) * mm, "end": v(1705.2, -69.14) * mm});
            skLineSegment(sketch, "E3236", {"start": v(1705.2, -69.14) * mm, "end": v(1696.6, -80.4) * mm});
            skLineSegment(sketch, "E3237", {"start": v(1696.6, -80.4) * mm, "end": v(1684.34, -95.04) * mm});
            skLineSegment(sketch, "E3238", {"start": v(1684.34, -95.04) * mm, "end": v(1671.06, -109.22) * mm});
            skLineSegment(sketch, "E3239", {"start": v(1671.06, -109.22) * mm, "end": v(1656.88, -122.93) * mm});
            skLineSegment(sketch, "E3240", {"start": v(1656.88, -122.93) * mm, "end": v(1641.8, -136.14) * mm});
            skLineSegment(sketch, "E3241", {"start": v(1641.8, -136.14) * mm, "end": v(1625.74, -148.85) * mm});
            skLineSegment(sketch, "E3242", {"start": v(1625.74, -148.85) * mm, "end": v(1608.8, -161.05) * mm});
            skLineSegment(sketch, "E3243", {"start": v(1608.8, -161.05) * mm, "end": v(1595.47, -169.9) * mm});
            skLineSegment(sketch, "E3244", {"start": v(1595.47, -169.9) * mm, "end": v(1590.94, -172.72) * mm});
            skLineSegment(sketch, "E3245", {"start": v(1590.94, -172.72) * mm, "end": v(1587.57, -174.83) * mm});
            skLineSegment(sketch, "E3246", {"start": v(1587.57, -174.83) * mm, "end": v(1575.42, -157.83) * mm});
            skSolve(sketch);
        }
        {
            var Q0;
            Q0=makeQuery(id+"F0.imprint","IMPRINT",FACE,{"disambiguationData":[TD([[makeQuery(id+"F0.imprint","IMPRINT",EDGE,{"derivedFrom":sQuery(id+"F0.wireOp",EDGE,"E2071")}),-1.0]])]});
            var Q1;
            Q1=makeQuery(id+"F0.imprint","IMPRINT",FACE,{"disambiguationData":[TD([[makeQuery(id+"F0.imprint","IMPRINT",EDGE,{"derivedFrom":sQuery(id+"F0.wireOp",EDGE,"E4")}),1.0]])]});
            var Q2;
            Q2=makeQuery(id+"F0.imprint","IMPRINT",FACE,{"disambiguationData":[TD([[makeQuery(id+"F0.imprint","IMPRINT",EDGE,{"derivedFrom":sQuery(id+"F0.wireOp",EDGE,"E118")}),1.0]])]});
            var Q3;
            Q3=makeQuery(id+"F0.imprint","IMPRINT",FACE,{"disambiguationData":[TD([[makeQuery(id+"F0.imprint","IMPRINT",EDGE,{"derivedFrom":sQuery(id+"F0.wireOp",EDGE,"E2157")}),-1.0]])]});
            var Q4;
            Q4=makeQuery(id+"F0.imprint","IMPRINT",FACE,{"disambiguationData":[TD([[makeQuery(id+"F0.imprint","IMPRINT",EDGE,{"derivedFrom":sQuery(id+"F0.wireOp",EDGE,"E208")}),1.0]])]});
            var Q5;
            Q5=makeQuery(id+"F0.imprint","IMPRINT",FACE,{"disambiguationData":[TD([[makeQuery(id+"F0.imprint","IMPRINT",EDGE,{"derivedFrom":sQuery(id+"F0.wireOp",EDGE,"E2251")}),-1.0]])]});
            var Q6;
            Q6=makeQuery(id+"F0.imprint","IMPRINT",FACE,{"disambiguationData":[TD([[makeQuery(id+"F0.imprint","IMPRINT",EDGE,{"derivedFrom":sQuery(id+"F0.wireOp",EDGE,"E218")}),1.0]])]});
            var Q7;
            Q7=makeQuery(id+"F0.imprint","IMPRINT",FACE,{"disambiguationData":[TD([[makeQuery(id+"F0.imprint","IMPRINT",EDGE,{"derivedFrom":sQuery(id+"F0.wireOp",EDGE,"E2261")}),-1.0]])]});
            var Q8;
            Q8=makeQuery(id+"F0.imprint","IMPRINT",FACE,{"disambiguationData":[TD([[makeQuery(id+"F0.imprint","IMPRINT",EDGE,{"derivedFrom":sQuery(id+"F0.wireOp",EDGE,"E2335")}),-1.0]])]});
            var Q9;
            Q9=makeQuery(id+"F0.imprint","IMPRINT",FACE,{"disambiguationData":[TD([[makeQuery(id+"F0.imprint","IMPRINT",EDGE,{"derivedFrom":sQuery(id+"F0.wireOp",EDGE,"E290")}),1.0]])]});
            var Q10;
            Q10=makeQuery(id+"F0.imprint","IMPRINT",FACE,{"disambiguationData":[TD([[makeQuery(id+"F0.imprint","IMPRINT",EDGE,{"derivedFrom":sQuery(id+"F0.wireOp",EDGE,"E338")}),1.0]])]});
            var Q11;
            Q11=makeQuery(id+"F0.imprint","IMPRINT",FACE,{"disambiguationData":[TD([[makeQuery(id+"F0.imprint","IMPRINT",EDGE,{"derivedFrom":sQuery(id+"F0.wireOp",EDGE,"E580")}),1.0]])]});
            var Q12;
            Q12=makeQuery(id+"F0.imprint","IMPRINT",FACE,{"disambiguationData":[TD([[makeQuery(id+"F0.imprint","IMPRINT",EDGE,{"derivedFrom":sQuery(id+"F0.wireOp",EDGE,"E2640")}),-1.0]])]});
            var Q13;
            Q13=makeQuery(id+"F0.imprint","IMPRINT",FACE,{"disambiguationData":[TD([[makeQuery(id+"F0.imprint","IMPRINT",EDGE,{"derivedFrom":sQuery(id+"F0.wireOp",EDGE,"E660")}),1.0]])]});
            var Q14;
            Q14=makeQuery(id+"F0.imprint","IMPRINT",FACE,{"disambiguationData":[TD([[makeQuery(id+"F0.imprint","IMPRINT",EDGE,{"derivedFrom":sQuery(id+"F0.wireOp",EDGE,"E2731")}),-1.0]])]});
            var Q15;
            Q15=makeQuery(id+"F0.imprint","IMPRINT",FACE,{"disambiguationData":[TD([[makeQuery(id+"F0.imprint","IMPRINT",EDGE,{"derivedFrom":sQuery(id+"F0.wireOp",EDGE,"E738")}),1.0]])]});
            var Q16;
            Q16=makeQuery(id+"F0.imprint","IMPRINT",FACE,{"disambiguationData":[TD([[makeQuery(id+"F0.imprint","IMPRINT",EDGE,{"derivedFrom":sQuery(id+"F0.wireOp",EDGE,"E2821")}),-1.0]])]});
            var Q17;
            Q17=makeQuery(id+"F0.imprint","IMPRINT",FACE,{"disambiguationData":[TD([[makeQuery(id+"F0.imprint","IMPRINT",EDGE,{"derivedFrom":sQuery(id+"F0.wireOp",EDGE,"E1102")}),1.0]])]});
            var Q18;
            Q18=makeQuery(id+"F0.imprint","IMPRINT",FACE,{"disambiguationData":[TD([[makeQuery(id+"F0.imprint","IMPRINT",EDGE,{"derivedFrom":sQuery(id+"F0.wireOp",EDGE,"E3161")}),-1.0]])]});
            var Q19;
            Q19=makeQuery(id+"F0.imprint","IMPRINT",FACE,{"disambiguationData":[TD([[makeQuery(id+"F0.imprint","IMPRINT",EDGE,{"derivedFrom":sQuery(id+"F0.wireOp",EDGE,"E1216")}),1.0]])]});
            var Q20;
            Q20=makeQuery(id+"F0.imprint","IMPRINT",FACE,{"disambiguationData":[TD([[makeQuery(id+"F0.imprint","IMPRINT",EDGE,{"derivedFrom":sQuery(id+"F0.wireOp",EDGE,"E1405")}),1.0]])]});
            var Q21;
            Q21=makeQuery(id+"F0.imprint","IMPRINT",FACE,{"disambiguationData":[TD([[makeQuery(id+"F0.imprint","IMPRINT",EDGE,{"derivedFrom":sQuery(id+"F0.wireOp",EDGE,"E1487")}),1.0]])]});
            var Q22;
            Q22=makeQuery(id+"F0.imprint","IMPRINT",FACE,{"disambiguationData":[TD([[makeQuery(id+"F0.imprint","IMPRINT",EDGE,{"derivedFrom":sQuery(id+"F0.wireOp",EDGE,"E1549")}),1.0]])]});
            var Q23;
            Q23=makeQuery(id+"F0.imprint","IMPRINT",FACE,{"disambiguationData":[TD([[makeQuery(id+"F0.imprint","IMPRINT",EDGE,{"derivedFrom":sQuery(id+"F0.wireOp",EDGE,"E1609")}),1.0]])]});
            var Q24;
            Q24=makeQuery(id+"F0.imprint","IMPRINT",FACE,{"disambiguationData":[TD([[makeQuery(id+"F0.imprint","IMPRINT",EDGE,{"derivedFrom":sQuery(id+"F0.wireOp",EDGE,"E1705")}),1.0]])]});
            var Q25;
            Q25=makeQuery(id+"F0.imprint","IMPRINT",FACE,{"disambiguationData":[TD([[makeQuery(id+"F0.imprint","IMPRINT",EDGE,{"derivedFrom":sQuery(id+"F0.wireOp",EDGE,"E1765")}),1.0]])]});
            var Q26;
            Q26=makeQuery(id+"F0.imprint","IMPRINT",FACE,{"disambiguationData":[TD([[makeQuery(id+"F0.imprint","IMPRINT",EDGE,{"derivedFrom":sQuery(id+"F0.wireOp",EDGE,"E1809")}),1.0]])]});
            var Q27;
            Q27=makeQuery(id+"F0.imprint","IMPRINT",FACE,{"disambiguationData":[TD([[makeQuery(id+"F0.imprint","IMPRINT",EDGE,{"derivedFrom":sQuery(id+"F0.wireOp",EDGE,"E1905")}),1.0]])]});
            var Q28;
            Q28=makeQuery(id+"F0.imprint","IMPRINT",FACE,{"disambiguationData":[TD([[makeQuery(id+"F0.imprint","IMPRINT",EDGE,{"derivedFrom":sQuery(id+"F0.wireOp",EDGE,"E1965")}),1.0]])]});
            var Q29;
            Q29=makeQuery(id+"F0.imprint","IMPRINT",FACE,{"disambiguationData":[TD([[makeQuery(id+"F0.imprint","IMPRINT",EDGE,{"derivedFrom":sQuery(id+"F0.wireOp",EDGE,"E2027")}),1.0]])]});
            extrude(context, id + "F1", {"entities" : qUnion([Q0, Q1, Q2, Q3, Q4, Q5, Q6, Q7, Q8, Q9, Q10, Q11, Q12, Q13, Q14, Q15, Q16, Q17, Q18, Q19, Q20, Q21, Q22, Q23, Q24, Q25, Q26, Q27, Q28, Q29]), "depth" : 63.5 * mm, "offsetDistance" : 25.4 * mm});
        }
        {
            var Q0;
            Q0=makeQuery(id+"F1.opExtrude","CAP_FACE",FACE,{"disambiguationData":[OSD([sQuery(id+"F0.wireOp",EDGE,"E1102"),sQuery(id+"F0.wireOp",EDGE,"E1103"),sQuery(id+"F0.wireOp",EDGE,"E1104"),sQuery(id+"F0.wireOp",EDGE,"E1105"),sQuery(id+"F0.wireOp",EDGE,"E1106"),sQuery(id+"F0.wireOp",EDGE,"E1107"),sQuery(id+"F0.wireOp",EDGE,"E1108"),sQuery(id+"F0.wireOp",EDGE,"E1109"),sQuery(id+"F0.wireOp",EDGE,"E1110"),sQuery(id+"F0.wireOp",EDGE,"E1111"),sQuery(id+"F0.wireOp",EDGE,"E1112"),sQuery(id+"F0.wireOp",EDGE,"E1113"),sQuery(id+"F0.wireOp",EDGE,"E1114"),sQuery(id+"F0.wireOp",EDGE,"E1115"),sQuery(id+"F0.wireOp",EDGE,"E1116"),sQuery(id+"F0.wireOp",EDGE,"E1117"),sQuery(id+"F0.wireOp",EDGE,"E1118"),sQuery(id+"F0.wireOp",EDGE,"E1119"),sQuery(id+"F0.wireOp",EDGE,"E1120"),sQuery(id+"F0.wireOp",EDGE,"E1121"),sQuery(id+"F0.wireOp",EDGE,"E1122"),sQuery(id+"F0.wireOp",EDGE,"E1123"),sQuery(id+"F0.wireOp",EDGE,"E1124"),sQuery(id+"F0.wireOp",EDGE,"E1125"),sQuery(id+"F0.wireOp",EDGE,"E1126"),sQuery(id+"F0.wireOp",EDGE,"E1127"),sQuery(id+"F0.wireOp",EDGE,"E1128"),sQuery(id+"F0.wireOp",EDGE,"E1129"),sQuery(id+"F0.wireOp",EDGE,"E1130"),sQuery(id+"F0.wireOp",EDGE,"E1131"),sQuery(id+"F0.wireOp",EDGE,"E1132"),sQuery(id+"F0.wireOp",EDGE,"E1133"),sQuery(id+"F0.wireOp",EDGE,"E1134"),sQuery(id+"F0.wireOp",EDGE,"E1135"),sQuery(id+"F0.wireOp",EDGE,"E1136"),sQuery(id+"F0.wireOp",EDGE,"E1137"),sQuery(id+"F0.wireOp",EDGE,"E1138"),sQuery(id+"F0.wireOp",EDGE,"E1139"),sQuery(id+"F0.wireOp",EDGE,"E1140"),sQuery(id+"F0.wireOp",EDGE,"E1141"),sQuery(id+"F0.wireOp",EDGE,"E1142"),sQuery(id+"F0.wireOp",EDGE,"E1143"),sQuery(id+"F0.wireOp",EDGE,"E1144"),sQuery(id+"F0.wireOp",EDGE,"E1145"),sQuery(id+"F0.wireOp",EDGE,"E1146"),sQuery(id+"F0.wireOp",EDGE,"E1147"),sQuery(id+"F0.wireOp",EDGE,"E1148"),sQuery(id+"F0.wireOp",EDGE,"E1149"),sQuery(id+"F0.wireOp",EDGE,"E1150"),sQuery(id+"F0.wireOp",EDGE,"E1151"),sQuery(id+"F0.wireOp",EDGE,"E1152"),sQuery(id+"F0.wireOp",EDGE,"E1153"),sQuery(id+"F0.wireOp",EDGE,"E1154"),sQuery(id+"F0.wireOp",EDGE,"E1155"),sQuery(id+"F0.wireOp",EDGE,"E1156"),sQuery(id+"F0.wireOp",EDGE,"E1157"),sQuery(id+"F0.wireOp",EDGE,"E1158"),sQuery(id+"F0.wireOp",EDGE,"E1159"),sQuery(id+"F0.wireOp",EDGE,"E1160"),sQuery(id+"F0.wireOp",EDGE,"E1161"),sQuery(id+"F0.wireOp",EDGE,"E1162"),sQuery(id+"F0.wireOp",EDGE,"E1163"),sQuery(id+"F0.wireOp",EDGE,"E1164"),sQuery(id+"F0.wireOp",EDGE,"E1165"),sQuery(id+"F0.wireOp",EDGE,"E1166"),sQuery(id+"F0.wireOp",EDGE,"E1167"),sQuery(id+"F0.wireOp",EDGE,"E1168"),sQuery(id+"F0.wireOp",EDGE,"E1169"),sQuery(id+"F0.wireOp",EDGE,"E1170"),sQuery(id+"F0.wireOp",EDGE,"E1171"),sQuery(id+"F0.wireOp",EDGE,"E1172"),sQuery(id+"F0.wireOp",EDGE,"E1173"),sQuery(id+"F0.wireOp",EDGE,"E1174"),sQuery(id+"F0.wireOp",EDGE,"E1175"),sQuery(id+"F0.wireOp",EDGE,"E1176"),sQuery(id+"F0.wireOp",EDGE,"E1177"),sQuery(id+"F0.wireOp",EDGE,"E1178"),sQuery(id+"F0.wireOp",EDGE,"E1179"),sQuery(id+"F0.wireOp",EDGE,"E1180"),sQuery(id+"F0.wireOp",EDGE,"E1181"),sQuery(id+"F0.wireOp",EDGE,"E1182"),sQuery(id+"F0.wireOp",EDGE,"E1183"),sQuery(id+"F0.wireOp",EDGE,"E1184"),sQuery(id+"F0.wireOp",EDGE,"E1185"),sQuery(id+"F0.wireOp",EDGE,"E1186"),sQuery(id+"F0.wireOp",EDGE,"E1187"),sQuery(id+"F0.wireOp",EDGE,"E1188"),sQuery(id+"F0.wireOp",EDGE,"E1189"),sQuery(id+"F0.wireOp",EDGE,"E1190"),sQuery(id+"F0.wireOp",EDGE,"E1191"),sQuery(id+"F0.wireOp",EDGE,"E1192"),sQuery(id+"F0.wireOp",EDGE,"E1193"),sQuery(id+"F0.wireOp",EDGE,"E1194"),sQuery(id+"F0.wireOp",EDGE,"E1195"),sQuery(id+"F0.wireOp",EDGE,"E1196"),sQuery(id+"F0.wireOp",EDGE,"E1197"),sQuery(id+"F0.wireOp",EDGE,"E1198"),sQuery(id+"F0.wireOp",EDGE,"E1199"),sQuery(id+"F0.wireOp",EDGE,"E1200"),sQuery(id+"F0.wireOp",EDGE,"E1201"),sQuery(id+"F0.wireOp",EDGE,"E1202"),sQuery(id+"F0.wireOp",EDGE,"E1203"),sQuery(id+"F0.wireOp",EDGE,"E1204"),sQuery(id+"F0.wireOp",EDGE,"E1205"),sQuery(id+"F0.wireOp",EDGE,"E1206"),sQuery(id+"F0.wireOp",EDGE,"E1207"),sQuery(id+"F0.wireOp",EDGE,"E1208"),sQuery(id+"F0.wireOp",EDGE,"E1209"),sQuery(id+"F0.wireOp",EDGE,"E1210"),sQuery(id+"F0.wireOp",EDGE,"E1211"),sQuery(id+"F0.wireOp",EDGE,"E1212"),sQuery(id+"F0.wireOp",EDGE,"E1213"),sQuery(id+"F0.wireOp",EDGE,"E1214"),sQuery(id+"F0.wireOp",EDGE,"E1215")])],"isStart":true});
            var Q1;
            Q1=makeQuery(id+"F1.opExtrude","CAP_FACE",FACE,{"disambiguationData":[OSD([sQuery(id+"F0.wireOp",EDGE,"E738"),sQuery(id+"F0.wireOp",EDGE,"E739"),sQuery(id+"F0.wireOp",EDGE,"E740"),sQuery(id+"F0.wireOp",EDGE,"E741"),sQuery(id+"F0.wireOp",EDGE,"E742"),sQuery(id+"F0.wireOp",EDGE,"E743"),sQuery(id+"F0.wireOp",EDGE,"E744"),sQuery(id+"F0.wireOp",EDGE,"E745"),sQuery(id+"F0.wireOp",EDGE,"E746"),sQuery(id+"F0.wireOp",EDGE,"E747"),sQuery(id+"F0.wireOp",EDGE,"E748"),sQuery(id+"F0.wireOp",EDGE,"E749"),sQuery(id+"F0.wireOp",EDGE,"E750"),sQuery(id+"F0.wireOp",EDGE,"E751"),sQuery(id+"F0.wireOp",EDGE,"E752"),sQuery(id+"F0.wireOp",EDGE,"E753"),sQuery(id+"F0.wireOp",EDGE,"E754"),sQuery(id+"F0.wireOp",EDGE,"E755"),sQuery(id+"F0.wireOp",EDGE,"E756"),sQuery(id+"F0.wireOp",EDGE,"E757"),sQuery(id+"F0.wireOp",EDGE,"E758"),sQuery(id+"F0.wireOp",EDGE,"E759"),sQuery(id+"F0.wireOp",EDGE,"E760"),sQuery(id+"F0.wireOp",EDGE,"E761"),sQuery(id+"F0.wireOp",EDGE,"E762"),sQuery(id+"F0.wireOp",EDGE,"E763"),sQuery(id+"F0.wireOp",EDGE,"E764"),sQuery(id+"F0.wireOp",EDGE,"E765"),sQuery(id+"F0.wireOp",EDGE,"E766"),sQuery(id+"F0.wireOp",EDGE,"E767"),sQuery(id+"F0.wireOp",EDGE,"E768"),sQuery(id+"F0.wireOp",EDGE,"E769"),sQuery(id+"F0.wireOp",EDGE,"E770"),sQuery(id+"F0.wireOp",EDGE,"E771"),sQuery(id+"F0.wireOp",EDGE,"E772"),sQuery(id+"F0.wireOp",EDGE,"E773"),sQuery(id+"F0.wireOp",EDGE,"E774"),sQuery(id+"F0.wireOp",EDGE,"E775"),sQuery(id+"F0.wireOp",EDGE,"E776"),sQuery(id+"F0.wireOp",EDGE,"E777"),sQuery(id+"F0.wireOp",EDGE,"E778"),sQuery(id+"F0.wireOp",EDGE,"E779"),sQuery(id+"F0.wireOp",EDGE,"E780"),sQuery(id+"F0.wireOp",EDGE,"E781"),sQuery(id+"F0.wireOp",EDGE,"E782"),sQuery(id+"F0.wireOp",EDGE,"E783"),sQuery(id+"F0.wireOp",EDGE,"E784"),sQuery(id+"F0.wireOp",EDGE,"E785"),sQuery(id+"F0.wireOp",EDGE,"E786"),sQuery(id+"F0.wireOp",EDGE,"E787"),sQuery(id+"F0.wireOp",EDGE,"E788"),sQuery(id+"F0.wireOp",EDGE,"E789"),sQuery(id+"F0.wireOp",EDGE,"E790"),sQuery(id+"F0.wireOp",EDGE,"E791"),sQuery(id+"F0.wireOp",EDGE,"E792"),sQuery(id+"F0.wireOp",EDGE,"E793"),sQuery(id+"F0.wireOp",EDGE,"E794"),sQuery(id+"F0.wireOp",EDGE,"E795"),sQuery(id+"F0.wireOp",EDGE,"E796"),sQuery(id+"F0.wireOp",EDGE,"E797"),sQuery(id+"F0.wireOp",EDGE,"E798"),sQuery(id+"F0.wireOp",EDGE,"E799"),sQuery(id+"F0.wireOp",EDGE,"E800"),sQuery(id+"F0.wireOp",EDGE,"E801"),sQuery(id+"F0.wireOp",EDGE,"E802"),sQuery(id+"F0.wireOp",EDGE,"E803"),sQuery(id+"F0.wireOp",EDGE,"E804"),sQuery(id+"F0.wireOp",EDGE,"E805"),sQuery(id+"F0.wireOp",EDGE,"E806"),sQuery(id+"F0.wireOp",EDGE,"E807"),sQuery(id+"F0.wireOp",EDGE,"E808"),sQuery(id+"F0.wireOp",EDGE,"E809"),sQuery(id+"F0.wireOp",EDGE,"E810"),sQuery(id+"F0.wireOp",EDGE,"E811"),sQuery(id+"F0.wireOp",EDGE,"E812"),sQuery(id+"F0.wireOp",EDGE,"E813"),sQuery(id+"F0.wireOp",EDGE,"E814"),sQuery(id+"F0.wireOp",EDGE,"E815"),sQuery(id+"F0.wireOp",EDGE,"E816"),sQuery(id+"F0.wireOp",EDGE,"E817"),sQuery(id+"F0.wireOp",EDGE,"E818"),sQuery(id+"F0.wireOp",EDGE,"E819"),sQuery(id+"F0.wireOp",EDGE,"E820"),sQuery(id+"F0.wireOp",EDGE,"E821"),sQuery(id+"F0.wireOp",EDGE,"E822"),sQuery(id+"F0.wireOp",EDGE,"E823"),sQuery(id+"F0.wireOp",EDGE,"E824"),sQuery(id+"F0.wireOp",EDGE,"E825"),sQuery(id+"F0.wireOp",EDGE,"E826"),sQuery(id+"F0.wireOp",EDGE,"E827"),sQuery(id+"F0.wireOp",EDGE,"E828"),sQuery(id+"F0.wireOp",EDGE,"E829"),sQuery(id+"F0.wireOp",EDGE,"E830"),sQuery(id+"F0.wireOp",EDGE,"E831"),sQuery(id+"F0.wireOp",EDGE,"E832"),sQuery(id+"F0.wireOp",EDGE,"E833"),sQuery(id+"F0.wireOp",EDGE,"E834"),sQuery(id+"F0.wireOp",EDGE,"E835"),sQuery(id+"F0.wireOp",EDGE,"E836"),sQuery(id+"F0.wireOp",EDGE,"E837"),sQuery(id+"F0.wireOp",EDGE,"E838"),sQuery(id+"F0.wireOp",EDGE,"E839"),sQuery(id+"F0.wireOp",EDGE,"E840"),sQuery(id+"F0.wireOp",EDGE,"E841"),sQuery(id+"F0.wireOp",EDGE,"E842"),sQuery(id+"F0.wireOp",EDGE,"E843"),sQuery(id+"F0.wireOp",EDGE,"E844"),sQuery(id+"F0.wireOp",EDGE,"E845"),sQuery(id+"F0.wireOp",EDGE,"E846"),sQuery(id+"F0.wireOp",EDGE,"E847"),sQuery(id+"F0.wireOp",EDGE,"E848"),sQuery(id+"F0.wireOp",EDGE,"E849"),sQuery(id+"F0.wireOp",EDGE,"E850"),sQuery(id+"F0.wireOp",EDGE,"E851"),sQuery(id+"F0.wireOp",EDGE,"E852"),sQuery(id+"F0.wireOp",EDGE,"E853"),sQuery(id+"F0.wireOp",EDGE,"E854"),sQuery(id+"F0.wireOp",EDGE,"E855"),sQuery(id+"F0.wireOp",EDGE,"E856"),sQuery(id+"F0.wireOp",EDGE,"E857"),sQuery(id+"F0.wireOp",EDGE,"E858"),sQuery(id+"F0.wireOp",EDGE,"E859"),sQuery(id+"F0.wireOp",EDGE,"E860"),sQuery(id+"F0.wireOp",EDGE,"E861"),sQuery(id+"F0.wireOp",EDGE,"E862"),sQuery(id+"F0.wireOp",EDGE,"E863"),sQuery(id+"F0.wireOp",EDGE,"E864"),sQuery(id+"F0.wireOp",EDGE,"E865"),sQuery(id+"F0.wireOp",EDGE,"E866"),sQuery(id+"F0.wireOp",EDGE,"E867"),sQuery(id+"F0.wireOp",EDGE,"E868"),sQuery(id+"F0.wireOp",EDGE,"E869"),sQuery(id+"F0.wireOp",EDGE,"E870"),sQuery(id+"F0.wireOp",EDGE,"E871"),sQuery(id+"F0.wireOp",EDGE,"E872"),sQuery(id+"F0.wireOp",EDGE,"E873"),sQuery(id+"F0.wireOp",EDGE,"E874"),sQuery(id+"F0.wireOp",EDGE,"E875"),sQuery(id+"F0.wireOp",EDGE,"E876"),sQuery(id+"F0.wireOp",EDGE,"E877"),sQuery(id+"F0.wireOp",EDGE,"E878"),sQuery(id+"F0.wireOp",EDGE,"E879"),sQuery(id+"F0.wireOp",EDGE,"E880"),sQuery(id+"F0.wireOp",EDGE,"E881"),sQuery(id+"F0.wireOp",EDGE,"E882"),sQuery(id+"F0.wireOp",EDGE,"E883"),sQuery(id+"F0.wireOp",EDGE,"E884"),sQuery(id+"F0.wireOp",EDGE,"E885"),sQuery(id+"F0.wireOp",EDGE,"E886"),sQuery(id+"F0.wireOp",EDGE,"E887"),sQuery(id+"F0.wireOp",EDGE,"E888"),sQuery(id+"F0.wireOp",EDGE,"E889"),sQuery(id+"F0.wireOp",EDGE,"E890"),sQuery(id+"F0.wireOp",EDGE,"E891"),sQuery(id+"F0.wireOp",EDGE,"E892"),sQuery(id+"F0.wireOp",EDGE,"E893"),sQuery(id+"F0.wireOp",EDGE,"E894"),sQuery(id+"F0.wireOp",EDGE,"E895"),sQuery(id+"F0.wireOp",EDGE,"E896"),sQuery(id+"F0.wireOp",EDGE,"E897"),sQuery(id+"F0.wireOp",EDGE,"E898"),sQuery(id+"F0.wireOp",EDGE,"E899"),sQuery(id+"F0.wireOp",EDGE,"E900"),sQuery(id+"F0.wireOp",EDGE,"E901"),sQuery(id+"F0.wireOp",EDGE,"E902"),sQuery(id+"F0.wireOp",EDGE,"E903"),sQuery(id+"F0.wireOp",EDGE,"E904"),sQuery(id+"F0.wireOp",EDGE,"E905"),sQuery(id+"F0.wireOp",EDGE,"E906"),sQuery(id+"F0.wireOp",EDGE,"E907"),sQuery(id+"F0.wireOp",EDGE,"E908"),sQuery(id+"F0.wireOp",EDGE,"E909"),sQuery(id+"F0.wireOp",EDGE,"E910"),sQuery(id+"F0.wireOp",EDGE,"E911"),sQuery(id+"F0.wireOp",EDGE,"E912"),sQuery(id+"F0.wireOp",EDGE,"E913"),sQuery(id+"F0.wireOp",EDGE,"E914"),sQuery(id+"F0.wireOp",EDGE,"E915"),sQuery(id+"F0.wireOp",EDGE,"E916"),sQuery(id+"F0.wireOp",EDGE,"E917"),sQuery(id+"F0.wireOp",EDGE,"E918"),sQuery(id+"F0.wireOp",EDGE,"E919"),sQuery(id+"F0.wireOp",EDGE,"E920"),sQuery(id+"F0.wireOp",EDGE,"E921"),sQuery(id+"F0.wireOp",EDGE,"E922"),sQuery(id+"F0.wireOp",EDGE,"E923"),sQuery(id+"F0.wireOp",EDGE,"E924"),sQuery(id+"F0.wireOp",EDGE,"E925"),sQuery(id+"F0.wireOp",EDGE,"E926"),sQuery(id+"F0.wireOp",EDGE,"E927"),sQuery(id+"F0.wireOp",EDGE,"E928"),sQuery(id+"F0.wireOp",EDGE,"E929"),sQuery(id+"F0.wireOp",EDGE,"E930"),sQuery(id+"F0.wireOp",EDGE,"E931"),sQuery(id+"F0.wireOp",EDGE,"E932"),sQuery(id+"F0.wireOp",EDGE,"E933"),sQuery(id+"F0.wireOp",EDGE,"E934"),sQuery(id+"F0.wireOp",EDGE,"E935"),sQuery(id+"F0.wireOp",EDGE,"E936"),sQuery(id+"F0.wireOp",EDGE,"E937"),sQuery(id+"F0.wireOp",EDGE,"E938"),sQuery(id+"F0.wireOp",EDGE,"E939"),sQuery(id+"F0.wireOp",EDGE,"E940"),sQuery(id+"F0.wireOp",EDGE,"E941"),sQuery(id+"F0.wireOp",EDGE,"E942"),sQuery(id+"F0.wireOp",EDGE,"E943"),sQuery(id+"F0.wireOp",EDGE,"E944"),sQuery(id+"F0.wireOp",EDGE,"E945"),sQuery(id+"F0.wireOp",EDGE,"E946"),sQuery(id+"F0.wireOp",EDGE,"E947"),sQuery(id+"F0.wireOp",EDGE,"E948"),sQuery(id+"F0.wireOp",EDGE,"E949"),sQuery(id+"F0.wireOp",EDGE,"E950"),sQuery(id+"F0.wireOp",EDGE,"E951"),sQuery(id+"F0.wireOp",EDGE,"E952"),sQuery(id+"F0.wireOp",EDGE,"E953"),sQuery(id+"F0.wireOp",EDGE,"E954"),sQuery(id+"F0.wireOp",EDGE,"E955"),sQuery(id+"F0.wireOp",EDGE,"E956"),sQuery(id+"F0.wireOp",EDGE,"E957"),sQuery(id+"F0.wireOp",EDGE,"E958"),sQuery(id+"F0.wireOp",EDGE,"E959"),sQuery(id+"F0.wireOp",EDGE,"E960"),sQuery(id+"F0.wireOp",EDGE,"E961"),sQuery(id+"F0.wireOp",EDGE,"E962"),sQuery(id+"F0.wireOp",EDGE,"E963"),sQuery(id+"F0.wireOp",EDGE,"E964"),sQuery(id+"F0.wireOp",EDGE,"E965"),sQuery(id+"F0.wireOp",EDGE,"E966"),sQuery(id+"F0.wireOp",EDGE,"E967"),sQuery(id+"F0.wireOp",EDGE,"E968"),sQuery(id+"F0.wireOp",EDGE,"E969"),sQuery(id+"F0.wireOp",EDGE,"E970"),sQuery(id+"F0.wireOp",EDGE,"E971"),sQuery(id+"F0.wireOp",EDGE,"E972"),sQuery(id+"F0.wireOp",EDGE,"E973"),sQuery(id+"F0.wireOp",EDGE,"E974"),sQuery(id+"F0.wireOp",EDGE,"E975"),sQuery(id+"F0.wireOp",EDGE,"E976"),sQuery(id+"F0.wireOp",EDGE,"E977"),sQuery(id+"F0.wireOp",EDGE,"E978"),sQuery(id+"F0.wireOp",EDGE,"E979"),sQuery(id+"F0.wireOp",EDGE,"E980"),sQuery(id+"F0.wireOp",EDGE,"E981"),sQuery(id+"F0.wireOp",EDGE,"E982"),sQuery(id+"F0.wireOp",EDGE,"E983"),sQuery(id+"F0.wireOp",EDGE,"E984"),sQuery(id+"F0.wireOp",EDGE,"E985"),sQuery(id+"F0.wireOp",EDGE,"E986"),sQuery(id+"F0.wireOp",EDGE,"E987"),sQuery(id+"F0.wireOp",EDGE,"E988"),sQuery(id+"F0.wireOp",EDGE,"E989"),sQuery(id+"F0.wireOp",EDGE,"E990"),sQuery(id+"F0.wireOp",EDGE,"E991"),sQuery(id+"F0.wireOp",EDGE,"E992"),sQuery(id+"F0.wireOp",EDGE,"E993"),sQuery(id+"F0.wireOp",EDGE,"E994"),sQuery(id+"F0.wireOp",EDGE,"E995"),sQuery(id+"F0.wireOp",EDGE,"E996"),sQuery(id+"F0.wireOp",EDGE,"E997"),sQuery(id+"F0.wireOp",EDGE,"E998"),sQuery(id+"F0.wireOp",EDGE,"E999"),sQuery(id+"F0.wireOp",EDGE,"E1000"),sQuery(id+"F0.wireOp",EDGE,"E1001"),sQuery(id+"F0.wireOp",EDGE,"E1002"),sQuery(id+"F0.wireOp",EDGE,"E1003"),sQuery(id+"F0.wireOp",EDGE,"E1004"),sQuery(id+"F0.wireOp",EDGE,"E1005"),sQuery(id+"F0.wireOp",EDGE,"E1006"),sQuery(id+"F0.wireOp",EDGE,"E1007"),sQuery(id+"F0.wireOp",EDGE,"E1008"),sQuery(id+"F0.wireOp",EDGE,"E1009"),sQuery(id+"F0.wireOp",EDGE,"E1010"),sQuery(id+"F0.wireOp",EDGE,"E1011"),sQuery(id+"F0.wireOp",EDGE,"E1012"),sQuery(id+"F0.wireOp",EDGE,"E1013"),sQuery(id+"F0.wireOp",EDGE,"E1014"),sQuery(id+"F0.wireOp",EDGE,"E1015"),sQuery(id+"F0.wireOp",EDGE,"E1016"),sQuery(id+"F0.wireOp",EDGE,"E1017"),sQuery(id+"F0.wireOp",EDGE,"E1018"),sQuery(id+"F0.wireOp",EDGE,"E1019"),sQuery(id+"F0.wireOp",EDGE,"E1020"),sQuery(id+"F0.wireOp",EDGE,"E1021"),sQuery(id+"F0.wireOp",EDGE,"E1022"),sQuery(id+"F0.wireOp",EDGE,"E1023"),sQuery(id+"F0.wireOp",EDGE,"E1024"),sQuery(id+"F0.wireOp",EDGE,"E1025"),sQuery(id+"F0.wireOp",EDGE,"E1026"),sQuery(id+"F0.wireOp",EDGE,"E1027"),sQuery(id+"F0.wireOp",EDGE,"E1028"),sQuery(id+"F0.wireOp",EDGE,"E1029"),sQuery(id+"F0.wireOp",EDGE,"E1030"),sQuery(id+"F0.wireOp",EDGE,"E1031"),sQuery(id+"F0.wireOp",EDGE,"E1032"),sQuery(id+"F0.wireOp",EDGE,"E1033"),sQuery(id+"F0.wireOp",EDGE,"E1034"),sQuery(id+"F0.wireOp",EDGE,"E1035"),sQuery(id+"F0.wireOp",EDGE,"E1036"),sQuery(id+"F0.wireOp",EDGE,"E1037"),sQuery(id+"F0.wireOp",EDGE,"E1038"),sQuery(id+"F0.wireOp",EDGE,"E1039"),sQuery(id+"F0.wireOp",EDGE,"E1040"),sQuery(id+"F0.wireOp",EDGE,"E1041"),sQuery(id+"F0.wireOp",EDGE,"E1042"),sQuery(id+"F0.wireOp",EDGE,"E1043"),sQuery(id+"F0.wireOp",EDGE,"E1044"),sQuery(id+"F0.wireOp",EDGE,"E1045"),sQuery(id+"F0.wireOp",EDGE,"E1046"),sQuery(id+"F0.wireOp",EDGE,"E1047"),sQuery(id+"F0.wireOp",EDGE,"E1048"),sQuery(id+"F0.wireOp",EDGE,"E1049"),sQuery(id+"F0.wireOp",EDGE,"E1050"),sQuery(id+"F0.wireOp",EDGE,"E1051"),sQuery(id+"F0.wireOp",EDGE,"E1052"),sQuery(id+"F0.wireOp",EDGE,"E1053"),sQuery(id+"F0.wireOp",EDGE,"E1054"),sQuery(id+"F0.wireOp",EDGE,"E1055"),sQuery(id+"F0.wireOp",EDGE,"E1056"),sQuery(id+"F0.wireOp",EDGE,"E1057"),sQuery(id+"F0.wireOp",EDGE,"E1058"),sQuery(id+"F0.wireOp",EDGE,"E1059"),sQuery(id+"F0.wireOp",EDGE,"E1060"),sQuery(id+"F0.wireOp",EDGE,"E1061"),sQuery(id+"F0.wireOp",EDGE,"E1062"),sQuery(id+"F0.wireOp",EDGE,"E1063"),sQuery(id+"F0.wireOp",EDGE,"E1064"),sQuery(id+"F0.wireOp",EDGE,"E1065"),sQuery(id+"F0.wireOp",EDGE,"E1066"),sQuery(id+"F0.wireOp",EDGE,"E1067"),sQuery(id+"F0.wireOp",EDGE,"E1068"),sQuery(id+"F0.wireOp",EDGE,"E1069"),sQuery(id+"F0.wireOp",EDGE,"E1070"),sQuery(id+"F0.wireOp",EDGE,"E1071"),sQuery(id+"F0.wireOp",EDGE,"E1072"),sQuery(id+"F0.wireOp",EDGE,"E1073"),sQuery(id+"F0.wireOp",EDGE,"E1074"),sQuery(id+"F0.wireOp",EDGE,"E1075"),sQuery(id+"F0.wireOp",EDGE,"E1076"),sQuery(id+"F0.wireOp",EDGE,"E1077"),sQuery(id+"F0.wireOp",EDGE,"E1078"),sQuery(id+"F0.wireOp",EDGE,"E1079"),sQuery(id+"F0.wireOp",EDGE,"E1080"),sQuery(id+"F0.wireOp",EDGE,"E1081"),sQuery(id+"F0.wireOp",EDGE,"E1082"),sQuery(id+"F0.wireOp",EDGE,"E1083"),sQuery(id+"F0.wireOp",EDGE,"E1084"),sQuery(id+"F0.wireOp",EDGE,"E1085"),sQuery(id+"F0.wireOp",EDGE,"E1086"),sQuery(id+"F0.wireOp",EDGE,"E1087"),sQuery(id+"F0.wireOp",EDGE,"E1088"),sQuery(id+"F0.wireOp",EDGE,"E1089"),sQuery(id+"F0.wireOp",EDGE,"E1090"),sQuery(id+"F0.wireOp",EDGE,"E1091"),sQuery(id+"F0.wireOp",EDGE,"E1092"),sQuery(id+"F0.wireOp",EDGE,"E1093"),sQuery(id+"F0.wireOp",EDGE,"E1094"),sQuery(id+"F0.wireOp",EDGE,"E1095"),sQuery(id+"F0.wireOp",EDGE,"E1096"),sQuery(id+"F0.wireOp",EDGE,"E1097"),sQuery(id+"F0.wireOp",EDGE,"E1098"),sQuery(id+"F0.wireOp",EDGE,"E1099"),sQuery(id+"F0.wireOp",EDGE,"E1100"),sQuery(id+"F0.wireOp",EDGE,"E1101")])],"isStart":true});
            var Q2;
            Q2=makeQuery(id+"F1.opExtrude","CAP_FACE",FACE,{"disambiguationData":[OSD([sQuery(id+"F0.wireOp",EDGE,"E660"),sQuery(id+"F0.wireOp",EDGE,"E661"),sQuery(id+"F0.wireOp",EDGE,"E662"),sQuery(id+"F0.wireOp",EDGE,"E663"),sQuery(id+"F0.wireOp",EDGE,"E664"),sQuery(id+"F0.wireOp",EDGE,"E665"),sQuery(id+"F0.wireOp",EDGE,"E666"),sQuery(id+"F0.wireOp",EDGE,"E667"),sQuery(id+"F0.wireOp",EDGE,"E668"),sQuery(id+"F0.wireOp",EDGE,"E669"),sQuery(id+"F0.wireOp",EDGE,"E670"),sQuery(id+"F0.wireOp",EDGE,"E671"),sQuery(id+"F0.wireOp",EDGE,"E672"),sQuery(id+"F0.wireOp",EDGE,"E673"),sQuery(id+"F0.wireOp",EDGE,"E674"),sQuery(id+"F0.wireOp",EDGE,"E675"),sQuery(id+"F0.wireOp",EDGE,"E676"),sQuery(id+"F0.wireOp",EDGE,"E677"),sQuery(id+"F0.wireOp",EDGE,"E678"),sQuery(id+"F0.wireOp",EDGE,"E679"),sQuery(id+"F0.wireOp",EDGE,"E680"),sQuery(id+"F0.wireOp",EDGE,"E681"),sQuery(id+"F0.wireOp",EDGE,"E682"),sQuery(id+"F0.wireOp",EDGE,"E683"),sQuery(id+"F0.wireOp",EDGE,"E684"),sQuery(id+"F0.wireOp",EDGE,"E685"),sQuery(id+"F0.wireOp",EDGE,"E686"),sQuery(id+"F0.wireOp",EDGE,"E687"),sQuery(id+"F0.wireOp",EDGE,"E688"),sQuery(id+"F0.wireOp",EDGE,"E689"),sQuery(id+"F0.wireOp",EDGE,"E690"),sQuery(id+"F0.wireOp",EDGE,"E691"),sQuery(id+"F0.wireOp",EDGE,"E692"),sQuery(id+"F0.wireOp",EDGE,"E693"),sQuery(id+"F0.wireOp",EDGE,"E694"),sQuery(id+"F0.wireOp",EDGE,"E695"),sQuery(id+"F0.wireOp",EDGE,"E696"),sQuery(id+"F0.wireOp",EDGE,"E697"),sQuery(id+"F0.wireOp",EDGE,"E698"),sQuery(id+"F0.wireOp",EDGE,"E699"),sQuery(id+"F0.wireOp",EDGE,"E700"),sQuery(id+"F0.wireOp",EDGE,"E701"),sQuery(id+"F0.wireOp",EDGE,"E702"),sQuery(id+"F0.wireOp",EDGE,"E703"),sQuery(id+"F0.wireOp",EDGE,"E704"),sQuery(id+"F0.wireOp",EDGE,"E705"),sQuery(id+"F0.wireOp",EDGE,"E706"),sQuery(id+"F0.wireOp",EDGE,"E707"),sQuery(id+"F0.wireOp",EDGE,"E708"),sQuery(id+"F0.wireOp",EDGE,"E709"),sQuery(id+"F0.wireOp",EDGE,"E710"),sQuery(id+"F0.wireOp",EDGE,"E711"),sQuery(id+"F0.wireOp",EDGE,"E712"),sQuery(id+"F0.wireOp",EDGE,"E713"),sQuery(id+"F0.wireOp",EDGE,"E714"),sQuery(id+"F0.wireOp",EDGE,"E715"),sQuery(id+"F0.wireOp",EDGE,"E716"),sQuery(id+"F0.wireOp",EDGE,"E717"),sQuery(id+"F0.wireOp",EDGE,"E718"),sQuery(id+"F0.wireOp",EDGE,"E719"),sQuery(id+"F0.wireOp",EDGE,"E720"),sQuery(id+"F0.wireOp",EDGE,"E721"),sQuery(id+"F0.wireOp",EDGE,"E722"),sQuery(id+"F0.wireOp",EDGE,"E723"),sQuery(id+"F0.wireOp",EDGE,"E724"),sQuery(id+"F0.wireOp",EDGE,"E725"),sQuery(id+"F0.wireOp",EDGE,"E726"),sQuery(id+"F0.wireOp",EDGE,"E727"),sQuery(id+"F0.wireOp",EDGE,"E728"),sQuery(id+"F0.wireOp",EDGE,"E729"),sQuery(id+"F0.wireOp",EDGE,"E730"),sQuery(id+"F0.wireOp",EDGE,"E731"),sQuery(id+"F0.wireOp",EDGE,"E732"),sQuery(id+"F0.wireOp",EDGE,"E733"),sQuery(id+"F0.wireOp",EDGE,"E734"),sQuery(id+"F0.wireOp",EDGE,"E735"),sQuery(id+"F0.wireOp",EDGE,"E736"),sQuery(id+"F0.wireOp",EDGE,"E737")])],"isStart":true});
            var Q3;
            Q3=makeQuery(id+"F1.opExtrude","CAP_FACE",FACE,{"disambiguationData":[OSD([sQuery(id+"F0.wireOp",EDGE,"E580"),sQuery(id+"F0.wireOp",EDGE,"E581"),sQuery(id+"F0.wireOp",EDGE,"E582"),sQuery(id+"F0.wireOp",EDGE,"E583"),sQuery(id+"F0.wireOp",EDGE,"E584"),sQuery(id+"F0.wireOp",EDGE,"E585"),sQuery(id+"F0.wireOp",EDGE,"E586"),sQuery(id+"F0.wireOp",EDGE,"E587"),sQuery(id+"F0.wireOp",EDGE,"E588"),sQuery(id+"F0.wireOp",EDGE,"E589"),sQuery(id+"F0.wireOp",EDGE,"E590"),sQuery(id+"F0.wireOp",EDGE,"E591"),sQuery(id+"F0.wireOp",EDGE,"E592"),sQuery(id+"F0.wireOp",EDGE,"E593"),sQuery(id+"F0.wireOp",EDGE,"E594"),sQuery(id+"F0.wireOp",EDGE,"E595"),sQuery(id+"F0.wireOp",EDGE,"E596"),sQuery(id+"F0.wireOp",EDGE,"E597"),sQuery(id+"F0.wireOp",EDGE,"E598"),sQuery(id+"F0.wireOp",EDGE,"E599"),sQuery(id+"F0.wireOp",EDGE,"E600"),sQuery(id+"F0.wireOp",EDGE,"E601"),sQuery(id+"F0.wireOp",EDGE,"E602"),sQuery(id+"F0.wireOp",EDGE,"E603"),sQuery(id+"F0.wireOp",EDGE,"E604"),sQuery(id+"F0.wireOp",EDGE,"E605"),sQuery(id+"F0.wireOp",EDGE,"E606"),sQuery(id+"F0.wireOp",EDGE,"E607"),sQuery(id+"F0.wireOp",EDGE,"E608"),sQuery(id+"F0.wireOp",EDGE,"E609"),sQuery(id+"F0.wireOp",EDGE,"E610"),sQuery(id+"F0.wireOp",EDGE,"E611"),sQuery(id+"F0.wireOp",EDGE,"E612"),sQuery(id+"F0.wireOp",EDGE,"E613"),sQuery(id+"F0.wireOp",EDGE,"E614"),sQuery(id+"F0.wireOp",EDGE,"E615"),sQuery(id+"F0.wireOp",EDGE,"E616"),sQuery(id+"F0.wireOp",EDGE,"E617"),sQuery(id+"F0.wireOp",EDGE,"E618"),sQuery(id+"F0.wireOp",EDGE,"E619"),sQuery(id+"F0.wireOp",EDGE,"E620"),sQuery(id+"F0.wireOp",EDGE,"E621"),sQuery(id+"F0.wireOp",EDGE,"E622"),sQuery(id+"F0.wireOp",EDGE,"E623"),sQuery(id+"F0.wireOp",EDGE,"E624"),sQuery(id+"F0.wireOp",EDGE,"E625"),sQuery(id+"F0.wireOp",EDGE,"E626"),sQuery(id+"F0.wireOp",EDGE,"E627"),sQuery(id+"F0.wireOp",EDGE,"E628"),sQuery(id+"F0.wireOp",EDGE,"E629"),sQuery(id+"F0.wireOp",EDGE,"E630"),sQuery(id+"F0.wireOp",EDGE,"E631"),sQuery(id+"F0.wireOp",EDGE,"E632"),sQuery(id+"F0.wireOp",EDGE,"E633"),sQuery(id+"F0.wireOp",EDGE,"E634"),sQuery(id+"F0.wireOp",EDGE,"E635"),sQuery(id+"F0.wireOp",EDGE,"E636"),sQuery(id+"F0.wireOp",EDGE,"E637"),sQuery(id+"F0.wireOp",EDGE,"E638"),sQuery(id+"F0.wireOp",EDGE,"E639"),sQuery(id+"F0.wireOp",EDGE,"E640"),sQuery(id+"F0.wireOp",EDGE,"E641"),sQuery(id+"F0.wireOp",EDGE,"E642"),sQuery(id+"F0.wireOp",EDGE,"E643"),sQuery(id+"F0.wireOp",EDGE,"E644"),sQuery(id+"F0.wireOp",EDGE,"E645"),sQuery(id+"F0.wireOp",EDGE,"E646"),sQuery(id+"F0.wireOp",EDGE,"E647"),sQuery(id+"F0.wireOp",EDGE,"E648"),sQuery(id+"F0.wireOp",EDGE,"E649"),sQuery(id+"F0.wireOp",EDGE,"E650"),sQuery(id+"F0.wireOp",EDGE,"E651"),sQuery(id+"F0.wireOp",EDGE,"E652"),sQuery(id+"F0.wireOp",EDGE,"E653"),sQuery(id+"F0.wireOp",EDGE,"E654"),sQuery(id+"F0.wireOp",EDGE,"E655"),sQuery(id+"F0.wireOp",EDGE,"E656"),sQuery(id+"F0.wireOp",EDGE,"E657"),sQuery(id+"F0.wireOp",EDGE,"E658"),sQuery(id+"F0.wireOp",EDGE,"E659")])],"isStart":true});
            var Q4;
            Q4=makeQuery(id+"F1.opExtrude","CAP_FACE",FACE,{"disambiguationData":[OSD([sQuery(id+"F0.wireOp",EDGE,"E290"),sQuery(id+"F0.wireOp",EDGE,"E291"),sQuery(id+"F0.wireOp",EDGE,"E292"),sQuery(id+"F0.wireOp",EDGE,"E293"),sQuery(id+"F0.wireOp",EDGE,"E294"),sQuery(id+"F0.wireOp",EDGE,"E295"),sQuery(id+"F0.wireOp",EDGE,"E296"),sQuery(id+"F0.wireOp",EDGE,"E297"),sQuery(id+"F0.wireOp",EDGE,"E298"),sQuery(id+"F0.wireOp",EDGE,"E299"),sQuery(id+"F0.wireOp",EDGE,"E300"),sQuery(id+"F0.wireOp",EDGE,"E301"),sQuery(id+"F0.wireOp",EDGE,"E302"),sQuery(id+"F0.wireOp",EDGE,"E303"),sQuery(id+"F0.wireOp",EDGE,"E304"),sQuery(id+"F0.wireOp",EDGE,"E305"),sQuery(id+"F0.wireOp",EDGE,"E306"),sQuery(id+"F0.wireOp",EDGE,"E307"),sQuery(id+"F0.wireOp",EDGE,"E308"),sQuery(id+"F0.wireOp",EDGE,"E309"),sQuery(id+"F0.wireOp",EDGE,"E310"),sQuery(id+"F0.wireOp",EDGE,"E311"),sQuery(id+"F0.wireOp",EDGE,"E312"),sQuery(id+"F0.wireOp",EDGE,"E313"),sQuery(id+"F0.wireOp",EDGE,"E314"),sQuery(id+"F0.wireOp",EDGE,"E315"),sQuery(id+"F0.wireOp",EDGE,"E316"),sQuery(id+"F0.wireOp",EDGE,"E317"),sQuery(id+"F0.wireOp",EDGE,"E318"),sQuery(id+"F0.wireOp",EDGE,"E319"),sQuery(id+"F0.wireOp",EDGE,"E320"),sQuery(id+"F0.wireOp",EDGE,"E321"),sQuery(id+"F0.wireOp",EDGE,"E322"),sQuery(id+"F0.wireOp",EDGE,"E323"),sQuery(id+"F0.wireOp",EDGE,"E324"),sQuery(id+"F0.wireOp",EDGE,"E325"),sQuery(id+"F0.wireOp",EDGE,"E326"),sQuery(id+"F0.wireOp",EDGE,"E327"),sQuery(id+"F0.wireOp",EDGE,"E328"),sQuery(id+"F0.wireOp",EDGE,"E329"),sQuery(id+"F0.wireOp",EDGE,"E330"),sQuery(id+"F0.wireOp",EDGE,"E331"),sQuery(id+"F0.wireOp",EDGE,"E332"),sQuery(id+"F0.wireOp",EDGE,"E333"),sQuery(id+"F0.wireOp",EDGE,"E334"),sQuery(id+"F0.wireOp",EDGE,"E335"),sQuery(id+"F0.wireOp",EDGE,"E336"),sQuery(id+"F0.wireOp",EDGE,"E337"),sQuery(id+"F0.wireOp",EDGE,"E338"),sQuery(id+"F0.wireOp",EDGE,"E339"),sQuery(id+"F0.wireOp",EDGE,"E340"),sQuery(id+"F0.wireOp",EDGE,"E341"),sQuery(id+"F0.wireOp",EDGE,"E342"),sQuery(id+"F0.wireOp",EDGE,"E343"),sQuery(id+"F0.wireOp",EDGE,"E344"),sQuery(id+"F0.wireOp",EDGE,"E345"),sQuery(id+"F0.wireOp",EDGE,"E346"),sQuery(id+"F0.wireOp",EDGE,"E347"),sQuery(id+"F0.wireOp",EDGE,"E348"),sQuery(id+"F0.wireOp",EDGE,"E349"),sQuery(id+"F0.wireOp",EDGE,"E350"),sQuery(id+"F0.wireOp",EDGE,"E351"),sQuery(id+"F0.wireOp",EDGE,"E352"),sQuery(id+"F0.wireOp",EDGE,"E353"),sQuery(id+"F0.wireOp",EDGE,"E354"),sQuery(id+"F0.wireOp",EDGE,"E355"),sQuery(id+"F0.wireOp",EDGE,"E356"),sQuery(id+"F0.wireOp",EDGE,"E357"),sQuery(id+"F0.wireOp",EDGE,"E358"),sQuery(id+"F0.wireOp",EDGE,"E359"),sQuery(id+"F0.wireOp",EDGE,"E360"),sQuery(id+"F0.wireOp",EDGE,"E361"),sQuery(id+"F0.wireOp",EDGE,"E362"),sQuery(id+"F0.wireOp",EDGE,"E363"),sQuery(id+"F0.wireOp",EDGE,"E364"),sQuery(id+"F0.wireOp",EDGE,"E365"),sQuery(id+"F0.wireOp",EDGE,"E366"),sQuery(id+"F0.wireOp",EDGE,"E367"),sQuery(id+"F0.wireOp",EDGE,"E368"),sQuery(id+"F0.wireOp",EDGE,"E369"),sQuery(id+"F0.wireOp",EDGE,"E370"),sQuery(id+"F0.wireOp",EDGE,"E371"),sQuery(id+"F0.wireOp",EDGE,"E372"),sQuery(id+"F0.wireOp",EDGE,"E373"),sQuery(id+"F0.wireOp",EDGE,"E374"),sQuery(id+"F0.wireOp",EDGE,"E375"),sQuery(id+"F0.wireOp",EDGE,"E376"),sQuery(id+"F0.wireOp",EDGE,"E377"),sQuery(id+"F0.wireOp",EDGE,"E378"),sQuery(id+"F0.wireOp",EDGE,"E379"),sQuery(id+"F0.wireOp",EDGE,"E380"),sQuery(id+"F0.wireOp",EDGE,"E381"),sQuery(id+"F0.wireOp",EDGE,"E382"),sQuery(id+"F0.wireOp",EDGE,"E383"),sQuery(id+"F0.wireOp",EDGE,"E384"),sQuery(id+"F0.wireOp",EDGE,"E385"),sQuery(id+"F0.wireOp",EDGE,"E386"),sQuery(id+"F0.wireOp",EDGE,"E387"),sQuery(id+"F0.wireOp",EDGE,"E388"),sQuery(id+"F0.wireOp",EDGE,"E389"),sQuery(id+"F0.wireOp",EDGE,"E390"),sQuery(id+"F0.wireOp",EDGE,"E391"),sQuery(id+"F0.wireOp",EDGE,"E392"),sQuery(id+"F0.wireOp",EDGE,"E393"),sQuery(id+"F0.wireOp",EDGE,"E394"),sQuery(id+"F0.wireOp",EDGE,"E395"),sQuery(id+"F0.wireOp",EDGE,"E396"),sQuery(id+"F0.wireOp",EDGE,"E397"),sQuery(id+"F0.wireOp",EDGE,"E398"),sQuery(id+"F0.wireOp",EDGE,"E399"),sQuery(id+"F0.wireOp",EDGE,"E400"),sQuery(id+"F0.wireOp",EDGE,"E401"),sQuery(id+"F0.wireOp",EDGE,"E402"),sQuery(id+"F0.wireOp",EDGE,"E403"),sQuery(id+"F0.wireOp",EDGE,"E404"),sQuery(id+"F0.wireOp",EDGE,"E405"),sQuery(id+"F0.wireOp",EDGE,"E406"),sQuery(id+"F0.wireOp",EDGE,"E407"),sQuery(id+"F0.wireOp",EDGE,"E408"),sQuery(id+"F0.wireOp",EDGE,"E409"),sQuery(id+"F0.wireOp",EDGE,"E410"),sQuery(id+"F0.wireOp",EDGE,"E411"),sQuery(id+"F0.wireOp",EDGE,"E412"),sQuery(id+"F0.wireOp",EDGE,"E413"),sQuery(id+"F0.wireOp",EDGE,"E414"),sQuery(id+"F0.wireOp",EDGE,"E415"),sQuery(id+"F0.wireOp",EDGE,"E416"),sQuery(id+"F0.wireOp",EDGE,"E417"),sQuery(id+"F0.wireOp",EDGE,"E418"),sQuery(id+"F0.wireOp",EDGE,"E419"),sQuery(id+"F0.wireOp",EDGE,"E420"),sQuery(id+"F0.wireOp",EDGE,"E421"),sQuery(id+"F0.wireOp",EDGE,"E422"),sQuery(id+"F0.wireOp",EDGE,"E423"),sQuery(id+"F0.wireOp",EDGE,"E424"),sQuery(id+"F0.wireOp",EDGE,"E425"),sQuery(id+"F0.wireOp",EDGE,"E426"),sQuery(id+"F0.wireOp",EDGE,"E427"),sQuery(id+"F0.wireOp",EDGE,"E428"),sQuery(id+"F0.wireOp",EDGE,"E429"),sQuery(id+"F0.wireOp",EDGE,"E430"),sQuery(id+"F0.wireOp",EDGE,"E431"),sQuery(id+"F0.wireOp",EDGE,"E432"),sQuery(id+"F0.wireOp",EDGE,"E433"),sQuery(id+"F0.wireOp",EDGE,"E434"),sQuery(id+"F0.wireOp",EDGE,"E435"),sQuery(id+"F0.wireOp",EDGE,"E436"),sQuery(id+"F0.wireOp",EDGE,"E437"),sQuery(id+"F0.wireOp",EDGE,"E438"),sQuery(id+"F0.wireOp",EDGE,"E439"),sQuery(id+"F0.wireOp",EDGE,"E440"),sQuery(id+"F0.wireOp",EDGE,"E441"),sQuery(id+"F0.wireOp",EDGE,"E442"),sQuery(id+"F0.wireOp",EDGE,"E443"),sQuery(id+"F0.wireOp",EDGE,"E444"),sQuery(id+"F0.wireOp",EDGE,"E445"),sQuery(id+"F0.wireOp",EDGE,"E446"),sQuery(id+"F0.wireOp",EDGE,"E447"),sQuery(id+"F0.wireOp",EDGE,"E448"),sQuery(id+"F0.wireOp",EDGE,"E449"),sQuery(id+"F0.wireOp",EDGE,"E450"),sQuery(id+"F0.wireOp",EDGE,"E451"),sQuery(id+"F0.wireOp",EDGE,"E452"),sQuery(id+"F0.wireOp",EDGE,"E453"),sQuery(id+"F0.wireOp",EDGE,"E454"),sQuery(id+"F0.wireOp",EDGE,"E455"),sQuery(id+"F0.wireOp",EDGE,"E456"),sQuery(id+"F0.wireOp",EDGE,"E457"),sQuery(id+"F0.wireOp",EDGE,"E458"),sQuery(id+"F0.wireOp",EDGE,"E459"),sQuery(id+"F0.wireOp",EDGE,"E460"),sQuery(id+"F0.wireOp",EDGE,"E461"),sQuery(id+"F0.wireOp",EDGE,"E462"),sQuery(id+"F0.wireOp",EDGE,"E463"),sQuery(id+"F0.wireOp",EDGE,"E464"),sQuery(id+"F0.wireOp",EDGE,"E465"),sQuery(id+"F0.wireOp",EDGE,"E466"),sQuery(id+"F0.wireOp",EDGE,"E467"),sQuery(id+"F0.wireOp",EDGE,"E468"),sQuery(id+"F0.wireOp",EDGE,"E469"),sQuery(id+"F0.wireOp",EDGE,"E470"),sQuery(id+"F0.wireOp",EDGE,"E471"),sQuery(id+"F0.wireOp",EDGE,"E472"),sQuery(id+"F0.wireOp",EDGE,"E473"),sQuery(id+"F0.wireOp",EDGE,"E474"),sQuery(id+"F0.wireOp",EDGE,"E475"),sQuery(id+"F0.wireOp",EDGE,"E476"),sQuery(id+"F0.wireOp",EDGE,"E477"),sQuery(id+"F0.wireOp",EDGE,"E478"),sQuery(id+"F0.wireOp",EDGE,"E479"),sQuery(id+"F0.wireOp",EDGE,"E480"),sQuery(id+"F0.wireOp",EDGE,"E481"),sQuery(id+"F0.wireOp",EDGE,"E482"),sQuery(id+"F0.wireOp",EDGE,"E483"),sQuery(id+"F0.wireOp",EDGE,"E484"),sQuery(id+"F0.wireOp",EDGE,"E485"),sQuery(id+"F0.wireOp",EDGE,"E486"),sQuery(id+"F0.wireOp",EDGE,"E487"),sQuery(id+"F0.wireOp",EDGE,"E488"),sQuery(id+"F0.wireOp",EDGE,"E489"),sQuery(id+"F0.wireOp",EDGE,"E490"),sQuery(id+"F0.wireOp",EDGE,"E491"),sQuery(id+"F0.wireOp",EDGE,"E492"),sQuery(id+"F0.wireOp",EDGE,"E493"),sQuery(id+"F0.wireOp",EDGE,"E494"),sQuery(id+"F0.wireOp",EDGE,"E495"),sQuery(id+"F0.wireOp",EDGE,"E496"),sQuery(id+"F0.wireOp",EDGE,"E497"),sQuery(id+"F0.wireOp",EDGE,"E498"),sQuery(id+"F0.wireOp",EDGE,"E499"),sQuery(id+"F0.wireOp",EDGE,"E500"),sQuery(id+"F0.wireOp",EDGE,"E501"),sQuery(id+"F0.wireOp",EDGE,"E502"),sQuery(id+"F0.wireOp",EDGE,"E503"),sQuery(id+"F0.wireOp",EDGE,"E504"),sQuery(id+"F0.wireOp",EDGE,"E505"),sQuery(id+"F0.wireOp",EDGE,"E506"),sQuery(id+"F0.wireOp",EDGE,"E507"),sQuery(id+"F0.wireOp",EDGE,"E508"),sQuery(id+"F0.wireOp",EDGE,"E509"),sQuery(id+"F0.wireOp",EDGE,"E510"),sQuery(id+"F0.wireOp",EDGE,"E511"),sQuery(id+"F0.wireOp",EDGE,"E512"),sQuery(id+"F0.wireOp",EDGE,"E513"),sQuery(id+"F0.wireOp",EDGE,"E514"),sQuery(id+"F0.wireOp",EDGE,"E515"),sQuery(id+"F0.wireOp",EDGE,"E516"),sQuery(id+"F0.wireOp",EDGE,"E517"),sQuery(id+"F0.wireOp",EDGE,"E518"),sQuery(id+"F0.wireOp",EDGE,"E519"),sQuery(id+"F0.wireOp",EDGE,"E520"),sQuery(id+"F0.wireOp",EDGE,"E521"),sQuery(id+"F0.wireOp",EDGE,"E522"),sQuery(id+"F0.wireOp",EDGE,"E523"),sQuery(id+"F0.wireOp",EDGE,"E524"),sQuery(id+"F0.wireOp",EDGE,"E525"),sQuery(id+"F0.wireOp",EDGE,"E526"),sQuery(id+"F0.wireOp",EDGE,"E527"),sQuery(id+"F0.wireOp",EDGE,"E528"),sQuery(id+"F0.wireOp",EDGE,"E529"),sQuery(id+"F0.wireOp",EDGE,"E530"),sQuery(id+"F0.wireOp",EDGE,"E531"),sQuery(id+"F0.wireOp",EDGE,"E532"),sQuery(id+"F0.wireOp",EDGE,"E533"),sQuery(id+"F0.wireOp",EDGE,"E534"),sQuery(id+"F0.wireOp",EDGE,"E535"),sQuery(id+"F0.wireOp",EDGE,"E536"),sQuery(id+"F0.wireOp",EDGE,"E537"),sQuery(id+"F0.wireOp",EDGE,"E538"),sQuery(id+"F0.wireOp",EDGE,"E539"),sQuery(id+"F0.wireOp",EDGE,"E540"),sQuery(id+"F0.wireOp",EDGE,"E541"),sQuery(id+"F0.wireOp",EDGE,"E542"),sQuery(id+"F0.wireOp",EDGE,"E543"),sQuery(id+"F0.wireOp",EDGE,"E544"),sQuery(id+"F0.wireOp",EDGE,"E545"),sQuery(id+"F0.wireOp",EDGE,"E546"),sQuery(id+"F0.wireOp",EDGE,"E547"),sQuery(id+"F0.wireOp",EDGE,"E548"),sQuery(id+"F0.wireOp",EDGE,"E549"),sQuery(id+"F0.wireOp",EDGE,"E550"),sQuery(id+"F0.wireOp",EDGE,"E551"),sQuery(id+"F0.wireOp",EDGE,"E552"),sQuery(id+"F0.wireOp",EDGE,"E553"),sQuery(id+"F0.wireOp",EDGE,"E554"),sQuery(id+"F0.wireOp",EDGE,"E555"),sQuery(id+"F0.wireOp",EDGE,"E556"),sQuery(id+"F0.wireOp",EDGE,"E557"),sQuery(id+"F0.wireOp",EDGE,"E558"),sQuery(id+"F0.wireOp",EDGE,"E559"),sQuery(id+"F0.wireOp",EDGE,"E560"),sQuery(id+"F0.wireOp",EDGE,"E561"),sQuery(id+"F0.wireOp",EDGE,"E562"),sQuery(id+"F0.wireOp",EDGE,"E563"),sQuery(id+"F0.wireOp",EDGE,"E564"),sQuery(id+"F0.wireOp",EDGE,"E565"),sQuery(id+"F0.wireOp",EDGE,"E566"),sQuery(id+"F0.wireOp",EDGE,"E567"),sQuery(id+"F0.wireOp",EDGE,"E568"),sQuery(id+"F0.wireOp",EDGE,"E569"),sQuery(id+"F0.wireOp",EDGE,"E570"),sQuery(id+"F0.wireOp",EDGE,"E571"),sQuery(id+"F0.wireOp",EDGE,"E572"),sQuery(id+"F0.wireOp",EDGE,"E573"),sQuery(id+"F0.wireOp",EDGE,"E574"),sQuery(id+"F0.wireOp",EDGE,"E575"),sQuery(id+"F0.wireOp",EDGE,"E576"),sQuery(id+"F0.wireOp",EDGE,"E577"),sQuery(id+"F0.wireOp",EDGE,"E578"),sQuery(id+"F0.wireOp",EDGE,"E579")])],"isStart":true});
            var Q5;
            Q5=makeQuery(id+"F1.opExtrude","CAP_FACE",FACE,{"disambiguationData":[OSD([sQuery(id+"F0.wireOp",EDGE,"E208"),sQuery(id+"F0.wireOp",EDGE,"E209"),sQuery(id+"F0.wireOp",EDGE,"E210"),sQuery(id+"F0.wireOp",EDGE,"E211"),sQuery(id+"F0.wireOp",EDGE,"E212"),sQuery(id+"F0.wireOp",EDGE,"E213"),sQuery(id+"F0.wireOp",EDGE,"E214"),sQuery(id+"F0.wireOp",EDGE,"E215"),sQuery(id+"F0.wireOp",EDGE,"E216"),sQuery(id+"F0.wireOp",EDGE,"E217")])],"isStart":true});
            var Q6;
            Q6=makeQuery(id+"F1.opExtrude","CAP_FACE",FACE,{"disambiguationData":[OSD([sQuery(id+"F0.wireOp",EDGE,"E218"),sQuery(id+"F0.wireOp",EDGE,"E219"),sQuery(id+"F0.wireOp",EDGE,"E220"),sQuery(id+"F0.wireOp",EDGE,"E221"),sQuery(id+"F0.wireOp",EDGE,"E222"),sQuery(id+"F0.wireOp",EDGE,"E223"),sQuery(id+"F0.wireOp",EDGE,"E224"),sQuery(id+"F0.wireOp",EDGE,"E225"),sQuery(id+"F0.wireOp",EDGE,"E226"),sQuery(id+"F0.wireOp",EDGE,"E227"),sQuery(id+"F0.wireOp",EDGE,"E228"),sQuery(id+"F0.wireOp",EDGE,"E229"),sQuery(id+"F0.wireOp",EDGE,"E230"),sQuery(id+"F0.wireOp",EDGE,"E231"),sQuery(id+"F0.wireOp",EDGE,"E232"),sQuery(id+"F0.wireOp",EDGE,"E233"),sQuery(id+"F0.wireOp",EDGE,"E234"),sQuery(id+"F0.wireOp",EDGE,"E235"),sQuery(id+"F0.wireOp",EDGE,"E236"),sQuery(id+"F0.wireOp",EDGE,"E237"),sQuery(id+"F0.wireOp",EDGE,"E238"),sQuery(id+"F0.wireOp",EDGE,"E239"),sQuery(id+"F0.wireOp",EDGE,"E240"),sQuery(id+"F0.wireOp",EDGE,"E241"),sQuery(id+"F0.wireOp",EDGE,"E242"),sQuery(id+"F0.wireOp",EDGE,"E243"),sQuery(id+"F0.wireOp",EDGE,"E244"),sQuery(id+"F0.wireOp",EDGE,"E245"),sQuery(id+"F0.wireOp",EDGE,"E246"),sQuery(id+"F0.wireOp",EDGE,"E247"),sQuery(id+"F0.wireOp",EDGE,"E248"),sQuery(id+"F0.wireOp",EDGE,"E249"),sQuery(id+"F0.wireOp",EDGE,"E250"),sQuery(id+"F0.wireOp",EDGE,"E251"),sQuery(id+"F0.wireOp",EDGE,"E252"),sQuery(id+"F0.wireOp",EDGE,"E253"),sQuery(id+"F0.wireOp",EDGE,"E254"),sQuery(id+"F0.wireOp",EDGE,"E255"),sQuery(id+"F0.wireOp",EDGE,"E256"),sQuery(id+"F0.wireOp",EDGE,"E257"),sQuery(id+"F0.wireOp",EDGE,"E258"),sQuery(id+"F0.wireOp",EDGE,"E259"),sQuery(id+"F0.wireOp",EDGE,"E260"),sQuery(id+"F0.wireOp",EDGE,"E261"),sQuery(id+"F0.wireOp",EDGE,"E262"),sQuery(id+"F0.wireOp",EDGE,"E263"),sQuery(id+"F0.wireOp",EDGE,"E264"),sQuery(id+"F0.wireOp",EDGE,"E265"),sQuery(id+"F0.wireOp",EDGE,"E266"),sQuery(id+"F0.wireOp",EDGE,"E267"),sQuery(id+"F0.wireOp",EDGE,"E268"),sQuery(id+"F0.wireOp",EDGE,"E269"),sQuery(id+"F0.wireOp",EDGE,"E270"),sQuery(id+"F0.wireOp",EDGE,"E271"),sQuery(id+"F0.wireOp",EDGE,"E272"),sQuery(id+"F0.wireOp",EDGE,"E273"),sQuery(id+"F0.wireOp",EDGE,"E274"),sQuery(id+"F0.wireOp",EDGE,"E275"),sQuery(id+"F0.wireOp",EDGE,"E276"),sQuery(id+"F0.wireOp",EDGE,"E277"),sQuery(id+"F0.wireOp",EDGE,"E278"),sQuery(id+"F0.wireOp",EDGE,"E279"),sQuery(id+"F0.wireOp",EDGE,"E280"),sQuery(id+"F0.wireOp",EDGE,"E281"),sQuery(id+"F0.wireOp",EDGE,"E282"),sQuery(id+"F0.wireOp",EDGE,"E283"),sQuery(id+"F0.wireOp",EDGE,"E284"),sQuery(id+"F0.wireOp",EDGE,"E285"),sQuery(id+"F0.wireOp",EDGE,"E286"),sQuery(id+"F0.wireOp",EDGE,"E287"),sQuery(id+"F0.wireOp",EDGE,"E288"),sQuery(id+"F0.wireOp",EDGE,"E289")])],"isStart":true});
            var Q7;
            Q7=makeQuery(id+"F1.opExtrude","CAP_FACE",FACE,{"disambiguationData":[OSD([sQuery(id+"F0.wireOp",EDGE,"E118"),sQuery(id+"F0.wireOp",EDGE,"E119"),sQuery(id+"F0.wireOp",EDGE,"E120"),sQuery(id+"F0.wireOp",EDGE,"E121"),sQuery(id+"F0.wireOp",EDGE,"E122"),sQuery(id+"F0.wireOp",EDGE,"E123"),sQuery(id+"F0.wireOp",EDGE,"E124"),sQuery(id+"F0.wireOp",EDGE,"E125"),sQuery(id+"F0.wireOp",EDGE,"E126"),sQuery(id+"F0.wireOp",EDGE,"E127"),sQuery(id+"F0.wireOp",EDGE,"E128"),sQuery(id+"F0.wireOp",EDGE,"E129"),sQuery(id+"F0.wireOp",EDGE,"E130"),sQuery(id+"F0.wireOp",EDGE,"E131"),sQuery(id+"F0.wireOp",EDGE,"E132"),sQuery(id+"F0.wireOp",EDGE,"E133"),sQuery(id+"F0.wireOp",EDGE,"E134"),sQuery(id+"F0.wireOp",EDGE,"E135"),sQuery(id+"F0.wireOp",EDGE,"E136"),sQuery(id+"F0.wireOp",EDGE,"E137"),sQuery(id+"F0.wireOp",EDGE,"E138"),sQuery(id+"F0.wireOp",EDGE,"E139"),sQuery(id+"F0.wireOp",EDGE,"E140"),sQuery(id+"F0.wireOp",EDGE,"E141"),sQuery(id+"F0.wireOp",EDGE,"E142"),sQuery(id+"F0.wireOp",EDGE,"E143"),sQuery(id+"F0.wireOp",EDGE,"E144"),sQuery(id+"F0.wireOp",EDGE,"E145"),sQuery(id+"F0.wireOp",EDGE,"E146"),sQuery(id+"F0.wireOp",EDGE,"E147"),sQuery(id+"F0.wireOp",EDGE,"E148"),sQuery(id+"F0.wireOp",EDGE,"E149"),sQuery(id+"F0.wireOp",EDGE,"E150"),sQuery(id+"F0.wireOp",EDGE,"E151"),sQuery(id+"F0.wireOp",EDGE,"E152"),sQuery(id+"F0.wireOp",EDGE,"E153"),sQuery(id+"F0.wireOp",EDGE,"E154"),sQuery(id+"F0.wireOp",EDGE,"E155"),sQuery(id+"F0.wireOp",EDGE,"E156"),sQuery(id+"F0.wireOp",EDGE,"E157"),sQuery(id+"F0.wireOp",EDGE,"E158"),sQuery(id+"F0.wireOp",EDGE,"E159"),sQuery(id+"F0.wireOp",EDGE,"E160"),sQuery(id+"F0.wireOp",EDGE,"E161"),sQuery(id+"F0.wireOp",EDGE,"E162"),sQuery(id+"F0.wireOp",EDGE,"E163"),sQuery(id+"F0.wireOp",EDGE,"E164"),sQuery(id+"F0.wireOp",EDGE,"E165"),sQuery(id+"F0.wireOp",EDGE,"E166"),sQuery(id+"F0.wireOp",EDGE,"E167"),sQuery(id+"F0.wireOp",EDGE,"E168"),sQuery(id+"F0.wireOp",EDGE,"E169"),sQuery(id+"F0.wireOp",EDGE,"E170"),sQuery(id+"F0.wireOp",EDGE,"E171"),sQuery(id+"F0.wireOp",EDGE,"E172"),sQuery(id+"F0.wireOp",EDGE,"E173"),sQuery(id+"F0.wireOp",EDGE,"E174"),sQuery(id+"F0.wireOp",EDGE,"E175"),sQuery(id+"F0.wireOp",EDGE,"E176"),sQuery(id+"F0.wireOp",EDGE,"E177"),sQuery(id+"F0.wireOp",EDGE,"E178"),sQuery(id+"F0.wireOp",EDGE,"E179"),sQuery(id+"F0.wireOp",EDGE,"E180"),sQuery(id+"F0.wireOp",EDGE,"E181"),sQuery(id+"F0.wireOp",EDGE,"E182"),sQuery(id+"F0.wireOp",EDGE,"E183"),sQuery(id+"F0.wireOp",EDGE,"E184"),sQuery(id+"F0.wireOp",EDGE,"E185"),sQuery(id+"F0.wireOp",EDGE,"E186"),sQuery(id+"F0.wireOp",EDGE,"E187"),sQuery(id+"F0.wireOp",EDGE,"E188"),sQuery(id+"F0.wireOp",EDGE,"E189"),sQuery(id+"F0.wireOp",EDGE,"E190"),sQuery(id+"F0.wireOp",EDGE,"E191"),sQuery(id+"F0.wireOp",EDGE,"E192"),sQuery(id+"F0.wireOp",EDGE,"E193"),sQuery(id+"F0.wireOp",EDGE,"E194"),sQuery(id+"F0.wireOp",EDGE,"E195"),sQuery(id+"F0.wireOp",EDGE,"E196"),sQuery(id+"F0.wireOp",EDGE,"E197"),sQuery(id+"F0.wireOp",EDGE,"E198"),sQuery(id+"F0.wireOp",EDGE,"E199"),sQuery(id+"F0.wireOp",EDGE,"E200"),sQuery(id+"F0.wireOp",EDGE,"E201"),sQuery(id+"F0.wireOp",EDGE,"E202"),sQuery(id+"F0.wireOp",EDGE,"E203"),sQuery(id+"F0.wireOp",EDGE,"E204"),sQuery(id+"F0.wireOp",EDGE,"E205"),sQuery(id+"F0.wireOp",EDGE,"E206"),sQuery(id+"F0.wireOp",EDGE,"E207")])],"isStart":true});
            var Q8;
            Q8=makeQuery(id+"F1.opExtrude","CAP_FACE",FACE,{"disambiguationData":[OSD([sQuery(id+"F0.wireOp",EDGE,"E4"),sQuery(id+"F0.wireOp",EDGE,"E5"),sQuery(id+"F0.wireOp",EDGE,"E6"),sQuery(id+"F0.wireOp",EDGE,"E7"),sQuery(id+"F0.wireOp",EDGE,"E8"),sQuery(id+"F0.wireOp",EDGE,"E9"),sQuery(id+"F0.wireOp",EDGE,"E10"),sQuery(id+"F0.wireOp",EDGE,"E11"),sQuery(id+"F0.wireOp",EDGE,"E12"),sQuery(id+"F0.wireOp",EDGE,"E13"),sQuery(id+"F0.wireOp",EDGE,"E14"),sQuery(id+"F0.wireOp",EDGE,"E15"),sQuery(id+"F0.wireOp",EDGE,"E16"),sQuery(id+"F0.wireOp",EDGE,"E17"),sQuery(id+"F0.wireOp",EDGE,"E18"),sQuery(id+"F0.wireOp",EDGE,"E19"),sQuery(id+"F0.wireOp",EDGE,"E20"),sQuery(id+"F0.wireOp",EDGE,"E21"),sQuery(id+"F0.wireOp",EDGE,"E22"),sQuery(id+"F0.wireOp",EDGE,"E23"),sQuery(id+"F0.wireOp",EDGE,"E24"),sQuery(id+"F0.wireOp",EDGE,"E25"),sQuery(id+"F0.wireOp",EDGE,"E26"),sQuery(id+"F0.wireOp",EDGE,"E27"),sQuery(id+"F0.wireOp",EDGE,"E28"),sQuery(id+"F0.wireOp",EDGE,"E29"),sQuery(id+"F0.wireOp",EDGE,"E30"),sQuery(id+"F0.wireOp",EDGE,"E31"),sQuery(id+"F0.wireOp",EDGE,"E32"),sQuery(id+"F0.wireOp",EDGE,"E33"),sQuery(id+"F0.wireOp",EDGE,"E34"),sQuery(id+"F0.wireOp",EDGE,"E35"),sQuery(id+"F0.wireOp",EDGE,"E36"),sQuery(id+"F0.wireOp",EDGE,"E37"),sQuery(id+"F0.wireOp",EDGE,"E38"),sQuery(id+"F0.wireOp",EDGE,"E39"),sQuery(id+"F0.wireOp",EDGE,"E40"),sQuery(id+"F0.wireOp",EDGE,"E41"),sQuery(id+"F0.wireOp",EDGE,"E42"),sQuery(id+"F0.wireOp",EDGE,"E43"),sQuery(id+"F0.wireOp",EDGE,"E44"),sQuery(id+"F0.wireOp",EDGE,"E45"),sQuery(id+"F0.wireOp",EDGE,"E46"),sQuery(id+"F0.wireOp",EDGE,"E47"),sQuery(id+"F0.wireOp",EDGE,"E48"),sQuery(id+"F0.wireOp",EDGE,"E49"),sQuery(id+"F0.wireOp",EDGE,"E50"),sQuery(id+"F0.wireOp",EDGE,"E51"),sQuery(id+"F0.wireOp",EDGE,"E52"),sQuery(id+"F0.wireOp",EDGE,"E53"),sQuery(id+"F0.wireOp",EDGE,"E54"),sQuery(id+"F0.wireOp",EDGE,"E55"),sQuery(id+"F0.wireOp",EDGE,"E56"),sQuery(id+"F0.wireOp",EDGE,"E57"),sQuery(id+"F0.wireOp",EDGE,"E58"),sQuery(id+"F0.wireOp",EDGE,"E59"),sQuery(id+"F0.wireOp",EDGE,"E60"),sQuery(id+"F0.wireOp",EDGE,"E61"),sQuery(id+"F0.wireOp",EDGE,"E62"),sQuery(id+"F0.wireOp",EDGE,"E63"),sQuery(id+"F0.wireOp",EDGE,"E64"),sQuery(id+"F0.wireOp",EDGE,"E65"),sQuery(id+"F0.wireOp",EDGE,"E66"),sQuery(id+"F0.wireOp",EDGE,"E67"),sQuery(id+"F0.wireOp",EDGE,"E68"),sQuery(id+"F0.wireOp",EDGE,"E69"),sQuery(id+"F0.wireOp",EDGE,"E70"),sQuery(id+"F0.wireOp",EDGE,"E71"),sQuery(id+"F0.wireOp",EDGE,"E72"),sQuery(id+"F0.wireOp",EDGE,"E73"),sQuery(id+"F0.wireOp",EDGE,"E74"),sQuery(id+"F0.wireOp",EDGE,"E75"),sQuery(id+"F0.wireOp",EDGE,"E76"),sQuery(id+"F0.wireOp",EDGE,"E77"),sQuery(id+"F0.wireOp",EDGE,"E78"),sQuery(id+"F0.wireOp",EDGE,"E79"),sQuery(id+"F0.wireOp",EDGE,"E80"),sQuery(id+"F0.wireOp",EDGE,"E81"),sQuery(id+"F0.wireOp",EDGE,"E82"),sQuery(id+"F0.wireOp",EDGE,"E83"),sQuery(id+"F0.wireOp",EDGE,"E84"),sQuery(id+"F0.wireOp",EDGE,"E85"),sQuery(id+"F0.wireOp",EDGE,"E86"),sQuery(id+"F0.wireOp",EDGE,"E87"),sQuery(id+"F0.wireOp",EDGE,"E88"),sQuery(id+"F0.wireOp",EDGE,"E89"),sQuery(id+"F0.wireOp",EDGE,"E90"),sQuery(id+"F0.wireOp",EDGE,"E91"),sQuery(id+"F0.wireOp",EDGE,"E92"),sQuery(id+"F0.wireOp",EDGE,"E93"),sQuery(id+"F0.wireOp",EDGE,"E94"),sQuery(id+"F0.wireOp",EDGE,"E95"),sQuery(id+"F0.wireOp",EDGE,"E96"),sQuery(id+"F0.wireOp",EDGE,"E97"),sQuery(id+"F0.wireOp",EDGE,"E98"),sQuery(id+"F0.wireOp",EDGE,"E99"),sQuery(id+"F0.wireOp",EDGE,"E100"),sQuery(id+"F0.wireOp",EDGE,"E101"),sQuery(id+"F0.wireOp",EDGE,"E102"),sQuery(id+"F0.wireOp",EDGE,"E103"),sQuery(id+"F0.wireOp",EDGE,"E104"),sQuery(id+"F0.wireOp",EDGE,"E105"),sQuery(id+"F0.wireOp",EDGE,"E106"),sQuery(id+"F0.wireOp",EDGE,"E107"),sQuery(id+"F0.wireOp",EDGE,"E108"),sQuery(id+"F0.wireOp",EDGE,"E109"),sQuery(id+"F0.wireOp",EDGE,"E110"),sQuery(id+"F0.wireOp",EDGE,"E111"),sQuery(id+"F0.wireOp",EDGE,"E112"),sQuery(id+"F0.wireOp",EDGE,"E113"),sQuery(id+"F0.wireOp",EDGE,"E114"),sQuery(id+"F0.wireOp",EDGE,"E115"),sQuery(id+"F0.wireOp",EDGE,"E116"),sQuery(id+"F0.wireOp",EDGE,"E117")])],"isStart":true});
            var Q9;
            Q9=makeQuery(id+"F1.opExtrude","CAP_FACE",FACE,{"disambiguationData":[OSD([sQuery(id+"F0.wireOp",EDGE,"E1216"),sQuery(id+"F0.wireOp",EDGE,"E1217"),sQuery(id+"F0.wireOp",EDGE,"E1218"),sQuery(id+"F0.wireOp",EDGE,"E1219"),sQuery(id+"F0.wireOp",EDGE,"E1220"),sQuery(id+"F0.wireOp",EDGE,"E1221"),sQuery(id+"F0.wireOp",EDGE,"E1222"),sQuery(id+"F0.wireOp",EDGE,"E1223"),sQuery(id+"F0.wireOp",EDGE,"E1224"),sQuery(id+"F0.wireOp",EDGE,"E1225"),sQuery(id+"F0.wireOp",EDGE,"E1226"),sQuery(id+"F0.wireOp",EDGE,"E1227"),sQuery(id+"F0.wireOp",EDGE,"E1228"),sQuery(id+"F0.wireOp",EDGE,"E1229"),sQuery(id+"F0.wireOp",EDGE,"E1230"),sQuery(id+"F0.wireOp",EDGE,"E1231"),sQuery(id+"F0.wireOp",EDGE,"E1232"),sQuery(id+"F0.wireOp",EDGE,"E1233"),sQuery(id+"F0.wireOp",EDGE,"E1234"),sQuery(id+"F0.wireOp",EDGE,"E1235"),sQuery(id+"F0.wireOp",EDGE,"E1236"),sQuery(id+"F0.wireOp",EDGE,"E1237"),sQuery(id+"F0.wireOp",EDGE,"E1238"),sQuery(id+"F0.wireOp",EDGE,"E1239"),sQuery(id+"F0.wireOp",EDGE,"E1240"),sQuery(id+"F0.wireOp",EDGE,"E1241"),sQuery(id+"F0.wireOp",EDGE,"E1242"),sQuery(id+"F0.wireOp",EDGE,"E1243"),sQuery(id+"F0.wireOp",EDGE,"E1244"),sQuery(id+"F0.wireOp",EDGE,"E1245"),sQuery(id+"F0.wireOp",EDGE,"E1246"),sQuery(id+"F0.wireOp",EDGE,"E1247"),sQuery(id+"F0.wireOp",EDGE,"E1248"),sQuery(id+"F0.wireOp",EDGE,"E1249"),sQuery(id+"F0.wireOp",EDGE,"E1250"),sQuery(id+"F0.wireOp",EDGE,"E1251"),sQuery(id+"F0.wireOp",EDGE,"E1252"),sQuery(id+"F0.wireOp",EDGE,"E1253"),sQuery(id+"F0.wireOp",EDGE,"E1254"),sQuery(id+"F0.wireOp",EDGE,"E1255"),sQuery(id+"F0.wireOp",EDGE,"E1256"),sQuery(id+"F0.wireOp",EDGE,"E1257"),sQuery(id+"F0.wireOp",EDGE,"E1258"),sQuery(id+"F0.wireOp",EDGE,"E1259"),sQuery(id+"F0.wireOp",EDGE,"E1260"),sQuery(id+"F0.wireOp",EDGE,"E1261"),sQuery(id+"F0.wireOp",EDGE,"E1262"),sQuery(id+"F0.wireOp",EDGE,"E1263"),sQuery(id+"F0.wireOp",EDGE,"E1264"),sQuery(id+"F0.wireOp",EDGE,"E1265"),sQuery(id+"F0.wireOp",EDGE,"E1266"),sQuery(id+"F0.wireOp",EDGE,"E1267"),sQuery(id+"F0.wireOp",EDGE,"E1268"),sQuery(id+"F0.wireOp",EDGE,"E1269"),sQuery(id+"F0.wireOp",EDGE,"E1270"),sQuery(id+"F0.wireOp",EDGE,"E1271"),sQuery(id+"F0.wireOp",EDGE,"E1272"),sQuery(id+"F0.wireOp",EDGE,"E1273"),sQuery(id+"F0.wireOp",EDGE,"E1274"),sQuery(id+"F0.wireOp",EDGE,"E1275"),sQuery(id+"F0.wireOp",EDGE,"E1276"),sQuery(id+"F0.wireOp",EDGE,"E1277"),sQuery(id+"F0.wireOp",EDGE,"E1278"),sQuery(id+"F0.wireOp",EDGE,"E1279"),sQuery(id+"F0.wireOp",EDGE,"E1280"),sQuery(id+"F0.wireOp",EDGE,"E1281"),sQuery(id+"F0.wireOp",EDGE,"E1282"),sQuery(id+"F0.wireOp",EDGE,"E1283"),sQuery(id+"F0.wireOp",EDGE,"E1284"),sQuery(id+"F0.wireOp",EDGE,"E1285"),sQuery(id+"F0.wireOp",EDGE,"E1286"),sQuery(id+"F0.wireOp",EDGE,"E1287"),sQuery(id+"F0.wireOp",EDGE,"E1288"),sQuery(id+"F0.wireOp",EDGE,"E1289"),sQuery(id+"F0.wireOp",EDGE,"E1290"),sQuery(id+"F0.wireOp",EDGE,"E1291"),sQuery(id+"F0.wireOp",EDGE,"E1292"),sQuery(id+"F0.wireOp",EDGE,"E1293"),sQuery(id+"F0.wireOp",EDGE,"E1294"),sQuery(id+"F0.wireOp",EDGE,"E1295"),sQuery(id+"F0.wireOp",EDGE,"E1296"),sQuery(id+"F0.wireOp",EDGE,"E1297"),sQuery(id+"F0.wireOp",EDGE,"E1298"),sQuery(id+"F0.wireOp",EDGE,"E1299"),sQuery(id+"F0.wireOp",EDGE,"E1300"),sQuery(id+"F0.wireOp",EDGE,"E1301"),sQuery(id+"F0.wireOp",EDGE,"E1302"),sQuery(id+"F0.wireOp",EDGE,"E1303"),sQuery(id+"F0.wireOp",EDGE,"E1304"),sQuery(id+"F0.wireOp",EDGE,"E1305"),sQuery(id+"F0.wireOp",EDGE,"E1306"),sQuery(id+"F0.wireOp",EDGE,"E1307"),sQuery(id+"F0.wireOp",EDGE,"E1308"),sQuery(id+"F0.wireOp",EDGE,"E1309"),sQuery(id+"F0.wireOp",EDGE,"E1310"),sQuery(id+"F0.wireOp",EDGE,"E1311"),sQuery(id+"F0.wireOp",EDGE,"E1312"),sQuery(id+"F0.wireOp",EDGE,"E1313"),sQuery(id+"F0.wireOp",EDGE,"E1314"),sQuery(id+"F0.wireOp",EDGE,"E1315"),sQuery(id+"F0.wireOp",EDGE,"E1316"),sQuery(id+"F0.wireOp",EDGE,"E1317"),sQuery(id+"F0.wireOp",EDGE,"E1318"),sQuery(id+"F0.wireOp",EDGE,"E1319"),sQuery(id+"F0.wireOp",EDGE,"E1320"),sQuery(id+"F0.wireOp",EDGE,"E1321"),sQuery(id+"F0.wireOp",EDGE,"E1322"),sQuery(id+"F0.wireOp",EDGE,"E1323"),sQuery(id+"F0.wireOp",EDGE,"E1324"),sQuery(id+"F0.wireOp",EDGE,"E1325"),sQuery(id+"F0.wireOp",EDGE,"E1326"),sQuery(id+"F0.wireOp",EDGE,"E1327"),sQuery(id+"F0.wireOp",EDGE,"E1328"),sQuery(id+"F0.wireOp",EDGE,"E1329"),sQuery(id+"F0.wireOp",EDGE,"E1330"),sQuery(id+"F0.wireOp",EDGE,"E1331"),sQuery(id+"F0.wireOp",EDGE,"E1332"),sQuery(id+"F0.wireOp",EDGE,"E1333"),sQuery(id+"F0.wireOp",EDGE,"E1334"),sQuery(id+"F0.wireOp",EDGE,"E1335"),sQuery(id+"F0.wireOp",EDGE,"E1336"),sQuery(id+"F0.wireOp",EDGE,"E1337"),sQuery(id+"F0.wireOp",EDGE,"E1338"),sQuery(id+"F0.wireOp",EDGE,"E1339"),sQuery(id+"F0.wireOp",EDGE,"E1340"),sQuery(id+"F0.wireOp",EDGE,"E1341"),sQuery(id+"F0.wireOp",EDGE,"E1342"),sQuery(id+"F0.wireOp",EDGE,"E1343"),sQuery(id+"F0.wireOp",EDGE,"E1344"),sQuery(id+"F0.wireOp",EDGE,"E1345"),sQuery(id+"F0.wireOp",EDGE,"E1346"),sQuery(id+"F0.wireOp",EDGE,"E1347"),sQuery(id+"F0.wireOp",EDGE,"E1348"),sQuery(id+"F0.wireOp",EDGE,"E1349"),sQuery(id+"F0.wireOp",EDGE,"E1350"),sQuery(id+"F0.wireOp",EDGE,"E1351"),sQuery(id+"F0.wireOp",EDGE,"E1352"),sQuery(id+"F0.wireOp",EDGE,"E1353"),sQuery(id+"F0.wireOp",EDGE,"E1354"),sQuery(id+"F0.wireOp",EDGE,"E1355"),sQuery(id+"F0.wireOp",EDGE,"E1356"),sQuery(id+"F0.wireOp",EDGE,"E1357"),sQuery(id+"F0.wireOp",EDGE,"E1358"),sQuery(id+"F0.wireOp",EDGE,"E1359"),sQuery(id+"F0.wireOp",EDGE,"E1360"),sQuery(id+"F0.wireOp",EDGE,"E1361"),sQuery(id+"F0.wireOp",EDGE,"E1362"),sQuery(id+"F0.wireOp",EDGE,"E1363"),sQuery(id+"F0.wireOp",EDGE,"E1364"),sQuery(id+"F0.wireOp",EDGE,"E1365"),sQuery(id+"F0.wireOp",EDGE,"E1366"),sQuery(id+"F0.wireOp",EDGE,"E1367"),sQuery(id+"F0.wireOp",EDGE,"E1368"),sQuery(id+"F0.wireOp",EDGE,"E1369"),sQuery(id+"F0.wireOp",EDGE,"E1370"),sQuery(id+"F0.wireOp",EDGE,"E1371"),sQuery(id+"F0.wireOp",EDGE,"E1372"),sQuery(id+"F0.wireOp",EDGE,"E1373"),sQuery(id+"F0.wireOp",EDGE,"E1374"),sQuery(id+"F0.wireOp",EDGE,"E1375"),sQuery(id+"F0.wireOp",EDGE,"E1376"),sQuery(id+"F0.wireOp",EDGE,"E1377"),sQuery(id+"F0.wireOp",EDGE,"E1378"),sQuery(id+"F0.wireOp",EDGE,"E1379"),sQuery(id+"F0.wireOp",EDGE,"E1380"),sQuery(id+"F0.wireOp",EDGE,"E1381"),sQuery(id+"F0.wireOp",EDGE,"E1382"),sQuery(id+"F0.wireOp",EDGE,"E1383"),sQuery(id+"F0.wireOp",EDGE,"E1384"),sQuery(id+"F0.wireOp",EDGE,"E1385"),sQuery(id+"F0.wireOp",EDGE,"E1386"),sQuery(id+"F0.wireOp",EDGE,"E1387"),sQuery(id+"F0.wireOp",EDGE,"E1388"),sQuery(id+"F0.wireOp",EDGE,"E1389"),sQuery(id+"F0.wireOp",EDGE,"E1390"),sQuery(id+"F0.wireOp",EDGE,"E1391"),sQuery(id+"F0.wireOp",EDGE,"E1392"),sQuery(id+"F0.wireOp",EDGE,"E1393"),sQuery(id+"F0.wireOp",EDGE,"E1394"),sQuery(id+"F0.wireOp",EDGE,"E1395"),sQuery(id+"F0.wireOp",EDGE,"E1396"),sQuery(id+"F0.wireOp",EDGE,"E1397"),sQuery(id+"F0.wireOp",EDGE,"E1398"),sQuery(id+"F0.wireOp",EDGE,"E1399"),sQuery(id+"F0.wireOp",EDGE,"E1400"),sQuery(id+"F0.wireOp",EDGE,"E1401"),sQuery(id+"F0.wireOp",EDGE,"E1402"),sQuery(id+"F0.wireOp",EDGE,"E1403"),sQuery(id+"F0.wireOp",EDGE,"E1404")])],"isStart":true});
            var Q10;
            Q10=makeQuery(id+"F1.opExtrude","CAP_FACE",FACE,{"disambiguationData":[OSD([sQuery(id+"F0.wireOp",EDGE,"E1405"),sQuery(id+"F0.wireOp",EDGE,"E1406"),sQuery(id+"F0.wireOp",EDGE,"E1407"),sQuery(id+"F0.wireOp",EDGE,"E1408"),sQuery(id+"F0.wireOp",EDGE,"E1409"),sQuery(id+"F0.wireOp",EDGE,"E1410"),sQuery(id+"F0.wireOp",EDGE,"E1411"),sQuery(id+"F0.wireOp",EDGE,"E1412"),sQuery(id+"F0.wireOp",EDGE,"E1413"),sQuery(id+"F0.wireOp",EDGE,"E1414"),sQuery(id+"F0.wireOp",EDGE,"E1415"),sQuery(id+"F0.wireOp",EDGE,"E1416"),sQuery(id+"F0.wireOp",EDGE,"E1417"),sQuery(id+"F0.wireOp",EDGE,"E1418"),sQuery(id+"F0.wireOp",EDGE,"E1419"),sQuery(id+"F0.wireOp",EDGE,"E1420"),sQuery(id+"F0.wireOp",EDGE,"E1421"),sQuery(id+"F0.wireOp",EDGE,"E1422"),sQuery(id+"F0.wireOp",EDGE,"E1423"),sQuery(id+"F0.wireOp",EDGE,"E1424"),sQuery(id+"F0.wireOp",EDGE,"E1425"),sQuery(id+"F0.wireOp",EDGE,"E1426"),sQuery(id+"F0.wireOp",EDGE,"E1427"),sQuery(id+"F0.wireOp",EDGE,"E1428"),sQuery(id+"F0.wireOp",EDGE,"E1429"),sQuery(id+"F0.wireOp",EDGE,"E1430"),sQuery(id+"F0.wireOp",EDGE,"E1431"),sQuery(id+"F0.wireOp",EDGE,"E1432"),sQuery(id+"F0.wireOp",EDGE,"E1433"),sQuery(id+"F0.wireOp",EDGE,"E1434"),sQuery(id+"F0.wireOp",EDGE,"E1435"),sQuery(id+"F0.wireOp",EDGE,"E1436"),sQuery(id+"F0.wireOp",EDGE,"E1437"),sQuery(id+"F0.wireOp",EDGE,"E1438"),sQuery(id+"F0.wireOp",EDGE,"E1439"),sQuery(id+"F0.wireOp",EDGE,"E1440"),sQuery(id+"F0.wireOp",EDGE,"E1441"),sQuery(id+"F0.wireOp",EDGE,"E1442"),sQuery(id+"F0.wireOp",EDGE,"E1443"),sQuery(id+"F0.wireOp",EDGE,"E1444"),sQuery(id+"F0.wireOp",EDGE,"E1445"),sQuery(id+"F0.wireOp",EDGE,"E1446"),sQuery(id+"F0.wireOp",EDGE,"E1447"),sQuery(id+"F0.wireOp",EDGE,"E1448"),sQuery(id+"F0.wireOp",EDGE,"E1449"),sQuery(id+"F0.wireOp",EDGE,"E1450"),sQuery(id+"F0.wireOp",EDGE,"E1451"),sQuery(id+"F0.wireOp",EDGE,"E1452"),sQuery(id+"F0.wireOp",EDGE,"E1453"),sQuery(id+"F0.wireOp",EDGE,"E1454"),sQuery(id+"F0.wireOp",EDGE,"E1455"),sQuery(id+"F0.wireOp",EDGE,"E1456"),sQuery(id+"F0.wireOp",EDGE,"E1457"),sQuery(id+"F0.wireOp",EDGE,"E1458"),sQuery(id+"F0.wireOp",EDGE,"E1459"),sQuery(id+"F0.wireOp",EDGE,"E1460"),sQuery(id+"F0.wireOp",EDGE,"E1461"),sQuery(id+"F0.wireOp",EDGE,"E1462"),sQuery(id+"F0.wireOp",EDGE,"E1463"),sQuery(id+"F0.wireOp",EDGE,"E1464"),sQuery(id+"F0.wireOp",EDGE,"E1465"),sQuery(id+"F0.wireOp",EDGE,"E1466"),sQuery(id+"F0.wireOp",EDGE,"E1467"),sQuery(id+"F0.wireOp",EDGE,"E1468"),sQuery(id+"F0.wireOp",EDGE,"E1469"),sQuery(id+"F0.wireOp",EDGE,"E1470"),sQuery(id+"F0.wireOp",EDGE,"E1471"),sQuery(id+"F0.wireOp",EDGE,"E1472"),sQuery(id+"F0.wireOp",EDGE,"E1473"),sQuery(id+"F0.wireOp",EDGE,"E1474"),sQuery(id+"F0.wireOp",EDGE,"E1475"),sQuery(id+"F0.wireOp",EDGE,"E1476"),sQuery(id+"F0.wireOp",EDGE,"E1477"),sQuery(id+"F0.wireOp",EDGE,"E1478"),sQuery(id+"F0.wireOp",EDGE,"E1479"),sQuery(id+"F0.wireOp",EDGE,"E1480"),sQuery(id+"F0.wireOp",EDGE,"E1481"),sQuery(id+"F0.wireOp",EDGE,"E1482"),sQuery(id+"F0.wireOp",EDGE,"E1483"),sQuery(id+"F0.wireOp",EDGE,"E1484"),sQuery(id+"F0.wireOp",EDGE,"E1485"),sQuery(id+"F0.wireOp",EDGE,"E1486")])],"isStart":true});
            var Q11;
            Q11=makeQuery(id+"F1.opExtrude","CAP_FACE",FACE,{"disambiguationData":[OSD([sQuery(id+"F0.wireOp",EDGE,"E1549"),sQuery(id+"F0.wireOp",EDGE,"E1550"),sQuery(id+"F0.wireOp",EDGE,"E1551"),sQuery(id+"F0.wireOp",EDGE,"E1552"),sQuery(id+"F0.wireOp",EDGE,"E1553"),sQuery(id+"F0.wireOp",EDGE,"E1554"),sQuery(id+"F0.wireOp",EDGE,"E1555"),sQuery(id+"F0.wireOp",EDGE,"E1556"),sQuery(id+"F0.wireOp",EDGE,"E1557"),sQuery(id+"F0.wireOp",EDGE,"E1558"),sQuery(id+"F0.wireOp",EDGE,"E1559"),sQuery(id+"F0.wireOp",EDGE,"E1560"),sQuery(id+"F0.wireOp",EDGE,"E1561"),sQuery(id+"F0.wireOp",EDGE,"E1562"),sQuery(id+"F0.wireOp",EDGE,"E1563"),sQuery(id+"F0.wireOp",EDGE,"E1564"),sQuery(id+"F0.wireOp",EDGE,"E1565"),sQuery(id+"F0.wireOp",EDGE,"E1566"),sQuery(id+"F0.wireOp",EDGE,"E1567"),sQuery(id+"F0.wireOp",EDGE,"E1568"),sQuery(id+"F0.wireOp",EDGE,"E1569"),sQuery(id+"F0.wireOp",EDGE,"E1570"),sQuery(id+"F0.wireOp",EDGE,"E1571"),sQuery(id+"F0.wireOp",EDGE,"E1572"),sQuery(id+"F0.wireOp",EDGE,"E1573"),sQuery(id+"F0.wireOp",EDGE,"E1574"),sQuery(id+"F0.wireOp",EDGE,"E1575"),sQuery(id+"F0.wireOp",EDGE,"E1576"),sQuery(id+"F0.wireOp",EDGE,"E1577"),sQuery(id+"F0.wireOp",EDGE,"E1578"),sQuery(id+"F0.wireOp",EDGE,"E1579"),sQuery(id+"F0.wireOp",EDGE,"E1580"),sQuery(id+"F0.wireOp",EDGE,"E1581"),sQuery(id+"F0.wireOp",EDGE,"E1582"),sQuery(id+"F0.wireOp",EDGE,"E1583"),sQuery(id+"F0.wireOp",EDGE,"E1584"),sQuery(id+"F0.wireOp",EDGE,"E1585"),sQuery(id+"F0.wireOp",EDGE,"E1586"),sQuery(id+"F0.wireOp",EDGE,"E1587"),sQuery(id+"F0.wireOp",EDGE,"E1588"),sQuery(id+"F0.wireOp",EDGE,"E1589"),sQuery(id+"F0.wireOp",EDGE,"E1590"),sQuery(id+"F0.wireOp",EDGE,"E1591"),sQuery(id+"F0.wireOp",EDGE,"E1592"),sQuery(id+"F0.wireOp",EDGE,"E1593"),sQuery(id+"F0.wireOp",EDGE,"E1594"),sQuery(id+"F0.wireOp",EDGE,"E1595"),sQuery(id+"F0.wireOp",EDGE,"E1596"),sQuery(id+"F0.wireOp",EDGE,"E1597"),sQuery(id+"F0.wireOp",EDGE,"E1598"),sQuery(id+"F0.wireOp",EDGE,"E1599"),sQuery(id+"F0.wireOp",EDGE,"E1600"),sQuery(id+"F0.wireOp",EDGE,"E1601"),sQuery(id+"F0.wireOp",EDGE,"E1602"),sQuery(id+"F0.wireOp",EDGE,"E1603"),sQuery(id+"F0.wireOp",EDGE,"E1604"),sQuery(id+"F0.wireOp",EDGE,"E1605"),sQuery(id+"F0.wireOp",EDGE,"E1606"),sQuery(id+"F0.wireOp",EDGE,"E1607"),sQuery(id+"F0.wireOp",EDGE,"E1608")])],"isStart":true});
            var Q12;
            Q12=makeQuery(id+"F1.opExtrude","CAP_FACE",FACE,{"disambiguationData":[OSD([sQuery(id+"F0.wireOp",EDGE,"E1609"),sQuery(id+"F0.wireOp",EDGE,"E1610"),sQuery(id+"F0.wireOp",EDGE,"E1611"),sQuery(id+"F0.wireOp",EDGE,"E1612"),sQuery(id+"F0.wireOp",EDGE,"E1613"),sQuery(id+"F0.wireOp",EDGE,"E1614"),sQuery(id+"F0.wireOp",EDGE,"E1615"),sQuery(id+"F0.wireOp",EDGE,"E1616"),sQuery(id+"F0.wireOp",EDGE,"E1617"),sQuery(id+"F0.wireOp",EDGE,"E1618"),sQuery(id+"F0.wireOp",EDGE,"E1619"),sQuery(id+"F0.wireOp",EDGE,"E1620"),sQuery(id+"F0.wireOp",EDGE,"E1621"),sQuery(id+"F0.wireOp",EDGE,"E1622"),sQuery(id+"F0.wireOp",EDGE,"E1623"),sQuery(id+"F0.wireOp",EDGE,"E1624"),sQuery(id+"F0.wireOp",EDGE,"E1625"),sQuery(id+"F0.wireOp",EDGE,"E1626"),sQuery(id+"F0.wireOp",EDGE,"E1627"),sQuery(id+"F0.wireOp",EDGE,"E1628"),sQuery(id+"F0.wireOp",EDGE,"E1629"),sQuery(id+"F0.wireOp",EDGE,"E1630"),sQuery(id+"F0.wireOp",EDGE,"E1631"),sQuery(id+"F0.wireOp",EDGE,"E1632"),sQuery(id+"F0.wireOp",EDGE,"E1633"),sQuery(id+"F0.wireOp",EDGE,"E1634"),sQuery(id+"F0.wireOp",EDGE,"E1635"),sQuery(id+"F0.wireOp",EDGE,"E1636"),sQuery(id+"F0.wireOp",EDGE,"E1637"),sQuery(id+"F0.wireOp",EDGE,"E1638"),sQuery(id+"F0.wireOp",EDGE,"E1639"),sQuery(id+"F0.wireOp",EDGE,"E1640"),sQuery(id+"F0.wireOp",EDGE,"E1641"),sQuery(id+"F0.wireOp",EDGE,"E1642"),sQuery(id+"F0.wireOp",EDGE,"E1643"),sQuery(id+"F0.wireOp",EDGE,"E1644"),sQuery(id+"F0.wireOp",EDGE,"E1645"),sQuery(id+"F0.wireOp",EDGE,"E1646"),sQuery(id+"F0.wireOp",EDGE,"E1647"),sQuery(id+"F0.wireOp",EDGE,"E1648"),sQuery(id+"F0.wireOp",EDGE,"E1649"),sQuery(id+"F0.wireOp",EDGE,"E1650"),sQuery(id+"F0.wireOp",EDGE,"E1651"),sQuery(id+"F0.wireOp",EDGE,"E1652"),sQuery(id+"F0.wireOp",EDGE,"E1653"),sQuery(id+"F0.wireOp",EDGE,"E1654"),sQuery(id+"F0.wireOp",EDGE,"E1655"),sQuery(id+"F0.wireOp",EDGE,"E1656"),sQuery(id+"F0.wireOp",EDGE,"E1657"),sQuery(id+"F0.wireOp",EDGE,"E1658"),sQuery(id+"F0.wireOp",EDGE,"E1659"),sQuery(id+"F0.wireOp",EDGE,"E1660"),sQuery(id+"F0.wireOp",EDGE,"E1661"),sQuery(id+"F0.wireOp",EDGE,"E1662"),sQuery(id+"F0.wireOp",EDGE,"E1663"),sQuery(id+"F0.wireOp",EDGE,"E1664"),sQuery(id+"F0.wireOp",EDGE,"E1665"),sQuery(id+"F0.wireOp",EDGE,"E1666"),sQuery(id+"F0.wireOp",EDGE,"E1667"),sQuery(id+"F0.wireOp",EDGE,"E1668"),sQuery(id+"F0.wireOp",EDGE,"E1669"),sQuery(id+"F0.wireOp",EDGE,"E1670"),sQuery(id+"F0.wireOp",EDGE,"E1671"),sQuery(id+"F0.wireOp",EDGE,"E1672"),sQuery(id+"F0.wireOp",EDGE,"E1673"),sQuery(id+"F0.wireOp",EDGE,"E1674"),sQuery(id+"F0.wireOp",EDGE,"E1675"),sQuery(id+"F0.wireOp",EDGE,"E1676"),sQuery(id+"F0.wireOp",EDGE,"E1677"),sQuery(id+"F0.wireOp",EDGE,"E1678"),sQuery(id+"F0.wireOp",EDGE,"E1679"),sQuery(id+"F0.wireOp",EDGE,"E1680"),sQuery(id+"F0.wireOp",EDGE,"E1681"),sQuery(id+"F0.wireOp",EDGE,"E1682"),sQuery(id+"F0.wireOp",EDGE,"E1683"),sQuery(id+"F0.wireOp",EDGE,"E1684"),sQuery(id+"F0.wireOp",EDGE,"E1685"),sQuery(id+"F0.wireOp",EDGE,"E1686"),sQuery(id+"F0.wireOp",EDGE,"E1687"),sQuery(id+"F0.wireOp",EDGE,"E1688"),sQuery(id+"F0.wireOp",EDGE,"E1689"),sQuery(id+"F0.wireOp",EDGE,"E1690"),sQuery(id+"F0.wireOp",EDGE,"E1691"),sQuery(id+"F0.wireOp",EDGE,"E1692"),sQuery(id+"F0.wireOp",EDGE,"E1693"),sQuery(id+"F0.wireOp",EDGE,"E1694"),sQuery(id+"F0.wireOp",EDGE,"E1695"),sQuery(id+"F0.wireOp",EDGE,"E1696"),sQuery(id+"F0.wireOp",EDGE,"E1697"),sQuery(id+"F0.wireOp",EDGE,"E1698"),sQuery(id+"F0.wireOp",EDGE,"E1699"),sQuery(id+"F0.wireOp",EDGE,"E1700"),sQuery(id+"F0.wireOp",EDGE,"E1701"),sQuery(id+"F0.wireOp",EDGE,"E1702"),sQuery(id+"F0.wireOp",EDGE,"E1703"),sQuery(id+"F0.wireOp",EDGE,"E1704")])],"isStart":true});
            var Q13;
            Q13=makeQuery(id+"F1.opExtrude","CAP_FACE",FACE,{"disambiguationData":[OSD([sQuery(id+"F0.wireOp",EDGE,"E1487"),sQuery(id+"F0.wireOp",EDGE,"E1488"),sQuery(id+"F0.wireOp",EDGE,"E1489"),sQuery(id+"F0.wireOp",EDGE,"E1490"),sQuery(id+"F0.wireOp",EDGE,"E1491"),sQuery(id+"F0.wireOp",EDGE,"E1492"),sQuery(id+"F0.wireOp",EDGE,"E1493"),sQuery(id+"F0.wireOp",EDGE,"E1494"),sQuery(id+"F0.wireOp",EDGE,"E1495"),sQuery(id+"F0.wireOp",EDGE,"E1496"),sQuery(id+"F0.wireOp",EDGE,"E1497"),sQuery(id+"F0.wireOp",EDGE,"E1498"),sQuery(id+"F0.wireOp",EDGE,"E1499"),sQuery(id+"F0.wireOp",EDGE,"E1500"),sQuery(id+"F0.wireOp",EDGE,"E1501"),sQuery(id+"F0.wireOp",EDGE,"E1502"),sQuery(id+"F0.wireOp",EDGE,"E1503"),sQuery(id+"F0.wireOp",EDGE,"E1504"),sQuery(id+"F0.wireOp",EDGE,"E1505"),sQuery(id+"F0.wireOp",EDGE,"E1506"),sQuery(id+"F0.wireOp",EDGE,"E1507"),sQuery(id+"F0.wireOp",EDGE,"E1508"),sQuery(id+"F0.wireOp",EDGE,"E1509"),sQuery(id+"F0.wireOp",EDGE,"E1510"),sQuery(id+"F0.wireOp",EDGE,"E1511"),sQuery(id+"F0.wireOp",EDGE,"E1512"),sQuery(id+"F0.wireOp",EDGE,"E1513"),sQuery(id+"F0.wireOp",EDGE,"E1514"),sQuery(id+"F0.wireOp",EDGE,"E1515"),sQuery(id+"F0.wireOp",EDGE,"E1516"),sQuery(id+"F0.wireOp",EDGE,"E1517"),sQuery(id+"F0.wireOp",EDGE,"E1518"),sQuery(id+"F0.wireOp",EDGE,"E1519"),sQuery(id+"F0.wireOp",EDGE,"E1520"),sQuery(id+"F0.wireOp",EDGE,"E1521"),sQuery(id+"F0.wireOp",EDGE,"E1522"),sQuery(id+"F0.wireOp",EDGE,"E1523"),sQuery(id+"F0.wireOp",EDGE,"E1524"),sQuery(id+"F0.wireOp",EDGE,"E1525"),sQuery(id+"F0.wireOp",EDGE,"E1526"),sQuery(id+"F0.wireOp",EDGE,"E1527"),sQuery(id+"F0.wireOp",EDGE,"E1528"),sQuery(id+"F0.wireOp",EDGE,"E1529"),sQuery(id+"F0.wireOp",EDGE,"E1530"),sQuery(id+"F0.wireOp",EDGE,"E1531"),sQuery(id+"F0.wireOp",EDGE,"E1532"),sQuery(id+"F0.wireOp",EDGE,"E1533"),sQuery(id+"F0.wireOp",EDGE,"E1534"),sQuery(id+"F0.wireOp",EDGE,"E1535"),sQuery(id+"F0.wireOp",EDGE,"E1536"),sQuery(id+"F0.wireOp",EDGE,"E1537"),sQuery(id+"F0.wireOp",EDGE,"E1538"),sQuery(id+"F0.wireOp",EDGE,"E1539"),sQuery(id+"F0.wireOp",EDGE,"E1540"),sQuery(id+"F0.wireOp",EDGE,"E1541"),sQuery(id+"F0.wireOp",EDGE,"E1542"),sQuery(id+"F0.wireOp",EDGE,"E1543"),sQuery(id+"F0.wireOp",EDGE,"E1544"),sQuery(id+"F0.wireOp",EDGE,"E1545"),sQuery(id+"F0.wireOp",EDGE,"E1546"),sQuery(id+"F0.wireOp",EDGE,"E1547"),sQuery(id+"F0.wireOp",EDGE,"E1548")])],"isStart":true});
            var Q14;
            Q14=makeQuery(id+"F1.opExtrude","CAP_FACE",FACE,{"disambiguationData":[OSD([sQuery(id+"F0.wireOp",EDGE,"E1705"),sQuery(id+"F0.wireOp",EDGE,"E1706"),sQuery(id+"F0.wireOp",EDGE,"E1707"),sQuery(id+"F0.wireOp",EDGE,"E1708"),sQuery(id+"F0.wireOp",EDGE,"E1709"),sQuery(id+"F0.wireOp",EDGE,"E1710"),sQuery(id+"F0.wireOp",EDGE,"E1711"),sQuery(id+"F0.wireOp",EDGE,"E1712"),sQuery(id+"F0.wireOp",EDGE,"E1713"),sQuery(id+"F0.wireOp",EDGE,"E1714"),sQuery(id+"F0.wireOp",EDGE,"E1715"),sQuery(id+"F0.wireOp",EDGE,"E1716"),sQuery(id+"F0.wireOp",EDGE,"E1717"),sQuery(id+"F0.wireOp",EDGE,"E1718"),sQuery(id+"F0.wireOp",EDGE,"E1719"),sQuery(id+"F0.wireOp",EDGE,"E1720"),sQuery(id+"F0.wireOp",EDGE,"E1721"),sQuery(id+"F0.wireOp",EDGE,"E1722"),sQuery(id+"F0.wireOp",EDGE,"E1723"),sQuery(id+"F0.wireOp",EDGE,"E1724"),sQuery(id+"F0.wireOp",EDGE,"E1725"),sQuery(id+"F0.wireOp",EDGE,"E1726"),sQuery(id+"F0.wireOp",EDGE,"E1727"),sQuery(id+"F0.wireOp",EDGE,"E1728"),sQuery(id+"F0.wireOp",EDGE,"E1729"),sQuery(id+"F0.wireOp",EDGE,"E1730"),sQuery(id+"F0.wireOp",EDGE,"E1731"),sQuery(id+"F0.wireOp",EDGE,"E1732"),sQuery(id+"F0.wireOp",EDGE,"E1733"),sQuery(id+"F0.wireOp",EDGE,"E1734"),sQuery(id+"F0.wireOp",EDGE,"E1735"),sQuery(id+"F0.wireOp",EDGE,"E1736"),sQuery(id+"F0.wireOp",EDGE,"E1737"),sQuery(id+"F0.wireOp",EDGE,"E1738"),sQuery(id+"F0.wireOp",EDGE,"E1739"),sQuery(id+"F0.wireOp",EDGE,"E1740"),sQuery(id+"F0.wireOp",EDGE,"E1741"),sQuery(id+"F0.wireOp",EDGE,"E1742"),sQuery(id+"F0.wireOp",EDGE,"E1743"),sQuery(id+"F0.wireOp",EDGE,"E1744"),sQuery(id+"F0.wireOp",EDGE,"E1745"),sQuery(id+"F0.wireOp",EDGE,"E1746"),sQuery(id+"F0.wireOp",EDGE,"E1747"),sQuery(id+"F0.wireOp",EDGE,"E1748"),sQuery(id+"F0.wireOp",EDGE,"E1749"),sQuery(id+"F0.wireOp",EDGE,"E1750"),sQuery(id+"F0.wireOp",EDGE,"E1751"),sQuery(id+"F0.wireOp",EDGE,"E1752"),sQuery(id+"F0.wireOp",EDGE,"E1753"),sQuery(id+"F0.wireOp",EDGE,"E1754"),sQuery(id+"F0.wireOp",EDGE,"E1755"),sQuery(id+"F0.wireOp",EDGE,"E1756"),sQuery(id+"F0.wireOp",EDGE,"E1757"),sQuery(id+"F0.wireOp",EDGE,"E1758"),sQuery(id+"F0.wireOp",EDGE,"E1759"),sQuery(id+"F0.wireOp",EDGE,"E1760"),sQuery(id+"F0.wireOp",EDGE,"E1761"),sQuery(id+"F0.wireOp",EDGE,"E1762"),sQuery(id+"F0.wireOp",EDGE,"E1763"),sQuery(id+"F0.wireOp",EDGE,"E1764")])],"isStart":true});
            var Q15;
            Q15=makeQuery(id+"F1.opExtrude","CAP_FACE",FACE,{"disambiguationData":[OSD([sQuery(id+"F0.wireOp",EDGE,"E1765"),sQuery(id+"F0.wireOp",EDGE,"E1766"),sQuery(id+"F0.wireOp",EDGE,"E1767"),sQuery(id+"F0.wireOp",EDGE,"E1768"),sQuery(id+"F0.wireOp",EDGE,"E1769"),sQuery(id+"F0.wireOp",EDGE,"E1770"),sQuery(id+"F0.wireOp",EDGE,"E1771"),sQuery(id+"F0.wireOp",EDGE,"E1772"),sQuery(id+"F0.wireOp",EDGE,"E1773"),sQuery(id+"F0.wireOp",EDGE,"E1774"),sQuery(id+"F0.wireOp",EDGE,"E1775"),sQuery(id+"F0.wireOp",EDGE,"E1776"),sQuery(id+"F0.wireOp",EDGE,"E1777"),sQuery(id+"F0.wireOp",EDGE,"E1778"),sQuery(id+"F0.wireOp",EDGE,"E1779"),sQuery(id+"F0.wireOp",EDGE,"E1780"),sQuery(id+"F0.wireOp",EDGE,"E1781"),sQuery(id+"F0.wireOp",EDGE,"E1782"),sQuery(id+"F0.wireOp",EDGE,"E1783"),sQuery(id+"F0.wireOp",EDGE,"E1784"),sQuery(id+"F0.wireOp",EDGE,"E1785"),sQuery(id+"F0.wireOp",EDGE,"E1786"),sQuery(id+"F0.wireOp",EDGE,"E1787"),sQuery(id+"F0.wireOp",EDGE,"E1788"),sQuery(id+"F0.wireOp",EDGE,"E1789"),sQuery(id+"F0.wireOp",EDGE,"E1790"),sQuery(id+"F0.wireOp",EDGE,"E1791"),sQuery(id+"F0.wireOp",EDGE,"E1792"),sQuery(id+"F0.wireOp",EDGE,"E1793"),sQuery(id+"F0.wireOp",EDGE,"E1794"),sQuery(id+"F0.wireOp",EDGE,"E1795"),sQuery(id+"F0.wireOp",EDGE,"E1796"),sQuery(id+"F0.wireOp",EDGE,"E1797"),sQuery(id+"F0.wireOp",EDGE,"E1798"),sQuery(id+"F0.wireOp",EDGE,"E1799"),sQuery(id+"F0.wireOp",EDGE,"E1800"),sQuery(id+"F0.wireOp",EDGE,"E1801"),sQuery(id+"F0.wireOp",EDGE,"E1802"),sQuery(id+"F0.wireOp",EDGE,"E1803"),sQuery(id+"F0.wireOp",EDGE,"E1804"),sQuery(id+"F0.wireOp",EDGE,"E1805"),sQuery(id+"F0.wireOp",EDGE,"E1806"),sQuery(id+"F0.wireOp",EDGE,"E1807"),sQuery(id+"F0.wireOp",EDGE,"E1808")])],"isStart":true});
            var Q16;
            Q16=makeQuery(id+"F1.opExtrude","CAP_FACE",FACE,{"disambiguationData":[OSD([sQuery(id+"F0.wireOp",EDGE,"E1905"),sQuery(id+"F0.wireOp",EDGE,"E1906"),sQuery(id+"F0.wireOp",EDGE,"E1907"),sQuery(id+"F0.wireOp",EDGE,"E1908"),sQuery(id+"F0.wireOp",EDGE,"E1909"),sQuery(id+"F0.wireOp",EDGE,"E1910"),sQuery(id+"F0.wireOp",EDGE,"E1911"),sQuery(id+"F0.wireOp",EDGE,"E1912"),sQuery(id+"F0.wireOp",EDGE,"E1913"),sQuery(id+"F0.wireOp",EDGE,"E1914"),sQuery(id+"F0.wireOp",EDGE,"E1915"),sQuery(id+"F0.wireOp",EDGE,"E1916"),sQuery(id+"F0.wireOp",EDGE,"E1917"),sQuery(id+"F0.wireOp",EDGE,"E1918"),sQuery(id+"F0.wireOp",EDGE,"E1919"),sQuery(id+"F0.wireOp",EDGE,"E1920"),sQuery(id+"F0.wireOp",EDGE,"E1921"),sQuery(id+"F0.wireOp",EDGE,"E1922"),sQuery(id+"F0.wireOp",EDGE,"E1923"),sQuery(id+"F0.wireOp",EDGE,"E1924"),sQuery(id+"F0.wireOp",EDGE,"E1925"),sQuery(id+"F0.wireOp",EDGE,"E1926"),sQuery(id+"F0.wireOp",EDGE,"E1927"),sQuery(id+"F0.wireOp",EDGE,"E1928"),sQuery(id+"F0.wireOp",EDGE,"E1929"),sQuery(id+"F0.wireOp",EDGE,"E1930"),sQuery(id+"F0.wireOp",EDGE,"E1931"),sQuery(id+"F0.wireOp",EDGE,"E1932"),sQuery(id+"F0.wireOp",EDGE,"E1933"),sQuery(id+"F0.wireOp",EDGE,"E1934"),sQuery(id+"F0.wireOp",EDGE,"E1935"),sQuery(id+"F0.wireOp",EDGE,"E1936"),sQuery(id+"F0.wireOp",EDGE,"E1937"),sQuery(id+"F0.wireOp",EDGE,"E1938"),sQuery(id+"F0.wireOp",EDGE,"E1939"),sQuery(id+"F0.wireOp",EDGE,"E1940"),sQuery(id+"F0.wireOp",EDGE,"E1941"),sQuery(id+"F0.wireOp",EDGE,"E1942"),sQuery(id+"F0.wireOp",EDGE,"E1943"),sQuery(id+"F0.wireOp",EDGE,"E1944"),sQuery(id+"F0.wireOp",EDGE,"E1945"),sQuery(id+"F0.wireOp",EDGE,"E1946"),sQuery(id+"F0.wireOp",EDGE,"E1947"),sQuery(id+"F0.wireOp",EDGE,"E1948"),sQuery(id+"F0.wireOp",EDGE,"E1949"),sQuery(id+"F0.wireOp",EDGE,"E1950"),sQuery(id+"F0.wireOp",EDGE,"E1951"),sQuery(id+"F0.wireOp",EDGE,"E1952"),sQuery(id+"F0.wireOp",EDGE,"E1953"),sQuery(id+"F0.wireOp",EDGE,"E1954"),sQuery(id+"F0.wireOp",EDGE,"E1955"),sQuery(id+"F0.wireOp",EDGE,"E1956"),sQuery(id+"F0.wireOp",EDGE,"E1957"),sQuery(id+"F0.wireOp",EDGE,"E1958"),sQuery(id+"F0.wireOp",EDGE,"E1959"),sQuery(id+"F0.wireOp",EDGE,"E1960"),sQuery(id+"F0.wireOp",EDGE,"E1961"),sQuery(id+"F0.wireOp",EDGE,"E1962"),sQuery(id+"F0.wireOp",EDGE,"E1963"),sQuery(id+"F0.wireOp",EDGE,"E1964")])],"isStart":true});
            var Q17;
            Q17=makeQuery(id+"F1.opExtrude","CAP_FACE",FACE,{"disambiguationData":[OSD([sQuery(id+"F0.wireOp",EDGE,"E1965"),sQuery(id+"F0.wireOp",EDGE,"E1966"),sQuery(id+"F0.wireOp",EDGE,"E1967"),sQuery(id+"F0.wireOp",EDGE,"E1968"),sQuery(id+"F0.wireOp",EDGE,"E1969"),sQuery(id+"F0.wireOp",EDGE,"E1970"),sQuery(id+"F0.wireOp",EDGE,"E1971"),sQuery(id+"F0.wireOp",EDGE,"E1972"),sQuery(id+"F0.wireOp",EDGE,"E1973"),sQuery(id+"F0.wireOp",EDGE,"E1974"),sQuery(id+"F0.wireOp",EDGE,"E1975"),sQuery(id+"F0.wireOp",EDGE,"E1976"),sQuery(id+"F0.wireOp",EDGE,"E1977"),sQuery(id+"F0.wireOp",EDGE,"E1978"),sQuery(id+"F0.wireOp",EDGE,"E1979"),sQuery(id+"F0.wireOp",EDGE,"E1980"),sQuery(id+"F0.wireOp",EDGE,"E1981"),sQuery(id+"F0.wireOp",EDGE,"E1982"),sQuery(id+"F0.wireOp",EDGE,"E1983"),sQuery(id+"F0.wireOp",EDGE,"E1984"),sQuery(id+"F0.wireOp",EDGE,"E1985"),sQuery(id+"F0.wireOp",EDGE,"E1986"),sQuery(id+"F0.wireOp",EDGE,"E1987"),sQuery(id+"F0.wireOp",EDGE,"E1988"),sQuery(id+"F0.wireOp",EDGE,"E1989"),sQuery(id+"F0.wireOp",EDGE,"E1990"),sQuery(id+"F0.wireOp",EDGE,"E1991"),sQuery(id+"F0.wireOp",EDGE,"E1992"),sQuery(id+"F0.wireOp",EDGE,"E1993"),sQuery(id+"F0.wireOp",EDGE,"E1994"),sQuery(id+"F0.wireOp",EDGE,"E1995"),sQuery(id+"F0.wireOp",EDGE,"E1996"),sQuery(id+"F0.wireOp",EDGE,"E1997"),sQuery(id+"F0.wireOp",EDGE,"E1998"),sQuery(id+"F0.wireOp",EDGE,"E1999"),sQuery(id+"F0.wireOp",EDGE,"E2000"),sQuery(id+"F0.wireOp",EDGE,"E2001"),sQuery(id+"F0.wireOp",EDGE,"E2002"),sQuery(id+"F0.wireOp",EDGE,"E2003"),sQuery(id+"F0.wireOp",EDGE,"E2004"),sQuery(id+"F0.wireOp",EDGE,"E2005"),sQuery(id+"F0.wireOp",EDGE,"E2006"),sQuery(id+"F0.wireOp",EDGE,"E2007"),sQuery(id+"F0.wireOp",EDGE,"E2008"),sQuery(id+"F0.wireOp",EDGE,"E2009"),sQuery(id+"F0.wireOp",EDGE,"E2010"),sQuery(id+"F0.wireOp",EDGE,"E2011"),sQuery(id+"F0.wireOp",EDGE,"E2012"),sQuery(id+"F0.wireOp",EDGE,"E2013"),sQuery(id+"F0.wireOp",EDGE,"E2014"),sQuery(id+"F0.wireOp",EDGE,"E2015"),sQuery(id+"F0.wireOp",EDGE,"E2016"),sQuery(id+"F0.wireOp",EDGE,"E2017"),sQuery(id+"F0.wireOp",EDGE,"E2018"),sQuery(id+"F0.wireOp",EDGE,"E2019"),sQuery(id+"F0.wireOp",EDGE,"E2020"),sQuery(id+"F0.wireOp",EDGE,"E2021"),sQuery(id+"F0.wireOp",EDGE,"E2022"),sQuery(id+"F0.wireOp",EDGE,"E2023"),sQuery(id+"F0.wireOp",EDGE,"E2024"),sQuery(id+"F0.wireOp",EDGE,"E2025"),sQuery(id+"F0.wireOp",EDGE,"E2026")])],"isStart":true});
            var Q18;
            Q18=makeQuery(id+"F1.opExtrude","CAP_FACE",FACE,{"disambiguationData":[OSD([sQuery(id+"F0.wireOp",EDGE,"E2027"),sQuery(id+"F0.wireOp",EDGE,"E2028"),sQuery(id+"F0.wireOp",EDGE,"E2029"),sQuery(id+"F0.wireOp",EDGE,"E2030"),sQuery(id+"F0.wireOp",EDGE,"E2031"),sQuery(id+"F0.wireOp",EDGE,"E2032"),sQuery(id+"F0.wireOp",EDGE,"E2033"),sQuery(id+"F0.wireOp",EDGE,"E2034"),sQuery(id+"F0.wireOp",EDGE,"E2035"),sQuery(id+"F0.wireOp",EDGE,"E2036"),sQuery(id+"F0.wireOp",EDGE,"E2037"),sQuery(id+"F0.wireOp",EDGE,"E2038"),sQuery(id+"F0.wireOp",EDGE,"E2039"),sQuery(id+"F0.wireOp",EDGE,"E2040"),sQuery(id+"F0.wireOp",EDGE,"E2041"),sQuery(id+"F0.wireOp",EDGE,"E2042"),sQuery(id+"F0.wireOp",EDGE,"E2043"),sQuery(id+"F0.wireOp",EDGE,"E2044"),sQuery(id+"F0.wireOp",EDGE,"E2045"),sQuery(id+"F0.wireOp",EDGE,"E2046"),sQuery(id+"F0.wireOp",EDGE,"E2047"),sQuery(id+"F0.wireOp",EDGE,"E2048"),sQuery(id+"F0.wireOp",EDGE,"E2049"),sQuery(id+"F0.wireOp",EDGE,"E2050"),sQuery(id+"F0.wireOp",EDGE,"E2051"),sQuery(id+"F0.wireOp",EDGE,"E2052"),sQuery(id+"F0.wireOp",EDGE,"E2053"),sQuery(id+"F0.wireOp",EDGE,"E2054"),sQuery(id+"F0.wireOp",EDGE,"E2055"),sQuery(id+"F0.wireOp",EDGE,"E2056"),sQuery(id+"F0.wireOp",EDGE,"E2057"),sQuery(id+"F0.wireOp",EDGE,"E2058"),sQuery(id+"F0.wireOp",EDGE,"E2059"),sQuery(id+"F0.wireOp",EDGE,"E2060"),sQuery(id+"F0.wireOp",EDGE,"E2061"),sQuery(id+"F0.wireOp",EDGE,"E2062"),sQuery(id+"F0.wireOp",EDGE,"E2063"),sQuery(id+"F0.wireOp",EDGE,"E2064"),sQuery(id+"F0.wireOp",EDGE,"E2065"),sQuery(id+"F0.wireOp",EDGE,"E2066"),sQuery(id+"F0.wireOp",EDGE,"E2067"),sQuery(id+"F0.wireOp",EDGE,"E2068"),sQuery(id+"F0.wireOp",EDGE,"E2069"),sQuery(id+"F0.wireOp",EDGE,"E2070")])],"isStart":true});
            var Q19;
            Q19=makeQuery(id+"F1.opExtrude","CAP_FACE",FACE,{"disambiguationData":[OSD([sQuery(id+"F0.wireOp",EDGE,"E1809"),sQuery(id+"F0.wireOp",EDGE,"E1810"),sQuery(id+"F0.wireOp",EDGE,"E1811"),sQuery(id+"F0.wireOp",EDGE,"E1812"),sQuery(id+"F0.wireOp",EDGE,"E1813"),sQuery(id+"F0.wireOp",EDGE,"E1814"),sQuery(id+"F0.wireOp",EDGE,"E1815"),sQuery(id+"F0.wireOp",EDGE,"E1816"),sQuery(id+"F0.wireOp",EDGE,"E1817"),sQuery(id+"F0.wireOp",EDGE,"E1818"),sQuery(id+"F0.wireOp",EDGE,"E1819"),sQuery(id+"F0.wireOp",EDGE,"E1820"),sQuery(id+"F0.wireOp",EDGE,"E1821"),sQuery(id+"F0.wireOp",EDGE,"E1822"),sQuery(id+"F0.wireOp",EDGE,"E1823"),sQuery(id+"F0.wireOp",EDGE,"E1824"),sQuery(id+"F0.wireOp",EDGE,"E1825"),sQuery(id+"F0.wireOp",EDGE,"E1826"),sQuery(id+"F0.wireOp",EDGE,"E1827"),sQuery(id+"F0.wireOp",EDGE,"E1828"),sQuery(id+"F0.wireOp",EDGE,"E1829"),sQuery(id+"F0.wireOp",EDGE,"E1830"),sQuery(id+"F0.wireOp",EDGE,"E1831"),sQuery(id+"F0.wireOp",EDGE,"E1832"),sQuery(id+"F0.wireOp",EDGE,"E1833"),sQuery(id+"F0.wireOp",EDGE,"E1834"),sQuery(id+"F0.wireOp",EDGE,"E1835"),sQuery(id+"F0.wireOp",EDGE,"E1836"),sQuery(id+"F0.wireOp",EDGE,"E1837"),sQuery(id+"F0.wireOp",EDGE,"E1838"),sQuery(id+"F0.wireOp",EDGE,"E1839"),sQuery(id+"F0.wireOp",EDGE,"E1840"),sQuery(id+"F0.wireOp",EDGE,"E1841"),sQuery(id+"F0.wireOp",EDGE,"E1842"),sQuery(id+"F0.wireOp",EDGE,"E1843"),sQuery(id+"F0.wireOp",EDGE,"E1844"),sQuery(id+"F0.wireOp",EDGE,"E1845"),sQuery(id+"F0.wireOp",EDGE,"E1846"),sQuery(id+"F0.wireOp",EDGE,"E1847"),sQuery(id+"F0.wireOp",EDGE,"E1848"),sQuery(id+"F0.wireOp",EDGE,"E1849"),sQuery(id+"F0.wireOp",EDGE,"E1850"),sQuery(id+"F0.wireOp",EDGE,"E1851"),sQuery(id+"F0.wireOp",EDGE,"E1852"),sQuery(id+"F0.wireOp",EDGE,"E1853"),sQuery(id+"F0.wireOp",EDGE,"E1854"),sQuery(id+"F0.wireOp",EDGE,"E1855"),sQuery(id+"F0.wireOp",EDGE,"E1856"),sQuery(id+"F0.wireOp",EDGE,"E1857"),sQuery(id+"F0.wireOp",EDGE,"E1858"),sQuery(id+"F0.wireOp",EDGE,"E1859"),sQuery(id+"F0.wireOp",EDGE,"E1860"),sQuery(id+"F0.wireOp",EDGE,"E1861"),sQuery(id+"F0.wireOp",EDGE,"E1862"),sQuery(id+"F0.wireOp",EDGE,"E1863"),sQuery(id+"F0.wireOp",EDGE,"E1864"),sQuery(id+"F0.wireOp",EDGE,"E1865"),sQuery(id+"F0.wireOp",EDGE,"E1866"),sQuery(id+"F0.wireOp",EDGE,"E1867"),sQuery(id+"F0.wireOp",EDGE,"E1868"),sQuery(id+"F0.wireOp",EDGE,"E1869"),sQuery(id+"F0.wireOp",EDGE,"E1870"),sQuery(id+"F0.wireOp",EDGE,"E1871"),sQuery(id+"F0.wireOp",EDGE,"E1872"),sQuery(id+"F0.wireOp",EDGE,"E1873"),sQuery(id+"F0.wireOp",EDGE,"E1874"),sQuery(id+"F0.wireOp",EDGE,"E1875"),sQuery(id+"F0.wireOp",EDGE,"E1876"),sQuery(id+"F0.wireOp",EDGE,"E1877"),sQuery(id+"F0.wireOp",EDGE,"E1878"),sQuery(id+"F0.wireOp",EDGE,"E1879"),sQuery(id+"F0.wireOp",EDGE,"E1880"),sQuery(id+"F0.wireOp",EDGE,"E1881"),sQuery(id+"F0.wireOp",EDGE,"E1882"),sQuery(id+"F0.wireOp",EDGE,"E1883"),sQuery(id+"F0.wireOp",EDGE,"E1884"),sQuery(id+"F0.wireOp",EDGE,"E1885"),sQuery(id+"F0.wireOp",EDGE,"E1886"),sQuery(id+"F0.wireOp",EDGE,"E1887"),sQuery(id+"F0.wireOp",EDGE,"E1888"),sQuery(id+"F0.wireOp",EDGE,"E1889"),sQuery(id+"F0.wireOp",EDGE,"E1890"),sQuery(id+"F0.wireOp",EDGE,"E1891"),sQuery(id+"F0.wireOp",EDGE,"E1892"),sQuery(id+"F0.wireOp",EDGE,"E1893"),sQuery(id+"F0.wireOp",EDGE,"E1894"),sQuery(id+"F0.wireOp",EDGE,"E1895"),sQuery(id+"F0.wireOp",EDGE,"E1896"),sQuery(id+"F0.wireOp",EDGE,"E1897"),sQuery(id+"F0.wireOp",EDGE,"E1898"),sQuery(id+"F0.wireOp",EDGE,"E1899"),sQuery(id+"F0.wireOp",EDGE,"E1900"),sQuery(id+"F0.wireOp",EDGE,"E1901"),sQuery(id+"F0.wireOp",EDGE,"E1902"),sQuery(id+"F0.wireOp",EDGE,"E1903"),sQuery(id+"F0.wireOp",EDGE,"E1904")])],"isStart":true});
            shell(context, id + "F2", {"entities" : qUnion([Q0, Q1, Q2, Q3, Q4, Q5, Q6, Q7, Q8, Q9, Q10, Q11, Q12, Q13, Q14, Q15, Q16, Q17, Q18, Q19]), "thickness" : 0.5 * mm});
        }
        {
            var Q0;
            Q0=makeQuery(id+"F0.imprint","IMPRINT",FACE,{"disambiguationData":[TD([[makeQuery(id+"F0.imprint","IMPRINT",EDGE,{"derivedFrom":sQuery(id+"F0.wireOp",EDGE,"E2071")}),-1.0]])]});
            var Q1;
            Q1=makeQuery(id+"F0.imprint","IMPRINT",FACE,{"disambiguationData":[TD([[makeQuery(id+"F0.imprint","IMPRINT",EDGE,{"derivedFrom":sQuery(id+"F0.wireOp",EDGE,"E2157")}),-1.0]])]});
            var Q2;
            Q2=makeQuery(id+"F0.imprint","IMPRINT",FACE,{"disambiguationData":[TD([[makeQuery(id+"F0.imprint","IMPRINT",EDGE,{"derivedFrom":sQuery(id+"F0.wireOp",EDGE,"E2261")}),-1.0]])]});
            var Q3;
            Q3=makeQuery(id+"F0.imprint","IMPRINT",FACE,{"disambiguationData":[TD([[makeQuery(id+"F0.imprint","IMPRINT",EDGE,{"derivedFrom":sQuery(id+"F0.wireOp",EDGE,"E2251")}),-1.0]])]});
            var Q4;
            Q4=makeQuery(id+"F0.imprint","IMPRINT",FACE,{"disambiguationData":[TD([[makeQuery(id+"F0.imprint","IMPRINT",EDGE,{"derivedFrom":sQuery(id+"F0.wireOp",EDGE,"E2335")}),-1.0]])]});
            var Q5;
            Q5=makeQuery(id+"F0.imprint","IMPRINT",FACE,{"disambiguationData":[TD([[makeQuery(id+"F0.imprint","IMPRINT",EDGE,{"derivedFrom":sQuery(id+"F0.wireOp",EDGE,"E2640")}),-1.0]])]});
            var Q6;
            Q6=makeQuery(id+"F0.imprint","IMPRINT",FACE,{"disambiguationData":[TD([[makeQuery(id+"F0.imprint","IMPRINT",EDGE,{"derivedFrom":sQuery(id+"F0.wireOp",EDGE,"E2731")}),-1.0]])]});
            var Q7;
            Q7=makeQuery(id+"F0.imprint","IMPRINT",FACE,{"disambiguationData":[TD([[makeQuery(id+"F0.imprint","IMPRINT",EDGE,{"derivedFrom":sQuery(id+"F0.wireOp",EDGE,"E2821")}),-1.0]])]});
            var Q8;
            Q8=makeQuery(id+"F0.imprint","IMPRINT",FACE,{"disambiguationData":[TD([[makeQuery(id+"F0.imprint","IMPRINT",EDGE,{"derivedFrom":sQuery(id+"F0.wireOp",EDGE,"E3161")}),-1.0]])]});
            extrude(context, id + "F3", {"entities" : qUnion([Q0, Q1, Q2, Q3, Q4, Q5, Q6, Q7, Q8]), "operationType" : NewBodyOperationType.REMOVE, "endBound" : BoundingType.THROUGH_ALL, "depth" : 25.4 * mm, "offsetDistance" : 25.4 * mm});
        }
    });
